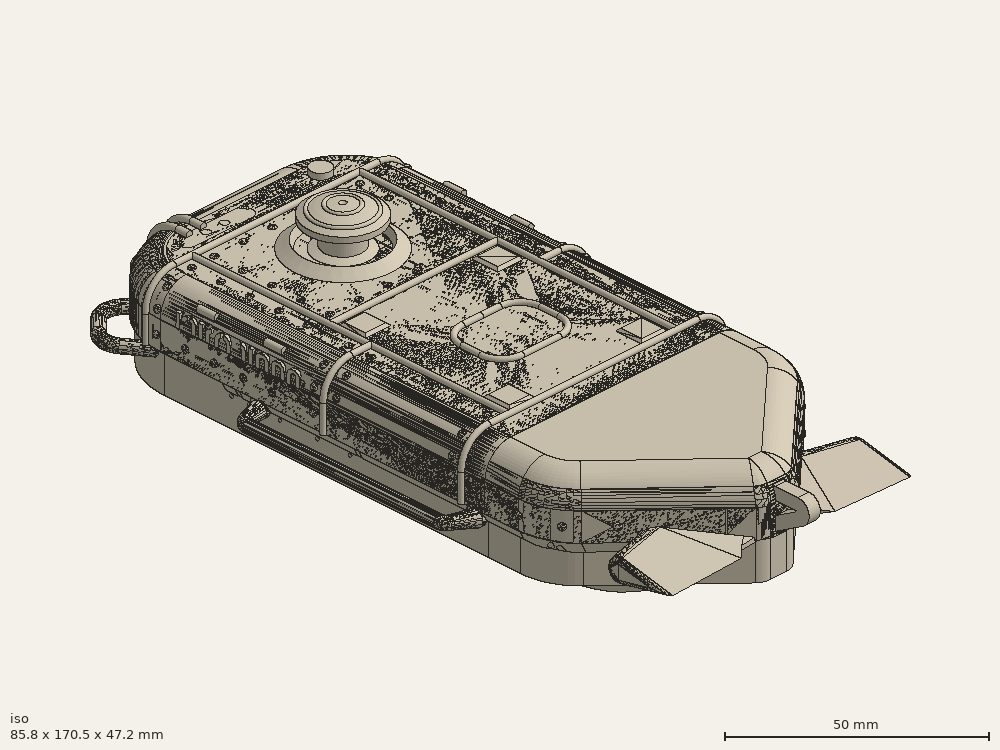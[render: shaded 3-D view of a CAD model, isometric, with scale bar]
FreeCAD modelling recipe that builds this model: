
FCSTD DOCUMENT  (FreeCAD 2022.709R26244 +5001 (Git))
Label: cq-80
License: All rights reserved
LicenseURL: http://en.wikipedia.org/wiki/All_rights_reserved
objects: Sketcher::SketchObject×173, PartDesign::Body×90, PartDesign::SubShapeBinder×79, PartDesign::Plane×57, PartDesign::Pad×45, Part::SubShapeBinder×44, PartDesign::ShapeBinder×41, PartDesign::FeatureBase×32, PartDesign::Pocket×29, PartDesign::Fillet×22, PartDesign::AdditivePipe×21, PartDesign::LinearPattern×16, PartDesign::Boolean×16, PartDesign::Mirrored×15, App::Part×14, PartDesign::MultiTransform×12, PartDesign::Line×12, Part::MultiFuse×11, PartDesign::Revolution×10, Part::Cut×8, +12 more types
note: 1204 computed .brp shape members not serialized (recipe doc carries the construction recipe); baked Part::Feature solids carry a one-line shape summary decoded from their .brp
EXTERNAL_REF file=cq-80-bottom.FCStd obj=Part

FEATURE [Sketcher::SketchObject] Sketch
  ArcFitTolerance = 0
  AttachmentSupport = -> [XY_Plane]
  FullyConstrained = true
  MapMode = 5
  Support = -> [XY_Plane]
  TreeRank = 6
  sketch-geometry (15):
    g0: LineSegment [constr] StartX=-35 StartY=53.5 StartZ=0 EndX=35 EndY=53.5 EndZ=0
    g1: LineSegment [constr] StartX=35 StartY=53.5 StartZ=0 EndX=35 EndY=-53.5 EndZ=0
    g2: LineSegment [constr] StartX=35 StartY=-53.5 StartZ=0 EndX=-35 EndY=-53.5 EndZ=0
    g3: LineSegment [constr] StartX=-35 StartY=-53.5 StartZ=0 EndX=-35 EndY=53.5 EndZ=0
    g4: LineSegment StartX=-35 StartY=-53.5 StartZ=0 EndX=-35 EndY=-69.5 EndZ=0
    g5: LineSegment [constr] StartX=-35 StartY=-69.5 StartZ=0 EndX=35 EndY=-69.5 EndZ=0
    g6: LineSegment StartX=35 StartY=-69.5 StartZ=0 EndX=35 EndY=-53.5 EndZ=0
    g7: LineSegment StartX=-35 StartY=-69.5 StartZ=0 EndX=-4.5 EndY=-97.9417 EndZ=0
    g8: LineSegment StartX=-4.5 StartY=-97.9417 StartZ=0 EndX=4.5 EndY=-97.9417 EndZ=0
    g9: LineSegment StartX=4.5 StartY=-97.9417 StartZ=0 EndX=35 EndY=-69.5 EndZ=0
    g10: LineSegment StartX=-15 StartY=53.5 StartZ=0 EndX=15 EndY=53.5 EndZ=0
    g11: LineSegment StartX=-35 StartY=33.5 StartZ=0 EndX=-35 EndY=-53.5 EndZ=0
    g12: LineSegment StartX=35 StartY=33.5 StartZ=0 EndX=35 EndY=-53.5 EndZ=0
    g13: ArcOfCircle CenterX=15 CenterY=33.5 CenterZ=0 NormalX=0 NormalY=0 NormalZ=1 AngleXU=0 Radius=20 StartAngle=1e-16 EndAngle=1.5708
    g14: ArcOfCircle CenterX=-15 CenterY=33.5 CenterZ=0 NormalX=0 NormalY=0 NormalZ=1 AngleXU=0 Radius=20 StartAngle=1.5708 EndAngle=3.14159
  constraints (39):
    c: Coincident(g0,g1)
    c: Coincident(g1,g2)
    c: Coincident(g2,g3)
    c: Coincident(g3,g0)
    c: Horizontal(g0)
    c: Horizontal(g2)
    c: Vertical(g1)
    c: Vertical(g3)
    c: DistanceX(g0,g0) = 70
    c: DistanceY(g3,g3) = 107
    c: Symmetric(g0,g2,g-1)
    c: Coincident(g2,g4)
    c: Vertical(g4)
    c: Coincident(g4,g5)
    c: Horizontal(g5)
    c: Coincident(g5,g6)
    c: Coincident(g6,g1)
    c: Vertical(g6)
    c: DistanceY(g4,g4) = 16
    c: Coincident(g4,g7)
    c: Coincident(g7,g8)
    c: Horizontal(g8)
    c: Coincident(g8,g9)
    c: Coincident(g9,g5)
    c: DistanceX(g8,g8) = 9
    c: Equal(g9,g7)
    c: Angle(g5,g9) = 0.750492
    c: Coincident(g11,g4)
    c: Coincident(g12,g6)
    c: Tangent(g14,g10) = 1.5708
    c: Tangent(g13,g10) = 1.5708
    c: Tangent(g12,g13) = 1.5708
    c: Tangent(g11,g14) = -1.5708
    c: Vertical(g12)
    c: Vertical(g11)
    c: Horizontal(g10)
    c: Radius(g14) = 20
    c: Radius(g13) = 20
    c: DistanceY(g-1,g10) = 53.5
FEATURE [PartDesign::Pad] Pad
  AddSubType = 0
  CheckUpToFaceLimits = true
  ClaimChildren = false
  Direction = (0,0,1)
  Fit = 0
  FitJoin = 0
  InnerFit = 0
  InnerFitJoin = 0
  InnerTaperAngle = 0
  InnerTaperAngleRev = 0
  Length = 14
  Length2 = 10
  NewSolid = false
  Profile = -> Sketch
  ReferenceAxis = -> Sketch [N_Axis]
  Suppress = false
  TreeRank = 6
  Type = 0
  _ProfileBasedVersion = 0
FEATURE [PartDesign::Fillet] Fillet001
  AddSubType = 0
  Base = -> Pad [Edge11,Edge14]
  BaseFeature = -> Pad
  NewSolid = false
  Radius = 4
  SupportTransform = false
  Suppress = false
  TreeRank = 6
FEATURE [PartDesign::Fillet] Fillet002
  AddSubType = 0
  Base = -> Fillet001 [Edge33,Edge3]
  BaseFeature = -> Fillet001
  NewSolid = false
  Radius = 16
  SupportTransform = false
  Suppress = false
  TreeRank = 6
FEATURE [PartDesign::Fillet] Fillet
  AddSubType = 0
  Base = -> Fillet002 [Face5]
  BaseFeature = -> Fillet002
  NewSolid = false
  Radius = 7
  SupportTransform = false
  Suppress = false
  TreeRank = 6
FEATURE [PartDesign::SubShapeBinder] Binder
  BindCopyOnChange = 0
  BindMode = 0
  ClaimChildren = false
  Context = -> Part [Part012.Body005.Binder.]
  FillStyle = 0
  Fuse = false
  MakeFace = true
  OffsetFill = false
  OffsetIntersection = false
  OffsetJoinType = 0
  OffsetOpenResult = false
  PartialLoad = false
  Relative = true
  Support = -> [Sketch]
  TreeRank = 6
  _Version = 2
FEATURE [PartDesign::SubShapeBinder] Binder004  label="Binder004(Fillet)..."
  BindCopyOnChange = 0
  BindMode = 0
  ClaimChildren = false
  Context = -> Part [Part012.Body006.Binder004.]
  FillStyle = 0
  Fuse = false
  MakeFace = true
  OffsetFill = false
  OffsetIntersection = false
  OffsetJoinType = 0
  OffsetOpenResult = false
  PartialLoad = false
  Relative = true
  Support = -> [Fillet[Edge67,Edge60]]
  TreeRank = 29
  _Version = 8
FEATURE [Sketcher::SketchObject] Sketch012
  ArcFitTolerance = 1e-06
  AttachmentSupport = -> [XY_Plane006]
  ExternalGeometry = -> [Binder004]
  FullyConstrained = true
  MapMode = 5
  Support = -> [XY_Plane006]
  TreeRank = 30
  sketch-geometry (2):
    g0: LineSegment StartX=-35 StartY=-53.5 StartZ=0 EndX=-35 EndY=-47.5 EndZ=0
    g1: LineSegment StartX=35 StartY=-53.5 StartZ=0 EndX=35 EndY=-47.5 EndZ=0
  constraints (6):
    c: Coincident(g0,g-3)
    c: Vertical(g0)
    c: DistanceY(g0,g0) = 6
    c: Coincident(g1,g-4)
    c: Vertical(g1)
    c: Equal(g1,g0)
FEATURE [PartDesign::Plane] DatumPlane001
  AttachmentSupport = -> [Sketch012]
  Length = 35
  MapMode = 7
  MinimumLength = 10
  MinimumWidth = 10
  Placement = pos=(-35,-53.5,0) rot=(1,0,0;1.5708rad)
  ResizeMode = 0
  Support = -> [Sketch012]
  TreeRank = 31
  Width = 10
FEATURE [PartDesign::SubShapeBinder] Binder005  label="Binder005(Sketch013)..."
  BindCopyOnChange = 0
  BindMode = 0
  ClaimChildren = false
  Context = -> Part [Part012.Body007.Binder005.]
  FillStyle = 0
  Fuse = false
  MakeFace = true
  OffsetFill = false
  OffsetIntersection = false
  OffsetJoinType = 0
  OffsetOpenResult = false
  PartialLoad = false
  Relative = true
  Support = -> [Body006[Sketch013.Edge5,Sketch013.Edge4,Sketch013.Edge3,Sketch013.Edge2,Sketch013.Edge1]]
  TreeRank = 47
  _Version = 8
FEATURE [Sketcher::SketchObject] Sketch015
  ArcFitTolerance = 1e-06
  AttachmentSupport = -> [XY_Plane007]
  ExternalGeometry = -> [Binder005]
  FullyConstrained = true
  MapMode = 5
  Support = -> [XY_Plane007]
  TreeRank = 48
  sketch-geometry (1):
    g0: LineSegment StartX=-35 StartY=-47.5 StartZ=0 EndX=-35 EndY=-10.5 EndZ=0
  constraints (3):
    c: Coincident(g0,g-3)
    c: Vertical(g0)
    c: DistanceY(g0,g0) = 37
FEATURE [PartDesign::Plane] DatumPlane002
  AttachmentSupport = -> [Sketch015]
  Length = 71.8
  MapMode = 7
  MinimumLength = 10
  MinimumWidth = 10
  Placement = pos=(-35,-10.5,0) rot=(1,0,0;1.5708rad)
  ResizeMode = 0
  Support = -> [Sketch015]
  TreeRank = 49
  Width = 14.9
FEATURE [Sketcher::SketchObject] Sketch016
  ArcFitTolerance = 1e-06
  AttachmentSupport = -> [DatumPlane002]
  ExternalGeometry = -> [Binder005]
  FullyConstrained = true
  MapMode = 5
  Placement = pos=(-35,-10.5,0) rot=(1,0,0;1.5708rad)
  Support = -> [DatumPlane002]
  TreeRank = 50
  sketch-geometry (8):
    g0: LineSegment StartX=0 StartY=0 StartZ=0 EndX=0 EndY=7 EndZ=0
    g1: LineSegment StartX=70 StartY=0 StartZ=0 EndX=70 EndY=7 EndZ=0
    g2: LineSegment [constr] StartX=63 StartY=14 StartZ=0 EndX=7 EndY=14 EndZ=0
    g3: ArcOfCircle CenterX=7 CenterY=7 CenterZ=0 NormalX=0 NormalY=0 NormalZ=1 AngleXU=0 Radius=7 StartAngle=1.5708 EndAngle=3.14159
    g4: ArcOfCircle CenterX=63 CenterY=7 CenterZ=0 NormalX=0 NormalY=0 NormalZ=1 AngleXU=0 Radius=7 StartAngle=1e-16 EndAngle=1.5708
    g5: LineSegment StartX=7 StartY=14 StartZ=0 EndX=12.5 EndY=14 EndZ=0
    g6: LineSegment StartX=57.5 StartY=14 StartZ=0 EndX=63 EndY=14 EndZ=0
    g7: LineSegment [constr] StartX=12.5 StartY=14 StartZ=0 EndX=57.5 EndY=14 EndZ=0
  constraints (21):
    c: Coincident(g0,g-3)
    c: Coincident(g0,g-4)
    c: Coincident(g1,g-7)
    c: Coincident(g1,g-7)
    c: Coincident(g2,g-6)
    c: Coincident(g2,g-5)
    c: Coincident(g3,g-4)
    c: Coincident(g3,g0)
    c: Coincident(g3,g2)
    c: Coincident(g4,g-6)
    c: Coincident(g4,g1)
    c: Coincident(g4,g2)
    c: Horizontal(g5)
    c: Horizontal(g6)
    c: Coincident(g5,g3)
    c: Coincident(g6,g4)
    c: Equal(g5,g6)
    c: Horizontal(g7)
    c: Coincident(g7,g5)
    c: Coincident(g7,g6)
    c: DistanceX(g7,g7) = 45
FEATURE [Sketcher::SketchObject] Sketch017
  ArcFitTolerance = 1e-06
  AttachmentSupport = -> [XY_Plane007]
  ExternalGeometry = -> [Sketch016]
  FullyConstrained = true
  MapMode = 5
  Support = -> [XY_Plane007]
  TreeRank = 51
  expr: Constraints[0] = Spreadsheet.groove_radius
  expr: Constraints[2] = Spreadsheet.groove_lift
  expr: Constraints[3] = Spreadsheet.groove_radius
  expr: Constraints[5] = Spreadsheet.groove_lift
  sketch-geometry (2):
    g0: Circle CenterX=-35.3 CenterY=-10.5 CenterZ=0 NormalX=0 NormalY=0 NormalZ=1 AngleXU=0 Radius=0.7
    g1: Circle CenterX=35.3 CenterY=-10.5 CenterZ=0 NormalX=0 NormalY=0 NormalZ=1 AngleXU=0 Radius=0.7
  constraints (6):
    c: Radius(g0) = 0.7
    c: Horizontal(g-3,g0)
    c: DistanceX(g0,g-3) = 0.3
    c: Radius(g1) = 0.7
    c: Horizontal(g1,g-4)
    c: DistanceX(g-4,g1) = 0.3
FEATURE [PartDesign::SubShapeBinder] Binder006  label="Binder006(Sketch017)"
  BindCopyOnChange = 0
  BindMode = 0
  ClaimChildren = false
  Context = -> Part [Part012.Body007.Binder006.]
  FillStyle = 0
  Fuse = false
  MakeFace = true
  OffsetFill = false
  OffsetIntersection = false
  OffsetJoinType = 0
  OffsetOpenResult = false
  PartialLoad = false
  Relative = true
  Support = -> [Sketch017[Edge1]]
  TreeRank = 53
  _Version = 8
FEATURE [PartDesign::AdditivePipe] Pipe002
  AddSubType = 0
  AuxilleryCurvelinear = true
  AuxillerySpineTangent = false
  Binormal = (0,0,0)
  ClaimChildren = false
  Fit = 0
  FitJoin = 0
  InnerFit = 0
  InnerFitJoin = 0
  Linearize = true
  Mode = 0
  NewSolid = false
  Profile = -> Binder006
  Spine = -> Sketch016 [Edge1,Edge2,Edge3]
  SpineTangent = false
  Suppress = false
  Transformation = 0
  Transition = 1
  TreeRank = 54
  _ProfileBasedVersion = 2
FEATURE [PartDesign::SubShapeBinder] Binder007  label="Binder007(Sketch017)"
  BindCopyOnChange = 0
  BindMode = 0
  ClaimChildren = false
  Context = -> Part [Part012.Body007.Binder007.]
  FillStyle = 0
  Fuse = false
  MakeFace = true
  OffsetFill = false
  OffsetIntersection = false
  OffsetJoinType = 0
  OffsetOpenResult = false
  PartialLoad = false
  Relative = true
  Support = -> [Sketch017[Edge2]]
  TreeRank = 56
  _Version = 8
FEATURE [PartDesign::AdditivePipe] Pipe003
  AddSubType = 0
  AuxilleryCurvelinear = true
  AuxillerySpineTangent = false
  BaseFeature = -> Pipe002
  Binormal = (0,0,0)
  ClaimChildren = false
  Fit = 0
  FitJoin = 0
  InnerFit = 0
  InnerFitJoin = 0
  Linearize = true
  Mode = 0
  NewSolid = false
  Profile = -> Binder007
  Spine = -> Sketch016 [Edge4,Edge5,Edge6]
  SpineTangent = false
  Suppress = false
  Transformation = 0
  Transition = 1
  TreeRank = 57
  _ProfileBasedVersion = 2
FEATURE [PartDesign::Body] Body007  label="middle side groove"
  AutoGroupSolids = false
  ClaimAllChildren = false
  ExportMode = 0
  Group = -> [Binder005,Sketch015,DatumPlane002,Sketch016,Sketch017,Pipe002,Binder006,Pipe003,Binder007]
  Origin = -> Origin007
  Tip = -> Pipe003
  TreeRank = 3234
  _ExportChildren = -> [Binder005,Sketch015,DatumPlane002,Sketch017,Pipe002,Pipe003]
  _GroupVersion = 1
FEATURE [PartDesign::SubShapeBinder] Binder008  label="Binder008(Sketch016)..."
  BindCopyOnChange = 0
  BindMode = 0
  ClaimChildren = false
  Context = -> Part [Part012.Body008.Binder008.]
  FillStyle = 0
  Fuse = false
  MakeFace = true
  OffsetFill = false
  OffsetIntersection = false
  OffsetJoinType = 0
  OffsetOpenResult = false
  PartialLoad = false
  Relative = true
  Support = -> [Body007[Sketch016.Edge3,Sketch016.Edge6]]
  TreeRank = 70
  _Version = 8
FEATURE [Sketcher::SketchObject] Sketch018
  ArcFitTolerance = 1e-06
  AttachmentSupport = -> [XY_Plane008]
  ExternalGeometry = -> [Binder008]
  FullyConstrained = true
  MapMode = 5
  Support = -> [XY_Plane008]
  TreeRank = 71
  sketch-geometry (1):
    g0: LineSegment StartX=-22.5 StartY=-10.5 StartZ=0 EndX=-22.5 EndY=0.5 EndZ=0
  constraints (3):
    c: Coincident(g0,g-3)
    c: Vertical(g0)
    c: DistanceY(g0,g0) = 11
FEATURE [PartDesign::Plane] DatumPlane003
  AttachmentSupport = -> [Sketch018]
  Length = 22.5
  MapMode = 7
  MinimumLength = 10
  MinimumWidth = 10
  Placement = pos=(-22.5,0.5,0) rot=(1,0,0;1.5708rad)
  ResizeMode = 0
  Support = -> [Sketch018]
  TreeRank = 72
  Width = 10
FEATURE [Sketcher::SketchObject] Sketch019
  ArcFitTolerance = 1e-06
  AttachmentSupport = -> [DatumPlane003]
  ExternalGeometry = -> [Binder008]
  FullyConstrained = true
  MapMode = 5
  Placement = pos=(-22.5,0.5,0) rot=(1,0,0;1.5708rad)
  Support = -> [DatumPlane003]
  TreeRank = 73
  sketch-geometry (1):
    g0: LineSegment StartX=0 StartY=14 StartZ=0 EndX=45 EndY=14 EndZ=0
  constraints (2):
    c: Coincident(g0,g-3)
    c: Coincident(g0,g-3)
FEATURE [PartDesign::Plane] DatumPlane004
  AttachmentSupport = -> [Sketch019]
  Length = 10
  MapMode = 7
  MinimumLength = 10
  MinimumWidth = 10
  Placement = pos=(-22.5,0.5,14) rot=(0.57735,-0.57735,-0.57735;2.0944rad)
  ResizeMode = 0
  Support = -> [Sketch019]
  TreeRank = 74
  Width = 10
FEATURE [Sketcher::SketchObject] Sketch020
  ArcFitTolerance = 1e-06
  AttachmentSupport = -> [DatumPlane004]
  FullyConstrained = true
  MapMode = 5
  Placement = pos=(-22.5,0.5,14) rot=(0.57735,-0.57735,-0.57735;2.0944rad)
  Support = -> [DatumPlane004]
  TreeRank = 75
  expr: Constraints[1] = Spreadsheet.groove_radius
  expr: Constraints[2] = Spreadsheet.groove_lift
  sketch-geometry (1):
    g0: Circle CenterX=0 CenterY=0.3 CenterZ=0 NormalX=0 NormalY=0 NormalZ=1 AngleXU=0 Radius=0.7
  constraints (3):
    c: Vertical(g0,g-1)
    c: Radius(g0) = 0.7
    c: DistanceY(g-1,g0) = 0.3
FEATURE [Spreadsheet::Sheet] Spreadsheet
  PythonMode = false
  ShowCells = 0
  TreeRank = 0
  cells = A1=groove_radius; B1(groove_radius)=0.7; A2=groove_lift; B2(groove_lift)=0.3; A3=bump_radius; B3(bump_radius)=0.8; A4=bump_sink; B4(bump_sink)=0.3; A5=middle_thickness; B5(middle_thickness)=10; A6=top_shell_width; B6(top_shell_width)=1; A7=bottom_shell_width; B7(bottom_shell_width)=1; A8=card_len; B8(card_len)=53.98; A9=card_thickness; B9(card_thickness)=1.2; C9=card nominal: 0.68-0.84; A10=thumbstick_width; B10(thumbstick_width)=9.68; A11=side_emboss_thickness; B11(side_emboss_thickness)=1; A12=side_bar_len; B12(side_bar_len)=58; A13=bottom_bump_polar_angle; B13(bottom_bump_polar_angle)=123.22; A14=bottom_groove_revolve_angle; B14(bottom_groove_revolve_angle)=133.24; A15=bottom_groove_len; B15(bottom_groove_len)=64
FEATURE [PartDesign::AdditivePipe] Pipe004
  AddSubType = 0
  AuxilleryCurvelinear = true
  AuxillerySpineTangent = false
  Binormal = (0,0,0)
  ClaimChildren = false
  Fit = 0
  FitJoin = 0
  InnerFit = 0
  InnerFitJoin = 0
  Linearize = true
  Mode = 0
  NewSolid = false
  Placement = pos=(-22.5,0.5,14) rot=(0.57735,-0.57735,-0.57735;2.0944rad)
  Profile = -> Sketch020
  Spine = -> Sketch019 [Edge1]
  SpineTangent = false
  Suppress = false
  Transformation = 0
  Transition = 1
  TreeRank = 77
  _ProfileBasedVersion = 2
FEATURE [PartDesign::Body] Body008  label="middle groove"
  AutoGroupSolids = false
  ClaimAllChildren = false
  ExportMode = 0
  Group = -> [Binder008,Sketch018,DatumPlane003,Sketch019,DatumPlane004,Sketch020,Pipe004]
  Origin = -> Origin008
  Tip = -> Pipe004
  TreeRank = 3238
  _ExportChildren = -> [Binder008,Sketch018,DatumPlane003,DatumPlane004,Pipe004]
  _GroupVersion = 1
FEATURE [PartDesign::SubShapeBinder] Binder009  label="Binder009(Sketch019)"
  BindCopyOnChange = 0
  BindMode = 0
  ClaimChildren = false
  Context = -> Part [Part012.Body009.Binder009.]
  FillStyle = 0
  Fuse = false
  MakeFace = true
  OffsetFill = false
  OffsetIntersection = false
  OffsetJoinType = 0
  OffsetOpenResult = false
  PartialLoad = false
  Relative = true
  Support = -> [Body008[Sketch019.]]
  TreeRank = 90
  _Version = 8
FEATURE [PartDesign::SubShapeBinder] Binder010  label="Binder010(Sketch013)"
  BindCopyOnChange = 0
  BindMode = 0
  ClaimChildren = false
  Context = -> Part [Part012.Body009.Binder010.]
  FillStyle = 0
  Fuse = false
  MakeFace = true
  OffsetFill = false
  OffsetIntersection = false
  OffsetJoinType = 0
  OffsetOpenResult = false
  PartialLoad = false
  Relative = true
  Support = -> [Body006[Sketch013.]]
  TreeRank = 91
  _Version = 8
FEATURE [PartDesign::SubShapeBinder] Binder011  label="Binder011(Sketch010)"
  BindCopyOnChange = 0
  BindMode = 0
  ClaimChildren = false
  Context = -> Part [Part012.Body009.Binder011.]
  FillStyle = 0
  Fuse = false
  MakeFace = true
  OffsetFill = false
  OffsetIntersection = false
  OffsetJoinType = 0
  OffsetOpenResult = false
  PartialLoad = false
  Relative = true
  Support = -> [Body005[Sketch010.]]
  TreeRank = 92
  _Version = 8
FEATURE [PartDesign::Plane] DatumPlane005
  AttachmentSupport = -> [Binder011,Binder009]
  Length = 10
  MapMode = 13
  MinimumLength = 10
  MinimumWidth = 10
  Placement = pos=(-9.12311,12.8333,14) rot=(0,0,1;0rad)
  ResizeMode = 0
  Support = -> [Binder011,Binder009]
  TreeRank = 93
  Width = 12.8333
FEATURE [Sketcher::SketchObject] Sketch021
  ArcFitTolerance = 1e-06
  AttachmentSupport = -> [DatumPlane005]
  ExternalGeometry = -> [Binder011,Binder010]
  FullyConstrained = true
  MapMode = 5
  Placement = pos=(-9.12311,12.8333,14) rot=(0,0,1;0rad)
  Support = -> [DatumPlane005]
  TreeRank = 94
  sketch-geometry (7):
    g0: LineSegment StartX=-13.3769 StartY=24.6667 StartZ=0 EndX=-13.3769 EndY=-60.3333 EndZ=0
    g1: LineSegment StartX=31.6231 StartY=24.6667 StartZ=0 EndX=31.6231 EndY=-60.3333 EndZ=0
    g2: LineSegment [constr] StartX=-13.3769 StartY=-40.3333 StartZ=0 EndX=31.6231 EndY=-40.3333 EndZ=0
    g3: LineSegment [constr] StartX=-18.8769 StartY=-60.3333 StartZ=0 EndX=9.12311 EndY=-60.3333 EndZ=0
    g4: LineSegment [constr] StartX=9.12311 StartY=-60.3333 StartZ=0 EndX=37.1231 EndY=-60.3333 EndZ=0
    g5: LineSegment [constr] StartX=-13.3769 StartY=-60.3333 StartZ=0 EndX=9.12311 EndY=-60.3333 EndZ=0
    g6: LineSegment [constr] StartX=9.12311 StartY=-60.3333 StartZ=0 EndX=31.6231 EndY=-60.3333 EndZ=0
  constraints (21):
    c: Vertical(g0)
    c: Vertical(g1)
    c: Equal(g0,g1)
    c: Horizontal(g0,g-3)
    c: PointOnObject(g2,g0)
    c: PointOnObject(g2,g1)
    c: Horizontal(g2)
    c: DistanceX(g2,g2) = 45
    c: DistanceY(g0,g2) = 20
    c: Horizontal(g1,g0)
    c: Horizontal(g0,g-4)
    c: Coincident(g3,g-4)
    c: PointOnObject(g3,g-4)
    c: Coincident(g4,g3)
    c: Coincident(g4,g-4)
    c: Equal(g3,g4)
    c: Coincident(g5,g0)
    c: Coincident(g5,g3)
    c: Coincident(g6,g3)
    c: Coincident(g6,g1)
    c: Equal(g5,g6)
FEATURE [PartDesign::Plane] DatumPlane006
  AttachmentSupport = -> [Sketch021]
  Length = 46.2
  MapMode = 7
  MinimumLength = 10
  MinimumWidth = 10
  Placement = pos=(-22.5,37.5,14) rot=(0,0.707107,0.707107;3.14159rad)
  ResizeMode = 0
  Support = -> [Sketch021]
  TreeRank = 95
  Width = 10
FEATURE [Sketcher::SketchObject] Sketch022
  ArcFitTolerance = 1e-06
  AttachmentSupport = -> [DatumPlane006]
  ExternalGeometry = -> [Sketch021]
  FullyConstrained = true
  MapMode = 5
  Placement = pos=(-22.5,37.5,14) rot=(0,0.707107,0.707107;3.14159rad)
  Support = -> [DatumPlane006]
  TreeRank = 96
  expr: Constraints[2] = Spreadsheet.groove_radius
  expr: Constraints[3] = Spreadsheet.groove_radius
  expr: Constraints[4] = Spreadsheet.groove_lift
  expr: Constraints[5] = Spreadsheet.groove_lift
  sketch-geometry (2):
    g0: Circle CenterX=0 CenterY=0.3 CenterZ=0 NormalX=0 NormalY=0 NormalZ=1 AngleXU=0 Radius=0.7
    g1: Circle CenterX=-45 CenterY=0.3 CenterZ=0 NormalX=0 NormalY=0 NormalZ=1 AngleXU=0 Radius=0.7
  constraints (6):
    c: Vertical(g-3,g0)
    c: Vertical(g-5,g1)
    c: Radius(g0) = 0.7
    c: Radius(g1) = 0.7
    c: DistanceY(g-3,g0) = 0.3
    c: DistanceY(g-5,g1) = 0.3
FEATURE [PartDesign::SubShapeBinder] Binder012  label="Binder012(Sketch022)"
  BindCopyOnChange = 0
  BindMode = 0
  ClaimChildren = false
  Context = -> Part [Part012.Body009.Binder012.]
  FillStyle = 0
  Fuse = false
  MakeFace = true
  OffsetFill = false
  OffsetIntersection = false
  OffsetJoinType = 0
  OffsetOpenResult = false
  PartialLoad = false
  Relative = true
  Support = -> [Sketch022[Edge1]]
  TreeRank = 98
  _Version = 8
FEATURE [PartDesign::AdditivePipe] Pipe005
  AddSubType = 0
  AuxilleryCurvelinear = true
  AuxillerySpineTangent = false
  Binormal = (0,0,0)
  ClaimChildren = false
  Fit = 0
  FitJoin = 0
  InnerFit = 0
  InnerFitJoin = 0
  Linearize = true
  Mode = 0
  NewSolid = false
  Profile = -> Binder012
  Spine = -> Sketch021 [Edge1]
  SpineTangent = false
  Suppress = false
  Transformation = 0
  Transition = 1
  TreeRank = 99
  _ProfileBasedVersion = 2
FEATURE [PartDesign::SubShapeBinder] Binder013  label="Binder013(Sketch022)"
  BindCopyOnChange = 0
  BindMode = 0
  ClaimChildren = false
  Context = -> Part [Part012.Body009.Binder013.]
  FillStyle = 0
  Fuse = false
  MakeFace = true
  OffsetFill = false
  OffsetIntersection = false
  OffsetJoinType = 0
  OffsetOpenResult = false
  PartialLoad = false
  Relative = true
  Support = -> [Sketch022[Edge2]]
  TreeRank = 101
  _Version = 8
FEATURE [PartDesign::Body] Body009  label="left groove"
  AutoGroupSolids = false
  ClaimAllChildren = false
  ExportMode = 0
  Group = -> [Binder009,Binder010,Binder011,DatumPlane005,Sketch021,DatumPlane006,Sketch022,Pipe005,Binder012,Binder013]
  Origin = -> Origin009
  Tip = -> Pipe005
  TreeRank = 3246
  _ExportChildren = -> [Binder009,Binder010,Binder011,DatumPlane005,DatumPlane006,Sketch022,Pipe005,Binder013]
  _GroupVersion = 1
FEATURE [PartDesign::Plane] DatumPlane007
  AttachmentSupport = -> [Sketch012]
  Length = 71.8
  MapMode = 7
  MinimumLength = 10
  MinimumWidth = 10
  Placement = pos=(-35,-47.5,0) rot=(1,0,0;1.5708rad)
  ResizeMode = 0
  Support = -> [Sketch012]
  TreeRank = 103
  Width = 14.9
FEATURE [Sketcher::SketchObject] Sketch013
  ArcFitTolerance = 1e-06
  AttachmentSupport = -> [DatumPlane007]
  ExternalGeometry = -> [Binder004,Sketch012]
  FullyConstrained = true
  MapMode = 5
  Placement = pos=(-35,-47.5,0) rot=(1,0,0;1.5708rad)
  Support = -> [DatumPlane007]
  TreeRank = 32
  sketch-geometry (5):
    g0: ArcOfCircle CenterX=7 CenterY=7 CenterZ=0 NormalX=0 NormalY=0 NormalZ=1 AngleXU=0 Radius=7 StartAngle=1.5708 EndAngle=3.14159
    g1: ArcOfCircle CenterX=63 CenterY=7 CenterZ=0 NormalX=0 NormalY=0 NormalZ=1 AngleXU=0 Radius=7 StartAngle=0 EndAngle=1.5708
    g2: LineSegment StartX=7 StartY=14 StartZ=0 EndX=63 EndY=14 EndZ=0
    g3: LineSegment StartX=70 StartY=7 StartZ=0 EndX=70 EndY=9e-16 EndZ=0
    g4: LineSegment StartX=0 StartY=7 StartZ=0 EndX=0 EndY=9e-16 EndZ=0
  constraints (12):
    c: Coincident(g0,g-3)
    c: Coincident(g0,g-3)
    c: Coincident(g0,g-3)
    c: Coincident(g1,g-4)
    c: Coincident(g1,g-4)
    c: Coincident(g1,g-4)
    c: Coincident(g2,g0)
    c: Coincident(g2,g1)
    c: Coincident(g3,g1)
    c: Coincident(g3,g-6)
    c: Coincident(g4,g0)
    c: Coincident(g4,g-5)
FEATURE [Sketcher::SketchObject] Sketch014
  ArcFitTolerance = 1e-06
  AttachmentSupport = -> [XY_Plane006]
  ExternalGeometry = -> [Sketch013]
  FullyConstrained = true
  MapMode = 5
  Support = -> [XY_Plane006]
  TreeRank = 33
  expr: Constraints[0] = Spreadsheet.groove_radius
  expr: Constraints[2] = Spreadsheet.groove_lift
  sketch-geometry (1):
    g0: Circle CenterX=-35.3 CenterY=-47.5 CenterZ=0 NormalX=0 NormalY=0 NormalZ=1 AngleXU=0 Radius=0.7
  constraints (3):
    c: Radius(g0) = 0.7
    c: Horizontal(g-3,g0)
    c: DistanceX(g0,g-3) = 0.3
FEATURE [PartDesign::AdditivePipe] Pipe001
  AddSubType = 0
  AuxilleryCurvelinear = true
  AuxillerySpineTangent = false
  Binormal = (0,0,0)
  ClaimChildren = false
  Fit = 0
  FitJoin = 0
  InnerFit = 0
  InnerFitJoin = 0
  Linearize = true
  Mode = 0
  NewSolid = false
  Profile = -> Sketch014
  Spine = -> Sketch013 [Edge5,Edge4,Edge3,Edge2,Edge1]
  SpineTangent = false
  Suppress = false
  Transformation = 0
  Transition = 1
  TreeRank = 34
  _ProfileBasedVersion = 2
FEATURE [PartDesign::Body] Body006  label="bottom groove"
  AutoGroupSolids = false
  ClaimAllChildren = false
  ExportMode = 0
  Group = -> [Binder004,Sketch012,DatumPlane001,Sketch013,Sketch014,Pipe001,DatumPlane007]
  Origin = -> Origin006
  Tip = -> Pipe001
  TreeRank = 3250
  _ExportChildren = -> [Binder004,Sketch012,DatumPlane001,Pipe001,DatumPlane007]
  _GroupVersion = 1
FEATURE [PartDesign::SubShapeBinder] Binder015  label="Binder015(Sketch019)"
  BindCopyOnChange = 0
  BindMode = 0
  ClaimChildren = false
  Context = -> Part [Part004.Body011.Binder015.]
  FillStyle = 0
  Fuse = false
  MakeFace = true
  OffsetFill = false
  OffsetIntersection = false
  OffsetJoinType = 0
  OffsetOpenResult = false
  PartialLoad = false
  Relative = true
  Support = -> [Body008[Sketch019.]]
  TreeRank = 129
  _Version = 8
FEATURE [PartDesign::SubShapeBinder] Binder016  label="Binder016(Sketch013)"
  BindCopyOnChange = 0
  BindMode = 0
  ClaimChildren = false
  Context = -> Part [Part004.Body011.Binder016.]
  FillStyle = 0
  Fuse = false
  MakeFace = true
  OffsetFill = false
  OffsetIntersection = false
  OffsetJoinType = 0
  OffsetOpenResult = false
  PartialLoad = false
  Relative = true
  Support = -> [Body006[Sketch013.]]
  TreeRank = 130
  _Version = 8
FEATURE [PartDesign::ShapeBinder] ShapeBinder
  Placement = pos=(-9.12311,12.8333,14) rot=(0,0,1;0rad)
  Support = -> [Sketch021]
  TraceSupport = false
  TreeRank = 209
FEATURE [PartDesign::Plane] DatumPlane008
  AttachmentSupport = -> [ShapeBinder,Binder015,Binder016]
  Length = 10
  MapMode = 45
  MinimumLength = 10
  MinimumWidth = 10
  Placement = pos=(1.921e-13,-12.869,14) rot=(0,0,1;0rad)
  ResizeMode = 0
  Support = -> [ShapeBinder,Binder015,Binder016]
  TreeRank = 133
  Width = 12.869
FEATURE [Sketcher::SketchObject] Sketch023
  ArcFitTolerance = 1e-06
  AttachmentSupport = -> [DatumPlane008]
  ExternalGeometry = -> [Binder016,ShapeBinder]
  FullyConstrained = true
  MapMode = 5
  Placement = pos=(1.921e-13,-12.869,14) rot=(0,0,1;0rad)
  Support = -> [DatumPlane008]
  TreeRank = 132
  sketch-geometry (4):
    g0: LineSegment StartX=-21.3 StartY=-26.431 StartZ=0 EndX=-14.3 EndY=-26.431 EndZ=0
    g1: LineSegment StartX=-14.3 StartY=-26.431 StartZ=0 EndX=-14.3 EndY=-33.431 EndZ=0
    g2: LineSegment StartX=-14.3 StartY=-33.431 StartZ=0 EndX=-21.3 EndY=-33.431 EndZ=0
    g3: LineSegment StartX=-21.3 StartY=-33.431 StartZ=0 EndX=-21.3 EndY=-26.431 EndZ=0
  constraints (12):
    c: Coincident(g0,g1)
    c: Coincident(g1,g2)
    c: Coincident(g2,g3)
    c: Coincident(g3,g0)
    c: Horizontal(g0)
    c: Horizontal(g2)
    c: Vertical(g1)
    c: Vertical(g3)
    c: DistanceX(g-4,g2) = 1.2
    c: DistanceY(g-4,g2) = 1.2
    c: DistanceY(g3,g3) = 7
    c: Equal(g3,g2)
FEATURE [Sketcher::SketchObject] Sketch025
  ArcFitTolerance = 1e-06
  AttachmentSupport = -> [DatumPlane008]
  ExternalGeometry = -> [Binder015,ShapeBinder]
  FullyConstrained = true
  MapMode = 5
  Placement = pos=(1.921e-13,-12.869,14) rot=(0,0,1;0rad)
  Support = -> [DatumPlane008]
  TreeRank = 135
  sketch-geometry (4):
    g0: LineSegment StartX=-22.5 StartY=13.369 StartZ=0 EndX=-4.334e-13 EndY=-10.631 EndZ=0
    g1: LineSegment StartX=-4.324e-13 StartY=-10.631 StartZ=0 EndX=22.5 EndY=-34.631 EndZ=0
    g2: LineSegment StartX=-4.324e-13 StartY=-10.631 StartZ=0 EndX=-4.324e-13 EndY=-20.631 EndZ=0
    g3: LineSegment StartX=-4.324e-13 StartY=-10.631 StartZ=0 EndX=-10 EndY=-10.631 EndZ=0
  constraints (11):
    c: Coincident(g0,g-3)
    c: Coincident(g0,g1)
    c: Coincident(g1,g-5)
    c: Parallel(g1,g0)
    c: Equal(g0,g1)
    c: Coincident(g2,g0)
    c: Vertical(g2)
    c: DistanceY(g2,g2) = 10
    c: Coincident(g3,g0)
    c: Horizontal(g3)
    c: DistanceX(g3,g3) = 10
FEATURE [PartDesign::Pad] Pad005
  AddSubType = 0
  AlongSketchNormal = false
  CheckUpToFaceLimits = true
  ClaimChildren = false
  Direction = (0,3e-16,1)
  Fit = 0
  FitJoin = 0
  InnerFit = 0
  InnerFitJoin = 0
  InnerTaperAngle = 0
  InnerTaperAngleRev = 0
  Length = 0.7
  Length2 = 100
  Linearize = true
  NewSolid = false
  Placement = pos=(1.921e-13,-12.869,14) rot=(0,0,1;0rad)
  Profile = -> Sketch023
  Suppress = false
  TreeRank = 136
  Type = 0
  _ProfileBasedVersion = 1
FEATURE [PartDesign::Plane] DatumPlane010
  AttachmentSupport = -> [Sketch025]
  Length = 70
  MapMode = 7
  MinimumLength = 10
  MinimumWidth = 10
  Placement = pos=(-1.6e-15,-23.5,14) rot=(0,0.707107,0.707107;3.14159rad)
  ResizeMode = 0
  Support = -> [Sketch025]
  TreeRank = 140
  Width = 14.6
FEATURE [PartDesign::SubShapeBinder] Binder017  label="Binder017(*Sketch019)..."
  BindCopyOnChange = 0
  BindMode = 0
  ClaimChildren = false
  Context = -> Part [Part012.Body012.Binder017.]
  FillStyle = 0
  Fuse = false
  MakeFace = true
  OffsetFill = false
  OffsetIntersection = false
  OffsetJoinType = 0
  OffsetOpenResult = false
  PartialLoad = false
  Relative = true
  Support = -> [Body009[Binder009.,Binder010.,Binder011.]]
  TreeRank = 154
  _Version = 8
FEATURE [PartDesign::Plane] DatumPlane011
  AttachmentSupport = -> [Binder017]
  Length = 10
  MapMode = 13
  MinimumLength = 10
  MinimumWidth = 10
  Placement = pos=(-9.12311,12.8333,14) rot=(0,0,1;0rad)
  ResizeMode = 0
  Support = -> [Binder017]
  TreeRank = 155
  Width = 12.8333
FEATURE [Part::SubShapeBinder] Import  label="Import(*Sketch019...)"
  BindCopyOnChange = 0
  BindMode = 0
  ClaimChildren = false
  Context = -> Part [Part012.Body012.Import.]
  FillStyle = 0
  Fuse = false
  MakeFace = false
  OffsetFill = false
  OffsetIntersection = false
  OffsetJoinType = 0
  OffsetOpenResult = false
  PartialLoad = false
  Relative = true
  Support = -> [Binder017]
  TreeRank = 157
  _Version = 8
FEATURE [Sketcher::SketchObject] Sketch026
  ArcFitTolerance = 1e-06
  AttachmentSupport = -> [DatumPlane011]
  ExternalGeometry = -> [Import]
  FullyConstrained = true
  MapMode = 5
  Placement = pos=(-9.12311,12.8333,14) rot=(0,0,1;0rad)
  Support = -> [DatumPlane011]
  TreeRank = 156
  sketch-geometry (1):
    g0: LineSegment StartX=31.6231 StartY=24.6667 StartZ=0 EndX=31.6231 EndY=-60.3333 EndZ=0
  constraints (4):
    c: Vertical(g0)
    c: PointOnObject(g-3,g0)
    c: Horizontal(g-4,g0)
    c: Horizontal(g-5,g0)
FEATURE [PartDesign::Plane] DatumPlane012
  AttachmentSupport = -> [Sketch026]
  Length = 10
  MapMode = 7
  MinimumLength = 10
  MinimumWidth = 10
  Placement = pos=(22.5,37.5,14) rot=(0,0.707107,0.707107;3.14159rad)
  ResizeMode = 0
  Support = -> [Sketch026]
  TreeRank = 158
  Width = 10
FEATURE [Sketcher::SketchObject] Sketch027
  ArcFitTolerance = 1e-06
  AttachmentSupport = -> [DatumPlane012]
  FullyConstrained = true
  MapMode = 5
  Placement = pos=(22.5,37.5,14) rot=(0,0.707107,0.707107;3.14159rad)
  Support = -> [DatumPlane012]
  TreeRank = 159
  expr: Constraints[1] = Spreadsheet.groove_radius
  expr: Constraints[2] = Spreadsheet.groove_lift
  sketch-geometry (1):
    g0: Circle CenterX=0 CenterY=0.3 CenterZ=0 NormalX=0 NormalY=0 NormalZ=1 AngleXU=0 Radius=0.7
  constraints (3):
    c: Vertical(g0,g-1)
    c: Radius(g0) = 0.7
    c: DistanceY(g-1,g0) = 0.3
FEATURE [PartDesign::AdditivePipe] Pipe007
  AddSubType = 0
  AuxilleryCurvelinear = true
  AuxillerySpineTangent = false
  Binormal = (0,0,0)
  ClaimChildren = false
  Fit = 0
  FitJoin = 0
  InnerFit = 0
  InnerFitJoin = 0
  Linearize = true
  Mode = 0
  NewSolid = false
  Placement = pos=(22.5,37.5,14) rot=(0,0.707107,0.707107;3.14159rad)
  Profile = -> Sketch027
  Spine = -> Sketch026 [Edge1]
  SpineTangent = false
  Suppress = false
  Transformation = 0
  Transition = 1
  TreeRank = 160
  _ProfileBasedVersion = 2
FEATURE [PartDesign::Body] Body012  label="right groove"
  AutoGroupSolids = false
  ClaimAllChildren = false
  ExportMode = 0
  Group = -> [Sketch026,Import,DatumPlane012,Sketch027,Pipe007,Binder017,DatumPlane011]
  Origin = -> Origin012
  Tip = -> Pipe007
  TreeRank = 3242
  _ExportChildren = -> [Import,DatumPlane012,Pipe007,Binder017,DatumPlane011]
  _GroupVersion = 1
FEATURE [PartDesign::SubShapeBinder] Binder018  label="Binder018(Sketch019)"
  BindCopyOnChange = 0
  BindMode = 0
  ClaimChildren = false
  Context = -> Part [Part006.Body.Binder018.]
  FillStyle = 0
  Fuse = false
  MakeFace = true
  OffsetFill = false
  OffsetIntersection = false
  OffsetJoinType = 0
  OffsetOpenResult = false
  PartialLoad = false
  Relative = true
  Support = -> [Body008[Sketch019.]]
  TreeRank = 186
  _Version = 8
FEATURE [PartDesign::ShapeBinder] ShapeBinder001
  Placement = pos=(-9.12311,12.8333,14) rot=(0,0,1;0rad)
  Support = -> [Sketch021]
  TraceSupport = false
  TreeRank = 187
FEATURE [PartDesign::Plane] DatumPlane014
  AttachmentSupport = -> [Fillet]
  Length = 10
  MapMode = 5
  MinimumLength = 10
  MinimumWidth = 10
  Placement = pos=(0,0,14) rot=(0,0,1;0rad)
  ResizeMode = 0
  Support = -> [Fillet]
  TreeRank = 189
  Width = 10
FEATURE [Sketcher::SketchObject] Sketch028
  ArcFitTolerance = 1e-06
  AttachmentSupport = -> [DatumPlane014]
  ExternalGeometry = -> [Binder018,ShapeBinder001]
  FullyConstrained = true
  MapMode = 5
  Placement = pos=(0,0,14) rot=(0,0,1;0rad)
  Support = -> [DatumPlane014]
  TreeRank = 165
  sketch-geometry (4):
    g0: LineSegment StartX=-21.2 StartY=-39.5 StartZ=0 EndX=-14.5 EndY=-39.5 EndZ=0
    g1: LineSegment StartX=-14.5 StartY=-39.5 StartZ=0 EndX=-14.5 EndY=-46.2 EndZ=0
    g2: LineSegment StartX=-14.5 StartY=-46.2 StartZ=0 EndX=-21.2 EndY=-46.2 EndZ=0
    g3: LineSegment StartX=-21.2 StartY=-46.2 StartZ=0 EndX=-21.2 EndY=-39.5 EndZ=0
  constraints (12):
    c: Coincident(g0,g1)
    c: Coincident(g1,g2)
    c: Coincident(g2,g3)
    c: Coincident(g3,g0)
    c: Horizontal(g0)
    c: Horizontal(g2)
    c: Vertical(g1)
    c: Vertical(g3)
    c: DistanceX(g-5,g2) = 1.3
    c: DistanceY(g-5,g2) = 1.3
    c: DistanceX(g2,g2) = 6.7
    c: DistanceY(g1,g1) = 6.7
FEATURE [Sketcher::SketchObject] Sketch029
  ArcFitTolerance = 1e-06
  AttachmentSupport = -> [DatumPlane014]
  ExternalGeometry = -> [Binder018,ShapeBinder001]
  FullyConstrained = true
  MapMode = 5
  Placement = pos=(0,0,14) rot=(0,0,1;0rad)
  Support = -> [DatumPlane014]
  TreeRank = 191
  sketch-geometry (4):
    g0: LineSegment StartX=-22.5 StartY=0.5 StartZ=0 EndX=0 EndY=-23.5 EndZ=0
    g1: LineSegment StartX=0 StartY=-23.5 StartZ=0 EndX=22.5 EndY=-47.5 EndZ=0
    g2: LineSegment StartX=0 StartY=-23.5 StartZ=0 EndX=0 EndY=-33.5 EndZ=0
    g3: LineSegment StartX=0 StartY=-23.5 StartZ=0 EndX=-10 EndY=-23.5 EndZ=0
  constraints (11):
    c: Coincident(g0,g-3)
    c: Coincident(g0,g1)
    c: Coincident(g1,g-4)
    c: Parallel(g1,g0)
    c: Equal(g0,g1)
    c: Coincident(g2,g0)
    c: Vertical(g2)
    c: Coincident(g3,g0)
    c: Horizontal(g3)
    c: DistanceY(g2,g2) = 10
    c: DistanceX(g3,g3) = 10
FEATURE [PartDesign::Plane] DatumPlane016
  AttachmentSupport = -> [Sketch029]
  Length = 70
  MapMode = 7
  MinimumLength = 10
  MinimumWidth = 10
  Placement = pos=(0,-23.5,14) rot=(0,0.707107,0.707107;3.14159rad)
  ResizeMode = 0
  Support = -> [Sketch029]
  TreeRank = 193
  Width = 14
FEATURE [PartDesign::Body] Body  label="top master"
  AutoGroupSolids = false
  ClaimAllChildren = false
  ExportMode = 0
  Group = -> [Sketch,Pad,Fillet001,Fillet002,Fillet,Binder018,ShapeBinder001,DatumPlane014,Sketch028,DatumPlane016,Sketch029]
  Origin = -> Origin
  Tip = -> Fillet
  TreeRank = 1
  _ExportChildren = -> [Pad,Fillet001,Fillet002,Fillet,Binder018,ShapeBinder001,DatumPlane014,Sketch028,DatumPlane016,Sketch029]
  _GroupVersion = 1
FEATURE [PartDesign::Mirrored] Mirrored002
  AddSubType = 0
  CopyShape = false
  MirrorPlane = -> Sketch023 [V_Axis]
  NewSolid = false
  ParallelTransform = true
  Placement = pos=(1.921e-13,-12.869,14) rot=(0,0,1;0rad)
  SubTransform = true
  Suppress = false
  TreeRank = 202
  _Version = 3
FEATURE [PartDesign::Mirrored] Mirrored003
  AddSubType = 0
  CopyShape = false
  MirrorPlane = -> DatumPlane010
  NewSolid = false
  ParallelTransform = true
  Placement = pos=(1.921e-13,-12.869,14) rot=(0,0,1;0rad)
  SubTransform = true
  Suppress = false
  TreeRank = 203
  _Version = 3
FEATURE [PartDesign::MultiTransform] MultiTransform001
  AddSubType = 0
  BaseFeature = -> Pad005
  CopyShape = false
  NewSolid = false
  OriginalSubs = -> [Pad005]
  Originals = -> [Pad005]
  ParallelTransform = true
  Placement = pos=(1.921e-13,-12.869,14) rot=(0,0,1;0rad)
  SubTransform = true
  Suppress = false
  Transformations = -> [Mirrored002,Mirrored003]
  TreeRank = 201
  _Version = 3
FEATURE [PartDesign::Draft] Draft
  AddSubType = 0
  Angle = 45
  Base = -> MultiTransform001 [Face13,Face16,Face15,Face14,Face20,Face19,Face22,Face21,Face7,Face10,Face9,Face8,Face4,Face3,Face2,Face1]
  BaseFeature = -> MultiTransform001
  NeutralPlane = -> MultiTransform001 [Face17]
  NewSolid = false
  Placement = pos=(1.921e-13,-12.869,14) rot=(0,0,1;0rad)
  SupportTransform = false
  Suppress = false
  TreeRank = 204
FEATURE [PartDesign::SubShapeBinder] Import001  label="Import001(Sketch022)"
  BindCopyOnChange = 0
  BindMode = 0
  ClaimChildren = false
  Context = -> Part [Part004.Body011.Import001.]
  FillStyle = 0
  Fuse = false
  MakeFace = false
  OffsetFill = false
  OffsetIntersection = false
  OffsetJoinType = 0
  OffsetOpenResult = false
  PartialLoad = false
  Relative = true
  Support = -> [Body009[Sketch022.]]
  TreeRank = 208
  _Version = 8
FEATURE [PartDesign::Body] Body011  label="square bumps"
  AutoGroupSolids = false
  ClaimAllChildren = false
  ExportMode = 0
  Group = -> [Binder015,Binder016,ShapeBinder,Sketch023,DatumPlane008,Sketch025,Pad005,DatumPlane010,MultiTransform001,Draft,Mirrored002,Mirrored003,Import001]
  Origin = -> Origin011
  Tip = -> Draft
  TreeRank = 3144
  _ExportChildren = -> [Binder015,Binder016,ShapeBinder,DatumPlane008,Sketch025,Pad005,DatumPlane010,MultiTransform001,Draft,Import001]
  _GroupVersion = 1
FEATURE [PartDesign::SubShapeBinder] Binder019  label="Binder019(*Sketch019)"
  BindCopyOnChange = 0
  BindMode = 0
  ClaimChildren = false
  Context = -> Part [Part012.Body013.Binder019.]
  FillStyle = 0
  Fuse = false
  MakeFace = true
  OffsetFill = false
  OffsetIntersection = false
  OffsetJoinType = 0
  OffsetOpenResult = false
  PartialLoad = false
  Relative = true
  Support = -> [Body011[Binder015.Edge1]]
  TreeRank = 223
  _Version = 8
FEATURE [Part::SubShapeBinder] Import002  label="Import002(*Sketch019)"
  BindCopyOnChange = 0
  BindMode = 0
  ClaimChildren = false
  Context = -> Part [Part012.Body013.Import002.]
  FillStyle = 0
  Fuse = false
  MakeFace = false
  OffsetFill = false
  OffsetIntersection = false
  OffsetJoinType = 0
  OffsetOpenResult = false
  PartialLoad = false
  Relative = true
  Support = -> [Body011[Binder015.]]
  TreeRank = 224
  _Version = 8
FEATURE [Sketcher::SketchObject] Sketch030
  ArcFitTolerance = 1e-06
  AttachmentSupport = -> [Fillet]
  ExternalGeometry = -> [Import002]
  FullyConstrained = true
  MapMode = 5
  Placement = pos=(0,0,14) rot=(0,0,1;0rad)
  Support = -> [Fillet]
  TreeRank = 222
  sketch-geometry (13):
    g0: LineSegment StartX=10.5 StartY=-23 StartZ=0 EndX=10.5 EndY=-28 EndZ=0
    g1: LineSegment StartX=5 StartY=-33.5 StartZ=0 EndX=-5 EndY=-33.5 EndZ=0
    g2: LineSegment StartX=-10.5 StartY=-28 StartZ=0 EndX=-10.5 EndY=-23 EndZ=0
    g3: ArcOfCircle CenterX=-5 CenterY=-23 CenterZ=0 NormalX=0 NormalY=0 NormalZ=1 AngleXU=0 Radius=5.5 StartAngle=1.5708 EndAngle=3.14159
    g4: GeomPoint [constr] X=-10.5 Y=-17.5 Z=0
    g5: ArcOfCircle CenterX=-5 CenterY=-28 CenterZ=0 NormalX=0 NormalY=0 NormalZ=1 AngleXU=0 Radius=5.5 StartAngle=3.14159 EndAngle=4.71239
    g6: GeomPoint [constr] X=-10.5 Y=-33.5 Z=0
    g7: ArcOfCircle CenterX=5 CenterY=-28 CenterZ=0 NormalX=0 NormalY=0 NormalZ=1 AngleXU=0 Radius=5.5 StartAngle=4.71239 EndAngle=6.28319
    g8: GeomPoint [constr] X=10.5 Y=-33.5 Z=0
    g9: ArcOfCircle CenterX=5 CenterY=-23 CenterZ=0 NormalX=0 NormalY=0 NormalZ=1 AngleXU=0 Radius=5.5 StartAngle=0 EndAngle=1.5708
    g10: GeomPoint [constr] X=10.5 Y=-17.5 Z=0
    g11: LineSegment StartX=-5 StartY=-17.5 StartZ=0 EndX=0 EndY=-17.5 EndZ=0
    g12: LineSegment StartX=0 StartY=-17.5 StartZ=0 EndX=5 EndY=-17.5 EndZ=0
  constraints (32):
    c: Vertical(g0)
    c: Vertical(g2)
    c: DistanceY(g4,g-3) = 18
    c: DistanceY(g6,g4) = 16
    c: DistanceX(g4,g10) = 21
    c: Symmetric(g8,g6,g-2)
    c: PointOnObject(g4,g2)
    c: Tangent(g2,g3) = 1.5708
    c: PointOnObject(g6,g2)
    c: PointOnObject(g6,g1)
    c: Tangent(g2,g5) = 1.5708
    c: Tangent(g1,g5) = 1.5708
    c: PointOnObject(g8,g1)
    c: PointOnObject(g8,g0)
    c: Tangent(g1,g7) = 1.5708
    c: Tangent(g0,g7) = 1.5708
    c: PointOnObject(g10,g0)
    c: Tangent(g0,g9) = 1.5708
    c: Radius(g3) = 5.5
    c: Radius(g5) = 5.5
    c: Radius(g7) = 5.5
    c: Radius(g9) = 5.5
    c: Coincident(g11,g3)
    c: PointOnObject(g11,g-2)
    c: Horizontal(g11)
    c: Coincident(g12,g11)
    c: Coincident(g12,g9)
    c: Horizontal(g12)
    c: Horizontal(g4,g11)
    c: Vertical(g9,g9)
    c: Vertical(g3,g3)
    c: Horizontal(g10,g11)
FEATURE [Sketcher::SketchObject] Sketch031
  ArcFitTolerance = 1e-06
  AttachmentSupport = -> [YZ_Plane013]
  ExternalGeometry = -> [Sketch030]
  FullyConstrained = true
  MapMode = 5
  Placement = pos=(0,0,0) rot=(0.57735,0.57735,0.57735;2.0944rad)
  Support = -> [YZ_Plane013]
  TreeRank = 225
  expr: Constraints[1] = Spreadsheet.groove_lift
  expr: Constraints[2] = Spreadsheet.groove_radius
  sketch-geometry (1):
    g0: Circle CenterX=-17.5 CenterY=14.3 CenterZ=0 NormalX=0 NormalY=0 NormalZ=1 AngleXU=0 Radius=0.7
  constraints (3):
    c: Vertical(g0,g-3)
    c: DistanceY(g-3,g0) = 0.3
    c: Radius(g0) = 0.7
FEATURE [PartDesign::AdditivePipe] Pipe008
  AddSubType = 0
  AuxilleryCurvelinear = true
  AuxillerySpineTangent = false
  Binormal = (0,0,0)
  ClaimChildren = false
  Fit = 0
  FitJoin = 0
  InnerFit = 0
  InnerFitJoin = 0
  Linearize = true
  Mode = 0
  NewSolid = false
  Placement = pos=(0,0,0) rot=(0.57735,0.57735,0.57735;2.0944rad)
  Profile = -> Sketch031
  Spine = -> Sketch030 [Edge8,Edge9,Edge1,Edge2,Edge3,Edge4,Edge5,Edge6,Edge7]
  SpineTangent = false
  Suppress = false
  Transformation = 0
  Transition = 1
  TreeRank = 226
  _ProfileBasedVersion = 2
FEATURE [PartDesign::Body] Body013  label="belly button"
  AutoGroupSolids = false
  ClaimAllChildren = false
  ExportMode = 0
  Group = -> [Sketch030,Binder019,Import002,Sketch031,Pipe008]
  Origin = -> Origin013
  Tip = -> Pipe008
  TreeRank = 3230
  _ExportChildren = -> [Binder019,Import002,Pipe008]
  _GroupVersion = 1
FEATURE [PartDesign::ShapeBinder] ShapeBinder002
  Support = -> [ShapeBinder]
  TraceSupport = false
  TreeRank = 227
FEATURE [PartDesign::ShapeBinder] ShapeBinder003
  Placement = pos=(-22.5,0.5,0) rot=(1,0,0;1.5708rad)
  Support = -> [Binder015]
  TraceSupport = false
  TreeRank = 228
FEATURE [Sketcher::SketchObject] Sketch033
  ArcFitTolerance = 1e-06
  AttachmentSupport = -> [XY_Plane010]
  ExternalGeometry = -> [ShapeBinder003]
  FullyConstrained = true
  MapMode = 5
  Support = -> [XY_Plane010]
  TreeRank = 233
  expr: Constraints[1] = 37 - 6
  expr: Constraints[6] = 45 - 6
  sketch-geometry (5):
    g0: LineSegment StartX=-19.5 StartY=3.5 StartZ=0 EndX=-19.5 EndY=34.5 EndZ=0
    g1: LineSegment StartX=-19.5 StartY=3.5 StartZ=0 EndX=19.5 EndY=3.5 EndZ=0
    g2: LineSegment StartX=19.5 StartY=3.5 StartZ=0 EndX=0 EndY=19 EndZ=0
    g3: LineSegment StartX=0 StartY=19 StartZ=0 EndX=-19.5 EndY=34.5 EndZ=0
    g4: LineSegment StartX=0 StartY=19 StartZ=0 EndX=-6.22244 EndY=11.1718 EndZ=0
  constraints (15):
    c: Vertical(g0)
    c: DistanceY(g0,g0) = 31
    c: DistanceX(g-3,g0) = 3
    c: DistanceY(g-3,g0) = 3
    c: Coincident(g1,g0)
    c: Horizontal(g1)
    c: DistanceX(g1,g1) = 39
    c: Coincident(g2,g1)
    c: Coincident(g3,g2)
    c: Coincident(g3,g0)
    c: Equal(g2,g3)
    c: Parallel(g2,g3)
    c: Coincident(g4,g2)
    c: Perpendicular(g3,g4)
    c: Distance(g4) = 10
FEATURE [PartDesign::Plane] DatumPlane017
  AttachmentSupport = -> [Sketch033]
  Length = 10
  MapMode = 7
  MinimumLength = 10
  MinimumWidth = 10
  Placement = pos=(-19.5,3.5,0) rot=(0.57735,-0.57735,-0.57735;2.0944rad)
  ResizeMode = 0
  Support = -> [Sketch033]
  TreeRank = 234
  Width = 10
FEATURE [Sketcher::SketchObject] Sketch035
  ArcFitTolerance = 1e-06
  AttachmentSupport = -> [DatumPlane017]
  ExternalGeometry = -> [ShapeBinder003]
  FullyConstrained = true
  MapMode = 5
  Placement = pos=(-19.5,3.5,0) rot=(0.57735,-0.57735,-0.57735;2.0944rad)
  Support = -> [DatumPlane017]
  TreeRank = 238
  sketch-geometry (8):
    g0: LineSegment StartX=0.9 StartY=14 StartZ=0 EndX=0.9 EndY=13.2 EndZ=0
    g1: LineSegment StartX=0.9 StartY=13.2 StartZ=0 EndX=0 EndY=13.2 EndZ=0
    g2: LineSegment StartX=0 StartY=13.2 StartZ=0 EndX=0 EndY=14.55 EndZ=0
    g3: ArcOfEllipse CenterX=0 CenterY=14 CenterZ=0 NormalX=0 NormalY=0 NormalZ=1 MajorRadius=0.9 MinorRadius=0.55 AngleXU=0 StartAngle=-9e-16 EndAngle=1.5708
    g4: LineSegment [constr] StartX=0.9 StartY=14 StartZ=0 EndX=-0.9 EndY=14 EndZ=0
    g5: LineSegment [constr] StartX=0 StartY=14.55 StartZ=0 EndX=0 EndY=13.45 EndZ=0
    g6: GeomPoint [constr] X=0.71239 Y=14 Z=0
    g7: GeomPoint [constr] X=-0.71239 Y=14 Z=0
  constraints (15):
    c: Coincident(g1,g0)
    c: Horizontal(g1)
    c: Vertical(g0)
    c: DistanceY(g0,g0) = 0.8
    c: Coincident(g2,g1)
    c: Vertical(g2)
    c: PointOnObject(g2,g-2)
    c: Horizontal(g-3,g0)
    c: InternalAlignment(g4-g7 -> g3) x4
    c: PointOnObject(g3,g2)
    c: Coincident(g3,g2)
    c: DistanceX(g1,g1) = 0.9
    c: DistanceY(g0,g2) = 0.55
    c: Tangent(g3,g0) = 1.5708
    c: Horizontal(g4)
FEATURE [PartDesign::Line] DatumLine
  AttacherType = Attacher::AttachEngineLine
  AttachmentSupport = -> [Sketch035]
  Length = 14
  MapMode = 29
  MinimumLength = 10
  Placement = pos=(-19.5,3.5,0) rot=(0,0,1;0rad)
  ResizeMode = 0
  Support = -> [Sketch035]
  TreeRank = 239
FEATURE [PartDesign::Revolution] Revolution
  AddSubType = 0
  Angle = 360
  Axis = (0,0,1)
  Base = (-19.5,3.5,0)
  ClaimChildren = false
  Fit = 0
  FitJoin = 0
  InnerFit = 0
  InnerFitJoin = 0
  Linearize = true
  NewSolid = false
  Placement = pos=(-19.5,3.5,0) rot=(0.57735,-0.57735,-0.57735;2.0944rad)
  Profile = -> Sketch035
  ReferenceAxis = -> Sketch035 [V_Axis]
  Reversed = true
  Suppress = false
  TreeRank = 240
  _ProfileBasedVersion = 1
FEATURE [Sketcher::SketchObject] Sketch036
  ArcFitTolerance = 1e-06
  AttachmentSupport = -> [XY_Plane010]
  FullyConstrained = false
  MapMode = 5
  Support = -> [XY_Plane010]
  TreeRank = 256
  sketch-geometry (4):
    g0: LineSegment StartX=-14.5158 StartY=27.916 StartZ=0 EndX=15.7271 EndY=27.916 EndZ=0
    g1: LineSegment StartX=15.7271 StartY=27.916 StartZ=0 EndX=15.7271 EndY=7.66619 EndZ=0
    g2: LineSegment StartX=15.7271 StartY=7.66619 StartZ=0 EndX=-14.5158 EndY=7.66619 EndZ=0
    g3: LineSegment StartX=-14.5158 StartY=7.66619 StartZ=0 EndX=-14.5158 EndY=27.916 EndZ=0
  constraints (8):
    c: Coincident(g0,g1)
    c: Coincident(g1,g2)
    c: Coincident(g2,g3)
    c: Coincident(g3,g0)
    c: Horizontal(g0)
    c: Horizontal(g2)
    c: Vertical(g1)
    c: Vertical(g3)
FEATURE [PartDesign::Body] Body010  label="bump master"
  AutoGroupSolids = false
  ClaimAllChildren = false
  ExportMode = 0
  Group = -> [ShapeBinder002,ShapeBinder003,Sketch033,DatumPlane017,Sketch035,DatumLine,Revolution,Sketch036]
  Origin = -> Origin010
  Tip = -> Revolution
  TreeRank = 277
  _ExportChildren = -> [ShapeBinder002,ShapeBinder003,Sketch033,DatumPlane017,DatumLine,Revolution,Sketch036]
  _GroupVersion = 1
FEATURE [PartDesign::ShapeBinder] ShapeBinder004
  Support = -> [Sketch036]
  TraceSupport = false
  TreeRank = 271
FEATURE [Part::SubShapeBinder] Import003  label="Import003(Sketch036)"
  BindCopyOnChange = 0
  BindMode = 0
  ClaimChildren = false
  Context = -> Body014 [Import003.]
  FillStyle = 0
  Fuse = false
  MakeFace = false
  OffsetFill = false
  OffsetIntersection = false
  OffsetJoinType = 0
  OffsetOpenResult = false
  PartialLoad = false
  Relative = true
  Support = -> [Body010[Sketch036.]]
  TreeRank = 273
  _Version = 8
FEATURE [Sketcher::SketchObject] Sketch037
  ArcFitTolerance = 1e-06
  AttachmentSupport = -> [XY_Plane015]
  ExternalGeometry = -> [Import003]
  FullyConstrained = true
  MapMode = 5
  Support = -> [XY_Plane015]
  TreeRank = 272
  sketch-geometry (4):
    g0: LineSegment StartX=15.7271 StartY=27.916 StartZ=0 EndX=-14.5158 EndY=27.916 EndZ=0
    g1: LineSegment StartX=-14.5158 StartY=27.916 StartZ=0 EndX=-14.5158 EndY=7.66619 EndZ=0
    g2: LineSegment StartX=-14.5158 StartY=7.66619 StartZ=0 EndX=15.7271 EndY=7.66619 EndZ=0
    g3: LineSegment StartX=15.7271 StartY=7.66619 StartZ=0 EndX=15.7271 EndY=27.916 EndZ=0
  constraints (10):
    c: Coincident(g0,g1)
    c: Coincident(g1,g2)
    c: Coincident(g2,g3)
    c: Coincident(g3,g0)
    c: Horizontal(g0)
    c: Horizontal(g2)
    c: Vertical(g1)
    c: Vertical(g3)
    c: Coincident(g0,g-4)
    c: Coincident(g1,g-5)
FEATURE [PartDesign::Pad] Pad006
  AddSubType = 0
  AlongSketchNormal = false
  CheckUpToFaceLimits = true
  ClaimChildren = false
  Direction = (0,0,1)
  Fit = 0
  FitJoin = 0
  InnerFit = 0
  InnerFitJoin = 0
  InnerTaperAngle = 0
  InnerTaperAngleRev = 0
  Length = 20
  Length2 = 100
  Linearize = true
  NewSolid = false
  Profile = -> Sketch037
  Suppress = false
  TreeRank = 274
  Type = 0
  _ProfileBasedVersion = 1
FEATURE [PartDesign::Body] Body014  label="top bump cutout"
  AutoGroupSolids = false
  ClaimAllChildren = false
  ExportMode = 0
  Group = -> [ShapeBinder004,Sketch037,Import003,Pad006]
  Origin = -> Origin015
  Tip = -> Pad006
  TreeRank = 3478
  _ExportChildren = -> [ShapeBinder004,Import003,Pad006]
  _GroupVersion = 1
FEATURE [PartDesign::FeatureBase] Clone
  BaseFeature = -> Body010
  NewSolid = false
  Suppress = false
  TreeRank = 288
FEATURE [PartDesign::FeatureBase] Clone001
  BaseFeature = -> Body010
  NewSolid = false
  Suppress = false
  TreeRank = 300
FEATURE [PartDesign::FeatureBase] Clone002
  BaseFeature = -> Body010
  NewSolid = false
  Suppress = false
  TreeRank = 312
FEATURE [PartDesign::Body] Body017
  AutoGroupSolids = false
  BaseFeature = -> Body010
  ClaimAllChildren = false
  ExportMode = 0
  Group = -> [Clone002]
  Origin = -> Origin018
  Placement = pos=(-6,-11,0) rot=(0,0,1;0rad)
  Tip = -> Clone002
  TreeRank = 314
  _ExportChildren = -> [Clone002]
  _GroupVersion = 1
FEATURE [PartDesign::LinearPattern] LinearPattern
  AddSubType = 0
  CopyShape = false
  Direction = -> X_Axis016
  Length = 39
  NewSolid = false
  Occurrences = 6
  ParallelTransform = true
  SubTransform = true
  Suppress = false
  TreeRank = 328
  _Version = 3
  expr: Length = 45 - 6
FEATURE [PartDesign::LinearPattern] LinearPattern001
  AddSubType = 0
  CopyShape = false
  Direction = -> Y_Axis016
  Length = 31
  NewSolid = false
  Occurrences = 5
  ParallelTransform = true
  SubTransform = true
  Suppress = false
  TreeRank = 329
  _Version = 3
  expr: Length = 37 - 6
FEATURE [PartDesign::MultiTransform] MultiTransform
  AddSubType = 0
  BaseFeature = -> Clone
  CopyShape = false
  NewSolid = false
  OriginalSubs = -> [Clone]
  Originals = -> [Clone]
  ParallelTransform = true
  SubTransform = true
  Suppress = false
  Transformations = -> [LinearPattern,LinearPattern001]
  TreeRank = 327
  _Version = 3
FEATURE [PartDesign::Body] Body015  label="top bump"
  AutoGroupSolids = false
  BaseFeature = -> Body010
  ClaimAllChildren = false
  ExportMode = 0
  Group = -> [Clone,MultiTransform,LinearPattern,LinearPattern001]
  Origin = -> Origin016
  Tip = -> MultiTransform
  TreeRank = 3477
  _ExportChildren = -> [Clone,MultiTransform]
  _GroupVersion = 1
FEATURE [PartDesign::ShapeBinder] ShapeBinder005
  Placement = pos=(-29,-10.5,0) rot=(1,0,0;1.5708rad)
  Support = -> [Sketch016]
  TraceSupport = true
  TreeRank = 331
FEATURE [PartDesign::Plane] DatumPlane018
  AttachmentSupport = -> [ShapeBinder005]
  Length = 22.5
  MapMode = 13
  MinimumLength = 10
  MinimumWidth = 10
  Placement = pos=(-22.5,-10.5,11.6667) rot=(1,0,0;1.5708rad)
  ResizeMode = 0
  Support = -> [ShapeBinder005]
  TreeRank = 332
  Width = 11.6667
FEATURE [Sketcher::SketchObject] Sketch038
  ArcFitTolerance = 1e-06
  AttachmentSupport = -> [DatumPlane018]
  ExternalGeometry = -> [ShapeBinder005]
  FullyConstrained = true
  MapMode = 5
  Placement = pos=(-22.5,-10.5,11.6667) rot=(1,0,0;1.5708rad)
  Support = -> [DatumPlane018]
  TreeRank = 333
  sketch-geometry (6):
    g0: LineSegment StartX=0.5 StartY=2.33333 StartZ=0 EndX=0.5 EndY=-4.66667 EndZ=0
    g1: LineSegment [constr] StartX=6 StartY=2.33333 StartZ=0 EndX=3 EndY=2.33333 EndZ=0
    g2: LineSegment [constr] StartX=-6.5 StartY=-11.6667 StartZ=0 EndX=-6.5 EndY=-8.66667 EndZ=0
    g3: LineSegment StartX=3 StartY=2.33333 StartZ=0 EndX=0.5 EndY=2.33333 EndZ=0
    g4: LineSegment StartX=-6.5 StartY=-8.66667 StartZ=0 EndX=-6.5 EndY=-4.66667 EndZ=0
    g5: ArcOfCircle CenterX=0.5 CenterY=-4.66667 CenterZ=0 NormalX=0 NormalY=0 NormalZ=1 AngleXU=0 Radius=7 StartAngle=1.5708 EndAngle=3.14159
  constraints (15):
    c: Coincident(g0,g-3)
    c: Coincident(g0,g-3)
    c: Coincident(g1,g-4)
    c: Horizontal(g1)
    c: DistanceX(g1,g1) = 3
    c: Coincident(g2,g-5)
    c: Vertical(g2)
    c: DistanceY(g2,g2) = 3
    c: Coincident(g3,g1)
    c: Coincident(g3,g0)
    c: Coincident(g4,g2)
    c: Coincident(g4,g-3)
    c: Coincident(g5,g0)
    c: Coincident(g5,g0)
    c: Coincident(g5,g4)
FEATURE [PartDesign::Line] DatumLine001
  AttacherType = Attacher::AttachEngineLine
  AttachmentSupport = -> [DatumPlane018,Sketch038]
  Length = 45.7964
  MapMode = 46
  MinimumLength = 10
  Placement = pos=(-22,-10.5,7) rot=(0,-0.707107,0.707107;3.14159rad)
  ResizeMode = 0
  Support = -> [DatumPlane018,Sketch038]
  TreeRank = 334
FEATURE [PartDesign::LinearPattern] LinearPattern002
  AddSubType = 0
  CopyShape = false
  Direction = -> Y_Axis017
  Length = 31
  NewSolid = false
  Occurrences = 5
  ParallelTransform = true
  SubTransform = true
  Suppress = false
  TreeRank = 430
  _Version = 3
  expr: Length = 37 - 6
FEATURE [PartDesign::MultiTransform] MultiTransform002
  AddSubType = 0
  BaseFeature = -> Clone001
  CopyShape = false
  NewSolid = false
  OriginalSubs = -> [Clone001]
  Originals = -> [Clone001]
  ParallelTransform = true
  SubTransform = true
  Suppress = false
  Transformations = -> [LinearPattern002]
  TreeRank = 335
  _Version = 3
FEATURE [PartDesign::Body] Body016
  AutoGroupSolids = false
  BaseFeature = -> Body010
  ClaimAllChildren = false
  ExportMode = 0
  Group = -> [Clone001,ShapeBinder005,DatumPlane018,Sketch038,DatumLine001,MultiTransform002,LinearPattern002]
  Origin = -> Origin017
  Placement = pos=(-6,0,0) rot=(0,0,1;0rad)
  Tip = -> MultiTransform002
  TreeRank = 339
  _ExportChildren = -> [Clone001,ShapeBinder005,DatumPlane018,Sketch038,DatumLine001,MultiTransform002]
  _GroupVersion = 1
FEATURE [PartDesign::ShapeBinder] ShapeBinder006
  Placement = pos=(-35,-10.5,0) rot=(1,0,0;1.5708rad)
  Support = -> [Sketch016]
  TraceSupport = false
  TreeRank = 393
FEATURE [Sketcher::SketchObject] Sketch039
  ArcFitTolerance = 1e-06
  AttachmentSupport = -> [XZ_Plane023]
  ExternalGeometry = -> [ShapeBinder006]
  FullyConstrained = true
  MapMode = 5
  Placement = pos=(0,0,0) rot=(1,0,0;1.5708rad)
  Support = -> [XZ_Plane023]
  TreeRank = 394
  sketch-geometry (4):
    g0: LineSegment StartX=-37 StartY=15 StartZ=0 EndX=-28 EndY=15 EndZ=0
    g1: LineSegment StartX=-28 StartY=15 StartZ=0 EndX=-28 EndY=7 EndZ=0
    g2: LineSegment StartX=-28 StartY=7 StartZ=0 EndX=-37 EndY=7 EndZ=0
    g3: LineSegment StartX=-37 StartY=7 StartZ=0 EndX=-37 EndY=15 EndZ=0
  constraints (11):
    c: Coincident(g0,g1)
    c: Coincident(g1,g2)
    c: Coincident(g2,g3)
    c: Coincident(g3,g0)
    c: Horizontal(g0)
    c: Horizontal(g2)
    c: Vertical(g1)
    c: Vertical(g3)
    c: Coincident(g1,g-4)
    c: DistanceY(g3,g3) = 8
    c: DistanceX(g0,g0) = 9
FEATURE [PartDesign::Pad] Pad007
  AddSubType = 0
  AlongSketchNormal = false
  CheckUpToFaceLimits = true
  ClaimChildren = false
  Direction = (0,-1,-2e-16)
  Fit = 0
  FitJoin = 0
  InnerFit = 0
  InnerFitJoin = 0
  InnerTaperAngle = 0
  InnerTaperAngleRev = 0
  Length = 30
  Length2 = 100
  Linearize = true
  NewSolid = false
  Placement = pos=(0,0,0) rot=(1,0,0;1.5708rad)
  Profile = -> Sketch039
  Reversed = true
  Suppress = false
  TreeRank = 395
  Type = 0
  _ProfileBasedVersion = 1
FEATURE [PartDesign::Body] Body022
  AutoGroupSolids = false
  ClaimAllChildren = false
  ExportMode = 0
  Group = -> [ShapeBinder006,Sketch039,Pad007]
  Origin = -> Origin023
  Placement = pos=(0,-0.26,0) rot=(0,0,1;0rad)
  Tip = -> Pad007
  TreeRank = 3484
  _ExportChildren = -> [ShapeBinder006,Pad007]
  _GroupVersion = 1
FEATURE [PartDesign::FeatureBase] Clone010
  BaseFeature = -> Body010
  NewSolid = false
  Suppress = false
  TreeRank = 470
FEATURE [PartDesign::LinearPattern] LinearPattern003
  AddSubType = 0
  BaseFeature = -> Clone010
  CopyShape = false
  Direction = -> Y_Axis027
  Length = 31
  NewSolid = false
  Occurrences = 5
  OriginalSubs = -> [Clone010]
  Originals = -> [Clone010]
  ParallelTransform = true
  Reversed = true
  SubTransform = true
  Suppress = false
  TreeRank = 474
  _Version = 3
  expr: Length = 37 - 6
FEATURE [PartDesign::Body] Body026
  AutoGroupSolids = false
  BaseFeature = -> Body010
  ClaimAllChildren = false
  ExportMode = 0
  Group = -> [Clone010,LinearPattern003]
  Origin = -> Origin027
  Placement = pos=(-6,-17,0) rot=(0,0,1;0rad)
  Tip = -> LinearPattern003
  TreeRank = 473
  _ExportChildren = -> [Clone010,LinearPattern003]
  _GroupVersion = 1
FEATURE [PartDesign::FeatureBase] Clone011
  BaseFeature = -> Body026
  NewSolid = false
  Placement = pos=(-6,-17,0) rot=(0,0,1;0rad)
  Suppress = false
  TreeRank = 484
FEATURE [PartDesign::Body] Body027
  AutoGroupSolids = false
  BaseFeature = -> Body026
  ClaimAllChildren = false
  ExportMode = 0
  Group = -> [Clone011]
  Origin = -> Origin028
  Placement = pos=(-20.95,0,28.8) rot=(0,-1,0;1.5708rad)
  Tip = -> Clone011
  TreeRank = 487
  _ExportChildren = -> [Clone011]
  _GroupVersion = 1
FEATURE [PartDesign::FeatureBase] Clone012
  BaseFeature = -> Body026
  NewSolid = false
  Placement = pos=(-6,-17,0) rot=(0,0,1;0rad)
  Suppress = false
  TreeRank = 497
FEATURE [PartDesign::Body] Body028
  AutoGroupSolids = false
  BaseFeature = -> Body026
  ClaimAllChildren = false
  ExportMode = 0
  Group = -> [Clone012]
  Origin = -> Origin029
  Placement = pos=(-3.18,0,15.72) rot=(0,-1,0;0.610865rad)
  Tip = -> Clone012
  TreeRank = 500
  _ExportChildren = -> [Clone012]
  _GroupVersion = 1
FEATURE [PartDesign::FeatureBase] Clone013
  BaseFeature = -> Body026
  NewSolid = false
  Placement = pos=(-6,-17,0) rot=(0,0,1;0rad)
  Suppress = false
  TreeRank = 510
FEATURE [PartDesign::Body] Body029
  AutoGroupSolids = false
  BaseFeature = -> Body026
  ClaimAllChildren = false
  ExportMode = 0
  Group = -> [Clone013]
  Origin = -> Origin030
  Placement = pos=(-14.58,0,29.79) rot=(0,-1,0;1.309rad)
  Tip = -> Clone013
  TreeRank = 513
  _ExportChildren = -> [Clone013]
  _GroupVersion = 1
FEATURE [Part::MultiFuse] Fusion006
  Shapes = -> [Body027,Body026]
  TreeRank = 514
FEATURE [Part::MultiFuse] Fusion007
  Shapes = -> [Fusion006,Body028]
  TreeRank = 515
FEATURE [Part::MultiFuse] Fusion008
  Shapes = -> [Fusion007,Body029]
  TreeRank = 516
FEATURE [PartDesign::ShapeBinder] ShapeBinder007
  Placement = pos=(0,0,0) rot=(1,0,0;1.5708rad)
  Support = -> [Sketch039]
  TraceSupport = false
  TreeRank = 541
FEATURE [Sketcher::SketchObject] Sketch040
  ArcFitTolerance = 1e-06
  AttachmentSupport = -> [XZ_Plane032]
  ExternalGeometry = -> [ShapeBinder007]
  FullyConstrained = true
  MapMode = 5
  Placement = pos=(0,0,0) rot=(1,0,0;1.5708rad)
  Support = -> [XZ_Plane032]
  TreeRank = 542
  sketch-geometry (4):
    g0: LineSegment StartX=-28 StartY=15 StartZ=0 EndX=-37 EndY=15 EndZ=0
    g1: LineSegment StartX=-37 StartY=15 StartZ=0 EndX=-37 EndY=7 EndZ=0
    g2: LineSegment StartX=-37 StartY=7 StartZ=0 EndX=-28 EndY=7 EndZ=0
    g3: LineSegment StartX=-28 StartY=7 StartZ=0 EndX=-28 EndY=15 EndZ=0
  constraints (10):
    c: Coincident(g0,g1)
    c: Coincident(g1,g2)
    c: Coincident(g2,g3)
    c: Coincident(g3,g0)
    c: Horizontal(g0)
    c: Horizontal(g2)
    c: Vertical(g1)
    c: Vertical(g3)
    c: Coincident(g0,g-3)
    c: Coincident(g1,g-4)
FEATURE [PartDesign::Pad] Pad008
  AddSubType = 0
  CheckUpToFaceLimits = true
  ClaimChildren = false
  Direction = (0,-1,-2e-16)
  Fit = 0
  FitJoin = 0
  InnerFit = 0
  InnerFitJoin = 0
  InnerTaperAngle = 0
  InnerTaperAngleRev = 0
  Length = 20
  Length2 = 100
  Linearize = true
  NewSolid = false
  Placement = pos=(0,0,0) rot=(1,0,0;1.5708rad)
  Profile = -> Sketch040
  Suppress = false
  TreeRank = 543
  Type = 0
  _ProfileBasedVersion = 1
FEATURE [PartDesign::Body] Body030
  AutoGroupSolids = false
  ClaimAllChildren = false
  ExportMode = 0
  Group = -> [ShapeBinder007,Sketch040,Pad008]
  Origin = -> Origin032
  Placement = pos=(0,-19,0) rot=(0,0,1;0rad)
  Tip = -> Pad008
  TreeRank = 540
  _ExportChildren = -> [ShapeBinder007,Pad008]
  _GroupVersion = 1
FEATURE [Part::Cut] Cut002  label="bump side 2"
  Base = -> Fusion008
  Tool = -> Body030
  TreeRank = 3474
FEATURE [Sketcher::SketchObject] Sketch041
  ArcFitTolerance = 1e-06
  AttachmentSupport = -> [XZ_Plane033]
  FullyConstrained = true
  MapMode = 5
  Placement = pos=(0,0,0) rot=(1,0,0;1.5708rad)
  Support = -> [XZ_Plane033]
  TreeRank = 569
  sketch-geometry (1):
    g0: Circle CenterX=0 CenterY=0 CenterZ=0 NormalX=0 NormalY=0 NormalZ=1 AngleXU=0 Radius=0.9
  constraints (2):
    c: Coincident(g0,g-1)
    c: Radius(g0) = 0.9
FEATURE [PartDesign::Pad] Pad009
  AddSubType = 0
  AlongSketchNormal = false
  CheckUpToFaceLimits = true
  ClaimChildren = false
  Direction = (0,-1,2e-16)
  Fit = 0
  FitJoin = 0
  InnerFit = 0
  InnerFitJoin = 0
  InnerTaperAngle = 0
  InnerTaperAngleRev = 0
  Length = 4.8
  Length2 = 100
  Linearize = true
  NewSolid = false
  Placement = pos=(0,0,0) rot=(1,0,0;1.5708rad)
  Profile = -> Sketch041
  Suppress = false
  TreeRank = 3216
  Type = 0
  _ProfileBasedVersion = 1
FEATURE [PartDesign::ShapeBinder] ShapeBinder008
  Support = -> [Fillet]
  TraceSupport = false
  TreeRank = 598
FEATURE [Sketcher::SketchObject] Sketch042
  ArcFitTolerance = 1e-06
  AttachmentSupport = -> [ShapeBinder008]
  ExternalGeometry = -> [ShapeBinder008]
  FullyConstrained = true
  MapMode = 5
  Placement = pos=(0,53.5,0) rot=(0,0.707107,0.707107;3.14159rad)
  Support = -> [ShapeBinder008]
  TreeRank = 599
  sketch-geometry (3):
    g0: ArcOfCircle CenterX=-12 CenterY=5.4 CenterZ=0 NormalX=0 NormalY=0 NormalZ=1 AngleXU=0 Radius=3 StartAngle=3.14159 EndAngle=4.71239
    g1: LineSegment StartX=-15 StartY=5.4 StartZ=0 EndX=-12 EndY=5.4 EndZ=0
    g2: LineSegment StartX=-12 StartY=5.4 StartZ=0 EndX=-12 EndY=2.4 EndZ=0
  constraints (9):
    c: Coincident(g1,g0)
    c: Coincident(g1,g0)
    c: Coincident(g2,g0)
    c: Coincident(g2,g0)
    c: Vertical(g2)
    c: Horizontal(g1)
    c: Radius(g0) = 3
    c: DistanceX(g-3,g0) = 20
    c: DistanceY(g-1,g0) = 5.4
FEATURE [PartDesign::Line] DatumLine002
  AttacherType = Attacher::AttachEngineLine
  AttachmentSupport = -> [Sketch042]
  Length = 10
  MapMode = 29
  MinimumLength = 10
  Placement = pos=(12,53.5,0) rot=(0,1,0;3.14159rad)
  ResizeMode = 0
  Support = -> [Sketch042]
  TreeRank = 600
FEATURE [PartDesign::Revolution] Revolution001
  AddSubType = 0
  Angle = 360
  Axis = (0,0,-1)
  Base = (12,53.5,0)
  ClaimChildren = false
  Fit = 0
  FitJoin = 0
  InnerFit = 0
  InnerFitJoin = 0
  Linearize = true
  NewSolid = false
  Profile = -> Sketch042
  ReferenceAxis = -> DatumLine002
  Reversed = true
  Suppress = false
  TreeRank = 601
  _ProfileBasedVersion = 1
FEATURE [PartDesign::Body] Body033  label="front light bottom"
  AutoGroupSolids = false
  ClaimAllChildren = false
  ExportMode = 0
  Group = -> [ShapeBinder008,Sketch042,DatumLine002,Revolution001]
  Origin = -> Origin035
  Tip = -> Revolution001
  TreeRank = 3282
  _ExportChildren = -> [ShapeBinder008,DatumLine002,Revolution001]
  _GroupVersion = 1
FEATURE [PartDesign::ShapeBinder] ShapeBinder009
  Placement = pos=(0,53.5,0) rot=(0,0.707107,0.707107;3.14159rad)
  Support = -> [Sketch042]
  TraceSupport = false
  TreeRank = 614
FEATURE [PartDesign::ShapeBinder] ShapeBinder010
  Support = -> [Fillet]
  TraceSupport = false
  TreeRank = 615
FEATURE [Sketcher::SketchObject] Sketch043
  ArcFitTolerance = 1e-06
  AttachmentSupport = -> [ShapeBinder010]
  ExternalGeometry = -> [ShapeBinder009]
  FullyConstrained = true
  MapMode = 5
  Placement = pos=(0,53.5,0) rot=(0,0.707107,0.707107;3.14159rad)
  Support = -> [ShapeBinder010]
  TreeRank = 616
  sketch-geometry (5):
    g0: ArcOfCircle CenterX=-12 CenterY=6.6 CenterZ=0 NormalX=0 NormalY=0 NormalZ=1 AngleXU=0 Radius=3 StartAngle=1.5708 EndAngle=3.14159
    g1: LineSegment StartX=-12 StartY=9.6 StartZ=0 EndX=-12 EndY=6.6 EndZ=0
    g2: LineSegment StartX=-12 StartY=6.6 StartZ=0 EndX=-12 EndY=5.4 EndZ=0
    g3: LineSegment StartX=-12 StartY=5.4 StartZ=0 EndX=-15 EndY=5.4 EndZ=0
    g4: LineSegment StartX=-15 StartY=5.4 StartZ=0 EndX=-15 EndY=6.6 EndZ=0
  constraints (13):
    c: Coincident(g1,g0)
    c: Coincident(g1,g0)
    c: Vertical(g1)
    c: Vertical(g0,g-5)
    c: Vertical(g0,g-6)
    c: DistanceY(g-5,g0) = 1.2
    c: Coincident(g2,g0)
    c: Coincident(g2,g-5)
    c: Coincident(g2,g3)
    c: Coincident(g3,g-6)
    c: Coincident(g3,g4)
    c: Coincident(g4,g0)
    c: Horizontal(g0,g0)
FEATURE [PartDesign::Line] DatumLine003
  AttacherType = Attacher::AttachEngineLine
  AttachmentSupport = -> [Sketch043]
  Length = 10
  MapMode = 29
  MinimumLength = 10
  Placement = pos=(12,53.5,0) rot=(0,1,0;3.14159rad)
  ResizeMode = 0
  Support = -> [Sketch043]
  TreeRank = 617
FEATURE [PartDesign::ShapeBinder] ShapeBinder011
  Support = -> [Revolution001]
  TraceSupport = false
  TreeRank = 632
FEATURE [PartDesign::ShapeBinder] ShapeBinder012
  Support = -> [Fillet]
  TraceSupport = false
  TreeRank = 633
FEATURE [Part::SubShapeBinder] Import005  label="Import005(Revolution001)"
  BindCopyOnChange = 0
  BindMode = 0
  ClaimChildren = false
  Context = -> Part [Part010.Body035.Import005.]
  FillStyle = 0
  Fuse = false
  MakeFace = false
  OffsetFill = false
  OffsetIntersection = false
  OffsetJoinType = 0
  OffsetOpenResult = false
  PartialLoad = false
  Relative = true
  Support = -> [Body033[Revolution001.]]
  TreeRank = 635
  _Version = 8
FEATURE [Sketcher::SketchObject] Sketch044
  ArcFitTolerance = 1e-06
  AttachmentSupport = -> [ShapeBinder012]
  ExternalGeometry = -> [Import005,ShapeBinder011]
  FullyConstrained = true
  MapMode = 5
  Placement = pos=(0,53.5,0) rot=(0,0.707107,0.707107;3.14159rad)
  Support = -> [ShapeBinder012]
  TreeRank = 634
  sketch-geometry (3):
    g0: Circle CenterX=-12 CenterY=6.9 CenterZ=0 NormalX=0 NormalY=0 NormalZ=1 AngleXU=0 Radius=1.5
    g1: LineSegment [constr] StartX=-12 StartY=6.9 StartZ=0 EndX=-15 EndY=5.4 EndZ=0
    g2: LineSegment [constr] StartX=-12 StartY=6.9 StartZ=0 EndX=-9 EndY=5.4 EndZ=0
  constraints (7):
    c: DistanceY(g-4,g0) = 1.5
    c: Coincident(g1,g0)
    c: Coincident(g1,g-4)
    c: Coincident(g2,g1)
    c: Coincident(g2,g-4)
    c: Equal(g1,g2)
    c: Radius(g0) = 1.5
FEATURE [PartDesign::SubShapeBinder] Import004  label="Import004(DatumLine002)"
  BindCopyOnChange = 0
  BindMode = 0
  ClaimChildren = false
  Context = -> Part [Part010.Body034.Import004.]
  FillStyle = 0
  Fuse = false
  MakeFace = false
  OffsetFill = false
  OffsetIntersection = false
  OffsetJoinType = 0
  OffsetOpenResult = false
  PartialLoad = false
  Relative = true
  Support = -> [Body033[DatumLine002.]]
  TreeRank = 636
  _Version = 8
FEATURE [PartDesign::Revolution] Revolution002
  AddSubType = 0
  Angle = 180
  Axis = (0,0,-1)
  Base = (12,53.5,0)
  ClaimChildren = false
  Fit = 0
  FitJoin = 0
  InnerFit = 0
  InnerFitJoin = 0
  Linearize = true
  NewSolid = false
  Profile = -> Sketch043
  ReferenceAxis = -> Import004
  Suppress = false
  TreeRank = 618
  _ProfileBasedVersion = 1
FEATURE [PartDesign::Body] Body034  label="front light top cutout"
  AutoGroupSolids = false
  ClaimAllChildren = false
  ExportMode = 0
  Group = -> [ShapeBinder009,ShapeBinder010,Sketch043,DatumLine003,Revolution002,Import004]
  Origin = -> Origin036
  Tip = -> Revolution002
  TreeRank = 3274
  _ExportChildren = -> [ShapeBinder009,ShapeBinder010,DatumLine003,Revolution002,Import004]
  _GroupVersion = 1
FEATURE [PartDesign::Pad] Pad010
  AddSubType = 0
  AlongSketchNormal = false
  CheckUpToFaceLimits = true
  ClaimChildren = false
  Direction = (0,1,-2e-16)
  Fit = 0
  FitJoin = 0
  InnerFit = 0
  InnerFitJoin = 0
  InnerTaperAngle = 0
  InnerTaperAngleRev = 0
  Length = 4.25
  Length2 = 100
  Linearize = true
  NewSolid = false
  Profile = -> Sketch044
  Reversed = true
  Suppress = false
  TreeRank = 637
  Type = 0
  _ProfileBasedVersion = 1
FEATURE [PartDesign::Body] Body035  label="front light hole"
  AutoGroupSolids = false
  ClaimAllChildren = false
  ExportMode = 0
  Group = -> [ShapeBinder011,ShapeBinder012,Sketch044,Import005,Pad010]
  Origin = -> Origin037
  Tip = -> Pad010
  TreeRank = 3270
  _ExportChildren = -> [ShapeBinder011,ShapeBinder012,Import005,Pad010]
  _GroupVersion = 1
FEATURE [PartDesign::ShapeBinder] ShapeBinder014
  Placement = pos=(0,53.5,0) rot=(0,0.707107,0.707107;3.14159rad)
  Support = -> [Sketch043]
  TraceSupport = false
  TreeRank = 740
FEATURE [Part::SubShapeBinder] Import007  label="Import007(Revolution002)"
  BindCopyOnChange = 0
  BindMode = 0
  ClaimChildren = false
  Context = -> Part [Body039.Import007.]
  FillStyle = 0
  Fuse = false
  MakeFace = false
  OffsetFill = false
  OffsetIntersection = false
  OffsetJoinType = 0
  OffsetOpenResult = false
  PartialLoad = false
  Relative = true
  Support = -> [Body034[Revolution002.]]
  TreeRank = 743
  _Version = 8
FEATURE [Sketcher::SketchObject] Sketch047
  ArcFitTolerance = 1e-06
  AttachmentSupport = -> [Import007]
  ExternalGeometry = -> [Import007]
  FullyConstrained = true
  MapMode = 5
  Placement = pos=(-6.6e-15,53.5,0) rot=(0,0.707107,0.707107;3.14159rad)
  Support = -> [Import007]
  TreeRank = 746
  sketch-geometry (9):
    g0: LineSegment StartX=-12 StartY=9.6 StartZ=0 EndX=-12 EndY=10.6 EndZ=0
    g1: ArcOfCircle CenterX=-12 CenterY=6.6 CenterZ=0 NormalX=0 NormalY=0 NormalZ=1 AngleXU=0 Radius=3 StartAngle=1.5708 EndAngle=3.14159
    g2: ArcOfCircle CenterX=-12 CenterY=6.6 CenterZ=0 NormalX=0 NormalY=0 NormalZ=1 AngleXU=0 Radius=4 StartAngle=1.5708 EndAngle=3.14159
    g3: LineSegment StartX=-16 StartY=6.6 StartZ=0 EndX=-16 EndY=5.4 EndZ=0
    g4: LineSegment StartX=-15 StartY=6.6 StartZ=0 EndX=-15 EndY=5.4 EndZ=0
    g5: LineSegment StartX=-16 StartY=5.4 StartZ=0 EndX=-16 EndY=3.4 EndZ=0
    g6: LineSegment StartX=-16 StartY=3.4 StartZ=0 EndX=-12 EndY=3.4 EndZ=0
    g7: LineSegment StartX=-12 StartY=3.4 StartZ=0 EndX=-12 EndY=5.4 EndZ=0
    g8: LineSegment StartX=-12 StartY=5.4 StartZ=0 EndX=-15 EndY=5.4 EndZ=0
  constraints (24):
    c: Coincident(g0,g-5)
    c: Vertical(g0)
    c: Coincident(g1,g-4)
    c: Coincident(g1,g0)
    c: Coincident(g2,g1)
    c: Coincident(g2,g0)
    c: Horizontal(g1,g2)
    c: Coincident(g3,g2)
    c: Vertical(g3)
    c: DistanceX(g3,g-3) = 1
    c: Coincident(g4,g1)
    c: Coincident(g5,g3)
    c: Vertical(g5)
    c: Coincident(g6,g5)
    c: Horizontal(g6)
    c: Coincident(g7,g6)
    c: Coincident(g7,g-6)
    c: Vertical(g7)
    c: DistanceY(g5,g5) = 2
    c: Equal(g7,g5)
    c: Coincident(g8,g7)
    c: Coincident(g8,g4)
    c: Coincident(g4,g-3)
    c: Horizontal(g2,g-7)
FEATURE [PartDesign::Line] DatumLine005
  AttacherType = Attacher::AttachEngineLine
  AttachmentSupport = -> [Sketch047]
  Length = 10
  MapMode = 29
  MinimumLength = 10
  Placement = pos=(12,53.5,0) rot=(0,0,1;0rad)
  ResizeMode = 0
  Support = -> [Sketch047]
  TreeRank = 745
FEATURE [PartDesign::Revolution] Revolution004
  AddSubType = 0
  Angle = 180
  Axis = (0,0,1)
  Base = (12,53.5,0)
  ClaimChildren = false
  Fit = 0
  FitJoin = 0
  InnerFit = 0
  InnerFitJoin = 0
  Linearize = true
  NewSolid = false
  Profile = -> Sketch047
  ReferenceAxis = -> DatumLine005
  Reversed = true
  Suppress = false
  TreeRank = 747
  _ProfileBasedVersion = 1
FEATURE [PartDesign::ShapeBinder] ShapeBinder015
  Placement = pos=(0,0,14) rot=(0,0,1;0rad)
  Support = -> [Fillet]
  TraceSupport = false
  TreeRank = 763
FEATURE [Sketcher::SketchObject] Sketch048
  ArcFitTolerance = 1e-06
  AttachmentSupport = -> [ShapeBinder015]
  ExternalGeometry = -> [ShapeBinder015]
  FullyConstrained = true
  MapMode = 5
  Placement = pos=(0,0,14) rot=(0,0,1;0rad)
  Support = -> [ShapeBinder015]
  TreeRank = 764
  sketch-geometry (1):
    g0: LineSegment StartX=17 StartY=46.5 StartZ=0 EndX=17 EndY=42.5 EndZ=0
  constraints (4):
    c: Vertical(g0)
    c: DistanceY(g0,g0) = 4
    c: DistanceX(g-3,g0) = 2
    c: Horizontal(g0,g-3)
FEATURE [PartDesign::Plane] DatumPlane019
  AttachmentSupport = -> [Sketch048]
  Length = 17
  MapMode = 7
  MinimumLength = 10
  MinimumWidth = 10
  Placement = pos=(17,42.5,14) rot=(0,0.707107,0.707107;3.14159rad)
  ResizeMode = 0
  Support = -> [Sketch048]
  TreeRank = 765
  Width = 14
FEATURE [Part::SubShapeBinder] Import009  label="Import009(Sketch049)"
  BindCopyOnChange = 0
  BindMode = 0
  ClaimChildren = false
  Context = -> Part [Part010.Body041.Import009.]
  FillStyle = 0
  Fuse = false
  MakeFace = false
  OffsetFill = false
  OffsetIntersection = false
  OffsetJoinType = 0
  OffsetOpenResult = false
  PartialLoad = false
  Relative = true
  Support = -> [Body040[Sketch049.]]
  TreeRank = 790
  _Version = 8
FEATURE [PartDesign::Plane] DatumPlane021
  AttachmentSupport = -> [Sketch048]
  Length = 17
  MapMode = 7
  MinimumLength = 10
  MinimumWidth = 10
  Placement = pos=(17,46.5,14) rot=(0,0.707107,0.707107;3.14159rad)
  ResizeMode = 0
  Support = -> [Sketch048]
  TreeRank = 791
  Width = 14
FEATURE [PartDesign::Plane] DatumPlane022
  AttachmentSupport = -> [Sketch048]
  Length = 10
  MapMode = 7
  MinimumLength = 10
  MinimumWidth = 10
  Placement = pos=(17,42.5,14) rot=(0,0.707107,0.707107;3.14159rad)
  ResizeMode = 0
  Support = -> [Sketch048]
  TreeRank = 792
  Width = 10
FEATURE [Sketcher::SketchObject] Sketch049
  ArcFitTolerance = 1e-06
  AttachmentSupport = -> [DatumPlane022]
  FullyConstrained = true
  MapMode = 5
  Placement = pos=(17,42.5,14) rot=(0,0.707107,0.707107;3.14159rad)
  Support = -> [DatumPlane022]
  TreeRank = 768
  expr: Constraints[17] = Spreadsheet.top_shell_width
  sketch-geometry (9):
    g0: LineSegment StartX=-5 StartY=-7 StartZ=0 EndX=-3 EndY=-7 EndZ=0
    g1: LineSegment StartX=-3 StartY=-7 StartZ=0 EndX=-3 EndY=-5 EndZ=0
    g2: LineSegment StartX=-3 StartY=-5 StartZ=0 EndX=-2.5 EndY=-5 EndZ=0
    g3: LineSegment StartX=-5 StartY=-1 StartZ=0 EndX=-5 EndY=-7 EndZ=0
    g4: LineSegment [constr] StartX=-5 StartY=-1 StartZ=0 EndX=-2.5 EndY=-1 EndZ=0
    g5: LineSegment StartX=-2.5 StartY=-1 StartZ=0 EndX=-2.5 EndY=-5 EndZ=0
    g6: LineSegment StartX=-5 StartY=-1 StartZ=0 EndX=-5 EndY=-0.5 EndZ=0
    g7: LineSegment StartX=-5 StartY=-0.5 StartZ=0 EndX=-2.5 EndY=-0.5 EndZ=0
    g8: LineSegment StartX=-2.5 StartY=-0.5 StartZ=0 EndX=-2.5 EndY=-1 EndZ=0
  constraints (26):
    c: Horizontal(g0)
    c: Coincident(g0,g1)
    c: Vertical(g1)
    c: Coincident(g1,g2)
    c: Horizontal(g2)
    c: Coincident(g3,g0)
    c: Vertical(g3)
    c: DistanceY(g1,g1) = 2
    c: Coincident(g4,g3)
    c: Horizontal(g4)
    c: Coincident(g5,g4)
    c: Coincident(g5,g2)
    c: Vertical(g5)
    c: DistanceX(g2,g2) = 0.5
    c: DistanceX(g0,g0) = 2
    c: DistanceX(g4,g-1) = 2.5
    c: DistanceY(g5,g5) = 4
    c: DistanceY(g4,g-1) = 1
    c: Coincident(g3,g6)
    c: Vertical(g6)
    c: Coincident(g6,g7)
    c: Horizontal(g7)
    c: Coincident(g7,g8)
    c: Coincident(g8,g5)
    c: Vertical(g8)
    c: DistanceY(g6,g6) = 0.5
FEATURE [Sketcher::SketchObject] Sketch050
  ArcFitTolerance = 1e-06
  AttachmentSupport = -> [DatumPlane022]
  FullyConstrained = true
  MapMode = 5
  Placement = pos=(17,42.5,14) rot=(0,0.707107,0.707107;3.14159rad)
  Support = -> [DatumPlane022]
  TreeRank = 769
  sketch-geometry (1):
    g0: LineSegment StartX=0 StartY=0 StartZ=0 EndX=0 EndY=-10 EndZ=0
  constraints (3):
    c: Coincident(g0,g-1)
    c: PointOnObject(g0,g-2)
    c: DistanceY(g0,g0) = 10
FEATURE [PartDesign::Line] DatumLine006
  AttacherType = Attacher::AttachEngineLine
  AttachmentSupport = -> [Sketch050]
  Length = 14
  MapMode = 29
  MinimumLength = 10
  Placement = pos=(17,42.5,14) rot=(0,1,0;3.14159rad)
  ResizeMode = 0
  Support = -> [Sketch050]
  TreeRank = 770
FEATURE [PartDesign::Revolution] Revolution005
  AddSubType = 0
  Angle = 360
  Axis = (0,2e-16,1)
  Base = (17,42.5,14)
  ClaimChildren = false
  Fit = 0
  FitJoin = 0
  InnerFit = 0
  InnerFitJoin = 0
  Linearize = true
  NewSolid = false
  Placement = pos=(17,42.5,14) rot=(0,0.707107,0.707107;3.14159rad)
  Profile = -> Sketch049
  ReferenceAxis = -> Sketch049 [V_Axis]
  Suppress = false
  TreeRank = 771
  _ProfileBasedVersion = 1
FEATURE [PartDesign::ShapeBinder] ShapeBinder016
  Placement = pos=(17,42.5,14) rot=(0,0.707107,0.707107;3.14159rad)
  Support = -> [Sketch049]
  TraceSupport = false
  TreeRank = 784
FEATURE [PartDesign::Plane] DatumPlane020
  AttachmentSupport = -> [ShapeBinder016]
  Length = 20.5
  MapMode = 13
  MinimumLength = 10
  MinimumWidth = 10
  Placement = pos=(20.5,42.5,11.3333) rot=(1,0,0;1.5708rad)
  ResizeMode = 0
  Support = -> [ShapeBinder016]
  TreeRank = 785
  Width = 11.3333
FEATURE [Sketcher::SketchObject] Sketch051
  ArcFitTolerance = 1e-06
  AttachmentSupport = -> [DatumPlane020]
  ExternalGeometry = -> [ShapeBinder016,Import009]
  FullyConstrained = true
  MapMode = 5
  Placement = pos=(20.5,42.5,11.3333) rot=(1,0,0;1.5708rad)
  Support = -> [DatumPlane020]
  TreeRank = 786
  sketch-geometry (4):
    g0: LineSegment StartX=-1 StartY=4.16667 StartZ=0 EndX=-3.5 EndY=4.16667 EndZ=0
    g1: LineSegment StartX=-3.5 StartY=4.16667 StartZ=0 EndX=-3.5 EndY=-4.33333 EndZ=0
    g2: LineSegment StartX=-3.5 StartY=-4.33333 StartZ=0 EndX=-1 EndY=-4.33333 EndZ=0
    g3: LineSegment StartX=-1 StartY=-4.33333 StartZ=0 EndX=-1 EndY=4.16667 EndZ=0
  constraints (12):
    c: Coincident(g0,g1)
    c: Coincident(g1,g2)
    c: Coincident(g2,g3)
    c: Coincident(g3,g0)
    c: Horizontal(g0)
    c: Horizontal(g2)
    c: Vertical(g1)
    c: Vertical(g3)
    c: Horizontal(g2,g-4)
    c: DistanceX(g0,g0) = 2.5
    c: Vertical(g-3,g0)
    c: DistanceY(g-5,g0) = 2.5
FEATURE [PartDesign::Line] DatumLine007
  AttacherType = Attacher::AttachEngineLine
  AttachmentSupport = -> [Sketch051]
  Length = 10
  MapMode = 29
  MinimumLength = 10
  Placement = pos=(17,42.5,11.3333) rot=(0,1,0;3.14159rad)
  ResizeMode = 0
  Support = -> [Sketch051]
  TreeRank = 787
FEATURE [PartDesign::Revolution] Revolution006
  AddSubType = 0
  Angle = 360
  Axis = (0,0,-1)
  Base = (17,42.5,11.3333)
  ClaimChildren = false
  Fit = 0
  FitJoin = 0
  InnerFit = 0
  InnerFitJoin = 0
  Linearize = true
  NewSolid = false
  Placement = pos=(20.5,42.5,11.3333) rot=(1,0,0;1.5708rad)
  Profile = -> Sketch051
  ReferenceAxis = -> DatumLine007
  Suppress = false
  TreeRank = 788
  _ProfileBasedVersion = 1
FEATURE [PartDesign::Body] Body041  label="top light cutout"
  AutoGroupSolids = false
  ClaimAllChildren = false
  ExportMode = 0
  Group = -> [ShapeBinder016,DatumPlane020,Sketch051,DatumLine007,Revolution006,Import009]
  Origin = -> Origin043
  Tip = -> Revolution006
  TreeRank = 3266
  _ExportChildren = -> [ShapeBinder016,DatumPlane020,DatumLine007,Revolution006,Import009]
  _GroupVersion = 1
FEATURE [PartDesign::FeatureBase] Clone015
  BaseFeature = -> Body
  NewSolid = false
  Suppress = false
  TreeRank = 802
FEATURE [Part::SubShapeBinder] Import010  label="Import010(Clone015)"
  BindCopyOnChange = 0
  BindMode = 0
  ClaimChildren = false
  Context = -> Part [Part010.Body040.Import010.]
  FillStyle = 0
  Fuse = false
  MakeFace = false
  OffsetFill = false
  OffsetIntersection = false
  OffsetJoinType = 0
  OffsetOpenResult = false
  PartialLoad = false
  Relative = true
  Support = -> [Body042[Clone015.]]
  TreeRank = 808
  _Version = 8
FEATURE [PartDesign::ShapeBinder] ShapeBinder017
  Support = -> [Sketch]
  TraceSupport = false
  TreeRank = 824
FEATURE [Sketcher::SketchObject] Sketch054
  ArcFitTolerance = 1e-06
  AttachmentSupport = -> [XY_Plane045]
  ExternalGeometry = -> [ShapeBinder017]
  FullyConstrained = true
  MapMode = 5
  Support = -> [XY_Plane045]
  TreeRank = 825
  expr: Constraints[24] = Spreadsheet.top_shell_width
  expr: Constraints[26] = Spreadsheet.top_shell_width
  expr: Constraints[28] = Spreadsheet.top_shell_width
  expr: Constraints[35] = Spreadsheet.top_shell_width
  sketch-geometry (13):
    g0: LineSegment StartX=34 StartY=33.5 StartZ=0 EndX=34 EndY=-53.5 EndZ=0
    g1: LineSegment StartX=34 StartY=-53.5 StartZ=0 EndX=34 EndY=-69.0652 EndZ=0
    g2: LineSegment StartX=34 StartY=-69.0652 StartZ=0 EndX=3.818 EndY=-97.2104 EndZ=0
    g3: LineSegment StartX=3.818 StartY=-97.2104 StartZ=0 EndX=-3.818 EndY=-97.2104 EndZ=0
    g4: LineSegment StartX=-3.818 StartY=-97.2104 StartZ=0 EndX=-34 EndY=-69.0652 EndZ=0
    g5: LineSegment StartX=-34 StartY=-69.0652 StartZ=0 EndX=-34 EndY=-53.5 EndZ=0
    g6: LineSegment StartX=-34 StartY=-53.5 StartZ=0 EndX=-34 EndY=33.5 EndZ=0
    g7: LineSegment [constr] StartX=3.818 StartY=-97.2104 StartZ=0 EndX=4.5 EndY=-97.9417 EndZ=0
    g8: LineSegment [constr] StartX=-3.818 StartY=-97.2104 StartZ=0 EndX=-4.5 EndY=-97.9417 EndZ=0
    g9: LineSegment [constr] StartX=35 StartY=-53.5 StartZ=0 EndX=34 EndY=-53.5 EndZ=0
    g10: LineSegment StartX=-15 StartY=52.5 StartZ=0 EndX=15 EndY=52.5 EndZ=0
    g11: ArcOfCircle CenterX=-15 CenterY=33.5 CenterZ=0 NormalX=0 NormalY=0 NormalZ=1 AngleXU=0 Radius=19 StartAngle=1.5708 EndAngle=3.14159
    g12: ArcOfCircle CenterX=15 CenterY=33.5 CenterZ=0 NormalX=0 NormalY=0 NormalZ=1 AngleXU=0 Radius=19 StartAngle=0 EndAngle=1.5708
  constraints (36):
    c: Vertical(g0)
    c: Coincident(g0,g1)
    c: Vertical(g1)
    c: Coincident(g2,g3)
    c: Horizontal(g3)
    c: Coincident(g3,g4)
    c: Coincident(g4,g5)
    c: Vertical(g5)
    c: Coincident(g5,g6)
    c: Vertical(g6)
    c: Parallel(g2,g-9)
    c: Parallel(g4,g-10)
    c: Coincident(g7,g2)
    c: Coincident(g7,g-9)
    c: Coincident(g8,g3)
    c: Coincident(g8,g-10)
    c: Perpendicular(g-9,g7)
    c: Equal(g7,g8)
    c: Horizontal(g-8,g0)
    c: Horizontal(g5,g-7)
    c: Horizontal(g6,g-7)
    c: Horizontal(g0,g-6)
    c: Coincident(g9,g-8)
    c: Coincident(g9,g0)
    c: DistanceX(g9,g9) = 1
    c: Coincident(g1,g2)
    c: DistanceX(g-11,g5) = 1
    c: Horizontal(g10)
    c: DistanceY(g10,g-5) = 1
    c: Coincident(g11,g-5)
    c: Coincident(g11,g10)
    c: Coincident(g11,g6)
    c: Coincident(g12,g-3)
    c: Coincident(g12,g10)
    c: Coincident(g12,g0)
    c: Distance(g7) = 1
FEATURE [PartDesign::Pad] Pad011
  AddSubType = 0
  AlongSketchNormal = false
  CheckUpToFaceLimits = true
  ClaimChildren = false
  Direction = (0,0,1)
  Fit = 0
  FitJoin = 0
  InnerFit = 0
  InnerFitJoin = 0
  InnerTaperAngle = 0
  InnerTaperAngleRev = 0
  Length = 13
  Length2 = 100
  Linearize = true
  NewSolid = false
  Profile = -> Sketch054
  Suppress = false
  TreeRank = 826
  Type = 0
  _ProfileBasedVersion = 1
FEATURE [PartDesign::Plane] DatumPlane023
  AttachmentSupport = -> [Pad011]
  Length = 70
  MapMode = 5
  MinimumLength = 10
  MinimumWidth = 10
  Placement = pos=(0,0,13) rot=(0,0,1;0rad)
  ResizeMode = 0
  Support = -> [Pad011]
  TreeRank = 842
  Width = 151.442
FEATURE [PartDesign::Fillet] Fillet004
  AddSubType = 0
  Base = -> Pad011 [Edge11,Edge8]
  BaseFeature = -> Pad011
  NewSolid = false
  Radius = 4
  SupportTransform = false
  Suppress = false
  TreeRank = 843
FEATURE [PartDesign::Fillet] Fillet005
  AddSubType = 0
  Base = -> Fillet004 [Edge33,Edge3]
  BaseFeature = -> Fillet004
  NewSolid = false
  Radius = 16
  SupportTransform = false
  Suppress = false
  TreeRank = 844
FEATURE [PartDesign::Fillet] Fillet006
  AddSubType = 0
  Base = -> Fillet005 [Edge32,Edge31,Edge29,Edge27,Edge23,Edge4,Edge19,Edge22,Edge24,Edge26,Edge28,Edge30]
  BaseFeature = -> Fillet005
  NewSolid = false
  Radius = 7
  SupportTransform = false
  Suppress = false
  TreeRank = 845
FEATURE [Sketcher::SketchObject] Sketch057
  ArcFitTolerance = 1e-06
  AttachmentSupport = -> [Fillet006]
  FullyConstrained = true
  MapMode = 5
  Placement = pos=(0,0,13) rot=(0,0,1;0rad)
  Support = -> [Fillet006]
  TreeRank = 846
  sketch-geometry (4):
    g0: LineSegment StartX=-40 StartY=65 StartZ=0 EndX=40 EndY=65 EndZ=0
    g1: LineSegment StartX=40 StartY=65 StartZ=0 EndX=40 EndY=-105 EndZ=0
    g2: LineSegment StartX=40 StartY=-105 StartZ=0 EndX=-40 EndY=-105 EndZ=0
    g3: LineSegment StartX=-40 StartY=-105 StartZ=0 EndX=-40 EndY=65 EndZ=0
  constraints (11):
    c: Coincident(g0,g1)
    c: Coincident(g1,g2)
    c: Coincident(g2,g3)
    c: Coincident(g3,g0)
    c: Horizontal(g2)
    c: Vertical(g1)
    c: Vertical(g3)
    c: DistanceX(g0,g0) = 80
    c: DistanceY(g1,g1) = 170
    c: Symmetric(g0,g0,g-2)
    c: DistanceY(g-1,g0) = 65
FEATURE [PartDesign::Pocket] Pocket001
  AddSubType = 1
  BaseFeature = -> Fillet006
  CheckUpToFaceLimits = true
  ClaimChildren = false
  Fit = 0
  FitJoin = 0
  InnerFit = 0
  InnerFitJoin = 0
  InnerTaperAngle = 0
  InnerTaperAngleRev = 0
  Length = 3
  Length2 = 100
  Linearize = true
  NewSolid = false
  Profile = -> Sketch057
  Suppress = false
  TreeRank = 847
  Type = 0
  _ProfileBasedVersion = 1
  _Version = 1
  expr: Length = 3
FEATURE [Sketcher::SketchObject] Sketch058
  ArcFitTolerance = 1e-06
  AttachmentSupport = -> [Pocket001]
  ExternalGeometry = -> [Sketch054]
  FullyConstrained = true
  MapMode = 5
  Placement = pos=(0,0,10) rot=(0,0,1;0rad)
  Support = -> [Pocket001]
  TreeRank = 848
  expr: Constraints[7] = Spreadsheet.top_shell_width
  sketch-geometry (4):
    g0: LineSegment StartX=-40 StartY=-52.5 StartZ=0 EndX=40 EndY=-52.5 EndZ=0
    g1: LineSegment StartX=40 StartY=-52.5 StartZ=0 EndX=40 EndY=-102.5 EndZ=0
    g2: LineSegment StartX=40 StartY=-102.5 StartZ=0 EndX=-40 EndY=-102.5 EndZ=0
    g3: LineSegment StartX=-40 StartY=-102.5 StartZ=0 EndX=-40 EndY=-52.5 EndZ=0
  constraints (11):
    c: Coincident(g0,g1)
    c: Coincident(g1,g2)
    c: Coincident(g2,g3)
    c: Coincident(g3,g0)
    c: Horizontal(g0)
    c: Vertical(g1)
    c: Vertical(g3)
    c: DistanceY(g-3,g0) = 1
    c: Symmetric(g1,g2,g-2)
    c: DistanceX(g2,g2) = 80
    c: DistanceY(g1,g1) = 50
FEATURE [PartDesign::Pad] Pad012
  AddSubType = 0
  AlongSketchNormal = false
  BaseFeature = -> Pocket001
  CheckUpToFaceLimits = true
  ClaimChildren = false
  Direction = (0,0,-1)
  Fit = 0
  FitJoin = 0
  InnerFit = 0
  InnerFitJoin = 0
  InnerTaperAngle = 0
  InnerTaperAngleRev = 0
  Length = 1
  Length2 = 100
  Linearize = true
  NewSolid = false
  Profile = -> Pocket001 [Face4]
  Suppress = false
  TreeRank = 869
  Type = 0
  _ProfileBasedVersion = 1
FEATURE [PartDesign::Body] Body043  label="top cut out 1"
  AutoGroupSolids = false
  ClaimAllChildren = false
  ExportMode = 0
  Group = -> [ShapeBinder017,Sketch054,Pad011,Fillet004,Fillet005,Fillet006,DatumPlane023,Sketch057,Pocket001,Sketch058,Pad012]
  Origin = -> Origin045
  Tip = -> Pad012
  TreeRank = 961
  _ExportChildren = -> [ShapeBinder017,Pad011,Fillet004,Fillet005,Fillet006,DatumPlane023,Pocket001,Sketch058,Pad012]
  _GroupVersion = 1
FEATURE [PartDesign::ShapeBinder] ShapeBinder018
  Placement = pos=(0,0,14) rot=(0,0,1;0rad)
  Support = -> [Fillet]
  TraceSupport = false
  TreeRank = 942
FEATURE [Sketcher::SketchObject] Sketch059
  ArcFitTolerance = 1e-06
  AttachmentSupport = -> [Clone015]
  ExternalGeometry = -> [Clone015]
  FullyConstrained = true
  MapMode = 5
  Placement = pos=(0,0,14) rot=(0,0,1;0rad)
  Support = -> [Clone015]
  TreeRank = 956
  sketch-geometry (4):
    g0: LineSegment StartX=-40 StartY=-53.5 StartZ=0 EndX=40 EndY=-53.5 EndZ=0
    g1: LineSegment StartX=40 StartY=-53.5 StartZ=0 EndX=40 EndY=-103.5 EndZ=0
    g2: LineSegment StartX=40 StartY=-103.5 StartZ=0 EndX=-40 EndY=-103.5 EndZ=0
    g3: LineSegment StartX=-40 StartY=-103.5 StartZ=0 EndX=-40 EndY=-53.5 EndZ=0
  constraints (11):
    c: Coincident(g0,g1)
    c: Coincident(g1,g2)
    c: Coincident(g2,g3)
    c: Coincident(g3,g0)
    c: Horizontal(g2)
    c: Vertical(g1)
    c: Vertical(g3)
    c: DistanceX(g2,g2) = 80
    c: DistanceY(g1,g1) = 50
    c: Symmetric(g0,g0,g-2)
    c: Horizontal(g0,g-3)
FEATURE [PartDesign::Pocket] Pocket
  AddSubType = 1
  BaseFeature = -> Clone015
  CheckUpToFaceLimits = true
  ClaimChildren = false
  Fit = 0
  FitJoin = 0
  InnerFit = 0
  InnerFitJoin = 0
  InnerTaperAngle = 0
  InnerTaperAngleRev = 0
  Length = 3
  Length2 = 100
  Linearize = true
  NewSolid = false
  Profile = -> Sketch059
  Suppress = false
  TreeRank = 957
  Type = 0
  _ProfileBasedVersion = 1
  _Version = 1
FEATURE [PartDesign::Body] Body042  label="top"
  AutoGroupSolids = false
  BaseFeature = -> Body
  ClaimAllChildren = false
  ExportMode = 0
  Group = -> [Clone015,Sketch059,Pocket]
  Origin = -> Origin044
  Tip = -> Pocket
  TreeRank = 960
  _ExportChildren = -> [Clone015,Pocket]
  _GroupVersion = 1
FEATURE [Part::Cut] Cut003
  Base = -> Body042
  Tool = -> Body043
  TreeRank = 962
FEATURE [PartDesign::FeatureBase] Clone016
  BaseFeature = -> Fillet006
  NewSolid = false
  Suppress = false
  TreeRank = 972
FEATURE [Sketcher::SketchObject] Sketch060
  ArcFitTolerance = 1e-06
  AttachmentSupport = -> [Clone016]
  ExternalGeometry = -> [Clone016]
  FullyConstrained = true
  MapMode = 5
  Placement = pos=(0,0,13) rot=(0,0,1;0rad)
  Support = -> [Clone016]
  TreeRank = 976
  sketch-geometry (4):
    g0: LineSegment StartX=-40 StartY=-6.5 StartZ=0 EndX=40 EndY=-6.5 EndZ=0
    g1: LineSegment StartX=40 StartY=-6.5 StartZ=0 EndX=40 EndY=-106.5 EndZ=0
    g2: LineSegment StartX=40 StartY=-106.5 StartZ=0 EndX=-40 EndY=-106.5 EndZ=0
    g3: LineSegment StartX=-40 StartY=-106.5 StartZ=0 EndX=-40 EndY=-6.5 EndZ=0
  constraints (11):
    c: Coincident(g0,g1)
    c: Coincident(g1,g2)
    c: Coincident(g2,g3)
    c: Coincident(g3,g0)
    c: Horizontal(g2)
    c: Vertical(g1)
    c: Vertical(g3)
    c: Symmetric(g0,g0,g-2)
    c: DistanceY(g0,g-3) = 59
    c: DistanceY(g1,g1) = 100
    c: DistanceX(g2,g2) = 80
FEATURE [PartDesign::Pocket] Pocket002
  AddSubType = 1
  BaseFeature = -> Clone016
  CheckUpToFaceLimits = true
  ClaimChildren = false
  Fit = 0
  FitJoin = 0
  InnerFit = 0
  InnerFitJoin = 0
  InnerTaperAngle = 0
  InnerTaperAngleRev = 0
  Length = 14
  Length2 = 100
  Linearize = true
  NewSolid = false
  Profile = -> Sketch060
  Suppress = false
  TreeRank = 977
  Type = 0
  _ProfileBasedVersion = 1
  _Version = 1
FEATURE [Sketcher::SketchObject] Sketch061
  ArcFitTolerance = 1e-06
  AttachmentSupport = -> [Pocket002]
  FullyConstrained = true
  MapMode = 5
  Placement = pos=(0,0,13) rot=(0,0,1;0rad)
  Support = -> [Pocket002]
  TreeRank = 978
  sketch-geometry (4):
    g0: LineSegment StartX=-40 StartY=60 StartZ=0 EndX=40 EndY=60 EndZ=0
    g1: LineSegment StartX=40 StartY=60 StartZ=0 EndX=40 EndY=-20 EndZ=0
    g2: LineSegment StartX=40 StartY=-20 StartZ=0 EndX=-40 EndY=-20 EndZ=0
    g3: LineSegment StartX=-40 StartY=-20 StartZ=0 EndX=-40 EndY=60 EndZ=0
  constraints (11):
    c: Coincident(g0,g1)
    c: Coincident(g1,g2)
    c: Coincident(g2,g3)
    c: Coincident(g3,g0)
    c: Horizontal(g2)
    c: Vertical(g1)
    c: Vertical(g3)
    c: Symmetric(g0,g0,g-2)
    c: DistanceX(g2,g2) = 80
    c: DistanceY(g1,g1) = 80
    c: DistanceY(g-1,g0) = 60
FEATURE [PartDesign::Body] Body044
  AutoGroupSolids = false
  BaseFeature = -> Fillet006
  ClaimAllChildren = false
  ExportMode = 0
  Group = -> [Clone016,Sketch060,Pocket002,Sketch061]
  Origin = -> Origin047
  Tip = -> Pocket002
  TreeRank = 975
  _ExportChildren = -> [Clone016,Pocket002,Sketch061]
  _GroupVersion = 1
FEATURE [Part::SubShapeBinder] Import011  label="Import011(Cut004)"
  BindCopyOnChange = 0
  BindMode = 0
  ClaimChildren = false
  Context = -> Part [Part006.Body045.Import011.]
  FillStyle = 0
  Fuse = false
  MakeFace = false
  OffsetFill = false
  OffsetIntersection = false
  OffsetJoinType = 0
  OffsetOpenResult = false
  PartialLoad = false
  Relative = true
  Support = -> [Cut004]
  TreeRank = 995
  _Version = 8
FEATURE [Sketcher::SketchObject] Sketch062
  ArcFitTolerance = 1e-06
  AttachmentSupport = -> [Import011]
  FullyConstrained = true
  MapMode = 5
  Placement = pos=(0,0,11) rot=(0,0,1;0rad)
  Support = -> [Import011]
  TreeRank = 996
FEATURE [Sketcher::SketchObject] Sketch063
  ArcFitTolerance = 1e-06
  AttachmentSupport = -> [Import011]
  FullyConstrained = false
  MapMode = 5
  Placement = pos=(0,0,11) rot=(0,0,1;0rad)
  Support = -> [Import011]
  TreeRank = 997
  sketch-geometry (8):
    g0: LineSegment StartX=-23.99 StartY=8.70684 StartZ=0 EndX=23.99 EndY=8.70684 EndZ=0
    g1: LineSegment StartX=26.99 StartY=5.70684 StartZ=0 EndX=26.99 EndY=-73.8932 EndZ=0
    g2: LineSegment StartX=23.99 StartY=-76.8932 StartZ=0 EndX=-23.99 EndY=-76.8932 EndZ=0
    g3: LineSegment StartX=-26.99 StartY=-73.8932 StartZ=0 EndX=-26.99 EndY=5.70684 EndZ=0
    g4: ArcOfCircle CenterX=23.99 CenterY=5.70684 CenterZ=0 NormalX=0 NormalY=0 NormalZ=1 AngleXU=0 Radius=3 StartAngle=0 EndAngle=1.5708
    g5: ArcOfCircle CenterX=-23.99 CenterY=5.70684 CenterZ=0 NormalX=0 NormalY=0 NormalZ=1 AngleXU=0 Radius=3 StartAngle=1.5708 EndAngle=3.14159
    g6: ArcOfCircle CenterX=-23.99 CenterY=-73.8932 CenterZ=0 NormalX=0 NormalY=0 NormalZ=1 AngleXU=0 Radius=3 StartAngle=3.14159 EndAngle=4.71239
    g7: ArcOfCircle CenterX=23.99 CenterY=-73.8932 CenterZ=0 NormalX=0 NormalY=0 NormalZ=1 AngleXU=0 Radius=3 StartAngle=4.71239 EndAngle=6.28319
  constraints (18):
    c: Horizontal(g2)
    c: Vertical(g1)
    c: Vertical(g3)
    c: Tangent(g0,g4) = 1.5708
    c: Tangent(g1,g4) = 1.5708
    c: Tangent(g0,g5) = 1.5708
    c: Tangent(g3,g5) = 1.5708
    c: Tangent(g3,g6) = 1.5708
    c: Tangent(g2,g6) = 1.5708
    c: Tangent(g2,g7) = 1.5708
    c: Tangent(g1,g7) = 1.5708
    c: Radius(g7) = 3
    c: Radius(g6) = 3
    c: Radius(g5) = 3
    c: Radius(g4) = 3
    c: DistanceX(g3,g1) = 53.98
    c: DistanceY(g2,g0) = 85.6
    c: Symmetric(g0,g0,g-2)
FEATURE [PartDesign::Body] Body045  label="card"
  AutoGroupSolids = false
  ClaimAllChildren = false
  ExportMode = 0
  Group = -> [Import011,Sketch062,Sketch063]
  Origin = -> Origin048
  TreeRank = 992
  _ExportChildren = -> [Import011,Sketch062,Sketch063]
  _GroupVersion = 1
FEATURE [Part::SubShapeBinder] Import012  label="Import012(Cut004)"
  BindCopyOnChange = 0
  BindMode = 0
  ClaimChildren = false
  Context = -> Part [Body046.Import012.]
  FillStyle = 0
  Fuse = false
  MakeFace = false
  OffsetFill = false
  OffsetIntersection = false
  OffsetJoinType = 0
  OffsetOpenResult = false
  PartialLoad = false
  Relative = true
  Support = -> [Cut004]
  TreeRank = 1015
  _Version = 8
FEATURE [PartDesign::ShapeBinder] ShapeBinder019
  Support = -> [Fillet]
  TraceSupport = false
  TreeRank = 1016
FEATURE [Sketcher::SketchObject] Sketch009
  ArcFitTolerance = 0
  AttachmentSupport = -> [XY_Plane005]
  ExternalGeometry = -> [ShapeBinder018,ShapeBinder019]
  FullyConstrained = true
  MapMode = 5
  Support = -> [XY_Plane005]
  TreeRank = 6
  sketch-geometry (7):
    g0: LineSegment [constr] StartX=-50 StartY=37.5 StartZ=0 EndX=50 EndY=37.5 EndZ=0
    g1: GeomPoint [constr] X=-27.3693 Y=37.5 Z=0
    g2: GeomPoint [constr] X=27.3693 Y=37.5 Z=0
    g3: LineSegment StartX=-27.3693 StartY=37.5 StartZ=0 EndX=-27.3693 EndY=47.5 EndZ=0
    g4: LineSegment StartX=27.3693 StartY=37.5 StartZ=0 EndX=27.3693 EndY=47.5 EndZ=0
    g5: LineSegment StartX=-34.5959 StartY=37.5 StartZ=0 EndX=-34.5959 EndY=47.5 EndZ=0
    g6: LineSegment StartX=34.5959 StartY=37.5 StartZ=0 EndX=34.5959 EndY=47.5 EndZ=0
  constraints (21):
    c: DistanceX(g0,g0) = 100
    c: DistanceY(g-1,g0) = 37.5
    c: Symmetric(g0,g0,g-2)
    c: PointOnObject(g1,g0)
    c: PointOnObject(g2,g0)
    c: Coincident(g3,g1)
    c: Vertical(g3)
    c: Coincident(g4,g2)
    c: Vertical(g4)
    c: DistanceY(g3,g3) = 10
    c: DistanceY(g4,g4) = 10
    c: PointOnObject(g4,g-3)
    c: PointOnObject(g3,g-4)
    c: Vertical(g5)
    c: PointOnObject(g5,g0)
    c: PointOnObject(g5,g-5)
    c: DistanceY(g5,g5) = 10
    c: Vertical(g6)
    c: PointOnObject(g6,g0)
    c: PointOnObject(g6,g-6)
    c: DistanceY(g6,g6) = 10
FEATURE [PartDesign::Plane] DatumPlane
  AttachmentSupport = -> [Sketch009]
  Length = 70.9918
  MapMode = 7
  MinimumLength = 10
  MinimumWidth = 10
  Placement = pos=(-27.3693,37.5,0) rot=(1,0,0;1.5708rad)
  ResizeMode = 0
  Support = -> [Sketch009]
  TreeRank = 6
  Width = 14.9
FEATURE [Sketcher::SketchObject] Sketch010
  ArcFitTolerance = 0
  AttachmentSupport = -> [DatumPlane]
  ExternalGeometry = -> [Sketch009,ShapeBinder018]
  FullyConstrained = true
  MapMode = 5
  Placement = pos=(-27.3693,37.5,0) rot=(1,0,0;1.5708rad)
  Support = -> [DatumPlane]
  TreeRank = 10
  sketch-geometry (5):
    g0: ArcOfCircle CenterX=0 CenterY=6.7734 CenterZ=0 NormalX=0 NormalY=0 NormalZ=1 AngleXU=0 Radius=7.2266 StartAngle=1.5708 EndAngle=3.14159
    g1: ArcOfCircle CenterX=54.7386 CenterY=6.7734 CenterZ=0 NormalX=0 NormalY=0 NormalZ=1 AngleXU=0 Radius=7.2266 StartAngle=-5.3e-15 EndAngle=1.5708
    g2: LineSegment StartX=2.84e-14 StartY=14 StartZ=0 EndX=54.7386 EndY=14 EndZ=0
    g3: LineSegment StartX=-7.2266 StartY=6.7734 StartZ=0 EndX=-7.2266 EndY=0 EndZ=0
    g4: LineSegment StartX=61.9652 StartY=6.7734 StartZ=0 EndX=61.9652 EndY=0 EndZ=0
  constraints (14):
    c: Vertical(g4)
    c: Tangent(g4,g1) = 1.5708
    c: Tangent(g3,g0) = -1.5708
    c: Horizontal(g4,g-4)
    c: Horizontal(g3,g4)
    c: Vertical(g1,g-4)
    c: Horizontal(g2)
    c: Tangent(g2,g1) = 1.5708
    c: Tangent(g0,g2) = 1.5708
    c: Vertical(g-6,g3)
    c: Vertical(g-7,g4)
    c: Vertical(g0,g3)
    c: Vertical(g0,g-3)
    c: Horizontal(g1,g-5)
FEATURE [Sketcher::SketchObject] Sketch011
  ArcFitTolerance = 1e-06
  AttachmentSupport = -> [XY_Plane005]
  ExternalGeometry = -> [Sketch010]
  FullyConstrained = true
  MapMode = 5
  Support = -> [XY_Plane005]
  TreeRank = 9
  expr: Constraints[1] = Spreadsheet.groove_radius
  expr: Constraints[2] = Spreadsheet.groove_lift
  sketch-geometry (1):
    g0: Circle CenterX=-34.8959 CenterY=37.5 CenterZ=0 NormalX=0 NormalY=0 NormalZ=1 AngleXU=0 Radius=0.7
  constraints (3):
    c: Horizontal(g-3,g0)
    c: Radius(g0) = 0.7
    c: DistanceX(g0,g-3) = 0.3
FEATURE [PartDesign::AdditivePipe] Pipe
  AddSubType = 0
  AuxilleryCurvelinear = true
  AuxillerySpineTangent = false
  Binormal = (0,0,0)
  ClaimChildren = false
  Fit = 0
  FitJoin = 0
  InnerFit = 0
  InnerFitJoin = 0
  Linearize = true
  Mode = 0
  NewSolid = false
  Profile = -> Sketch011
  Spine = -> Sketch010 [Edge5,Edge4,Edge3,Edge2,Edge1]
  SpineTangent = false
  Suppress = false
  Transformation = 0
  Transition = 1
  TreeRank = 11
  _ProfileBasedVersion = 2
FEATURE [PartDesign::Body] Body005  label="top groove"
  AutoGroupSolids = false
  ClaimAllChildren = false
  ExportMode = 0
  Group = -> [Sketch009,Binder,Sketch010,DatumPlane,Sketch011,Pipe,ShapeBinder018,ShapeBinder019]
  Origin = -> Origin005
  Tip = -> Pipe
  TreeRank = 3254
  _ExportChildren = -> [Sketch009,Binder,DatumPlane,Pipe,ShapeBinder018,ShapeBinder019]
  _GroupVersion = 1
FEATURE [Part::SubShapeBinder] Import013  label="Import013(Cut004)"
  BindCopyOnChange = 0
  BindMode = 0
  ClaimChildren = false
  Context = -> Body047 [Import013.]
  FillStyle = 0
  Fuse = false
  MakeFace = false
  OffsetFill = false
  OffsetIntersection = false
  OffsetJoinType = 0
  OffsetOpenResult = false
  PartialLoad = false
  Relative = true
  Support = -> [Cut004]
  TreeRank = 1031
  _Version = 8
FEATURE [Sketcher::SketchObject] Sketch065
  ArcFitTolerance = 1e-06
  AttachmentSupport = -> [Import013]
  ExternalGeometry = -> [Import013]
  FullyConstrained = true
  MapMode = 5
  Placement = pos=(0,-53.5,0) rot=(1,0,0;1.5708rad)
  Support = -> [Import013]
  TreeRank = 1032
  expr: Constraints[8] = Spreadsheet.card_thickness
  expr: Constraints[9] = Spreadsheet.card_len
  sketch-geometry (4):
    g0: LineSegment StartX=-26.99 StartY=12.2 StartZ=0 EndX=26.99 EndY=12.2 EndZ=0
    g1: LineSegment StartX=26.99 StartY=12.2 StartZ=0 EndX=26.99 EndY=11 EndZ=0
    g2: LineSegment StartX=26.99 StartY=11 StartZ=0 EndX=-26.99 EndY=11 EndZ=0
    g3: LineSegment StartX=-26.99 StartY=11 StartZ=0 EndX=-26.99 EndY=12.2 EndZ=0
  constraints (11):
    c: Coincident(g0,g1)
    c: Coincident(g1,g2)
    c: Coincident(g2,g3)
    c: Coincident(g3,g0)
    c: Horizontal(g2)
    c: Vertical(g1)
    c: Vertical(g3)
    c: Symmetric(g0,g0,g-2)
    c: DistanceY(g1,g1) = 1.2
    c: DistanceX(g2,g2) = 53.98
    c: Horizontal(g2,g-3)
FEATURE [PartDesign::Pad] Pad013
  AddSubType = 0
  AlongSketchNormal = false
  CheckUpToFaceLimits = true
  ClaimChildren = false
  Direction = (0,-1,2e-16)
  Fit = 0
  FitJoin = 0
  InnerFit = 0
  InnerFitJoin = 0
  InnerTaperAngle = 0
  InnerTaperAngleRev = 0
  Length = 60
  Length2 = 100
  Linearize = true
  NewSolid = false
  Profile = -> Sketch065
  Reversed = true
  Suppress = false
  TreeRank = 1034
  Type = 0
  _ProfileBasedVersion = 1
FEATURE [Part::SubShapeBinder] Import015  label="Import015(Cut005)"
  BindCopyOnChange = 0
  BindMode = 0
  ClaimChildren = false
  Context = -> Part002 [Body049.Import015.]
  FillStyle = 0
  Fuse = false
  MakeFace = false
  OffsetFill = false
  OffsetIntersection = false
  OffsetJoinType = 0
  OffsetOpenResult = false
  PartialLoad = false
  Relative = true
  Support = -> [Cut005]
  TreeRank = 1091
  _Version = 8
FEATURE [Part::SubShapeBinder] Import016  label="Import016(Sketch064)"
  BindCopyOnChange = 0
  BindMode = 0
  ClaimChildren = false
  Context = -> Part002 [Body049.Import016.]
  FillStyle = 0
  Fuse = false
  MakeFace = false
  OffsetFill = false
  OffsetIntersection = false
  OffsetJoinType = 0
  OffsetOpenResult = false
  PartialLoad = false
  Relative = true
  Support = -> [Body046[Sketch064.]]
  TreeRank = 1092
  _Version = 8
FEATURE [Part::SubShapeBinder] Import017  label="Import017(Sketch064)"
  BindCopyOnChange = 0
  BindMode = 0
  ClaimChildren = false
  Context = -> Part002 [Body048.Import017.]
  FillStyle = 0
  Fuse = false
  MakeFace = false
  OffsetFill = false
  OffsetIntersection = false
  OffsetJoinType = 0
  OffsetOpenResult = false
  PartialLoad = false
  Relative = true
  Support = -> [Body046[Sketch064.]]
  TreeRank = 1094
  _Version = 8
FEATURE [Part::SubShapeBinder] Import018  label="Import018(Draft001)"
  BindCopyOnChange = 0
  BindMode = 0
  ClaimChildren = false
  Context = -> Part002 [Body049.Import018.]
  FillStyle = 0
  Fuse = false
  MakeFace = false
  OffsetFill = false
  OffsetIntersection = false
  OffsetJoinType = 0
  OffsetOpenResult = false
  PartialLoad = false
  Relative = true
  Support = -> [Body048[Draft001.]]
  TreeRank = 1103
  _Version = 8
FEATURE [Sketcher::SketchObject] Sketch069
  ArcFitTolerance = 1e-06
  AttachmentSupport = -> [YZ_Plane052]
  ExternalGeometry = -> [Import015,Import018]
  FullyConstrained = true
  MapMode = 5
  Placement = pos=(0,0,0) rot=(0.57735,0.57735,0.57735;2.0944rad)
  Support = -> [YZ_Plane052]
  TreeRank = 1090
  expr: Constraints[9] = Spreadsheet.thumbstick_width / 2
  sketch-geometry (3):
    g0: LineSegment StartX=19.5 StartY=4.18436 StartZ=0 EndX=19.5 EndY=34.1844 EndZ=0
    g1: LineSegment StartX=19.5 StartY=4.18436 StartZ=0 EndX=7.77807 EndY=31.7995 EndZ=0
    g2: LineSegment [constr] StartX=14.9552 StartY=14.8911 StartZ=0 EndX=10.5 EndY=13 EndZ=0
  constraints (10):
    c: Vertical(g0)
    c: Angle(g0,g1) = 0.401426
    c: DistanceX(g0,g-3) = 34
    c: Coincident(g0,g1)
    c: DistanceY(g0,g0) = 30
    c: Distance(g1) = 30
    c: PointOnObject(g2,g1)
    c: Coincident(g2,g-4)
    c: Perpendicular(g1,g2)
    c: Distance(g2) = 4.84
FEATURE [PartDesign::Body] Body049  label="joystick origin"
  AutoGroupSolids = false
  ClaimAllChildren = false
  ExportMode = 0
  Group = -> [Sketch069,Import015,Import016,Import018]
  Origin = -> Origin052
  TreeRank = 1089
  _ExportChildren = -> [Sketch069,Import015,Import016,Import018]
  _GroupVersion = 1
FEATURE [Part::SubShapeBinder] Import019  label="Import019(Cut005)"
  BindCopyOnChange = 0
  BindMode = 0
  ClaimChildren = false
  Context = -> Part002 [Body048.Import019.]
  FillStyle = 0
  Fuse = false
  MakeFace = false
  OffsetFill = false
  OffsetIntersection = false
  OffsetJoinType = 0
  OffsetOpenResult = false
  PartialLoad = false
  Relative = true
  Support = -> [Cut005]
  TreeRank = 1106
  _Version = 8
FEATURE [Sketcher::SketchObject] Sketch073
  ArcFitTolerance = 1e-06
  AttachmentSupport = -> [Import019]
  FullyConstrained = true
  MapMode = 5
  Placement = pos=(0,0,11) rot=(0,0,1;0rad)
  Support = -> [Import019]
  TreeRank = 1107
FEATURE [Part::SubShapeBinder] Import020  label="Import020(Fillet)"
  BindCopyOnChange = 0
  BindMode = 0
  ClaimChildren = false
  Context = -> Part [Part011.Body051.Import020.]
  FillStyle = 0
  Fuse = false
  MakeFace = false
  OffsetFill = false
  OffsetIntersection = false
  OffsetJoinType = 0
  OffsetOpenResult = false
  PartialLoad = false
  Relative = true
  Support = -> [Body[Fillet.]]
  TreeRank = 1137
  _Version = 8
FEATURE [Sketcher::SketchObject] Sketch074
  ArcFitTolerance = 1e-06
  AttachmentSupport = -> [Import020]
  FullyConstrained = true
  MapMode = 5
  Placement = pos=(-35,0,0) rot=(0.57735,-0.57735,-0.57735;2.0944rad)
  Support = -> [Import020]
  TreeRank = 1138
  expr: Constraints[104] = Spreadsheet.side_emboss_thickness
  expr: Constraints[109] = Spreadsheet.side_emboss_thickness
  expr: Constraints[128] = Spreadsheet.side_emboss_thickness
  expr: Constraints[129] = Spreadsheet.side_emboss_thickness
  expr: Constraints[130] = Spreadsheet.side_emboss_thickness
  expr: Constraints[157] = Spreadsheet.side_emboss_thickness
  expr: Constraints[24] = Spreadsheet.side_emboss_thickness
  expr: Constraints[35] = Spreadsheet.side_emboss_thickness
  expr: Constraints[78] = Spreadsheet.side_emboss_thickness
  expr: Constraints[84] = Spreadsheet.side_emboss_thickness
  expr: Constraints[86] = Spreadsheet.side_emboss_thickness - 0.2
  sketch-geometry (56):
    g0: LineSegment [constr] StartX=-17.25 StartY=2.4 StartZ=0 EndX=17.25 EndY=2.4 EndZ=0
    g1: LineSegment [constr] StartX=17.25 StartY=2.4 StartZ=0 EndX=17.25 EndY=-2.4 EndZ=0
    g2: LineSegment [constr] StartX=17.25 StartY=-2.4 StartZ=0 EndX=-17.25 EndY=-2.4 EndZ=0
    g3: LineSegment [constr] StartX=-17.25 StartY=-2.4 StartZ=0 EndX=-17.25 EndY=2.4 EndZ=0
    g4: LineSegment StartX=-16.25 StartY=0.129822 StartZ=0 EndX=-16.25 EndY=2.4 EndZ=0
    g5: LineSegment StartX=-16.25 StartY=2.4 StartZ=0 EndX=-15.25 EndY=2.4 EndZ=0
    g6: LineSegment StartX=-15.25 StartY=2.4 StartZ=0 EndX=-15.25 EndY=0.129822 EndZ=0
    g7: ArcOfCircle CenterX=-17.85 CenterY=0.129822 CenterZ=0 NormalX=0 NormalY=0 NormalZ=1 AngleXU=0 Radius=1.6 StartAngle=5.09679 EndAngle=6.28319
    g8: ArcOfCircle CenterX=-17.85 CenterY=0.129822 CenterZ=0 NormalX=0 NormalY=0 NormalZ=1 AngleXU=0 Radius=2.6 StartAngle=4.94526 EndAngle=6.28319
    g9: LineSegment StartX=-17.25 StartY=-1.35342 StartZ=0 EndX=-17.25 EndY=-2.4 EndZ=0
    g10: ArcOfCircle CenterX=-13.25 CenterY=1 CenterZ=0 NormalX=0 NormalY=0 NormalZ=1 AngleXU=0 Radius=0.6 StartAngle=1.5708 EndAngle=3.14159
    g11: ArcOfCircle CenterX=-13.45 CenterY=1 CenterZ=0 NormalX=0 NormalY=0 NormalZ=1 AngleXU=0 Radius=1.4 StartAngle=1.5708 EndAngle=3.14159
    g12: ArcOfCircle CenterX=-12.45 CenterY=1.2 CenterZ=0 NormalX=0 NormalY=0 NormalZ=1 AngleXU=0 Radius=0.4 StartAngle=0 EndAngle=1.5708
    g13: ArcOfCircle CenterX=-12.25 CenterY=1.2 CenterZ=0 NormalX=0 NormalY=0 NormalZ=1 AngleXU=0 Radius=1.2 StartAngle=0 EndAngle=1.5708
    g14: ArcOfCircle CenterX=-13.05 CenterY=-0.463508 CenterZ=0 NormalX=0 NormalY=0 NormalZ=1 AngleXU=0 Radius=1 StartAngle=5.23599 EndAngle=6.28319
    g15: ArcOfCircle CenterX=-13.05 CenterY=-0.463508 CenterZ=0 NormalX=0 NormalY=0 NormalZ=1 AngleXU=0 Radius=2 StartAngle=4.96507 EndAngle=6.28319
    g16: LineSegment StartX=-12.05 StartY=1.2 StartZ=0 EndX=-12.05 EndY=-0.463508 EndZ=0
    g17: LineSegment StartX=-11.05 StartY=1.2 StartZ=0 EndX=-11.05 EndY=-0.463508 EndZ=0
    g18: LineSegment [constr] StartX=-12.45 StartY=1.6 StartZ=0 EndX=-13.25 EndY=1.6 EndZ=0
    g19: LineSegment [constr] StartX=-12.25 StartY=2.4 StartZ=0 EndX=-13.45 EndY=2.4 EndZ=0
    g20: LineSegment StartX=-13.85 StartY=1 StartZ=0 EndX=-14.85 EndY=1 EndZ=0
    g21: LineSegment StartX=-12.55 StartY=-1.32953 StartZ=0 EndX=-12.55 EndY=-2.4 EndZ=0
    g22: LineSegment StartX=-13.45 StartY=2.4 StartZ=0 EndX=-13.15 EndY=2.4 EndZ=0
    g23: LineSegment StartX=-13.15 StartY=2.4 StartZ=0 EndX=-13.15 EndY=1.6 EndZ=0
    g24: LineSegment StartX=-13.15 StartY=1.6 StartZ=0 EndX=-13.25 EndY=1.6 EndZ=0
    g25: LineSegment StartX=-12.55 StartY=1.6 StartZ=0 EndX=-12.45 EndY=1.6 EndZ=0
    g26: LineSegment StartX=-12.25 StartY=2.4 StartZ=0 EndX=-12.55 EndY=2.4 EndZ=0
    g27: LineSegment StartX=-12.55 StartY=2.4 StartZ=0 EndX=-12.55 EndY=1.6 EndZ=0
    g28: LineSegment StartX=-10.25 StartY=2.4 StartZ=0 EndX=-9.25 EndY=2.4 EndZ=0
    g29: LineSegment StartX=-9.25 StartY=2.4 StartZ=0 EndX=-9.25 EndY=-2.4 EndZ=0
    g30: LineSegment StartX=-9.25 StartY=-2.4 StartZ=0 EndX=-10.25 EndY=-2.4 EndZ=0
    g31: LineSegment StartX=-10.25 StartY=-2.4 StartZ=0 EndX=-10.25 EndY=2.4 EndZ=0
    g32: ArcOfCircle CenterX=-6.55 CenterY=0.510556 CenterZ=0 NormalX=0 NormalY=0 NormalZ=1 AngleXU=0 Radius=1.9 StartAngle=1.67625 EndAngle=3.14159
    g33: ArcOfCircle CenterX=-6.53492 CenterY=0.510556 CenterZ=0 NormalX=0 NormalY=0 NormalZ=1 AngleXU=0 Radius=0.915079 StartAngle=1.80806 EndAngle=3.14159
    g34: ArcOfCircle CenterX=-6.53492 CenterY=-0.510556 CenterZ=0 NormalX=0 NormalY=0 NormalZ=1 AngleXU=0 Radius=0.915079 StartAngle=3.14159 EndAngle=4.47513
    g35: ArcOfCircle CenterX=-6.55 CenterY=-0.510556 CenterZ=0 NormalX=0 NormalY=0 NormalZ=1 AngleXU=0 Radius=1.9 StartAngle=3.14159 EndAngle=4.60693
    g36: LineSegment StartX=-8.45 StartY=0.510556 StartZ=0 EndX=-8.45 EndY=-0.510556 EndZ=0
    g37: LineSegment StartX=-7.45 StartY=0.510556 StartZ=0 EndX=-7.45 EndY=-0.510556 EndZ=0
    g38: LineSegment StartX=-6.75 StartY=1.4 StartZ=0 EndX=-6.75 EndY=2.4 EndZ=0
    g39: LineSegment StartX=-6.75 StartY=-1.4 StartZ=0 EndX=-6.75 EndY=-2.4 EndZ=0
    g40: ArcOfCircle CenterX=-4.03492 CenterY=0.510556 CenterZ=0 NormalX=0 NormalY=0 NormalZ=1 AngleXU=0 Radius=0.915079 StartAngle=1.80806 EndAngle=3.14159
    g41: ArcOfCircle CenterX=-4.05 CenterY=0.510556 CenterZ=0 NormalX=0 NormalY=0 NormalZ=1 AngleXU=0 Radius=1.9 StartAngle=1.67625 EndAngle=3.14159
    g42: ArcOfCircle CenterX=-4.03492 CenterY=-0.510556 CenterZ=0 NormalX=0 NormalY=0 NormalZ=1 AngleXU=0 Radius=0.915079 StartAngle=3.14159 EndAngle=4.47513
    g43: ArcOfCircle CenterX=-4.05 CenterY=-0.510556 CenterZ=0 NormalX=0 NormalY=0 NormalZ=1 AngleXU=0 Radius=1.9 StartAngle=3.14159 EndAngle=4.60693
    g44: ArcOfCircle CenterX=-3.66508 CenterY=0.510556 CenterZ=0 NormalX=0 NormalY=0 NormalZ=1 AngleXU=0 Radius=0.915079 StartAngle=0 EndAngle=1.33354
    g45: ArcOfCircle CenterX=-3.65 CenterY=0.510556 CenterZ=0 NormalX=0 NormalY=0 NormalZ=1 AngleXU=0 Radius=1.9 StartAngle=0 EndAngle=1.46534
    g46: ArcOfCircle CenterX=-3.66508 CenterY=-0.510556 CenterZ=0 NormalX=0 NormalY=0 NormalZ=1 AngleXU=0 Radius=0.915079 StartAngle=4.94965 EndAngle=6.28319
    g47: ArcOfCircle CenterX=-3.65 CenterY=-0.510556 CenterZ=0 NormalX=0 NormalY=0 NormalZ=1 AngleXU=0 Radius=1.9 StartAngle=4.81785 EndAngle=6.28319
    g48: LineSegment StartX=-5.95 StartY=0.510556 StartZ=0 EndX=-5.95 EndY=-0.510556 EndZ=0
    g49: LineSegment StartX=-4.95 StartY=0.510556 StartZ=0 EndX=-4.95 EndY=-0.510556 EndZ=0
    g50: LineSegment StartX=-2.75 StartY=0.510556 StartZ=0 EndX=-2.75 EndY=-0.510556 EndZ=0
    g51: LineSegment StartX=-1.75 StartY=0.510556 StartZ=0 EndX=-1.75 EndY=-0.510556 EndZ=0
    g52: LineSegment StartX=-4.25 StartY=2.4 StartZ=0 EndX=-4.25 EndY=1.4 EndZ=0
    g53: LineSegment StartX=-4.25 StartY=-1.4 StartZ=0 EndX=-4.25 EndY=-2.4 EndZ=0
    g54: LineSegment StartX=-3.45 StartY=2.4 StartZ=0 EndX=-3.45 EndY=1.4 EndZ=0
    g55: LineSegment StartX=-3.45 StartY=-1.4 StartZ=0 EndX=-3.45 EndY=-2.4 EndZ=0
  constraints (163):
    c: Coincident(g0,g1)
    c: Coincident(g1,g2)
    c: Coincident(g2,g3)
    c: Coincident(g3,g0)
    c: Horizontal(g0)
    c: Horizontal(g2)
    c: Vertical(g1)
    c: Vertical(g3)
    c: Symmetric(g0,g2,g-1)
    c: DistanceX(g0,g0) = 34.5
    c: DistanceY(g3,g3) = 4.8
    c: Vertical(g4)
    c: Coincident(g4,g5)
    c: Horizontal(g5)
    c: Coincident(g5,g6)
    c: Vertical(g6)
    c: Coincident(g7,g4)
    c: Coincident(g8,g7)
    c: Coincident(g8,g6)
    c: Coincident(g9,g7)
    c: Coincident(g9,g8)
    c: Horizontal(g7,g4)
    c: Vertical(g7,g8)
    c: Horizontal(g6,g4)
    c: DistanceX(g5,g5) = 1
    c: Horizontal(g4,g0)
    c: Horizontal(g2,g8)
    c: Vertical(g8,g2)
    c: DistanceX(g0,g5) = 2
    c: Radius(g7) = 1.6
    c: Vertical(g16)
    c: Coincident(g20,g10)
    c: Coincident(g20,g11)
    c: Coincident(g21,g14)
    c: Coincident(g21,g15)
    c: DistanceX(g20,g20) = 1
    c: Vertical(g21)
    c: Tangent(g16,g14) = 1.5708
    c: Tangent(g17,g15) = 1.5708
    c: Tangent(g17,g13) = 1.5708
    c: Tangent(g16,g12) = 1.5708
    c: Tangent(g19,g13) = -1.5708
    c: Tangent(g19,g11) = -1.5708
    c: Horizontal(g20)
    c: Horizontal(g19)
    c: Vertical(g17)
    c: PointOnObject(g11,g0)
    c: DistanceX(g11,g13) = 3.8
    c: DistanceX(g5,g11) = 0.4
    c: PointOnObject(g15,g2)
    c: Tangent(g11,g22) = 1.5708
    c: Coincident(g22,g23)
    c: PointOnObject(g23,g18)
    c: Vertical(g23)
    c: Coincident(g23,g24)
    c: PointOnObject(g25,g18)
    c: Tangent(g13,g26) = -1.5708
    c: Coincident(g26,g27)
    c: Vertical(g27)
    c: Coincident(g25,g27)
    c: DistanceX(g22,g26) = 0.6
    c: DistanceY(g10,g11) = 1.4
    c: Radius(g13) = 1.2
    c: Radius(g15) = 2
    c: Vertical(g14,g25)
    c: Radius(g11) = 1.4
    c: Equal(g24,g25)
    c: Coincident(g28,g29)
    c: Coincident(g29,g30)
    c: Coincident(g30,g31)
    c: Coincident(g31,g28)
    c: Horizontal(g28)
    c: Horizontal(g30)
    c: Vertical(g29)
    c: Vertical(g31)
    c: PointOnObject(g28,g0)
    c: PointOnObject(g29,g2)
    c: DistanceX(g15,g30) = 0.8
    c: DistanceX(g30,g30) = 1
    c: Coincident(g18,g10)
    c: Tangent(g24,g10) = -1.5708
    c: Horizontal(g18)
    c: Tangent(g25,g12) = 1.5708
    c: Coincident(g12,g18)
    c: DistanceX(g12,g13) = 1
    c: Equal(g26,g22)
    c: DistanceY(g23,g23) = 0.8
    c: Horizontal(g10,g10)
    c: Coincident(g14,g15)
    c: Vertical(g36)
    c: Vertical(g37)
    c: Coincident(g38,g33)
    c: Coincident(g38,g32)
    c: Coincident(g39,g34)
    c: Coincident(g39,g35)
    c: Vertical(g39)
    c: DistanceX(g29,g35) = 0.8
    c: Horizontal(g34,g35)
    c: Horizontal(g33,g32)
    c: Vertical(g38)
    c: PointOnObject(g32,g0)
    c: PointOnObject(g35,g2)
    c: Tangent(g36,g35) = -1.5708
    c: Tangent(g36,g32) = -1.5708
    c: DistanceX(g32,g33) = 1
    c: Vertical(g33,g34)
    c: DistanceX(g32,g32) = 1.7
    c: Tangent(g37,g33) = -1.5708
    c: Tangent(g37,g34) = -1.5708
    c: DistanceY(g38,g38) = 1
    c: Equal(g38,g39)
    c: Radius(g32) = 1.9
    c: Radius(g35) = 1.9
    c: Tangent(g49,g42) = -1.5708
    c: Tangent(g49,g40) = -1.5708
    c: Tangent(g48,g41) = -1.5708
    c: Tangent(g48,g43) = -1.5708
    c: Tangent(g50,g46) = 1.5708
    c: Tangent(g51,g47) = 1.5708
    c: Tangent(g51,g45) = 1.5708
    c: Tangent(g50,g44) = 1.5708
    c: DistanceX(g34,g43) = 0.8
    c: Vertical(g48)
    c: Vertical(g49)
    c: Vertical(g50)
    c: Vertical(g51)
    c: PointOnObject(g43,g2)
    c: PointOnObject(g41,g0)
    c: DistanceX(g41,g40) = 1
    c: DistanceY(g40,g41) = 1
    c: DistanceY(g43,g42) = 1
    c: Radius(g41) = 1.9
    c: DistanceX(g41,g41) = 1.7
    c: Vertical(g43,g41)
    c: Vertical(g40,g41)
    c: Vertical(g42,g43)
    c: Vertical(g45,g47)
    c: PointOnObject(g47,g2)
    c: DistanceX(g45,g45) = 1.7
    c: PointOnObject(g45,g0)
    c: Radius(g45) = 1.9
    c: Radius(g47) = 1.9
    c: Radius(g43) = 1.9
    c: Coincident(g52,g40)
    c: Vertical(g52)
    c: Coincident(g53,g42)
    c: Vertical(g53)
    c: Coincident(g54,g45)
    c: Coincident(g54,g44)
    c: Coincident(g55,g46)
    c: Coincident(g55,g47)
    c: Vertical(g55)
    c: Vertical(g54)
    c: Equal(g55,g53)
    c: Equal(g54,g52)
    c: PointOnObject(g53,g2)
    c: DistanceX(g40,g44) = 0.8
    c: DistanceX(g44,g45) = 1
    c: PointOnObject(g52,g0)
    c: Horizontal(g40,g41)
    c: Horizontal(g43,g42)
    c: Horizontal(g44,g45)
    c: Horizontal(g46,g47)
FEATURE [Sketcher::SketchObject] Sketch075
  ArcFitTolerance = 1e-06
  AttachmentSupport = -> [Import020]
  ExternalGeometry = -> [Sketch074]
  FullyConstrained = true
  MapMode = 5
  Placement = pos=(-35,0,0) rot=(0.57735,-0.57735,-0.57735;2.0944rad)
  Support = -> [Import020]
  TreeRank = 1139
  expr: Constraints[26] = Spreadsheet.side_emboss_thickness
  expr: Constraints[27] = Spreadsheet.side_emboss_thickness
  expr: Constraints[38] = Spreadsheet.side_emboss_thickness - 0.2
  expr: Constraints[68] = Spreadsheet.side_emboss_thickness
  expr: Constraints[69] = Spreadsheet.side_emboss_thickness
  expr: Constraints[70] = Spreadsheet.side_emboss_thickness - 0.2
  expr: Constraints[71] = Spreadsheet.side_emboss_thickness - 0.2
  sketch-geometry (64):
    g0: ArcOfCircle CenterX=0.95 CenterY=1.1 CenterZ=0 NormalX=0 NormalY=0 NormalZ=1 AngleXU=0 Radius=0.3 StartAngle=5.405e-13 EndAngle=1.5708
    g1: ArcOfCircle CenterX=0.95 CenterY=1.1 CenterZ=0 NormalX=0 NormalY=0 NormalZ=1 AngleXU=0 Radius=1.3 StartAngle=0 EndAngle=1.5708
    g2: LineSegment StartX=0.95 StartY=2.4 StartZ=0 EndX=0.95 EndY=1.4 EndZ=0
    g3: LineSegment StartX=3.25 StartY=-0.7 StartZ=0 EndX=3.25 EndY=2.4 EndZ=0
    g4: LineSegment StartX=3.25 StartY=2.4 StartZ=0 EndX=4.25 EndY=2.4 EndZ=0
    g5: LineSegment StartX=4.25 StartY=2.4 StartZ=0 EndX=4.25 EndY=-0.4 EndZ=0
    g6: LineSegment [constr] StartX=-17.25 StartY=2.4 StartZ=0 EndX=17.25 EndY=2.4 EndZ=0
    g7: LineSegment [constr] StartX=17.25 StartY=2.4 StartZ=0 EndX=17.25 EndY=-2.4 EndZ=0
    g8: LineSegment [constr] StartX=17.25 StartY=-2.4 StartZ=0 EndX=-17.25 EndY=-2.4 EndZ=0
    g9: LineSegment [constr] StartX=-17.25 StartY=-2.4 StartZ=0 EndX=-17.25 EndY=2.4 EndZ=0
    g10: ArcOfCircle CenterX=2.35 CenterY=-1.5 CenterZ=0 NormalX=0 NormalY=0 NormalZ=1 AngleXU=0 Radius=0.1 StartAngle=3.14159 EndAngle=4.71239
    g11: ArcOfCircle CenterX=2.25 CenterY=-1.4 CenterZ=0 NormalX=0 NormalY=0 NormalZ=1 AngleXU=0 Radius=1 StartAngle=3.14159 EndAngle=4.71239
    g12: LineSegment StartX=2.25 StartY=1.1 StartZ=0 EndX=2.25 EndY=-1.5 EndZ=0
    g13: LineSegment StartX=1.25 StartY=-1.4 StartZ=0 EndX=1.25 EndY=1.1 EndZ=0
    g14: ArcOfCircle CenterX=2.25 CenterY=-0.4 CenterZ=0 NormalX=0 NormalY=0 NormalZ=1 AngleXU=0 Radius=2 StartAngle=4.71239 EndAngle=6.28319
    g15: ArcOfCircle CenterX=2.35 CenterY=-0.7 CenterZ=0 NormalX=0 NormalY=0 NormalZ=1 AngleXU=0 Radius=0.9 StartAngle=4.71239 EndAngle=6.28319
    g16: LineSegment StartX=8.45 StartY=1 StartZ=0 EndX=8.45 EndY=-1 EndZ=0
    g17: LineSegment StartX=7.45 StartY=1 StartZ=0 EndX=7.45 EndY=-1 EndZ=0
    g18: LineSegment StartX=6.05 StartY=1 StartZ=0 EndX=6.05 EndY=-1 EndZ=0
    g19: LineSegment StartX=5.05 StartY=1 StartZ=0 EndX=5.05 EndY=-1 EndZ=0
    g20: ArcOfCircle CenterX=7.05 CenterY=1 CenterZ=0 NormalX=0 NormalY=0 NormalZ=1 AngleXU=0 Radius=1.4 StartAngle=1e-16 EndAngle=1.5708
    g21: ArcOfCircle CenterX=6.85 CenterY=1 CenterZ=0 NormalX=0 NormalY=0 NormalZ=1 AngleXU=0 Radius=0.6 StartAngle=1e-16 EndAngle=1.5708
    g22: ArcOfCircle CenterX=6.65 CenterY=1 CenterZ=0 NormalX=0 NormalY=0 NormalZ=1 AngleXU=0 Radius=0.6 StartAngle=1.5708 EndAngle=3.14159
    g23: ArcOfCircle CenterX=6.45 CenterY=1 CenterZ=0 NormalX=0 NormalY=0 NormalZ=1 AngleXU=0 Radius=1.4 StartAngle=1.5708 EndAngle=3.14159
    g24: ArcOfCircle CenterX=6.85 CenterY=-1 CenterZ=0 NormalX=0 NormalY=0 NormalZ=1 AngleXU=0 Radius=0.6 StartAngle=4.71239 EndAngle=6.28319
    g25: ArcOfCircle CenterX=7.05 CenterY=-1 CenterZ=0 NormalX=0 NormalY=0 NormalZ=1 AngleXU=0 Radius=1.4 StartAngle=4.71239 EndAngle=6.28319
    g26: ArcOfCircle CenterX=6.65 CenterY=-1 CenterZ=0 NormalX=0 NormalY=0 NormalZ=1 AngleXU=0 Radius=0.6 StartAngle=3.14159 EndAngle=4.71239
    g27: ArcOfCircle CenterX=6.45 CenterY=-1 CenterZ=0 NormalX=0 NormalY=0 NormalZ=1 AngleXU=0 Radius=1.4 StartAngle=3.14159 EndAngle=4.71239
    g28: LineSegment StartX=7.05 StartY=-2.4 StartZ=0 EndX=6.45 EndY=-2.4 EndZ=0
    g29: LineSegment StartX=6.85 StartY=-1.6 StartZ=0 EndX=6.65 EndY=-1.6 EndZ=0
    g30: LineSegment StartX=6.85 StartY=1.6 StartZ=0 EndX=6.65 EndY=1.6 EndZ=0
    g31: LineSegment StartX=7.05 StartY=2.4 StartZ=0 EndX=6.45 EndY=2.4 EndZ=0
    g32: LineSegment StartX=12.65 StartY=1 StartZ=0 EndX=12.65 EndY=-1 EndZ=0
    g33: LineSegment StartX=11.65 StartY=1 StartZ=0 EndX=11.65 EndY=-1 EndZ=0
    g34: LineSegment StartX=10.25 StartY=1 StartZ=0 EndX=10.25 EndY=-1 EndZ=0
    g35: LineSegment StartX=9.25 StartY=1 StartZ=0 EndX=9.25 EndY=-1 EndZ=0
    g36: ArcOfCircle CenterX=11.25 CenterY=1 CenterZ=0 NormalX=0 NormalY=0 NormalZ=1 AngleXU=0 Radius=1.4 StartAngle=1e-16 EndAngle=1.5708
    g37: ArcOfCircle CenterX=11.05 CenterY=1 CenterZ=0 NormalX=0 NormalY=0 NormalZ=1 AngleXU=0 Radius=0.6 StartAngle=1e-16 EndAngle=1.5708
    g38: ArcOfCircle CenterX=10.85 CenterY=1 CenterZ=0 NormalX=0 NormalY=0 NormalZ=1 AngleXU=0 Radius=0.6 StartAngle=1.5708 EndAngle=3.14159
    g39: ArcOfCircle CenterX=10.65 CenterY=1 CenterZ=0 NormalX=0 NormalY=0 NormalZ=1 AngleXU=0 Radius=1.4 StartAngle=1.5708 EndAngle=3.14159
    g40: ArcOfCircle CenterX=11.05 CenterY=-1 CenterZ=0 NormalX=0 NormalY=0 NormalZ=1 AngleXU=0 Radius=0.6 StartAngle=4.71239 EndAngle=6.28319
    g41: ArcOfCircle CenterX=11.25 CenterY=-1 CenterZ=0 NormalX=0 NormalY=0 NormalZ=1 AngleXU=0 Radius=1.4 StartAngle=4.71239 EndAngle=6.28319
    g42: ArcOfCircle CenterX=10.85 CenterY=-1 CenterZ=0 NormalX=0 NormalY=0 NormalZ=1 AngleXU=0 Radius=0.6 StartAngle=3.14159 EndAngle=4.71239
    g43: ArcOfCircle CenterX=10.65 CenterY=-1 CenterZ=0 NormalX=0 NormalY=0 NormalZ=1 AngleXU=0 Radius=1.4 StartAngle=3.14159 EndAngle=4.71239
    g44: LineSegment StartX=11.25 StartY=-2.4 StartZ=0 EndX=10.65 EndY=-2.4 EndZ=0
    g45: LineSegment StartX=11.05 StartY=-1.6 StartZ=0 EndX=10.85 EndY=-1.6 EndZ=0
    g46: LineSegment StartX=11.05 StartY=1.6 StartZ=0 EndX=10.85 EndY=1.6 EndZ=0
    g47: LineSegment StartX=11.25 StartY=2.4 StartZ=0 EndX=10.65 EndY=2.4 EndZ=0
    g48: LineSegment StartX=16.85 StartY=1 StartZ=0 EndX=16.85 EndY=-1 EndZ=0
    g49: LineSegment StartX=15.85 StartY=1 StartZ=0 EndX=15.85 EndY=-1 EndZ=0
    g50: LineSegment StartX=14.45 StartY=1 StartZ=0 EndX=14.45 EndY=-1 EndZ=0
    g51: LineSegment StartX=13.45 StartY=1 StartZ=0 EndX=13.45 EndY=-1 EndZ=0
    g52: ArcOfCircle CenterX=15.45 CenterY=1 CenterZ=0 NormalX=0 NormalY=0 NormalZ=1 AngleXU=0 Radius=1.4 StartAngle=2e-16 EndAngle=1.5708
    g53: ArcOfCircle CenterX=15.25 CenterY=1 CenterZ=0 NormalX=0 NormalY=0 NormalZ=1 AngleXU=0 Radius=0.6 StartAngle=1e-16 EndAngle=1.5708
    g54: ArcOfCircle CenterX=15.05 CenterY=1 CenterZ=0 NormalX=0 NormalY=0 NormalZ=1 AngleXU=0 Radius=0.6 StartAngle=1.5708 EndAngle=3.14159
    g55: ArcOfCircle CenterX=14.85 CenterY=1 CenterZ=0 NormalX=0 NormalY=0 NormalZ=1 AngleXU=0 Radius=1.4 StartAngle=1.5708 EndAngle=3.14159
    g56: ArcOfCircle CenterX=15.25 CenterY=-1 CenterZ=0 NormalX=0 NormalY=0 NormalZ=1 AngleXU=0 Radius=0.6 StartAngle=4.71239 EndAngle=6.28319
    g57: ArcOfCircle CenterX=15.45 CenterY=-1 CenterZ=0 NormalX=0 NormalY=0 NormalZ=1 AngleXU=0 Radius=1.4 StartAngle=4.71239 EndAngle=6.28319
    g58: ArcOfCircle CenterX=15.05 CenterY=-1 CenterZ=0 NormalX=0 NormalY=0 NormalZ=1 AngleXU=0 Radius=0.6 StartAngle=3.14159 EndAngle=4.71239
    g59: ArcOfCircle CenterX=14.85 CenterY=-1 CenterZ=0 NormalX=0 NormalY=0 NormalZ=1 AngleXU=0 Radius=1.4 StartAngle=3.14159 EndAngle=4.71239
    g60: LineSegment StartX=15.45 StartY=-2.4 StartZ=0 EndX=14.85 EndY=-2.4 EndZ=0
    g61: LineSegment StartX=15.25 StartY=-1.6 StartZ=0 EndX=15.05 EndY=-1.6 EndZ=0
    g62: LineSegment StartX=15.25 StartY=1.6 StartZ=0 EndX=15.05 EndY=1.6 EndZ=0
    g63: LineSegment StartX=15.45 StartY=2.4 StartZ=0 EndX=14.85 EndY=2.4 EndZ=0
  constraints (164):
    c: Coincident(g2,g1)
    c: Coincident(g2,g0)
    c: Coincident(g3,g4)
    c: Coincident(g4,g5)
    c: Vertical(g3)
    c: Vertical(g5)
    c: Vertical(g2)
    c: Horizontal(g4)
    c: Coincident(g6,g7)
    c: Coincident(g7,g8)
    c: Coincident(g8,g9)
    c: Coincident(g9,g6)
    c: Horizontal(g6)
    c: Horizontal(g8)
    c: Vertical(g7)
    c: Vertical(g9)
    c: Symmetric(g6,g8,g-1)
    c: DistanceX(g8,g8) = 34.5
    c: DistanceY(g9,g9) = 4.8
    c: Vertical(g13)
    c: Vertical(g12)
    c: Tangent(g12,g1) = 1.5708
    c: Tangent(g12,g10) = -1.5708
    c: Tangent(g13,g11) = 1.5708
    c: Tangent(g13,g0) = -1.5708
    c: Radius(g11) = 1
    c: DistanceX(g0,g1) = 1
    c: DistanceY(g2,g2) = 1
    c: Equal(g2,g4)
    c: Tangent(g1,g6) = 1.5708
    c: Radius(g1) = 1.3
    c: PointOnObject(g3,g6)
    c: Tangent(g11,g8)
    c: Tangent(g14,g5) = 1.5708
    c: Radius(g10) = 0.1
    c: DistanceX(g1,g3) = 1
    c: Vertical(g0,g0)
    c: Tangent(g15,g3) = -1.5708
    c: DistanceY(g14,g10) = 0.8
    c: Tangent(g15,g10) = -1.5708
    c: Tangent(g11,g14) = -1.5708
    c: Vertical(g10,g10)
    c: Vertical(g11,g11)
    c: Vertical(g16)
    c: Vertical(g18)
    c: Vertical(g17)
    c: Vertical(g19)
    c: Tangent(g25,g16) = 1.5708
    c: Tangent(g28,g25) = 1.5708
    c: Tangent(g28,g27) = 1.5708
    c: Tangent(g27,g19) = -1.5708
    c: Tangent(g23,g19) = -1.5708
    c: Tangent(g31,g23) = -1.5708
    c: Tangent(g31,g20) = -1.5708
    c: Tangent(g20,g16) = 1.5708
    c: Tangent(g21,g17) = 1.5708
    c: Tangent(g30,g21) = -1.5708
    c: Tangent(g30,g22) = -1.5708
    c: Tangent(g22,g18) = -1.5708
    c: Tangent(g26,g18) = -1.5708
    c: Tangent(g29,g26) = 1.5708
    c: Tangent(g29,g24) = 1.5708
    c: Tangent(g24,g17) = 1.5708
    c: PointOnObject(g25,g8)
    c: PointOnObject(g20,g6)
    c: PointOnObject(g23,g6)
    c: PointOnObject(g27,g8)
    c: Horizontal(g30)
    c: DistanceX(g19,g18) = 1
    c: DistanceX(g17,g16) = 1
    c: DistanceY(g22,g23) = 0.8
    c: DistanceY(g27,g26) = 0.8
    c: Horizontal(g29)
    c: Radius(g27) = 1.4
    c: DistanceX(g5,g19) = 0.8
    c: Radius(g26) = 0.6
    c: DistanceX(g18,g17) = 1.4
    c: Vertical(g27,g23)
    c: Horizontal(g25,g27)
    c: Vertical(g25,g20)
    c: Horizontal(g24,g26)
    c: Vertical(g26,g22)
    c: Vertical(g21,g24)
    c: Vertical(g32)
    c: Vertical(g34)
    c: Vertical(g33)
    c: Vertical(g35)
    c: Tangent(g41,g32) = 1.5708
    c: Tangent(g44,g41) = 1.5708
    c: Tangent(g44,g43) = 1.5708
    c: Tangent(g43,g35) = -1.5708
    c: Tangent(g39,g35) = -1.5708
    c: Tangent(g47,g39) = -1.5708
    c: Tangent(g47,g36) = -1.5708
    c: Tangent(g36,g32) = 1.5708
    c: Tangent(g37,g33) = 1.5708
    c: Tangent(g46,g37) = -1.5708
    c: Tangent(g46,g38) = -1.5708
    c: Tangent(g38,g34) = -1.5708
    c: Tangent(g42,g34) = -1.5708
    c: Tangent(g45,g42) = 1.5708
    c: Tangent(g45,g40) = 1.5708
    c: Tangent(g40,g33) = 1.5708
    c: Horizontal(g46)
    c: DistanceX(g35,g34) = 1
    c: DistanceX(g33,g32) = 1
    c: DistanceY(g38,g39) = 0.8
    c: DistanceY(g43,g42) = 0.8
    c: Horizontal(g45)
    c: Equal(g27,g43) = 1.4
    c: Equal(g26,g42) = 0.6
    c: DistanceX(g34,g33) = 1.4
    c: Vertical(g43,g39)
    c: Horizontal(g41,g43)
    c: Vertical(g41,g36)
    c: Horizontal(g40,g42)
    c: Vertical(g42,g38)
    c: Vertical(g37,g40)
    c: PointOnObject(g39,g6)
    c: PointOnObject(g43,g8)
    c: PointOnObject(g36,g6)
    c: PointOnObject(g41,g8)
    c: DistanceX(g16,g35) = 0.8
    c: Vertical(g48)
    c: Vertical(g50)
    c: Vertical(g49)
    c: Vertical(g51)
    c: Tangent(g57,g48) = 1.5708
    c: Tangent(g60,g57) = 1.5708
    c: Tangent(g60,g59) = 1.5708
    c: Tangent(g59,g51) = -1.5708
    c: Tangent(g55,g51) = -1.5708
    c: Tangent(g63,g55) = -1.5708
    c: Tangent(g63,g52) = -1.5708
    c: Tangent(g52,g48) = 1.5708
    c: Tangent(g53,g49) = 1.5708
    c: Tangent(g62,g53) = -1.5708
    c: Tangent(g62,g54) = -1.5708
    c: Tangent(g54,g50) = -1.5708
    c: Tangent(g58,g50) = -1.5708
    c: Tangent(g61,g58) = 1.5708
    c: Tangent(g61,g56) = 1.5708
    c: Tangent(g56,g49) = 1.5708
    c: Horizontal(g62)
    c: DistanceX(g51,g50) = 1
    c: DistanceX(g49,g48) = 1
    c: DistanceY(g54,g55) = 0.8
    c: DistanceY(g59,g58) = 0.8
    c: Horizontal(g61)
    c: Equal(g27,g59) = 1.4
    c: Equal(g26,g58) = 0.6
    c: DistanceX(g50,g49) = 1.4
    c: Vertical(g59,g55)
    c: Horizontal(g57,g59)
    c: Vertical(g57,g52)
    c: Horizontal(g56,g58)
    c: Vertical(g58,g54)
    c: Vertical(g53,g56)
    c: PointOnObject(g55,g6)
    c: PointOnObject(g59,g8)
    c: PointOnObject(g57,g8)
    c: PointOnObject(g52,g6)
    c: DistanceX(g32,g51) = 0.8
    c: DistanceX(g-5,g1) = 2.7
FEATURE [Sketcher::SketchObject] Sketch076
  ArcFitTolerance = 1e-06
  AttachmentSupport = -> [Import020]
  FullyConstrained = true
  MapMode = 5
  Placement = pos=(-35,0,0) rot=(0.57735,-0.57735,-0.57735;2.0944rad)
  Support = -> [Import020]
  TreeRank = 1140
  sketch-geometry (4):
    g0: LineSegment StartX=-18.25 StartY=3.4 StartZ=0 EndX=18.25 EndY=3.4 EndZ=0
    g1: LineSegment StartX=18.25 StartY=3.4 StartZ=0 EndX=18.25 EndY=-3.4 EndZ=0
    g2: LineSegment StartX=18.25 StartY=-3.4 StartZ=0 EndX=-18.25 EndY=-3.4 EndZ=0
    g3: LineSegment StartX=-18.25 StartY=-3.4 StartZ=0 EndX=-18.25 EndY=3.4 EndZ=0
  constraints (11):
    c: Coincident(g0,g1)
    c: Coincident(g1,g2)
    c: Coincident(g2,g3)
    c: Coincident(g3,g0)
    c: Horizontal(g0)
    c: Horizontal(g2)
    c: Vertical(g1)
    c: Vertical(g3)
    c: Symmetric(g0,g2,g-1)
    c: DistanceX(g2,g2) = 36.5
    c: DistanceY(g3,g3) = 6.8
FEATURE [PartDesign::Pad] Pad017
  AddSubType = 0
  AlongSketchNormal = false
  CheckUpToFaceLimits = true
  ClaimChildren = false
  Direction = (-1,0,0)
  Fit = 0
  FitJoin = 0
  InnerFit = 0
  InnerFitJoin = 0
  InnerTaperAngle = 0
  InnerTaperAngleRev = 0
  Length = 3
  Length2 = 100
  Linearize = true
  NewSolid = false
  Profile = -> Sketch074
  Reversed = true
  Suppress = false
  TreeRank = 1171
  Type = 0
  _ProfileBasedVersion = 1
FEATURE [PartDesign::Pad] Pad018
  AddSubType = 0
  AlongSketchNormal = false
  BaseFeature = -> Pad017
  CheckUpToFaceLimits = true
  ClaimChildren = false
  Direction = (-1,0,0)
  Fit = 0
  FitJoin = 0
  InnerFit = 0
  InnerFitJoin = 0
  InnerTaperAngle = 0
  InnerTaperAngleRev = 0
  Length = 3
  Length2 = 100
  Linearize = true
  NewSolid = false
  Profile = -> Sketch075
  Reversed = true
  Suppress = false
  TreeRank = 1172
  Type = 0
  _ProfileBasedVersion = 1
FEATURE [PartDesign::FeatureBase] Clone019
  BaseFeature = -> Fillet006
  NewSolid = false
  Suppress = false
  TreeRank = 1199
FEATURE [PartDesign::Body] Body053  label="top inside master"
  AutoGroupSolids = false
  BaseFeature = -> Fillet006
  ClaimAllChildren = false
  ExportMode = 0
  Group = -> [Clone019]
  Origin = -> Origin056
  Tip = -> Clone019
  TreeRank = 1201
  _ExportChildren = -> [Clone019]
  _GroupVersion = 1
FEATURE [Part::SubShapeBinder] Import021  label="Import021(Fillet)"
  BindCopyOnChange = 0
  BindMode = 0
  ClaimChildren = false
  Context = -> Part [Part011.Body054.Import021.]
  FillStyle = 0
  Fuse = false
  MakeFace = false
  OffsetFill = false
  OffsetIntersection = false
  OffsetJoinType = 0
  OffsetOpenResult = false
  PartialLoad = false
  Relative = true
  Support = -> [Body[Fillet.]]
  TreeRank = 1216
  _Version = 8
FEATURE [Sketcher::SketchObject] Sketch077
  ArcFitTolerance = 1e-06
  AttachmentSupport = -> [Import021]
  ExternalGeometry = -> [Import021]
  FullyConstrained = true
  MapMode = 5
  Placement = pos=(0,0,14) rot=(0,0,1;0rad)
  Support = -> [Import021]
  TreeRank = 1217
  sketch-geometry (4):
    g0: ArcOfCircle CenterX=-19 CenterY=42.2 CenterZ=0 NormalX=0 NormalY=0 NormalZ=1 AngleXU=0 Radius=2.3 StartAngle=1.5708 EndAngle=4.71239
    g1: ArcOfCircle CenterX=-4 CenterY=42.2 CenterZ=0 NormalX=0 NormalY=0 NormalZ=1 AngleXU=0 Radius=2.3 StartAngle=4.71239 EndAngle=7.85398
    g2: LineSegment StartX=-19 StartY=39.9 StartZ=0 EndX=-4 EndY=39.9 EndZ=0
    g3: LineSegment StartX=-4 StartY=44.5 StartZ=0 EndX=-19 EndY=44.5 EndZ=0
  constraints (10):
    c: Tangent(g0,g2) = -1.5708
    c: Tangent(g2,g1) = -1.5708
    c: Tangent(g1,g3) = -1.5708
    c: Tangent(g3,g0) = -1.5708
    c: Equal(g0,g1)
    c: Horizontal(g1,g0)
    c: Radius(g0) = 2.3
    c: DistanceY(g0,g-3) = 9
    c: DistanceX(g0,g-3) = 4
    c: DistanceX(g3,g3) = 15
FEATURE [Part::Part2DObjectPython] ShapeString  # Draft 2D object (typed FeaturePython)
  FontFile = <userpath>/cq-80/Pretendo.ttf
  MakeFace = true
  Placement = pos=(-20,41,13) rot=(0,0,1;0rad)
  Size = 2.4
  String = niatendo
  Tracking = 0
  TreeRank = 1218
FEATURE [Part::Extrusion] Extrude  label="trademark text"
  Base = -> ShapeString
  Dir = (0,0,1)
  DirMode = 2
  FaceMakerClass = Part::FaceMakerBullseye
  InnerTaperAngle = 0
  InnerTaperAngleRev = 0
  LengthFwd = 0.6
  LengthRev = 0
  Linearize = true
  Solid = true
  Symmetric = false
  TreeRank = 3536
FEATURE [PartDesign::Pad] Pad019
  AddSubType = 0
  AlongSketchNormal = false
  CheckUpToFaceLimits = true
  ClaimChildren = false
  Direction = (0,0,1)
  Fit = 0
  FitJoin = 0
  InnerFit = 0
  InnerFitJoin = 0
  InnerTaperAngle = 0
  InnerTaperAngleRev = 0
  Length = 2
  Length2 = 100
  Linearize = true
  NewSolid = false
  Profile = -> Sketch077
  Reversed = true
  Suppress = false
  TreeRank = 1220
  Type = 0
  _ProfileBasedVersion = 1
FEATURE [PartDesign::ShapeBinder] ShapeBinder021
  Placement = pos=(0,0,14) rot=(0,0,1;0rad)
  Support = -> [Sketch077]
  TraceSupport = false
  TreeRank = 1233
FEATURE [Part::SubShapeBinder] Import022  label="Import022(Sketch077)"
  BindCopyOnChange = 0
  BindMode = 0
  ClaimChildren = false
  Context = -> Part [Part010.Body055.Import022.]
  FillStyle = 0
  Fuse = false
  MakeFace = false
  OffsetFill = false
  OffsetIntersection = false
  OffsetJoinType = 0
  OffsetOpenResult = false
  PartialLoad = false
  Relative = true
  Support = -> [Body054[Sketch077.]]
  TreeRank = 1235
  _Version = 8
FEATURE [PartDesign::Plane] DatumPlane025
  AttachmentSupport = -> [ShapeBinder021]
  Length = 23.6
  MapMode = 2
  MinimumLength = 10
  MinimumWidth = 10
  Placement = pos=(0,0,14) rot=(0,0,1;0rad)
  ResizeMode = 0
  Support = -> [ShapeBinder021]
  TreeRank = 1237
  Width = 46.5
FEATURE [Sketcher::SketchObject] Sketch078
  ArcFitTolerance = 1e-06
  AttachmentSupport = -> [DatumPlane025]
  ExternalGeometry = -> [Import022]
  FullyConstrained = true
  MapMode = 5
  Placement = pos=(0,0,14) rot=(0,0,1;0rad)
  Support = -> [DatumPlane025]
  TreeRank = 1236
  sketch-geometry (4):
    g0: ArcOfCircle CenterX=-19 CenterY=42.2 CenterZ=0 NormalX=0 NormalY=0 NormalZ=1 AngleXU=0 Radius=4.3 StartAngle=1.5708 EndAngle=4.71239
    g1: ArcOfCircle CenterX=-4 CenterY=42.2 CenterZ=0 NormalX=0 NormalY=0 NormalZ=1 AngleXU=0 Radius=4.3 StartAngle=4.71239 EndAngle=7.85398
    g2: LineSegment StartX=-19 StartY=46.5 StartZ=0 EndX=-4 EndY=46.5 EndZ=0
    g3: LineSegment StartX=-19 StartY=37.9 StartZ=0 EndX=-3.99998 EndY=37.9 EndZ=0
  constraints (9):
    c: Coincident(g0,g-3)
    c: Coincident(g1,g-4)
    c: DistanceY(g-3,g0) = 2
    c: Horizontal(g2)
    c: Coincident(g3,g1)
    c: Horizontal(g3)
    c: Tangent(g2,g1) = 1.5708
    c: Tangent(g2,g0) = 1.5708
    c: Tangent(g3,g0) = -1.5708
FEATURE [PartDesign::Pad] Pad020
  AddSubType = 0
  AlongSketchNormal = false
  CheckUpToFaceLimits = true
  ClaimChildren = false
  Direction = (0,0,1)
  Fit = 0
  FitJoin = 0
  InnerFit = 0
  InnerFitJoin = 0
  InnerTaperAngle = 0
  InnerTaperAngleRev = 0
  Length = 2
  Length2 = 100
  Linearize = true
  NewSolid = false
  Placement = pos=(0,0,14) rot=(0,0,1;0rad)
  Profile = -> Sketch078
  Reversed = true
  Suppress = false
  TreeRank = 1238
  Type = 0
  _ProfileBasedVersion = 1
FEATURE [PartDesign::Fillet] Fillet007
  AddSubType = 0
  Base = -> Pad020 [Face6]
  BaseFeature = -> Pad020
  NewSolid = false
  Placement = pos=(0,0,14) rot=(0,0,1;0rad)
  Radius = 1.99
  SupportTransform = false
  Suppress = false
  TreeRank = 1239
FEATURE [PartDesign::Body] Body055  label="trademark support"
  AutoGroupSolids = false
  ClaimAllChildren = false
  ExportMode = 0
  Group = -> [ShapeBinder021,Sketch078,Import022,DatumPlane025,Pad020,Fillet007]
  Origin = -> Origin058
  Placement = pos=(0,0,-1) rot=(0,0,1;0rad)
  Tip = -> Fillet007
  TreeRank = 3278
  _ExportChildren = -> [ShapeBinder021,Import022,DatumPlane025,Pad020,Fillet007]
  _GroupVersion = 1
FEATURE [PartDesign::ShapeBinder] ShapeBinder022
  Support = -> [Fillet,ShapeBinder019]
  TraceSupport = false
  TreeRank = 1252
FEATURE [Part::SubShapeBinder] Import023  label="Import023(Sketch077)"
  BindCopyOnChange = 0
  BindMode = 0
  ClaimChildren = false
  Context = -> Part [Part012.Body056.Import023.]
  FillStyle = 0
  Fuse = false
  MakeFace = false
  OffsetFill = false
  OffsetIntersection = false
  OffsetJoinType = 0
  OffsetOpenResult = false
  PartialLoad = false
  Relative = true
  Support = -> [Body054[Sketch077.]]
  TreeRank = 1254
  _Version = 8
FEATURE [Sketcher::SketchObject] Sketch079
  ArcFitTolerance = 1e-06
  AttachmentSupport = -> [Fillet]
  ExternalGeometry = -> [Import023,ShapeBinder022]
  FullyConstrained = true
  MapMode = 5
  Placement = pos=(0,0,14) rot=(0,0,1;0rad)
  Support = -> [Fillet]
  TreeRank = 1253
  sketch-geometry (6):
    g0: LineSegment [constr] StartX=-17.4 StartY=44.5 StartZ=0 EndX=-17.4 EndY=54.5 EndZ=0
    g1: LineSegment StartX=-17.4 StartY=46.2765 StartZ=0 EndX=-17.4 EndY=61.2765 EndZ=0
    g2: LineSegment StartX=-13.4 StartY=44.5 StartZ=0 EndX=-13.4 EndY=59.5 EndZ=0
    g3: LineSegment StartX=-17.4 StartY=61.2765 StartZ=0 EndX=-7.4 EndY=61.2765 EndZ=0
    g4: LineSegment StartX=-13.4 StartY=59.5 StartZ=0 EndX=-3.4 EndY=59.5 EndZ=0
    g5: LineSegment StartX=-17.4 StartY=53.3555 StartZ=0 EndX=-27.4 EndY=53.3555 EndZ=0
  constraints (22):
    c: PointOnObject(g0,g-3)
    c: Vertical(g0)
    c: DistanceY(g0,g0) = 10
    c: PointOnObject(g1,g0)
    c: PointOnObject(g1,g-4)
    c: DistanceX(g-3,g0) = 1.6
    c: Vertical(g1)
    c: PointOnObject(g2,g-3)
    c: Vertical(g2)
    c: DistanceY(g2,g2) = 15
    c: DistanceY(g1,g1) = 15
    c: DistanceX(g1,g2) = 4
    c: Coincident(g3,g1)
    c: Horizontal(g3)
    c: Coincident(g4,g2)
    c: Horizontal(g4)
    c: DistanceX(g3,g3) = 10
    c: DistanceX(g4,g4) = 10
    c: Horizontal(g5)
    c: PointOnObject(g5,g-5)
    c: PointOnObject(g5,g1)
    c: DistanceX(g5,g5) = 10
FEATURE [PartDesign::Plane] DatumPlane026
  AttachmentSupport = -> [Sketch079]
  Length = 61.2765
  MapMode = 7
  MinimumLength = 10
  MinimumWidth = 10
  Placement = pos=(-17.4,61.2765,14) rot=(0.57735,-0.57735,-0.57735;2.0944rad)
  ResizeMode = 0
  Support = -> [Sketch079]
  TreeRank = 1255
  Width = 14
FEATURE [Part::SubShapeBinder] Import024  label="Import024(ShapeBinder019)"
  BindCopyOnChange = 0
  BindMode = 0
  ClaimChildren = false
  Context = -> Part [Part012.Body056.Import024.]
  FillStyle = 0
  Fuse = false
  MakeFace = false
  OffsetFill = false
  OffsetIntersection = false
  OffsetJoinType = 0
  OffsetOpenResult = false
  PartialLoad = false
  Relative = true
  Support = -> [Body005[ShapeBinder019.]]
  TreeRank = 1257
  _Version = 8
FEATURE [Sketcher::SketchObject] Sketch080
  ArcFitTolerance = 1e-06
  AttachmentSupport = -> [DatumPlane026]
  ExternalGeometry = -> [Sketch079,Import024,ShapeBinder022]
  FullyConstrained = true
  MapMode = 5
  Placement = pos=(-17.4,61.2765,14) rot=(0.57735,-0.57735,-0.57735;2.0944rad)
  Support = -> [DatumPlane026]
  TreeRank = 1256
  sketch-geometry (3):
    g0: ArcOfCircle CenterX=14.9215 CenterY=-7 CenterZ=0 NormalX=0 NormalY=0 NormalZ=1 AngleXU=0 Radius=7.00044 StartAngle=1.55958 EndAngle=3.14159
    g1: LineSegment StartX=7.92106 StartY=-7 StartZ=0 EndX=7.92106 EndY=-14 EndZ=0
    g2: LineSegment StartX=15 StartY=0 StartZ=0 EndX=18 EndY=0 EndZ=0
  constraints (9):
    c: Coincident(g0,g-3)
    c: Vertical(g-4,g0)
    c: Vertical(g1)
    c: Horizontal(g1,g-5)
    c: Tangent(g1,g0) = -1.5708
    c: Horizontal(g-6,g0)
    c: Coincident(g2,g0)
    c: PointOnObject(g2,g-1)
    c: DistanceX(g2,g2) = 3
FEATURE [PartDesign::Plane] DatumPlane027
  AttachmentSupport = -> [Sketch079]
  Length = 26
  MapMode = 7
  MinimumLength = 10
  MinimumWidth = 10
  Placement = pos=(-13.4,59.5,14) rot=(0.57735,-0.57735,-0.57735;2.0944rad)
  ResizeMode = 0
  Support = -> [Sketch079]
  TreeRank = 1258
  Width = 15.1
FEATURE [Sketcher::SketchObject] Sketch081
  ArcFitTolerance = 1e-06
  AttachmentSupport = -> [DatumPlane027]
  ExternalGeometry = -> [ShapeBinder022,Import024]
  FullyConstrained = true
  MapMode = 5
  Placement = pos=(-13.4,59.5,14) rot=(0.57735,-0.57735,-0.57735;2.0944rad)
  Support = -> [DatumPlane027]
  TreeRank = 1259
  sketch-geometry (3):
    g0: ArcOfCircle CenterX=13 CenterY=-7 CenterZ=0 NormalX=0 NormalY=0 NormalZ=1 AngleXU=0 Radius=7 StartAngle=1.5708 EndAngle=3.14159
    g1: LineSegment StartX=6 StartY=-7 StartZ=0 EndX=6 EndY=-14 EndZ=0
    g2: LineSegment StartX=13 StartY=0 StartZ=0 EndX=16 EndY=0 EndZ=0
  constraints (7):
    c: Coincident(g1,g-4)
    c: Coincident(g1,g-5)
    c: Coincident(g-3,g0)
    c: Tangent(g0,g1) = -1.5708
    c: Coincident(g2,g0)
    c: Horizontal(g2)
    c: DistanceX(g2,g2) = 3
FEATURE [Sketcher::SketchObject] Sketch082
  ArcFitTolerance = 1e-06
  AttachmentSupport = -> [XY_Plane059]
  ExternalGeometry = -> [Sketch080,Sketch081]
  FullyConstrained = true
  MapMode = 5
  Support = -> [XY_Plane059]
  TreeRank = 1260
  expr: Constraints[4] = Spreadsheet.groove_lift
  expr: Constraints[5] = Spreadsheet.groove_lift
  sketch-geometry (2):
    g0: Circle CenterX=-17.4 CenterY=53.6555 CenterZ=0 NormalX=0 NormalY=0 NormalZ=1 AngleXU=0 Radius=0.9
    g1: Circle CenterX=-13.4 CenterY=53.8 CenterZ=0 NormalX=0 NormalY=0 NormalZ=1 AngleXU=0 Radius=0.9
  constraints (6):
    c: Vertical(g0,g-3)
    c: Vertical(g1,g-4)
    c: Radius(g0) = 0.9
    c: Radius(g1) = 0.9
    c: DistanceY(g-3,g0) = 0.3
    c: DistanceY(g-4,g1) = 0.3
FEATURE [PartDesign::SubShapeBinder] Binder020  label="Binder020(Sketch082)"
  BindCopyOnChange = 0
  BindMode = 0
  ClaimChildren = false
  Context = -> Part [Part012.Body056.Binder020.]
  FillStyle = 0
  Fuse = false
  MakeFace = true
  OffsetFill = false
  OffsetIntersection = false
  OffsetJoinType = 0
  OffsetOpenResult = false
  PartialLoad = false
  Relative = true
  Support = -> [Sketch082[Edge1]]
  TreeRank = 1262
  _Version = 8
FEATURE [PartDesign::AdditivePipe] Pipe009
  AddSubType = 0
  AuxilleryCurvelinear = true
  AuxillerySpineTangent = false
  Binormal = (0,0,0)
  ClaimChildren = false
  Fit = 0
  FitJoin = 0
  InnerFit = 0
  InnerFitJoin = 0
  Linearize = true
  Mode = 0
  NewSolid = false
  Profile = -> Binder020
  Spine = -> Sketch080 [Edge3,Edge2,Edge1]
  SpineTangent = false
  Suppress = false
  Transformation = 0
  Transition = 1
  TreeRank = 1263
  _ProfileBasedVersion = 2
FEATURE [PartDesign::SubShapeBinder] Binder021  label="Binder021(Sketch082)"
  BindCopyOnChange = 0
  BindMode = 0
  ClaimChildren = false
  Context = -> Part [Part012.Body056.Binder021.]
  FillStyle = 0
  Fuse = false
  MakeFace = true
  OffsetFill = false
  OffsetIntersection = false
  OffsetJoinType = 0
  OffsetOpenResult = false
  PartialLoad = false
  Relative = true
  Support = -> [Sketch082[Edge2]]
  TreeRank = 1265
  _Version = 8
FEATURE [PartDesign::AdditivePipe] Pipe010
  AddSubType = 0
  AuxilleryCurvelinear = true
  AuxillerySpineTangent = false
  BaseFeature = -> Pipe009
  Binormal = (0,0,0)
  ClaimChildren = false
  Fit = 0
  FitJoin = 0
  InnerFit = 0
  InnerFitJoin = 0
  Linearize = true
  Mode = 0
  NewSolid = false
  Profile = -> Binder021
  Spine = -> Sketch081 [Edge3,Edge2,Edge1]
  SpineTangent = false
  Suppress = false
  Transformation = 0
  Transition = 1
  TreeRank = 1266
  _ProfileBasedVersion = 2
FEATURE [PartDesign::Body] Body056  label="trademark groove"
  AutoGroupSolids = false
  ClaimAllChildren = false
  ExportMode = 0
  Group = -> [ShapeBinder022,Sketch079,Import023,DatumPlane026,Sketch080,Import024,DatumPlane027,Sketch081,Sketch082,Pipe009,Binder020,Pipe010,Binder021]
  Origin = -> Origin059
  Tip = -> Pipe010
  TreeRank = 3226
  _ExportChildren = -> [ShapeBinder022,Sketch079,Import023,DatumPlane026,Import024,DatumPlane027,Sketch082,Pipe009,Pipe010]
  _GroupVersion = 1
FEATURE [Part::SubShapeBinder] Import025  label="Import025(Cut005)"
  BindCopyOnChange = 0
  BindMode = 0
  ClaimChildren = false
  Context = -> Part [Part004.Body057.Import025.]
  FillStyle = 0
  Fuse = false
  MakeFace = false
  OffsetFill = false
  OffsetIntersection = false
  OffsetJoinType = 0
  OffsetOpenResult = false
  PartialLoad = false
  Relative = true
  Support = -> [Cut005]
  TreeRank = 1281
  _Version = 8
FEATURE [Sketcher::SketchObject] Sketch083
  ArcFitTolerance = 1e-06
  AttachmentSupport = -> [Import025]
  ExternalGeometry = -> [Import025]
  FullyConstrained = true
  MapMode = 5
  Placement = pos=(0,0,11) rot=(0,0,1;0rad)
  Support = -> [Import025]
  TreeRank = 1282
  sketch-geometry (18):
    g0: ArcOfCircle CenterX=0 CenterY=-62.9417 CenterZ=0 NormalX=0 NormalY=0 NormalZ=1 AngleXU=0 Radius=5.1 StartAngle=1.09956 EndAngle=2.04204
    g1: LineSegment StartX=-2.31535 StartY=-58.3976 StartZ=0 EndX=-14.0442 EndY=-64.3737 EndZ=0
    g2: LineSegment StartX=2.31535 StartY=-58.3976 StartZ=0 EndX=14.0442 EndY=-64.3737 EndZ=0
    g3: LineSegment StartX=-11.9558 StartY=-68.4723 StartZ=0 EndX=-0.226995 EndY=-62.4962 EndZ=0
    g4: LineSegment StartX=0.226995 StartY=-62.4962 StartZ=0 EndX=11.9558 EndY=-68.4723 EndZ=0
    g5: ArcOfCircle CenterX=-13 CenterY=-66.423 CenterZ=0 NormalX=0 NormalY=0 NormalZ=1 AngleXU=0 Radius=2.3 StartAngle=2.04204 EndAngle=5.18363
    g6: ArcOfCircle CenterX=13 CenterY=-66.423 CenterZ=0 NormalX=0 NormalY=0 NormalZ=1 AngleXU=0 Radius=2.3 StartAngle=4.24115 EndAngle=7.38274
    g7: ArcOfCircle CenterX=0 CenterY=-62.9417 CenterZ=0 NormalX=0 NormalY=0 NormalZ=1 AngleXU=0 Radius=0.5 StartAngle=1.09956 EndAngle=2.04204
    g8: LineSegment [constr] StartX=-11.9558 StartY=-68.4723 StartZ=0 EndX=0 EndY=-68.4723 EndZ=0
    g9: ArcOfCircle CenterX=0 CenterY=-71.9417 CenterZ=0 NormalX=0 NormalY=0 NormalZ=1 AngleXU=0 Radius=5.1 StartAngle=1.09956 EndAngle=2.04204
    g10: LineSegment StartX=-2.31535 StartY=-67.3976 StartZ=0 EndX=-14.0442 EndY=-73.3737 EndZ=0
    g11: LineSegment StartX=2.31535 StartY=-67.3976 StartZ=0 EndX=14.0442 EndY=-73.3737 EndZ=0
    g12: LineSegment StartX=-11.9558 StartY=-77.4723 StartZ=0 EndX=-0.226995 EndY=-71.4962 EndZ=0
    g13: LineSegment StartX=0.226995 StartY=-71.4962 StartZ=0 EndX=11.9558 EndY=-77.4723 EndZ=0
    g14: ArcOfCircle CenterX=-13 CenterY=-75.423 CenterZ=0 NormalX=0 NormalY=0 NormalZ=1 AngleXU=0 Radius=2.3 StartAngle=2.04204 EndAngle=5.18363
    g15: ArcOfCircle CenterX=13 CenterY=-75.423 CenterZ=0 NormalX=0 NormalY=0 NormalZ=1 AngleXU=0 Radius=2.3 StartAngle=4.24115 EndAngle=7.38274
    g16: ArcOfCircle CenterX=0 CenterY=-71.9417 CenterZ=0 NormalX=0 NormalY=0 NormalZ=1 AngleXU=0 Radius=0.5 StartAngle=1.09956 EndAngle=2.04204
    g17: LineSegment [constr] StartX=-11.9558 StartY=-77.4723 StartZ=0 EndX=0 EndY=-77.4723 EndZ=0
  constraints (44):
    c: PointOnObject(g0,g-2)
    c: Tangent(g5,g3) = -1.5708
    c: Tangent(g5,g1) = -1.5708
    c: Tangent(g1,g0) = -1.5708
    c: Tangent(g2,g0) = 1.5708
    c: Tangent(g6,g2) = 1.5708
    c: Tangent(g6,g4) = -1.5708
    c: Tangent(g7,g4) = 1.5708
    c: Tangent(g7,g3) = 1.5708
    c: Equal(g1,g2)
    c: Parallel(g3,g1)
    c: Parallel(g4,g2)
    c: Horizontal(g0,g0)
    c: Coincident(g7,g0)
    c: Distance(g3,g0) = 4.6
    c: DistanceX(g5,g0) = 13
    c: Radius(g7) = 0.5
    c: Coincident(g8,g3)
    c: PointOnObject(g8,g-2)
    c: Horizontal(g8)
    c: Angle(g8,g3) = 0.471239
    c: Tangent(g14,g12) = -1.5708
    c: Tangent(g14,g10) = -1.5708
    c: Tangent(g10,g9) = -1.5708
    c: Tangent(g11,g9) = 1.5708
    c: Tangent(g15,g11) = 1.5708
    c: Tangent(g15,g13) = -1.5708
    c: Tangent(g16,g13) = 1.5708
    c: Tangent(g16,g12) = 1.5708
    c: Equal(g10,g11)
    c: Parallel(g12,g10)
    c: Parallel(g13,g11)
    c: Horizontal(g9,g9)
    c: Coincident(g16,g9)
    c: Distance(g12,g9) = 4.6
    c: DistanceX(g14,g9) = 13
    c: Equal(g7,g16) = 0.5
    c: Coincident(g17,g12)
    c: Horizontal(g17)
    c: Angle(g17,g12) = 0.471239
    c: PointOnObject(g9,g-2)
    c: PointOnObject(g17,g-2)
    c: DistanceY(g14,g5) = 9
    c: DistanceY(g-3,g9) = 26
FEATURE [PartDesign::Pad] Pad021
  AddSubType = 0
  AlongSketchNormal = false
  CheckUpToFaceLimits = true
  ClaimChildren = false
  Direction = (0,0,1)
  Fit = 0
  FitJoin = 0
  InnerFit = 0
  InnerFitJoin = 0
  InnerTaperAngle = 0
  InnerTaperAngleRev = 0
  Length = 0.45
  Length2 = 100
  Linearize = true
  NewSolid = false
  Profile = -> Sketch083
  Suppress = false
  TreeRank = 1283
  Type = 0
  _ProfileBasedVersion = 1
FEATURE [PartDesign::Chamfer] Chamfer001
  AddSubType = 0
  Angle = 45
  Base = -> Pad021 [Face20,Face10]
  BaseFeature = -> Pad021
  ChamferType = 1
  FlipDirection = false
  NewSolid = false
  Size = 0.39
  Size2 = 0.5
  SupportTransform = false
  Suppress = false
  TreeRank = 1284
FEATURE [PartDesign::Body] Body057  label="arrows"
  AutoGroupSolids = false
  ClaimAllChildren = false
  ExportMode = 0
  Group = -> [Import025,Sketch083,Pad021,Chamfer001]
  Origin = -> Origin060
  Tip = -> Chamfer001
  TreeRank = 3148
  _ExportChildren = -> [Import025,Pad021,Chamfer001]
  _GroupVersion = 1
FEATURE [PartDesign::ShapeBinder] ShapeBinder023
  Support = -> [Sketch076]
  TraceSupport = false
  TreeRank = 1297
FEATURE [Part::SubShapeBinder] Import026  label="Import026(Sketch076)"
  BindCopyOnChange = 0
  BindMode = 0
  ClaimChildren = false
  Context = -> Part [Part011.Body058.Import026.]
  FillStyle = 0
  Fuse = false
  MakeFace = false
  OffsetFill = false
  OffsetIntersection = false
  OffsetJoinType = 0
  OffsetOpenResult = false
  PartialLoad = false
  Relative = true
  Support = -> [Body051[Sketch076.]]
  TreeRank = 1299
  _Version = 8
FEATURE [Sketcher::SketchObject] Sketch085
  ArcFitTolerance = 1e-06
  AttachmentSupport = -> [Revolution005]
  ExternalGeometry = -> [Revolution005]
  FullyConstrained = true
  MapMode = 5
  Placement = pos=(17,42.5,7) rot=(0,1,0;3.14159rad)
  Support = -> [Revolution005]
  TreeRank = 1328
  sketch-geometry (3):
    g0: ArcOfCircle CenterX=0 CenterY=0 CenterZ=0 NormalX=0 NormalY=0 NormalZ=1 AngleXU=0 Radius=6 StartAngle=5.75959 EndAngle=7.85398
    g1: LineSegment StartX=0 StartY=6 StartZ=0 EndX=0 EndY=0 EndZ=0
    g2: LineSegment StartX=0 StartY=0 StartZ=0 EndX=5.19615 EndY=-3 EndZ=0
  constraints (8):
    c: Coincident(g0,g-3)
    c: PointOnObject(g0,g-2)
    c: Coincident(g1,g0)
    c: Coincident(g1,g0)
    c: Coincident(g2,g0)
    c: Radius(g0) = 6
    c: Angle(g2,g1) = 2.0944
    c: Coincident(g2,g0)
FEATURE [PartDesign::Pocket] Pocket005
  AddSubType = 1
  BaseFeature = -> Revolution005
  CheckUpToFaceLimits = true
  ClaimChildren = false
  Fit = 0
  FitJoin = 0
  InnerFit = 0
  InnerFitJoin = 0
  InnerTaperAngle = 0
  InnerTaperAngleRev = 0
  Length = 3
  Length2 = 100
  Linearize = true
  NewSolid = false
  Placement = pos=(17,42.5,14) rot=(0,0.707107,0.707107;3.14159rad)
  Profile = -> Sketch085
  Suppress = false
  TreeRank = 1329
  Type = 0
  _ProfileBasedVersion = 1
  _Version = 1
FEATURE [PartDesign::Body] Body040  label="top light shell"
  AutoGroupSolids = false
  ClaimAllChildren = false
  ExportMode = 0
  Group = -> [ShapeBinder015,Sketch048,DatumPlane019,Sketch049,Sketch050,DatumLine006,Revolution005,DatumPlane021,DatumPlane022,Import010,Sketch085,Pocket005]
  Origin = -> Origin042
  Tip = -> Pocket005
  TreeRank = 3286
  _ExportChildren = -> [ShapeBinder015,Sketch048,DatumPlane019,Sketch050,DatumLine006,Revolution005,DatumPlane021,DatumPlane022,Import010,Pocket005]
  _GroupVersion = 1
FEATURE [Part::SubShapeBinder] Import027  label="Import027(Pad010)"
  BindCopyOnChange = 0
  BindMode = 0
  ClaimChildren = false
  Context = -> Part [Part010.Body060.Import027.]
  FillStyle = 0
  Fuse = false
  MakeFace = false
  OffsetFill = false
  OffsetIntersection = false
  OffsetJoinType = 0
  OffsetOpenResult = false
  PartialLoad = false
  Relative = true
  Support = -> [Body035[Pad010.]]
  TreeRank = 1344
  _Version = 8
FEATURE [Sketcher::SketchObject] Sketch086
  ArcFitTolerance = 1e-06
  AttachmentSupport = -> [Import027]
  ExternalGeometry = -> [Import027]
  FullyConstrained = true
  MapMode = 5
  Placement = pos=(0,49.25,0) rot=(1,0,0;1.5708rad)
  Support = -> [Import027]
  TreeRank = 1345
  sketch-geometry (1):
    g0: Circle CenterX=12 CenterY=6.9 CenterZ=0 NormalX=0 NormalY=0 NormalZ=1 AngleXU=0 Radius=3
  constraints (2):
    c: Radius(g0) = 3
    c: Coincident(g0,g-3)
FEATURE [PartDesign::Pad] Pad023
  AddSubType = 0
  AlongSketchNormal = false
  CheckUpToFaceLimits = true
  ClaimChildren = false
  Direction = (0,-1,2e-16)
  Fit = 0
  FitJoin = 0
  InnerFit = 0
  InnerFitJoin = 0
  InnerTaperAngle = 0
  InnerTaperAngleRev = 0
  Length = 2
  Length2 = 100
  Linearize = true
  NewSolid = false
  Profile = -> Sketch086
  Reversed = true
  Suppress = false
  TreeRank = 1346
  Type = 0
  _ProfileBasedVersion = 1
FEATURE [Sketcher::SketchObject] Sketch087
  ArcFitTolerance = 1e-06
  AttachmentSupport = -> [Pad023]
  FullyConstrained = true
  MapMode = 5
  Placement = pos=(0,49.25,0) rot=(1,0,0;1.5708rad)
  Support = -> [Pad023]
  TreeRank = 1361
FEATURE [PartDesign::Body] Body060  label="front light support"
  AutoGroupSolids = false
  ClaimAllChildren = false
  ExportMode = 0
  Group = -> [Import027,Sketch086,Pad023,Sketch087]
  Origin = -> Origin064
  Tip = -> Pad023
  TreeRank = 3292
  _ExportChildren = -> [Import027,Pad023,Sketch087]
  _GroupVersion = 1
FEATURE [PartDesign::ShapeBinder] ShapeBinder024
  TraceSupport = false
  TreeRank = 1420
FEATURE [Part::SubShapeBinder] Import029  label="Import029(Clone019)"
  BindCopyOnChange = 0
  BindMode = 0
  ClaimChildren = false
  Context = -> Body063 [Import029.]
  FillStyle = 0
  Fuse = false
  MakeFace = false
  OffsetFill = false
  OffsetIntersection = false
  OffsetJoinType = 0
  OffsetOpenResult = false
  PartialLoad = false
  Relative = true
  Support = -> [Body053[Clone019.]]
  TreeRank = 1480
  _Version = 8
FEATURE [Sketcher::SketchObject] Sketch089
  ArcFitTolerance = 1e-06
  AttachmentSupport = -> [Import029]
  ExternalGeometry = -> [Import029]
  FullyConstrained = true
  MapMode = 5
  Placement = pos=(0,0,0) rot=(1,0,0;3.14159rad)
  Support = -> [Import029]
  TreeRank = 1479
  sketch-geometry (4):
    g0: LineSegment StartX=33.9407 StartY=-35 StartZ=0 EndX=31.9407 EndY=-35 EndZ=0
    g1: LineSegment StartX=31.9407 StartY=-35 StartZ=0 EndX=31.9407 EndY=-40 EndZ=0
    g2: LineSegment StartX=31.9407 StartY=-40 StartZ=0 EndX=33.9407 EndY=-40 EndZ=0
    g3: LineSegment StartX=33.9407 StartY=-40 StartZ=0 EndX=33.9407 EndY=-35 EndZ=0
  constraints (12):
    c: Coincident(g0,g1)
    c: Coincident(g1,g2)
    c: Coincident(g2,g3)
    c: Coincident(g3,g0)
    c: Horizontal(g0)
    c: Horizontal(g2)
    c: Vertical(g1)
    c: Vertical(g3)
    c: DistanceY(g1,g1) = 5
    c: DistanceX(g0,g0) = 2
    c: PointOnObject(g0,g-3)
    c: DistanceY(g-3,g1) = 12.5
FEATURE [PartDesign::Plane] DatumPlane028
  AttachmentSupport = -> [Import029]
  Length = 68
  MapMode = 13
  MinimumLength = 10
  MinimumWidth = 10
  Placement = pos=(11.3333,33.5,10.6667) rot=(1,0,0;1.5708rad)
  ResizeMode = 0
  Support = -> [Import029]
  TreeRank = 1475
  Width = 13
FEATURE [Sketcher::SketchObject] Sketch090
  ArcFitTolerance = 1e-06
  AttachmentSupport = -> [DatumPlane028]
  ExternalGeometry = -> [Import029]
  FullyConstrained = true
  MapMode = 5
  Placement = pos=(11.3333,33.5,10.6667) rot=(1,0,0;1.5708rad)
  Support = -> [DatumPlane028]
  TreeRank = 1476
  sketch-geometry (5):
    g0: LineSegment StartX=15.6667 StartY=2.33333 StartZ=0 EndX=-38.3333 EndY=2.33333 EndZ=0
    g1: ArcOfCircle CenterX=15.6667 CenterY=-4.66667 CenterZ=0 NormalX=0 NormalY=0 NormalZ=1 AngleXU=0 Radius=7 StartAngle=0 EndAngle=1.5708
    g2: ArcOfCircle CenterX=-38.3333 CenterY=-4.66667 CenterZ=0 NormalX=0 NormalY=0 NormalZ=1 AngleXU=0 Radius=7 StartAngle=1.5708 EndAngle=3.14159
    g3: LineSegment StartX=-45.3333 StartY=-10.6667 StartZ=0 EndX=-45.3333 EndY=-4.66667 EndZ=0
    g4: LineSegment StartX=22.6667 StartY=-10.6667 StartZ=0 EndX=22.6667 EndY=-4.66667 EndZ=0
  constraints (12):
    c: Coincident(g0,g-3)
    c: Coincident(g0,g-4)
    c: Coincident(g1,g-3)
    c: Coincident(g1,g-6)
    c: Coincident(g1,g0)
    c: Coincident(g2,g-4)
    c: Coincident(g2,g0)
    c: Coincident(g2,g-5)
    c: Coincident(g3,g-5)
    c: Coincident(g3,g2)
    c: Coincident(g4,g-6)
    c: Coincident(g4,g1)
FEATURE [PartDesign::AdditivePipe] Pipe011
  AddSubType = 0
  AuxilleryCurvelinear = true
  AuxillerySpineTangent = false
  Binormal = (0,0,0)
  ClaimChildren = false
  Fit = 0
  FitJoin = 0
  InnerFit = 0
  InnerFitJoin = 0
  Linearize = true
  Mode = 0
  NewSolid = false
  Profile = -> Sketch089
  Spine = -> Sketch090 [Edge1,Edge2,Edge3,Edge4,Edge5]
  SpineTangent = false
  Suppress = false
  Transformation = 0
  Transition = 1
  TreeRank = 1481
  _ProfileBasedVersion = 2
FEATURE [PartDesign::Fillet] Fillet010
  AddSubType = 0
  Base = -> Pipe011 [Face5,Face9,Face13,Face17,Face22]
  BaseFeature = -> Pipe011
  NewSolid = false
  Radius = 1.99
  SupportTransform = false
  Suppress = false
  TreeRank = 1482
FEATURE [PartDesign::Body] Body063
  AutoGroupSolids = false
  ClaimAllChildren = false
  ExportMode = 0
  Group = -> [Import029,Sketch089,DatumPlane028,Sketch090,Pipe011,Fillet010]
  Origin = -> Origin068
  Tip = -> Fillet010
  TreeRank = 1462
  _ExportChildren = -> [Import029,DatumPlane028,Pipe011,Fillet010]
  _GroupVersion = 1
FEATURE [PartDesign::FeatureBase] Clone022
  BaseFeature = -> Body053
  NewSolid = false
  Suppress = false
  TreeRank = 1492
FEATURE [PartDesign::Body] Body064
  AutoGroupSolids = false
  BaseFeature = -> Body053
  ClaimAllChildren = false
  ExportMode = 0
  Group = -> [Clone022]
  Origin = -> Origin069
  Tip = -> Clone022
  TreeRank = 1494
  _ExportChildren = -> [Clone022]
  _GroupVersion = 1
FEATURE [Part::MultiCommon] Common002  label="top groove support"
  Shapes = -> [Body064,Body063]
  TreeRank = 3180
FEATURE [PartDesign::ShapeBinder] ShapeBinder025
  Support = -> [Clone019]
  TraceSupport = false
  TreeRank = 1508
FEATURE [Sketcher::SketchObject] Sketch091
  ArcFitTolerance = 1e-06
  AttachmentSupport = -> [XY_Plane070]
  ExternalGeometry = -> [ShapeBinder025]
  FullyConstrained = true
  MapMode = 5
  Support = -> [XY_Plane070]
  TreeRank = 1509
  sketch-geometry (4):
    g0: LineSegment StartX=34 StartY=-45 StartZ=0 EndX=32 EndY=-45 EndZ=0
    g1: LineSegment StartX=32 StartY=-45 StartZ=0 EndX=32 EndY=-50 EndZ=0
    g2: LineSegment StartX=32 StartY=-50 StartZ=0 EndX=34 EndY=-50 EndZ=0
    g3: LineSegment StartX=34 StartY=-50 StartZ=0 EndX=34 EndY=-45 EndZ=0
  constraints (12):
    c: Coincident(g0,g1)
    c: Coincident(g1,g2)
    c: Coincident(g2,g3)
    c: Coincident(g3,g0)
    c: Horizontal(g0)
    c: Horizontal(g2)
    c: Vertical(g1)
    c: Vertical(g3)
    c: PointOnObject(g0,g-3)
    c: DistanceY(g1,g1) = 5
    c: DistanceX(g0,g0) = 2
    c: DistanceY(g-3,g1) = 3.5
FEATURE [Sketcher::SketchObject] Sketch092
  ArcFitTolerance = 1e-06
  AttachmentSupport = -> [XZ_Plane070]
  ExternalGeometry = -> [ShapeBinder025]
  FullyConstrained = true
  MapMode = 5
  Placement = pos=(0,0,0) rot=(1,0,0;1.5708rad)
  Support = -> [XZ_Plane070]
  TreeRank = 1510
  sketch-geometry (5):
    g0: LineSegment StartX=34 StartY=0 StartZ=0 EndX=34 EndY=6 EndZ=0
    g1: LineSegment StartX=-34 StartY=6 StartZ=0 EndX=-34 EndY=0 EndZ=0
    g2: LineSegment StartX=-27 StartY=13 StartZ=0 EndX=27 EndY=13 EndZ=0
    g3: ArcOfCircle CenterX=27 CenterY=6 CenterZ=0 NormalX=0 NormalY=0 NormalZ=1 AngleXU=0 Radius=7 StartAngle=0 EndAngle=1.5708
    g4: ArcOfCircle CenterX=-27 CenterY=6 CenterZ=0 NormalX=0 NormalY=0 NormalZ=1 AngleXU=0 Radius=7 StartAngle=1.5708 EndAngle=3.14159
  constraints (13):
    c: Coincident(g0,g-4)
    c: Coincident(g0,g-4)
    c: Coincident(g1,g-5)
    c: PointOnObject(g1,g-1)
    c: Vertical(g1)
    c: Coincident(g2,g-5)
    c: Coincident(g2,g-3)
    c: Coincident(g3,g-3)
    c: Coincident(g3,g0)
    c: Coincident(g3,g2)
    c: Coincident(g4,g-5)
    c: Coincident(g4,g2)
    c: Coincident(g4,g1)
FEATURE [PartDesign::AdditivePipe] Pipe012
  AddSubType = 0
  AuxilleryCurvelinear = true
  AuxillerySpineTangent = false
  Binormal = (0,0,0)
  ClaimChildren = false
  Fit = 0
  FitJoin = 0
  InnerFit = 0
  InnerFitJoin = 0
  Linearize = true
  Mode = 0
  NewSolid = false
  Profile = -> Sketch091
  Spine = -> Sketch092 [Edge1,Edge2,Edge3,Edge4,Edge5]
  SpineTangent = false
  Suppress = false
  Transformation = 0
  Transition = 1
  TreeRank = 1511
  _ProfileBasedVersion = 2
FEATURE [PartDesign::Fillet] Fillet011
  AddSubType = 0
  Base = -> Pipe012 [Face3,Face7,Face11,Face15,Face20]
  BaseFeature = -> Pipe012
  NewSolid = false
  Radius = 1.99
  SupportTransform = false
  Suppress = false
  TreeRank = 1512
FEATURE [PartDesign::Body] Body065
  AutoGroupSolids = false
  ClaimAllChildren = false
  ExportMode = 0
  Group = -> [ShapeBinder025,Sketch091,Sketch092,Pipe012,Fillet011]
  Origin = -> Origin070
  Tip = -> Fillet011
  TreeRank = 1527
  _ExportChildren = -> [ShapeBinder025,Pipe012,Fillet011]
  _GroupVersion = 1
FEATURE [Part::SubShapeBinder] Import030  label="Import030(Clone019)"
  BindCopyOnChange = 0
  BindMode = 0
  ClaimChildren = false
  Context = -> Body069 [Import030.]
  FillStyle = 0
  Fuse = false
  MakeFace = false
  OffsetFill = false
  OffsetIntersection = false
  OffsetJoinType = 0
  OffsetOpenResult = false
  PartialLoad = false
  Relative = true
  Support = -> [Body053[Clone019.]]
  TreeRank = 1581
  _Version = 8
FEATURE [Sketcher::SketchObject] Sketch093
  ArcFitTolerance = 1e-06
  AttachmentSupport = -> [XY_Plane075]
  ExternalGeometry = -> [Import030]
  FullyConstrained = true
  MapMode = 5
  Support = -> [XY_Plane075]
  TreeRank = 1580
  sketch-geometry (4):
    g0: LineSegment StartX=34 StartY=3.1 StartZ=0 EndX=33 EndY=3.1 EndZ=0
    g1: LineSegment StartX=33 StartY=3.1 StartZ=0 EndX=33 EndY=-1.9 EndZ=0
    g2: LineSegment StartX=33 StartY=-1.9 StartZ=0 EndX=34 EndY=-1.9 EndZ=0
    g3: LineSegment StartX=34 StartY=-1.9 StartZ=0 EndX=34 EndY=3.1 EndZ=0
  constraints (12):
    c: Coincident(g0,g1)
    c: Coincident(g1,g2)
    c: Coincident(g2,g3)
    c: Coincident(g3,g0)
    c: Horizontal(g0)
    c: Horizontal(g2)
    c: Vertical(g1)
    c: Vertical(g3)
    c: PointOnObject(g0,g-3)
    c: DistanceY(g1,g1) = 5
    c: DistanceX(g0,g0) = 1
    c: DistanceY(g0,g-3) = 30.4
FEATURE [PartDesign::ShapeBinder] ShapeBinder026
  Support = -> [Clone019]
  TraceSupport = false
  TreeRank = 1582
FEATURE [Sketcher::SketchObject] Sketch094
  ArcFitTolerance = 1e-06
  AttachmentSupport = -> [XZ_Plane075]
  ExternalGeometry = -> [ShapeBinder026]
  FullyConstrained = true
  MapMode = 5
  Placement = pos=(0,0,0) rot=(1,0,0;1.5708rad)
  Support = -> [XZ_Plane075]
  TreeRank = 1583
  sketch-geometry (5):
    g0: LineSegment StartX=34 StartY=0 StartZ=0 EndX=34 EndY=6 EndZ=0
    g1: LineSegment StartX=27 StartY=13 StartZ=0 EndX=-27 EndY=13 EndZ=0
    g2: LineSegment StartX=-34 StartY=6 StartZ=0 EndX=-34 EndY=0 EndZ=0
    g3: ArcOfCircle CenterX=-27 CenterY=6 CenterZ=0 NormalX=0 NormalY=0 NormalZ=1 AngleXU=0 Radius=7 StartAngle=1.5708 EndAngle=3.14159
    g4: ArcOfCircle CenterX=27 CenterY=6 CenterZ=0 NormalX=0 NormalY=0 NormalZ=1 AngleXU=0 Radius=7 StartAngle=0 EndAngle=1.5708
  constraints (10):
    c: Coincident(g0,g-3)
    c: Coincident(g0,g-4)
    c: Coincident(g1,g-4)
    c: Coincident(g2,g-5)
    c: PointOnObject(g2,g-1)
    c: Tangent(g4,g1) = -1.5708
    c: Tangent(g3,g1) = -1.5708
    c: Tangent(g4,g0) = -1.5708
    c: Tangent(g3,g2) = -1.5708
    c: Vertical(g2)
FEATURE [PartDesign::AdditivePipe] Pipe013
  AddSubType = 0
  AuxilleryCurvelinear = true
  AuxillerySpineTangent = false
  Binormal = (0,0,0)
  ClaimChildren = false
  Fit = 0
  FitJoin = 0
  InnerFit = 0
  InnerFitJoin = 0
  Linearize = true
  Mode = 0
  NewSolid = false
  Profile = -> Sketch093
  Spine = -> Sketch094 [Edge1,Edge2,Edge3,Edge4,Edge5]
  SpineTangent = false
  Suppress = false
  Transformation = 0
  Transition = 1
  TreeRank = 1584
  _ProfileBasedVersion = 2
FEATURE [PartDesign::Fillet] Fillet012
  AddSubType = 0
  Base = -> Pipe013 [Face20,Face15,Face11,Face7,Face3]
  BaseFeature = -> Pipe013
  NewSolid = false
  Radius = 0.99
  SupportTransform = false
  Suppress = false
  TreeRank = 1585
FEATURE [PartDesign::ShapeBinder] ShapeBinder027
  TraceSupport = false
  TreeRank = 1620
FEATURE [PartDesign::ShapeBinder] ShapeBinder028
  TraceSupport = false
  TreeRank = 1621
FEATURE [Sketcher::SketchObject] Sketch095
  ArcFitTolerance = 1e-06
  AttachmentSupport = -> [XY_Plane076]
  ExternalGeometry = -> [ShapeBinder028,ShapeBinder027]
  FullyConstrained = true
  MapMode = 5
  Support = -> [XY_Plane076]
  TreeRank = 1622
  sketch-geometry (4):
    g0: LineSegment StartX=-32 StartY=31.26 StartZ=0 EndX=32 EndY=31.26 EndZ=0
    g1: LineSegment StartX=32 StartY=31.26 StartZ=0 EndX=32 EndY=-5.26 EndZ=0
    g2: LineSegment StartX=32 StartY=-5.26 StartZ=0 EndX=-32 EndY=-5.26 EndZ=0
    g3: LineSegment StartX=-32 StartY=-5.26 StartZ=0 EndX=-32 EndY=31.26 EndZ=0
  constraints (10):
    c: Coincident(g0,g1)
    c: Coincident(g1,g2)
    c: Coincident(g2,g3)
    c: Coincident(g3,g0)
    c: Horizontal(g0)
    c: Horizontal(g2)
    c: Vertical(g1)
    c: Vertical(g3)
    c: Coincident(g0,g-3)
    c: Coincident(g1,g-4)
FEATURE [PartDesign::Pad] Pad025
  AddSubType = 0
  AlongSketchNormal = false
  CheckUpToFaceLimits = true
  ClaimChildren = false
  Direction = (0,0,1)
  Fit = 0
  FitJoin = 0
  InnerFit = 0
  InnerFitJoin = 0
  InnerTaperAngle = 0
  InnerTaperAngleRev = 0
  Length = 20
  Length2 = 100
  Linearize = true
  NewSolid = false
  Profile = -> Sketch095
  Suppress = false
  TreeRank = 1623
  Type = 0
  _ProfileBasedVersion = 1
FEATURE [PartDesign::Body] Body070
  AutoGroupSolids = false
  ClaimAllChildren = false
  ExportMode = 0
  Group = -> [ShapeBinder027,ShapeBinder028,Sketch095,Pad025]
  Origin = -> Origin076
  Tip = -> Pad025
  TreeRank = 1619
  _ExportChildren = -> [ShapeBinder027,ShapeBinder028,Pad025]
  _GroupVersion = 1
FEATURE [Part::SubShapeBinder] Import031  label="Import031(Clone019)"
  BindCopyOnChange = 0
  BindMode = 0
  ClaimChildren = false
  Context = -> Part [Part005.Body071.Import031.]
  FillStyle = 0
  Fuse = false
  MakeFace = false
  OffsetFill = false
  OffsetIntersection = false
  OffsetJoinType = 0
  OffsetOpenResult = false
  PartialLoad = false
  Relative = true
  Support = -> [Body053[Clone019.]]
  TreeRank = 1745
  _Version = 8
FEATURE [Part::SubShapeBinder] Import032  label="Import032(top groove support)"
  BindCopyOnChange = 0
  BindMode = 0
  ClaimChildren = false
  Context = -> Part [Part005.Body071.Import032.]
  FillStyle = 0
  Fuse = false
  MakeFace = false
  OffsetFill = false
  OffsetIntersection = false
  OffsetJoinType = 0
  OffsetOpenResult = false
  PartialLoad = false
  Relative = true
  Support = -> [Common002]
  TreeRank = 1746
  _Version = 8
FEATURE [Part::SubShapeBinder] Import033  label="Import033(Common003)"
  BindCopyOnChange = 0
  BindMode = 0
  ClaimChildren = false
  Context = -> Part [Part005.Body071.Import033.]
  FillStyle = 0
  Fuse = false
  MakeFace = false
  OffsetFill = false
  OffsetIntersection = false
  OffsetJoinType = 0
  OffsetOpenResult = false
  PartialLoad = false
  Relative = true
  Support = -> [Common003]
  TreeRank = 1747
  _Version = 8
FEATURE [Sketcher::SketchObject] Sketch096
  ArcFitTolerance = 1e-06
  AttachmentSupport = -> [Import031]
  ExternalGeometry = -> [Import032,Import033]
  FullyConstrained = true
  MapMode = 5
  Placement = pos=(0,0,13) rot=(0,0,1;0rad)
  Support = -> [Import031]
  TreeRank = 3172
  sketch-geometry (4):
    g0: LineSegment StartX=-25 StartY=36.99 StartZ=0 EndX=-20 EndY=36.99 EndZ=0
    g1: LineSegment StartX=-20 StartY=36.99 StartZ=0 EndX=-20 EndY=2.11 EndZ=0
    g2: LineSegment StartX=-20 StartY=2.11 StartZ=0 EndX=-25 EndY=2.11 EndZ=0
    g3: LineSegment StartX=-25 StartY=2.11 StartZ=0 EndX=-25 EndY=36.99 EndZ=0
  constraints (12):
    c: Coincident(g0,g1)
    c: Coincident(g1,g2)
    c: Coincident(g2,g3)
    c: Coincident(g3,g0)
    c: Horizontal(g0)
    c: Horizontal(g2)
    c: Vertical(g1)
    c: Vertical(g3)
    c: Horizontal(g0,g-3)
    c: Horizontal(g1,g-4)
    c: DistanceX(g2,g1) = 5
    c: DistanceX(g-3,g0) = 2
FEATURE [PartDesign::Pad] Pad026
  AddSubType = 0
  AlongSketchNormal = false
  CheckUpToFaceLimits = true
  ClaimChildren = false
  Direction = (0,0,1)
  Fit = 0
  FitJoin = 0
  InnerFit = 0
  InnerFitJoin = 0
  InnerTaperAngle = 0
  InnerTaperAngleRev = 0
  Length = 1
  Length2 = 100
  Linearize = true
  NewSolid = false
  Profile = -> Sketch096
  Reversed = true
  Suppress = false
  TreeRank = 1748
  Type = 0
  _ProfileBasedVersion = 1
FEATURE [PartDesign::Fillet] Fillet013
  AddSubType = 0
  Base = -> Pad026 [Edge7,Edge12]
  BaseFeature = -> Pad026
  NewSolid = false
  Radius = 0.99
  SupportTransform = false
  Suppress = false
  TreeRank = 1749
FEATURE [Sketcher::SketchObject] Sketch103
  ArcFitTolerance = 1e-06
  AttachmentSupport = -> [XY_Plane080]
  FullyConstrained = true
  MapMode = 5
  Support = -> [XY_Plane080]
  TreeRank = 2378
  sketch-geometry (4):
    g0: LineSegment StartX=-34 StartY=11 StartZ=0 EndX=-14 EndY=11 EndZ=0
    g1: LineSegment StartX=-14 StartY=11 StartZ=0 EndX=-14 EndY=3 EndZ=0
    g2: LineSegment StartX=-14 StartY=3 StartZ=0 EndX=-34 EndY=3 EndZ=0
    g3: LineSegment StartX=-34 StartY=3 StartZ=0 EndX=-34 EndY=11 EndZ=0
  constraints (12):
    c: Coincident(g0,g1)
    c: Coincident(g1,g2)
    c: Coincident(g2,g3)
    c: Coincident(g3,g0)
    c: Horizontal(g0)
    c: Horizontal(g2)
    c: Vertical(g1)
    c: Vertical(g3)
    c: DistanceX(g2,g-1) = 34
    c: DistanceX(g2,g2) = 20
    c: DistanceY(g1,g1) = 8
    c: DistanceY(g-1,g1) = 3
FEATURE [PartDesign::Pad] Pad029
  AddSubType = 0
  AlongSketchNormal = false
  CheckUpToFaceLimits = true
  ClaimChildren = false
  Direction = (0,0,1)
  Fit = 0
  FitJoin = 0
  InnerFit = 0
  InnerFitJoin = 0
  InnerTaperAngle = 0
  InnerTaperAngleRev = 0
  Length = 14
  Length2 = 100
  Linearize = true
  NewSolid = false
  Profile = -> Sketch103
  Suppress = false
  TreeRank = 1941
  Type = 0
  _ProfileBasedVersion = 1
FEATURE [PartDesign::Pad] Pad030
  AddSubType = 0
  AlongSketchNormal = false
  BaseFeature = -> Pad029
  CheckUpToFaceLimits = true
  ClaimChildren = false
  Direction = (0,0,1)
  Fit = 0
  FitJoin = 0
  InnerFit = 0
  InnerFitJoin = 0
  InnerTaperAngle = 0
  InnerTaperAngleRev = 0
  Length = 6
  Length2 = 100
  Linearize = true
  NewSolid = false
  Profile = -> Sketch103
  Reversed = true
  Suppress = false
  TreeRank = 1942
  Type = 0
  _ProfileBasedVersion = 1
FEATURE [Sketcher::SketchObject] Sketch104
  ArcFitTolerance = 1e-06
  AttachmentSupport = -> [Pad030]
  ExternalGeometry = -> [Pad030]
  FullyConstrained = true
  MapMode = 5
  Placement = pos=(-34,0,0) rot=(0.57735,-0.57735,-0.57735;2.0944rad)
  Support = -> [Pad030]
  TreeRank = 2390
  sketch-geometry (1):
    g0: Circle CenterX=-8 CenterY=-2.1 CenterZ=0 NormalX=0 NormalY=0 NormalZ=1 AngleXU=0 Radius=2
  constraints (3):
    c: Diameter(g0) = 4
    c: DistanceY(g0,g-5) = 2.1
    c: DistanceX(g0,g-5) = 5
FEATURE [PartDesign::FeatureBase] Clone030
  BaseFeature = -> Body053
  NewSolid = false
  Suppress = false
  TreeRank = 1958
FEATURE [PartDesign::Pad] Pad031
  AddSubType = 0
  AlongSketchNormal = false
  BaseFeature = -> Clone030
  CheckUpToFaceLimits = true
  ClaimChildren = false
  Direction = (0,0,-1)
  Fit = 0
  FitJoin = 0
  InnerFit = 0
  InnerFitJoin = 0
  InnerTaperAngle = 0
  InnerTaperAngleRev = 0
  Length = 10
  Length2 = 100
  Linearize = true
  NewSolid = false
  Profile = -> Clone030 [Face4]
  Suppress = false
  TreeRank = 1961
  Type = 0
  _ProfileBasedVersion = 1
FEATURE [PartDesign::Body] Body078
  AutoGroupSolids = false
  BaseFeature = -> Body053
  ClaimAllChildren = false
  ExportMode = 0
  Group = -> [Clone030,Pad031]
  Origin = -> Origin092
  Tip = -> Pad031
  TreeRank = 3439
  _ExportChildren = -> [Clone030,Pad031]
  _GroupVersion = 1
FEATURE [Part::SubShapeBinder] Import035  label="Import035(main body)"
  BindCopyOnChange = 0
  BindMode = 0
  ClaimChildren = false
  Context = -> Part [Body079.Import035.]
  FillStyle = 0
  Fuse = false
  MakeFace = false
  OffsetFill = false
  OffsetIntersection = false
  OffsetJoinType = 0
  OffsetOpenResult = false
  PartialLoad = false
  Relative = true
  TreeRank = 1977
  _Version = 8
FEATURE [Sketcher::SketchObject] Sketch105
  ArcFitTolerance = 1e-06
  AttachmentSupport = -> [Import035]
  ExternalGeometry = -> [Import035]
  FullyConstrained = true
  MapMode = 5
  Placement = pos=(0,0,11) rot=(0,0,1;0rad)
  Support = -> [Import035]
  TreeRank = 1978
  sketch-geometry (4):
    g0: LineSegment StartX=33.7446 StartY=-43.5 StartZ=0 EndX=-33.7446 EndY=-43.5 EndZ=0
    g1: LineSegment StartX=-33.7446 StartY=-43.5 StartZ=0 EndX=-33.7446 EndY=-93.5 EndZ=0
    g2: LineSegment StartX=-33.7446 StartY=-93.5 StartZ=0 EndX=33.7446 EndY=-93.5 EndZ=0
    g3: LineSegment StartX=33.7446 StartY=-93.5 StartZ=0 EndX=33.7446 EndY=-43.5 EndZ=0
  constraints (12):
    c: Coincident(g1,g2)
    c: Coincident(g2,g3)
    c: Coincident(g3,g0)
    c: Horizontal(g0)
    c: Horizontal(g2)
    c: Vertical(g1)
    c: Vertical(g3)
    c: Vertical(g-4,g0)
    c: DistanceY(g3,g3) = 50
    c: Vertical(g0,g-3)
    c: DistanceY(g-3,g0) = 10
    c: Coincident(g1,g0)
FEATURE [PartDesign::Pad] Pad032
  AddSubType = 0
  AlongSketchNormal = false
  CheckUpToFaceLimits = true
  ClaimChildren = false
  Direction = (0,0,1)
  Fit = 0
  FitJoin = 0
  InnerFit = 0
  InnerFitJoin = 0
  InnerTaperAngle = 0
  InnerTaperAngleRev = 0
  Length = 10
  Length2 = 100
  Linearize = true
  NewSolid = false
  Profile = -> Sketch105
  Suppress = false
  TreeRank = 1979
  Type = 0
  _ProfileBasedVersion = 1
FEATURE [PartDesign::Pad] Pad033
  AddSubType = 0
  AlongSketchNormal = false
  BaseFeature = -> Pad032
  CheckUpToFaceLimits = true
  ClaimChildren = false
  Direction = (0,0,-1)
  Fit = 0
  FitJoin = 0
  InnerFit = 0
  InnerFitJoin = 0
  InnerTaperAngle = 0
  InnerTaperAngleRev = 0
  Length = 1
  Length2 = 100
  Linearize = true
  NewSolid = false
  Profile = -> Pad032 [Face5]
  Suppress = false
  TreeRank = 1981
  Type = 0
  _ProfileBasedVersion = 1
FEATURE [Part::SubShapeBinder] Import036  label="Import036(Pad030)"
  BindCopyOnChange = 0
  BindMode = 0
  ClaimChildren = false
  Context = -> Part [Part007.Body079.Import036.]
  FillStyle = 0
  Fuse = false
  MakeFace = false
  OffsetFill = false
  OffsetIntersection = false
  OffsetJoinType = 0
  OffsetOpenResult = false
  PartialLoad = false
  Relative = true
  Support = -> [Body073[Pad030.]]
  TreeRank = 1985
  _Version = 8
FEATURE [Sketcher::SketchObject] Sketch106
  ArcFitTolerance = 1e-06
  AttachmentSupport = -> [Import036]
  ExternalGeometry = -> [Import036]
  FullyConstrained = false
  MapMode = 5
  Placement = pos=(0,0,-6) rot=(1,0,0;3.14159rad)
  Support = -> [Import036]
  TreeRank = 1986
  sketch-geometry (4):
    g0: LineSegment StartX=-34 StartY=-3 StartZ=0 EndX=-26.4982 EndY=-3 EndZ=0
    g1: LineSegment StartX=-26.4982 StartY=-3 StartZ=0 EndX=-26.4982 EndY=-16.043 EndZ=0
    g2: LineSegment StartX=-26.4982 StartY=-16.043 StartZ=0 EndX=-34 EndY=-16.043 EndZ=0
    g3: LineSegment StartX=-34 StartY=-16.043 StartZ=0 EndX=-34 EndY=-3 EndZ=0
  constraints (9):
    c: Coincident(g0,g1)
    c: Coincident(g1,g2)
    c: Coincident(g2,g3)
    c: Coincident(g3,g0)
    c: Horizontal(g0)
    c: Horizontal(g2)
    c: Vertical(g1)
    c: Vertical(g3)
    c: Coincident(g0,g-4)
FEATURE [PartDesign::Body] Body079  label="screw support cutout"
  AutoGroupSolids = false
  ClaimAllChildren = false
  ExportMode = 0
  Group = -> [Import035,Sketch105,Pad032,Pad033,Import036,Sketch106]
  Origin = -> Origin093
  Tip = -> Pad033
  TreeRank = 3356
  _ExportChildren = -> [Import035,Pad032,Pad033,Import036,Sketch106]
  _GroupVersion = 1
FEATURE [Sketcher::SketchObject] Sketch107
  ArcFitTolerance = 1e-06
  AttachmentSupport = -> [Pad030]
  ExternalGeometry = -> [Pad030]
  FullyConstrained = true
  MapMode = 5
  Placement = pos=(0,0,-6) rot=(1,0,0;3.14159rad)
  Support = -> [Pad030]
  TreeRank = 1987
  sketch-geometry (4):
    g0: LineSegment StartX=-34 StartY=-3 StartZ=0 EndX=-27 EndY=-3 EndZ=0
    g1: LineSegment StartX=-27 StartY=-3 StartZ=0 EndX=-27 EndY=-11 EndZ=0
    g2: LineSegment StartX=-27 StartY=-11 StartZ=0 EndX=-34 EndY=-11 EndZ=0
    g3: LineSegment StartX=-34 StartY=-11 StartZ=0 EndX=-34 EndY=-3 EndZ=0
  constraints (11):
    c: Coincident(g0,g1)
    c: Coincident(g1,g2)
    c: Coincident(g2,g3)
    c: Coincident(g3,g0)
    c: Horizontal(g0)
    c: Horizontal(g2)
    c: Vertical(g1)
    c: Vertical(g3)
    c: Coincident(g0,g-4)
    c: Horizontal(g1,g-4)
    c: DistanceX(g0,g0) = 7
FEATURE [Sketcher::SketchObject] Sketch108
  ArcFitTolerance = 1e-06
  AttachmentSupport = -> [Pad030]
  ExternalGeometry = -> [Pad030]
  FullyConstrained = true
  MapMode = 5
  Placement = pos=(-14,0,0) rot=(0.57735,0.57735,0.57735;2.0944rad)
  Support = -> [Pad030]
  TreeRank = 2391
  sketch-geometry (1):
    g0: Circle CenterX=7 CenterY=-2 CenterZ=0 NormalX=0 NormalY=0 NormalZ=1 AngleXU=0 Radius=1.7
  constraints (3):
    c: Diameter(g0) = 3.4
    c: DistanceY(g0,g-4) = 2
    c: DistanceX(g-3,g0) = 4
FEATURE [Sketcher::SketchObject] Sketch109
  ArcFitTolerance = 1e-06
  AttachmentSupport = -> [Pad030]
  ExternalGeometry = -> [Pad030]
  FullyConstrained = true
  MapMode = 5
  Placement = pos=(-14,0,0) rot=(0.57735,0.57735,0.57735;2.0944rad)
  Support = -> [Pad030]
  TreeRank = 2380
  sketch-geometry (1):
    g0: Circle CenterX=7 CenterY=7 CenterZ=0 NormalX=0 NormalY=0 NormalZ=1 AngleXU=0 Radius=2
  constraints (3):
    c: DistanceX(g0,g-3) = 4
    c: DistanceY(g0,g-3) = 7
    c: Diameter(g0) = 4
FEATURE [Part::SubShapeBinder] Import037  label="Import037(DatumPlane)"
  BindCopyOnChange = 0
  BindMode = 0
  ClaimChildren = false
  Context = -> <external cq-80-bottom.FCStd>#Part [Body001.Import037.]
  FillStyle = 0
  Fuse = false
  MakeFace = false
  OffsetFill = false
  OffsetIntersection = false
  OffsetJoinType = 0
  OffsetOpenResult = false
  PartialLoad = false
  Relative = true
  Support = -> [DatumPlane029]
  TreeRank = 76
  _Version = 8
FEATURE [Part::SubShapeBinder] Import038  label="Import038(DatumPlane001)"
  BindCopyOnChange = 0
  BindMode = 0
  ClaimChildren = false
  Context = -> <external cq-80-bottom.FCStd>#Part [Body001.Import038.]
  FillStyle = 0
  Fuse = false
  MakeFace = false
  OffsetFill = false
  OffsetIntersection = false
  OffsetJoinType = 0
  OffsetOpenResult = false
  PartialLoad = false
  Relative = true
  Support = -> [DatumPlane030]
  TreeRank = 80
  _Version = 8
FEATURE [Part::SubShapeBinder] Import039  label="Import039(DatumPlane002)"
  BindCopyOnChange = 0
  BindMode = 0
  ClaimChildren = false
  Context = -> <external cq-80-bottom.FCStd>#Part [Body001.Import039.]
  FillStyle = 0
  Fuse = false
  MakeFace = false
  OffsetFill = false
  OffsetIntersection = false
  OffsetJoinType = 0
  OffsetOpenResult = false
  PartialLoad = false
  Relative = true
  Support = -> [DatumPlane031]
  TreeRank = 85
  _Version = 8
FEATURE [Part::SubShapeBinder] Import040  label="Import040(DatumPlane003)"
  BindCopyOnChange = 0
  BindMode = 0
  ClaimChildren = false
  Context = -> <external cq-80-bottom.FCStd>#Part [Body001.Import040.]
  FillStyle = 0
  Fuse = false
  MakeFace = false
  OffsetFill = false
  OffsetIntersection = false
  OffsetJoinType = 0
  OffsetOpenResult = false
  PartialLoad = false
  Relative = true
  Support = -> [Body080[DatumPlane032.]]
  TreeRank = 89
  _Version = 8
FEATURE [Sketcher::SketchObject] Sketch111
  ArcFitTolerance = 0
  AttachmentSupport = -> [XY_Plane088]
  FullyConstrained = true
  MapMode = 5
  Support = -> [XY_Plane088]
  TreeRank = 2826
  sketch-geometry (15):
    g0: LineSegment [constr] StartX=-35 StartY=53.5 StartZ=0 EndX=35 EndY=53.5 EndZ=0
    g1: LineSegment [constr] StartX=35 StartY=53.5 StartZ=0 EndX=35 EndY=-53.5 EndZ=0
    g2: LineSegment [constr] StartX=35 StartY=-53.5 StartZ=0 EndX=-35 EndY=-53.5 EndZ=0
    g3: LineSegment [constr] StartX=-35 StartY=-53.5 StartZ=0 EndX=-35 EndY=53.5 EndZ=0
    g4: LineSegment StartX=-35 StartY=-53.5 StartZ=0 EndX=-35 EndY=-69.5 EndZ=0
    g5: LineSegment [constr] StartX=-35 StartY=-69.5 StartZ=0 EndX=35 EndY=-69.5 EndZ=0
    g6: LineSegment StartX=35 StartY=-69.5 StartZ=0 EndX=35 EndY=-53.5 EndZ=0
    g7: LineSegment StartX=-35 StartY=-69.5 StartZ=0 EndX=-4.5 EndY=-97.9417 EndZ=0
    g8: LineSegment StartX=-4.5 StartY=-97.9417 StartZ=0 EndX=4.5 EndY=-97.9417 EndZ=0
    g9: LineSegment StartX=4.5 StartY=-97.9417 StartZ=0 EndX=35 EndY=-69.5 EndZ=0
    g10: LineSegment StartX=-15 StartY=53.5 StartZ=0 EndX=15 EndY=53.5 EndZ=0
    g11: LineSegment StartX=-35 StartY=33.5 StartZ=0 EndX=-35 EndY=-53.5 EndZ=0
    g12: LineSegment StartX=35 StartY=33.5 StartZ=0 EndX=35 EndY=-53.5 EndZ=0
    g13: ArcOfCircle CenterX=15 CenterY=33.5 CenterZ=0 NormalX=0 NormalY=0 NormalZ=1 AngleXU=0 Radius=20 StartAngle=1e-16 EndAngle=1.5708
    g14: ArcOfCircle CenterX=-15 CenterY=33.5 CenterZ=0 NormalX=0 NormalY=0 NormalZ=1 AngleXU=0 Radius=20 StartAngle=1.5708 EndAngle=3.14159
  constraints (39):
    c: Coincident(g0,g1)
    c: Coincident(g1,g2)
    c: Coincident(g2,g3)
    c: Coincident(g3,g0)
    c: Horizontal(g0)
    c: Horizontal(g2)
    c: Vertical(g1)
    c: Vertical(g3)
    c: DistanceX(g0,g0) = 70
    c: DistanceY(g3,g3) = 107
    c: Symmetric(g0,g2,g-1)
    c: Coincident(g2,g4)
    c: Vertical(g4)
    c: Coincident(g4,g5)
    c: Horizontal(g5)
    c: Coincident(g5,g6)
    c: Coincident(g6,g1)
    c: Vertical(g6)
    c: DistanceY(g4,g4) = 16
    c: Coincident(g4,g7)
    c: Coincident(g7,g8)
    c: Horizontal(g8)
    c: Coincident(g8,g9)
    c: Coincident(g9,g5)
    c: DistanceX(g8,g8) = 9
    c: Equal(g9,g7)
    c: Angle(g5,g9) = 0.750492
    c: Coincident(g11,g4)
    c: Coincident(g12,g6)
    c: Tangent(g14,g10) = 1.5708
    c: Tangent(g13,g10) = 1.5708
    c: Tangent(g12,g13) = 1.5708
    c: Tangent(g11,g14) = -1.5708
    c: Vertical(g12)
    c: Vertical(g11)
    c: Horizontal(g10)
    c: Radius(g14) = 20
    c: Radius(g13) = 20
    c: DistanceY(g-1,g10) = 53.5
FEATURE [Sketcher::SketchObject] Sketch001
  ArcFitTolerance = 1e-06
  AttachmentSupport = -> [Sketch111]
  ExternalGeometry = -> [Sketch111]
  FullyConstrained = true
  MapMode = 5
  Support = -> [Sketch111]
  TreeRank = 2827
  sketch-geometry (15):
    g0: LineSegment StartX=0 StartY=0 StartZ=0 EndX=0 EndY=17 EndZ=0
    g1: ArcOfCircle CenterX=-19 CenterY=-62.543 CenterZ=0 NormalX=0 NormalY=0 NormalZ=1 AngleXU=0 Radius=16 StartAngle=3.14159 EndAngle=3.9619
    g2: ArcOfCircle CenterX=19 CenterY=-62.543 CenterZ=0 NormalX=0 NormalY=0 NormalZ=1 AngleXU=0 Radius=16 StartAngle=5.46288 EndAngle=6.28319
    g3: ArcOfCircle CenterX=-4.10609 CenterY=-96.9417 CenterZ=0 NormalX=0 NormalY=0 NormalZ=1 AngleXU=0 Radius=1 StartAngle=3.9619 EndAngle=4.71239
    g4: ArcOfCircle CenterX=4.10609 CenterY=-96.9417 CenterZ=0 NormalX=0 NormalY=0 NormalZ=1 AngleXU=0 Radius=1 StartAngle=4.71239 EndAngle=5.46288
    g5: LineSegment StartX=4.10609 StartY=-97.9417 StartZ=0 EndX=-4.10609 EndY=-97.9417 EndZ=0
    g6: LineSegment StartX=-4.78809 StartY=-97.6731 StartZ=0 EndX=-29.912 EndY=-74.2447 EndZ=0
    g7: LineSegment StartX=4.78809 StartY=-97.6731 StartZ=0 EndX=29.912 EndY=-74.2447 EndZ=0
    g8: LineSegment StartX=35 StartY=-53.5 StartZ=0 EndX=35 EndY=-62.543 EndZ=0
    g9: LineSegment StartX=-35 StartY=-62.543 StartZ=0 EndX=-35 EndY=-53.5 EndZ=0
    g10: LineSegment StartX=-35 StartY=17 StartZ=0 EndX=-35 EndY=-53.5 EndZ=0
    g11: LineSegment StartX=0 StartY=0 StartZ=0 EndX=0 EndY=-69.5 EndZ=0
    g12: LineSegment StartX=0 StartY=0 StartZ=0 EndX=0 EndY=-97.9417 EndZ=0
    g13: LineSegment StartX=0 StartY=17 StartZ=0 EndX=0 EndY=24.6 EndZ=0
    g14: LineSegment StartX=0 StartY=24.6 StartZ=0 EndX=0 EndY=44.6 EndZ=0
  constraints (40):
    c: Coincident(g0,g-1)
    c: PointOnObject(g0,g-2)
    c: Tangent(g1,g-5) = -1.5708
    c: Tangent(g1,g-4) = -1.5708
    c: Tangent(g2,g-8) = -1.5708
    c: Tangent(g2,g-6) = -1.5708
    c: Radius(g1) = 16
    c: Radius(g2) = 16
    c: Radius(g3) = 1
    c: Tangent(g3,g-5) = -1.5708
    c: Tangent(g3,g-7) = -1.5708
    c: Tangent(g4,g-7) = -1.5708
    c: Tangent(g4,g-6) = -1.5708
    c: Radius(g4) = 1
    c: Coincident(g5,g4)
    c: Coincident(g5,g3)
    c: Coincident(g6,g3)
    c: Coincident(g6,g1)
    c: Coincident(g7,g4)
    c: Coincident(g7,g2)
    c: Coincident(g8,g-9)
    c: Coincident(g8,g2)
    c: Coincident(g9,g1)
    c: Coincident(g9,g-4)
    c: PointOnObject(g10,g-3)
    c: Coincident(g10,g9)
    c: Horizontal(g0,g10)
    c: DistanceY(g0,g10) = 17
    c: Coincident(g11,g0)
    c: PointOnObject(g11,g-2)
    c: Coincident(g12,g0)
    c: PointOnObject(g12,g5)
    c: Vertical(g12)
    c: Horizontal(g11,g-5)
    c: Coincident(g13,g0)
    c: PointOnObject(g13,g-2)
    c: DistanceY(g13,g13) = 7.6
    c: Coincident(g14,g13)
    c: PointOnObject(g14,g-2)
    c: DistanceY(g14,g14) = 20
FEATURE [PartDesign::Plane] DatumPlane029
  AttachmentSupport = -> [Sketch001]
  Length = 10
  MapMode = 7
  MinimumLength = 10
  MinimumWidth = 10
  Placement = pos=(0,17,0) rot=(1,0,0;1.5708rad)
  ResizeMode = 0
  Support = -> [Sketch001]
  TreeRank = 22
  Width = 10
FEATURE [PartDesign::Plane] DatumPlane030
  AttachmentSupport = -> [Sketch001]
  Length = 10
  MapMode = 7
  MinimumLength = 10
  MinimumWidth = 10
  Placement = pos=(0,-69.5,0) rot=(0,0.707107,0.707107;3.14159rad)
  ResizeMode = 0
  Support = -> [Sketch001]
  TreeRank = 24
  Width = 10
FEATURE [PartDesign::Plane] DatumPlane031
  AttachmentSupport = -> [Sketch001]
  Length = 10
  MapMode = 7
  MinimumLength = 10
  MinimumWidth = 10
  Placement = pos=(0,-97.9417,0) rot=(0,0.707107,0.707107;3.14159rad)
  ResizeMode = 0
  Support = -> [Sketch001]
  TreeRank = 26
  Width = 10
FEATURE [PartDesign::Plane] DatumPlane032
  AttachmentSupport = -> [Sketch001]
  Length = 10
  MapMode = 7
  MinimumLength = 10
  MinimumWidth = 10
  Placement = pos=(0,24.6,0) rot=(1,0,0;1.5708rad)
  ResizeMode = 0
  Support = -> [Sketch001]
  TreeRank = 53
  Width = 10
FEATURE [PartDesign::Plane] DatumPlane033
  AttachmentSupport = -> [Sketch001]
  Length = 10
  MapMode = 7
  MinimumLength = 10
  MinimumWidth = 10
  Placement = pos=(0,44.6,0) rot=(1,0,0;1.5708rad)
  ResizeMode = 0
  Support = -> [Sketch001]
  TreeRank = 55
  Width = 10
FEATURE [Sketcher::SketchObject] Sketch002
  ArcFitTolerance = 1e-06
  AttachmentSupport = -> [DatumPlane029]
  ExternalGeometry = -> [Sketch001]
  FullyConstrained = true
  MapMode = 5
  Placement = pos=(0,17,0) rot=(1,0,0;1.5708rad)
  Support = -> [DatumPlane029]
  TreeRank = 48
  sketch-geometry (3):
    g0: ArcOfCircle CenterX=-9e-16 CenterY=15.1304 CenterZ=0 NormalX=0 NormalY=0 NormalZ=1 AngleXU=0 Radius=38.1304 StartAngle=3.54963 EndAngle=5.87515
    g1: GeomPoint [constr] X=0 Y=-23 Z=0
    g2: LineSegment StartX=-35 StartY=0 StartZ=0 EndX=35 EndY=0 EndZ=0
  constraints (7):
    c: Coincident(g-3,g0)
    c: Coincident(g0,g-5)
    c: PointOnObject(g1,g0)
    c: PointOnObject(g1,g-2)
    c: DistanceY(g1,g-1) = 23
    c: Coincident(g2,g0)
    c: Coincident(g2,g0)
FEATURE [Sketcher::SketchObject] Sketch003
  ArcFitTolerance = 1e-06
  AttachmentSupport = -> [DatumPlane030]
  ExternalGeometry = -> [Sketch001]
  FullyConstrained = true
  MapMode = 5
  Placement = pos=(0,-69.5,0) rot=(0,0.707107,0.707107;3.14159rad)
  Support = -> [DatumPlane030]
  TreeRank = 47
  sketch-geometry (3):
    g0: ArcOfCircle CenterX=-1.7e-15 CenterY=15.1304 CenterZ=0 NormalX=0 NormalY=0 NormalZ=1 AngleXU=0 Radius=38.1304 StartAngle=3.54963 EndAngle=5.87515
    g1: GeomPoint [constr] X=0 Y=-23 Z=0
    g2: LineSegment StartX=-35 StartY=2e-15 StartZ=0 EndX=35 EndY=2e-15 EndZ=0
  constraints (7):
    c: Coincident(g0,g-3)
    c: Coincident(g0,g-4)
    c: PointOnObject(g1,g0)
    c: PointOnObject(g1,g-2)
    c: DistanceY(g1,g-1) = 23
    c: Coincident(g2,g0)
    c: Coincident(g2,g0)
FEATURE [PartDesign::AdditiveLoft] Loft  label="Loft body"
  AddSubType = 0
  ClaimChildren = false
  Closed = false
  Fit = 0
  FitJoin = 0
  InnerFit = 0
  InnerFitJoin = 0
  Linearize = true
  NewSolid = false
  Placement = pos=(0,17,0) rot=(1,0,0;1.5708rad)
  Profile = -> Sketch002
  Ruled = false
  Sections = -> [Sketch003]
  SplitProfile = false
  Suppress = false
  TreeRank = 2828
  _ProfileBasedVersion = 1
FEATURE [Sketcher::SketchObject] Sketch004
  ArcFitTolerance = 1e-06
  AttachmentSupport = -> [DatumPlane031]
  ExternalGeometry = -> [Sketch001,Sketch003]
  FullyConstrained = true
  MapMode = 5
  Placement = pos=(0,-97.9417,0) rot=(0,0.707107,0.707107;3.14159rad)
  Support = -> [DatumPlane031]
  TreeRank = 43
  sketch-geometry (2):
    g0: ArcOfCircle CenterX=-2.17e-14 CenterY=15.1304 CenterZ=0 NormalX=0 NormalY=0 NormalZ=1 AngleXU=0 Radius=15.6777 StartAngle=4.44739 EndAngle=4.97739
    g1: LineSegment StartX=-4.10609 StartY=0 StartZ=0 EndX=4.10609 EndY=1.8e-15 EndZ=0
  constraints (5):
    c: Coincident(g0,g-3)
    c: Coincident(g-3,g0)
    c: Horizontal(g0,g-4)
    c: Coincident(g1,g0)
    c: Coincident(g1,g0)
FEATURE [PartDesign::AdditiveLoft] Loft001  label="Loft001 tail"
  AddSubType = 0
  BaseFeature = -> Loft
  ClaimChildren = false
  Closed = false
  Fit = 0
  FitJoin = 0
  InnerFit = 0
  InnerFitJoin = 0
  Linearize = true
  NewSolid = false
  Placement = pos=(0,17,0) rot=(1,0,0;1.5708rad)
  Profile = -> Sketch003
  Ruled = false
  Sections = -> [Sketch004]
  SplitProfile = false
  Suppress = false
  TreeRank = 2829
  _ProfileBasedVersion = 1
FEATURE [PartDesign::ShapeBinder] ShapeBinder031
  Placement = pos=(0,-97.9417,0) rot=(0,0.707107,0.707107;3.14159rad)
  Support = -> [Sketch004]
  TraceSupport = false
  TreeRank = 82
FEATURE [Sketcher::SketchObject] Sketch005
  ArcFitTolerance = 1e-06
  AttachmentSupport = -> [DatumPlane032]
  FullyConstrained = true
  MapMode = 5
  Placement = pos=(0,24.6,0) rot=(1,0,0;1.5708rad)
  Support = -> [DatumPlane032]
  TreeRank = 58
  sketch-geometry (2):
    g0: ArcOfCircle CenterX=0 CenterY=0 CenterZ=0 NormalX=0 NormalY=0 NormalZ=1 AngleXU=0 Radius=20 StartAngle=3.14159 EndAngle=6.28319
    g1: LineSegment StartX=20 StartY=0 StartZ=0 EndX=-20 EndY=0 EndZ=0
  constraints (6):
    c: PointOnObject(g0,g-1)
    c: PointOnObject(g0,g-1)
    c: Coincident(g1,g0)
    c: Coincident(g1,g0)
    c: Coincident(g0,g-1)
    c: Radius(g0) = 20
FEATURE [PartDesign::AdditiveLoft] Loft002  label="Loft002 neck"
  AddSubType = 0
  BaseFeature = -> Loft001
  ClaimChildren = false
  Closed = false
  Fit = 0
  FitJoin = 0
  InnerFit = 0
  InnerFitJoin = 0
  Linearize = true
  NewSolid = false
  Placement = pos=(0,17,0) rot=(1,0,0;1.5708rad)
  Profile = -> Sketch002
  Ruled = false
  Sections = -> [Sketch005]
  SplitProfile = false
  Suppress = false
  TreeRank = 2831
  _ProfileBasedVersion = 1
FEATURE [Sketcher::SketchObject] Sketch006
  ArcFitTolerance = 1e-06
  AttachmentSupport = -> [DatumPlane032]
  ExternalGeometry = -> [Sketch005]
  FullyConstrained = true
  MapMode = 5
  Placement = pos=(0,24.6,0) rot=(1,0,0;1.5708rad)
  Support = -> [DatumPlane032]
  TreeRank = 56
  sketch-geometry (3):
    g0: ArcOfCircle CenterX=0 CenterY=0 CenterZ=0 NormalX=0 NormalY=0 NormalZ=1 AngleXU=0 Radius=20 StartAngle=3.14159 EndAngle=4.71239
    g1: LineSegment StartX=0 StartY=0 StartZ=0 EndX=-20 EndY=2.4e-15 EndZ=0
    g2: LineSegment StartX=0 StartY=0 StartZ=0 EndX=0 EndY=-20 EndZ=0
  constraints (7):
    c: Coincident(g0,g-3)
    c: Coincident(g0,g-3)
    c: PointOnObject(g0,g-2)
    c: Coincident(g1,g0)
    c: Coincident(g1,g0)
    c: Coincident(g2,g0)
    c: Coincident(g2,g0)
FEATURE [PartDesign::Line] DatumLine008
  AttacherType = Attacher::AttachEngineLine
  AttachmentSupport = -> [Sketch006]
  Length = 10
  MapMode = 29
  MinimumLength = 10
  Placement = pos=(0,24.6,0) rot=(0,1,0;3.14159rad)
  ResizeMode = 0
  Support = -> [Sketch006]
  TreeRank = 2830
FEATURE [PartDesign::Revolution] Revolution007  label="Revolution007 head"
  AddSubType = 0
  Angle = 180
  Axis = (0,-2e-16,-1)
  Base = (0,24.6,0)
  BaseFeature = -> Loft002
  ClaimChildren = false
  Fit = 0
  FitJoin = 0
  InnerFit = 0
  InnerFitJoin = 0
  Linearize = true
  NewSolid = false
  Placement = pos=(0,17,0) rot=(1,0,0;1.5708rad)
  Profile = -> Sketch006
  ReferenceAxis = -> DatumLine008
  Suppress = false
  TreeRank = 2832
  _ProfileBasedVersion = 1
FEATURE [PartDesign::FeatureBase] Clone032
  BaseFeature = -> Revolution007
  NewSolid = false
  Placement = pos=(0,17,0) rot=(1,0,0;1.5708rad)
  Suppress = false
  TreeRank = 127
FEATURE [PartDesign::ShapeBinder] ShapeBinder030
  Placement = pos=(0,17,0) rot=(1,0,0;1.5708rad)
  Support = -> [Revolution007]
  TraceSupport = false
  TreeRank = 73
FEATURE [Sketcher::SketchObject] Sketch007
  ArcFitTolerance = 1e-06
  AttachmentSupport = -> [Import037]
  ExternalGeometry = -> [ShapeBinder030]
  FullyConstrained = true
  MapMode = 5
  Placement = pos=(0,17,-3.8e-15) rot=(1,0,0;1.5708rad)
  Support = -> [Import037]
  TreeRank = 77
  sketch-geometry (2):
    g0: ArcOfCircle CenterX=-9e-16 CenterY=15.1304 CenterZ=0 NormalX=0 NormalY=0 NormalZ=1 AngleXU=0 Radius=37.2146 StartAngle=3.56029 EndAngle=5.86449
    g1: LineSegment StartX=-34 StartY=0 StartZ=0 EndX=34 EndY=0 EndZ=0
  constraints (6):
    c: Coincident(g0,g-3)
    c: PointOnObject(g0,g-1)
    c: PointOnObject(g0,g-1)
    c: DistanceX(g-3,g0) = 1
    c: Coincident(g1,g0)
    c: Coincident(g1,g0)
FEATURE [Sketcher::SketchObject] Sketch008
  ArcFitTolerance = 1e-06
  AttachmentSupport = -> [Import038]
  ExternalGeometry = -> [Sketch007]
  FullyConstrained = true
  MapMode = 5
  Placement = pos=(-6e-15,-69.5,1.54e-14) rot=(0,0.707107,0.707107;3.14159rad)
  Support = -> [Import038]
  TreeRank = 81
  sketch-geometry (2):
    g0: ArcOfCircle CenterX=9e-16 CenterY=15.1304 CenterZ=0 NormalX=0 NormalY=0 NormalZ=1 AngleXU=0 Radius=37.2146 StartAngle=3.56029 EndAngle=5.86449
    g1: LineSegment StartX=-34 StartY=7.1e-15 StartZ=0 EndX=34 EndY=7.1e-15 EndZ=0
  constraints (5):
    c: Coincident(g0,g-3)
    c: Coincident(g0,g-3)
    c: Horizontal(g0,g-3)
    c: Coincident(g1,g0)
    c: Coincident(g1,g0)
FEATURE [Sketcher::SketchObject] Sketch112
  ArcFitTolerance = 1e-06
  AttachmentSupport = -> [Import039]
  ExternalGeometry = -> [Sketch007,ShapeBinder031]
  FullyConstrained = true
  MapMode = 5
  Placement = pos=(-8.5e-15,-97.9417,2.17e-14) rot=(0,0.707107,0.707107;3.14159rad)
  Support = -> [Import039]
  TreeRank = 86
  sketch-geometry (2):
    g0: ArcOfCircle CenterX=-2.17e-14 CenterY=15.1304 CenterZ=0 NormalX=0 NormalY=0 NormalZ=1 AngleXU=0 Radius=15.446 StartAngle=4.50991 EndAngle=4.91486
    g1: LineSegment StartX=-3.10609 StartY=0 StartZ=0 EndX=3.10609 EndY=0 EndZ=0
  constraints (6):
    c: Coincident(g0,g-4)
    c: PointOnObject(g0,g-1)
    c: PointOnObject(g0,g-1)
    c: DistanceX(g-4,g0) = 1
    c: Coincident(g1,g0)
    c: Coincident(g1,g0)
FEATURE [PartDesign::Body] Body001  label="old sketches"
  AutoGroupSolids = false
  ClaimAllChildren = false
  ExportMode = 0
  Group = -> [ShapeBinder030,Import037,Sketch007,Import038,Sketch008,ShapeBinder031,Import039,Sketch112,Import040]
  Origin = -> Origin002
  TreeRank = 2068
  _ExportChildren = -> [ShapeBinder030,Import037,Sketch007,Import038,Sketch008,ShapeBinder031,Import039,Sketch112,Import040]
  _GroupVersion = 1
FEATURE [Sketcher::SketchObject] Sketch114
  ArcFitTolerance = 1e-06
  AttachmentSupport = -> [DatumPlane032]
  ExternalGeometry = -> [Sketch005]
  FullyConstrained = true
  MapMode = 5
  Placement = pos=(0,24.6,0) rot=(1,0,0;1.5708rad)
  Support = -> [DatumPlane032]
  TreeRank = 93
  expr: Constraints[3] = Spreadsheet.bottom_shell_width
  sketch-geometry (3):
    g0: ArcOfCircle CenterX=0 CenterY=0 CenterZ=0 NormalX=0 NormalY=0 NormalZ=1 AngleXU=0 Radius=19 StartAngle=3.14159 EndAngle=4.71239
    g1: LineSegment StartX=-19 StartY=2.3e-15 StartZ=0 EndX=0 EndY=0 EndZ=0
    g2: LineSegment StartX=0 StartY=0 StartZ=0 EndX=0 EndY=-19 EndZ=0
  constraints (8):
    c: Coincident(g0,g-3)
    c: PointOnObject(g0,g-1)
    c: PointOnObject(g0,g-2)
    c: DistanceX(g-3,g0) = 1
    c: Coincident(g1,g0)
    c: Coincident(g1,g0)
    c: Coincident(g2,g0)
    c: Coincident(g2,g0)
FEATURE [PartDesign::Groove] Groove  label="Groove head cutout"
  AddSubType = 1
  Angle = 360
  Axis = (0,-2e-16,-1)
  Base = (0,24.6,0)
  BaseFeature = -> Revolution007
  ClaimChildren = false
  Fit = 0
  FitJoin = 0
  InnerFit = 0
  InnerFitJoin = 0
  Linearize = true
  NewSolid = false
  Placement = pos=(0,17,0) rot=(1,0,0;1.5708rad)
  Profile = -> Sketch114
  ReferenceAxis = -> DatumLine008
  Reversed = true
  Suppress = false
  TreeRank = 2833
  _ProfileBasedVersion = 1
FEATURE [Sketcher::SketchObject] Sketch119
  ArcFitTolerance = 1e-06
  AttachmentSupport = -> [XY_Plane088]
  ExternalGeometry = -> [Sketch111]
  FullyConstrained = true
  MapMode = 5
  Support = -> [XY_Plane088]
  TreeRank = 2836
  expr: Constraints[2] = Spreadsheet.bottom_shell_width + 1
  sketch-geometry (1):
    g0: LineSegment StartX=0 StartY=0 StartZ=0 EndX=0 EndY=-95.9417 EndZ=0
  constraints (3):
    c: Coincident(g0,g-1)
    c: PointOnObject(g0,g-2)
    c: DistanceY(g-3,g0) = 2
FEATURE [PartDesign::Plane] DatumPlane034
  AttachmentSupport = -> [Sketch119]
  Length = 10
  MapMode = 7
  MinimumLength = 10
  MinimumWidth = 10
  Placement = pos=(0,-95.9417,0) rot=(0,0.707107,0.707107;3.14159rad)
  ResizeMode = 0
  Support = -> [Sketch119]
  TreeRank = 102
  Width = 10
FEATURE [Sketcher::SketchObject] Sketch118
  ArcFitTolerance = 1e-06
  AttachmentSupport = -> [DatumPlane034]
  ExternalGeometry = -> [Sketch004]
  FullyConstrained = true
  MapMode = 5
  Placement = pos=(0,-95.9417,0) rot=(0,0.707107,0.707107;3.14159rad)
  Support = -> [DatumPlane034]
  TreeRank = 100
  expr: Constraints[3] = Spreadsheet.bottom_shell_width
  sketch-geometry (2):
    g0: ArcOfCircle CenterX=-2.17e-14 CenterY=15.1304 CenterZ=0 NormalX=0 NormalY=0 NormalZ=1 AngleXU=0 Radius=15.446 StartAngle=4.50991 EndAngle=4.91486
    g1: LineSegment StartX=3.10609 StartY=0 StartZ=0 EndX=-3.10609 EndY=0 EndZ=0
  constraints (6):
    c: Coincident(g0,g-3)
    c: PointOnObject(g0,g-1)
    c: PointOnObject(g0,g-1)
    c: DistanceX(g0,g-3) = 1
    c: Coincident(g1,g0)
    c: Coincident(g1,g0)
FEATURE [Sketcher::SketchObject] Sketch120  label="inner plane sketch"
  ArcFitTolerance = 1e-06
  AttachmentSupport = -> [XY_Plane088]
  ExternalGeometry = -> [Sketch005,Sketch002,Sketch111]
  FullyConstrained = true
  MapMode = 5
  Support = -> [XY_Plane088]
  TreeRank = 2841
  expr: Constraints[34] = Spreadsheet.bottom_shell_width
  expr: Constraints[35] = Spreadsheet.bottom_shell_width
  sketch-geometry (14):
    g0: LineSegment StartX=0 StartY=0 StartZ=0 EndX=0 EndY=23.708 EndZ=0
    g1: LineSegment StartX=0 StartY=0 StartZ=0 EndX=0 EndY=16.3856 EndZ=0
    g2: LineSegment StartX=0 StartY=0 StartZ=0 EndX=0 EndY=-69.0652 EndZ=0
    g3: LineSegment [constr] StartX=-34 StartY=-60 StartZ=0 EndX=-34 EndY=-69.0652 EndZ=0
    g4: LineSegment [constr] StartX=-34 StartY=-69.0652 StartZ=0 EndX=-22.2738 EndY=-80 EndZ=0
    g5: LineSegment [constr] StartX=-22.2738 StartY=-80 StartZ=0 EndX=-22.9558 EndY=-80.7314 EndZ=0
    g6: LineSegment [constr] StartX=-34 StartY=-60 StartZ=0 EndX=-35 EndY=-60 EndZ=0
    g7: LineSegment [constr] StartX=-20 StartY=24.6 StartZ=0 EndX=-35 EndY=17 EndZ=0
    g8: LineSegment [constr] StartX=-35 StartY=17 StartZ=0 EndX=-35 EndY=-53.5 EndZ=0
    g9: LineSegment [constr] StartX=-17.7874 StartY=24.6 StartZ=0 EndX=-34 EndY=16.3856 EndZ=0
    g10: LineSegment [constr] StartX=-34 StartY=16.3856 StartZ=0 EndX=-34 EndY=0 EndZ=0
    g11: LineSegment [constr] StartX=-20 StartY=24.6 StartZ=0 EndX=-19.548 EndY=23.708 EndZ=0
    g12: LineSegment [constr] StartX=-34 StartY=0 StartZ=0 EndX=-35 EndY=0 EndZ=0
    g13: LineSegment StartX=0 StartY=23.708 StartZ=0 EndX=-19.548 EndY=23.708 EndZ=0
  constraints (41):
    c: Coincident(g0,g-1)
    c: PointOnObject(g0,g-2)
    c: Coincident(g1,g0)
    c: Vertical(g1)
    c: Coincident(g2,g0)
    c: PointOnObject(g2,g-2)
    c: Coincident(g4,g3)
    c: DistanceY(g3,g0) = 60
    c: DistanceY(g4,g3) = 20
    c: Parallel(g4,g-6)
    c: Parallel(g3,g-7)
    c: Coincident(g5,g4)
    c: PointOnObject(g5,g-6)
    c: Coincident(g6,g3)
    c: PointOnObject(g6,g-7)
    c: Perpendicular(g-7,g6)
    c: Perpendicular(g-6,g5)
    c: Distance(g5) = 1
    c: DistanceX(g6,g6) = 1
    c: Horizontal(g3,g2)
    c: Coincident(g7,g-3)
    c: Coincident(g7,g-4)
    c: Coincident(g8,g-4)
    c: Coincident(g8,g-7)
    c: Coincident(g10,g9)
    c: Vertical(g10)
    c: Horizontal(g9,g-3)
    c: Horizontal(g10,g0)
    c: Parallel(g9,g7)
    c: Coincident(g11,g-3)
    c: PointOnObject(g11,g9)
    c: Coincident(g12,g10)
    c: PointOnObject(g12,g8)
    c: Horizontal(g12)
    c: DistanceX(g12,g12) = 1
    c: Distance(g11) = 1
    c: Perpendicular(g9,g11)
    c: Horizontal(g1,g9)
    c: Horizontal(g0,g11)
    c: Coincident(g13,g0)
    c: Coincident(g13,g11)
FEATURE [PartDesign::Plane] DatumPlane035
  AttachmentSupport = -> [Sketch120]
  Length = 10
  MapMode = 7
  MinimumLength = 10
  MinimumWidth = 10
  Placement = pos=(0,23.708,0) rot=(1,0,0;1.5708rad)
  ResizeMode = 0
  Support = -> [Sketch120]
  TreeRank = 2073
  Width = 10
FEATURE [Sketcher::SketchObject] Sketch115
  ArcFitTolerance = 1e-06
  AttachmentSupport = -> [DatumPlane035]
  ExternalGeometry = -> [Sketch005,Sketch120]
  FullyConstrained = true
  MapMode = 5
  Placement = pos=(0,23.708,0) rot=(1,0,0;1.5708rad)
  Support = -> [DatumPlane035]
  TreeRank = 95
  sketch-geometry (2):
    g0: ArcOfCircle CenterX=0 CenterY=2e-16 CenterZ=0 NormalX=0 NormalY=0 NormalZ=1 AngleXU=0 Radius=19.548 StartAngle=3.14159 EndAngle=6.28319
    g1: LineSegment StartX=-19.548 StartY=0 StartZ=0 EndX=19.548 EndY=0 EndZ=0
  constraints (6):
    c: Coincident(g0,g-3)
    c: PointOnObject(g0,g-1)
    c: PointOnObject(g0,g-1)
    c: Coincident(g1,g0)
    c: Coincident(g1,g0)
    c: Vertical(g0,g-4)
FEATURE [PartDesign::Plane] DatumPlane036
  AttachmentSupport = -> [Sketch120]
  Length = 10
  MapMode = 7
  MinimumLength = 10
  MinimumWidth = 10
  Placement = pos=(0,16.3856,0) rot=(1,0,0;1.5708rad)
  ResizeMode = 0
  Support = -> [Sketch120]
  TreeRank = 2074
  Width = 10
FEATURE [Sketcher::SketchObject] Sketch116
  ArcFitTolerance = 1e-06
  AttachmentSupport = -> [DatumPlane036]
  ExternalGeometry = -> [Sketch002]
  FullyConstrained = true
  MapMode = 5
  Placement = pos=(0,16.3856,0) rot=(1,0,0;1.5708rad)
  Support = -> [DatumPlane036]
  TreeRank = 96
  expr: Constraints[3] = Spreadsheet.bottom_shell_width
  sketch-geometry (2):
    g0: ArcOfCircle CenterX=-9e-16 CenterY=15.1304 CenterZ=0 NormalX=0 NormalY=0 NormalZ=1 AngleXU=0 Radius=37.2146 StartAngle=3.56029 EndAngle=5.86449
    g1: LineSegment StartX=-34 StartY=0 StartZ=0 EndX=34 EndY=0 EndZ=0
  constraints (6):
    c: Coincident(g0,g-3)
    c: PointOnObject(g0,g-1)
    c: PointOnObject(g0,g-1)
    c: DistanceX(g-3,g0) = 1
    c: Coincident(g1,g0)
    c: Coincident(g1,g0)
FEATURE [PartDesign::SubtractiveLoft] Loft003  label="Loft003 neck cutout"
  AddSubType = 1
  BaseFeature = -> Groove
  ClaimChildren = false
  Closed = false
  Fit = 0
  FitJoin = 0
  InnerFit = 0
  InnerFitJoin = 0
  Linearize = true
  NewSolid = false
  Placement = pos=(0,17,0) rot=(1,0,0;1.5708rad)
  Profile = -> Sketch115
  Ruled = false
  Sections = -> [Sketch116]
  SplitProfile = false
  Suppress = false
  TreeRank = 2834
  _ProfileBasedVersion = 1
FEATURE [PartDesign::Plane] DatumPlane037
  AttachmentSupport = -> [Sketch120]
  Length = 10
  MapMode = 7
  MinimumLength = 10
  MinimumWidth = 10
  Placement = pos=(0,-69.0652,0) rot=(0,0.707107,0.707107;3.14159rad)
  ResizeMode = 0
  Support = -> [Sketch120]
  TreeRank = 2075
  Width = 10
FEATURE [Sketcher::SketchObject] Sketch117
  ArcFitTolerance = 1e-06
  AttachmentSupport = -> [DatumPlane037]
  ExternalGeometry = -> [Sketch003]
  FullyConstrained = true
  MapMode = 5
  Placement = pos=(0,-69.0652,0) rot=(0,0.707107,0.707107;3.14159rad)
  Support = -> [DatumPlane037]
  TreeRank = 98
  expr: Constraints[3] = Spreadsheet.bottom_shell_width
  sketch-geometry (2):
    g0: ArcOfCircle CenterX=-1.7e-15 CenterY=15.1304 CenterZ=0 NormalX=0 NormalY=0 NormalZ=1 AngleXU=0 Radius=37.2146 StartAngle=3.56029 EndAngle=5.86449
    g1: LineSegment StartX=34 StartY=4.636e-13 StartZ=0 EndX=-34 EndY=0 EndZ=0
  constraints (6):
    c: Coincident(g0,g-3)
    c: PointOnObject(g0,g-1)
    c: PointOnObject(g0,g-1)
    c: DistanceX(g0,g-3) = 1
    c: Coincident(g1,g0)
    c: Coincident(g1,g0)
FEATURE [PartDesign::SubtractiveLoft] Loft004  label="Loft004 body cutout"
  AddSubType = 1
  BaseFeature = -> Loft003
  ClaimChildren = false
  Closed = false
  Fit = 0
  FitJoin = 0
  InnerFit = 0
  InnerFitJoin = 0
  Linearize = true
  NewSolid = false
  Placement = pos=(0,17,0) rot=(1,0,0;1.5708rad)
  Profile = -> Sketch116
  Ruled = false
  Sections = -> [Sketch117]
  SplitProfile = false
  Suppress = false
  TreeRank = 2835
  _ProfileBasedVersion = 1
FEATURE [PartDesign::SubtractiveLoft] Loft005  label="Loft005 tail cutout"
  AddSubType = 1
  BaseFeature = -> Loft004
  ClaimChildren = false
  Closed = false
  Fit = 0
  FitJoin = 0
  InnerFit = 0
  InnerFitJoin = 0
  Linearize = true
  NewSolid = false
  Placement = pos=(0,17,0) rot=(1,0,0;1.5708rad)
  Profile = -> Sketch117
  Ruled = false
  Sections = -> [Sketch118]
  SplitProfile = false
  Suppress = false
  TreeRank = 2837
  _ProfileBasedVersion = 1
FEATURE [PartDesign::Fillet] Fillet014  label="Fillet014 tail inside "
  AddSubType = 0
  Base = -> Loft005 [Edge32]
  BaseFeature = -> Loft005
  NewSolid = false
  Placement = pos=(0,17,0) rot=(1,0,0;1.5708rad)
  Radius = 16
  SupportTransform = false
  Suppress = false
  TreeRank = 2838
FEATURE [PartDesign::Fillet] Fillet015  label="Fillet015 tail outside"
  AddSubType = 0
  Base = -> Fillet014 [Edge30]
  BaseFeature = -> Fillet014
  NewSolid = false
  Placement = pos=(0,17,0) rot=(1,0,0;1.5708rad)
  Radius = 16
  SupportTransform = false
  Suppress = false
  TreeRank = 2839
FEATURE [PartDesign::Chamfer] Chamfer003
  AddSubType = 0
  Angle = 45
  Base = -> Fillet015 [Edge46]
  BaseFeature = -> Fillet015
  ChamferType = 0
  FlipDirection = false
  NewSolid = false
  Placement = pos=(0,17,0) rot=(1,0,0;1.5708rad)
  Size = 0.3
  Size2 = 1
  SupportTransform = false
  Suppress = false
  TreeRank = 2840
FEATURE [Sketcher::SketchObject] Sketch123
  ArcFitTolerance = 1e-06
  AttachmentSupport = -> [XY_Plane089]
  FullyConstrained = true
  MapMode = 5
  Support = -> [XY_Plane089]
  TreeRank = 2097
  sketch-geometry (1):
    g0: LineSegment StartX=0 StartY=-97.94 StartZ=0 EndX=-32.8 EndY=-97.94 EndZ=0
  constraints (4):
    c: PointOnObject(g0,g-2)
    c: Horizontal(g0)
    c: DistanceX(g0,g0) = 32.8
    c: DistanceY(g0,g-1) = 97.94
FEATURE [PartDesign::Plane] DatumPlane038
  AttachmentSupport = -> [Sketch123]
  Length = 151.442
  MapMode = 7
  MinimumLength = 10
  MinimumWidth = 10
  Placement = pos=(-32.8,-97.94,0) rot=(0.57735,0.57735,0.57735;2.0944rad)
  ResizeMode = 0
  Support = -> [Sketch123]
  TreeRank = 2098
  Width = 10
FEATURE [Sketcher::SketchObject] Sketch121
  ArcFitTolerance = 1e-06
  AttachmentSupport = -> [DatumPlane038]
  ExternalGeometry = -> [Sketch123]
  FullyConstrained = true
  MapMode = 5
  Placement = pos=(-32.8,-97.94,0) rot=(0.57735,0.57735,0.57735;2.0944rad)
  Support = -> [DatumPlane038]
  TreeRank = 2094
  sketch-geometry (4):
    g0: ArcOfCircle CenterX=11.0449 CenterY=4.22e-14 CenterZ=0 NormalX=0 NormalY=0 NormalZ=1 AngleXU=0 Radius=2.7551 StartAngle=-1.51e-14 EndAngle=1.77113
    g1: LineSegment StartX=10.4966 StartY=2.7 StartZ=0 EndX=-2.8 EndY=2.274e-13 EndZ=0
    g2: ArcOfCircle CenterX=11.0449 CenterY=4.22e-14 CenterZ=0 NormalX=0 NormalY=0 NormalZ=1 AngleXU=0 Radius=2.7551 StartAngle=4.51205 EndAngle=6.28319
    g3: LineSegment StartX=10.4966 StartY=-2.7 StartZ=0 EndX=-2.8 EndY=2.274e-13 EndZ=0
  constraints (11):
    c: PointOnObject(g0,g-1)
    c: PointOnObject(g0,g-1)
    c: PointOnObject(g1,g-1)
    c: Tangent(g1,g0) = -1.5708
    c: DistanceX(g1,g0) = 16.6
    c: DistanceY(g0,g0) = 2.7
    c: Tangent(g3,g2) = 1.5708
    c: Coincident(g2,g0)
    c: Coincident(g3,g1)
    c: Coincident(g2,g0)
    c: DistanceX(g1,g-3) = 2.8
FEATURE [Sketcher::SketchObject] Sketch122
  ArcFitTolerance = 1e-06
  AttachmentSupport = -> [Sketch121]
  FullyConstrained = true
  MapMode = 5
  Placement = pos=(-32.8,-97.94,0) rot=(0.57735,0.57735,0.57735;2.0944rad)
  Support = -> [Sketch121]
  TreeRank = 2096
FEATURE [Sketcher::SketchObject] Sketch124
  ArcFitTolerance = 1e-06
  AttachmentSupport = -> [YZ_Plane089]
  ExternalGeometry = -> [Sketch123,Sketch121]
  FullyConstrained = true
  MapMode = 5
  Placement = pos=(0,0,0) rot=(0.57735,0.57735,0.57735;2.0944rad)
  Support = -> [YZ_Plane089]
  TreeRank = 2099
  sketch-geometry (4):
    g0: ArcOfCircle CenterX=-79.8237 CenterY=0 CenterZ=0 NormalX=0 NormalY=0 NormalZ=1 AngleXU=0 Radius=3.8837 StartAngle=0 EndAngle=1.77113
    g1: LineSegment StartX=-80.5965 StartY=3.80602 StartZ=0 EndX=-99.34 EndY=0 EndZ=0
    g2: LineSegment StartX=-99.34 StartY=0 StartZ=0 EndX=-80.5965 EndY=-3.80602 EndZ=0
    g3: ArcOfCircle CenterX=-79.8237 CenterY=0 CenterZ=0 NormalX=0 NormalY=0 NormalZ=1 AngleXU=0 Radius=3.8837 StartAngle=4.51205 EndAngle=6.28319
  constraints (12):
    c: PointOnObject(g0,g-1)
    c: PointOnObject(g0,g-1)
    c: PointOnObject(g1,g-1)
    c: Coincident(g2,g1)
    c: Coincident(g3,g0)
    c: Coincident(g3,g2)
    c: Coincident(g3,g0)
    c: DistanceX(g-3,g0) = 22
    c: Tangent(g1,g0) = -1.5708
    c: Vertical(g2,g0)
    c: DistanceX(g1,g-3) = 1.4
    c: Parallel(g1,g-4)
FEATURE [PartDesign::AdditiveLoft] Loft006
  AddSubType = 0
  ClaimChildren = false
  Closed = false
  Fit = 0
  FitJoin = 0
  InnerFit = 0
  InnerFitJoin = 0
  Linearize = true
  NewSolid = false
  Placement = pos=(-32.8,-97.94,0) rot=(0.57735,0.57735,0.57735;2.0944rad)
  Profile = -> Sketch121
  Ruled = false
  Sections = -> [Sketch124]
  SplitProfile = false
  Suppress = false
  TreeRank = 2100
  _ProfileBasedVersion = 1
FEATURE [Sketcher::SketchObject] Sketch125
  ArcFitTolerance = 1e-06
  AttachmentSupport = -> [XY_Plane089]
  ExternalGeometry = -> [Loft006]
  FullyConstrained = true
  MapMode = 5
  Support = -> [XY_Plane089]
  TreeRank = 2101
  sketch-geometry (4):
    g0: LineSegment StartX=0 StartY=-95.9735 StartZ=0 EndX=-9.8 EndY=-97.1735 EndZ=0
    g1: LineSegment StartX=-9.8 StartY=-97.1735 StartZ=0 EndX=-12.5 EndY=-99.8735 EndZ=0
    g2: LineSegment StartX=-12.5 StartY=-99.8735 StartZ=0 EndX=0 EndY=-99.8735 EndZ=0
    g3: LineSegment StartX=0 StartY=-99.8735 StartZ=0 EndX=0 EndY=-95.9735 EndZ=0
  constraints (12):
    c: PointOnObject(g0,g-2)
    c: Coincident(g1,g0)
    c: PointOnObject(g1,g-3)
    c: Coincident(g2,g1)
    c: PointOnObject(g2,g-2)
    c: Horizontal(g2)
    c: Coincident(g3,g2)
    c: Coincident(g3,g0)
    c: DistanceX(g2,g2) = 12.5
    c: DistanceY(g2,g0) = 3.9
    c: DistanceX(g1,g0) = 2.7
    c: DistanceY(g1,g0) = 2.7
FEATURE [Sketcher::SketchObject] Sketch126
  ArcFitTolerance = 1e-06
  AttachmentSupport = -> [XY_Plane092]
  FullyConstrained = true
  MapMode = 5
  Support = -> [XY_Plane092]
  TreeRank = 2154
  sketch-geometry (7):
    g0: LineSegment StartX=-10.9282 StartY=-94 StartZ=0 EndX=-4 EndY=-90 EndZ=0
    g1: LineSegment StartX=4 StartY=-90 StartZ=0 EndX=10.9282 EndY=-94 EndZ=0
    g2: LineSegment StartX=-10.9282 StartY=-94 StartZ=0 EndX=-10.9282 EndY=-99 EndZ=0
    g3: LineSegment StartX=-10.9282 StartY=-99 StartZ=0 EndX=10.9282 EndY=-99 EndZ=0
    g4: LineSegment StartX=10.9282 StartY=-99 StartZ=0 EndX=10.9282 EndY=-94 EndZ=0
    g5: LineSegment StartX=4 StartY=-90 StartZ=0 EndX=0 EndY=-90 EndZ=0
    g6: LineSegment StartX=0 StartY=-90 StartZ=0 EndX=-4 EndY=-90 EndZ=0
  constraints (20):
    c: DistanceY(g0,g0) = 4
    c: Coincident(g2,g0)
    c: Coincident(g3,g2)
    c: Horizontal(g3)
    c: Coincident(g4,g3)
    c: Coincident(g4,g1)
    c: Vertical(g4)
    c: Coincident(g5,g1)
    c: PointOnObject(g5,g-2)
    c: Horizontal(g5)
    c: Coincident(g6,g5)
    c: Coincident(g6,g0)
    c: Horizontal(g6)
    c: Equal(g5,g6)
    c: DistanceX(g5,g5) = 4
    c: Angle(g-2,g0) = 2.0944
    c: DistanceY(g0,g-1) = 90
    c: Vertical(g2)
    c: Symmetric(g0,g1,g-2)
    c: DistanceY(g2,g2) = 5
FEATURE [PartDesign::Pad] Pad034
  AddSubType = 0
  AlongSketchNormal = false
  CheckUpToFaceLimits = true
  ClaimChildren = false
  Direction = (0,0,1)
  Fit = 0
  FitJoin = 0
  InnerFit = 0
  InnerFitJoin = 0
  InnerTaperAngle = 0
  InnerTaperAngleRev = 0
  Length = 14
  Length2 = 100
  Linearize = true
  NewSolid = false
  Profile = -> Sketch126
  Suppress = false
  TreeRank = 2156
  Type = 0
  _ProfileBasedVersion = 1
FEATURE [PartDesign::Mirrored] Mirrored
  AddSubType = 0
  BaseFeature = -> Loft006
  CopyShape = false
  MirrorPlane = -> YZ_Plane089
  NewSolid = false
  OriginalSubs = -> [Loft006]
  Originals = -> [Loft006]
  ParallelTransform = true
  Placement = pos=(-32.8,-97.94,0) rot=(0.57735,0.57735,0.57735;2.0944rad)
  SubTransform = true
  Suppress = false
  TreeRank = 2164
  _Version = 3
FEATURE [PartDesign::Pocket] Pocket010
  AddSubType = 1
  BaseFeature = -> Mirrored
  CheckUpToFaceLimits = true
  ClaimChildren = false
  Fit = 0
  FitJoin = 0
  InnerFit = 0
  InnerFitJoin = 0
  InnerTaperAngle = 0
  InnerTaperAngleRev = 0
  Length = 5
  Length2 = 100
  Linearize = true
  Midplane = true
  NewSolid = false
  Placement = pos=(-32.8,-97.94,0) rot=(0.57735,0.57735,0.57735;2.0944rad)
  Profile = -> Sketch125
  Suppress = false
  TreeRank = 2165
  Type = 0
  _ProfileBasedVersion = 1
  _Version = 1
FEATURE [PartDesign::Mirrored] Mirrored004
  AddSubType = 0
  BaseFeature = -> Pocket010
  CopyShape = false
  MirrorPlane = -> YZ_Plane089
  NewSolid = false
  OriginalSubs = -> [Pocket010]
  Originals = -> [Pocket010]
  ParallelTransform = true
  Placement = pos=(-32.8,-97.94,0) rot=(0.57735,0.57735,0.57735;2.0944rad)
  SubTransform = true
  Suppress = false
  TreeRank = 2166
  _Version = 3
FEATURE [PartDesign::Fillet] Fillet016
  AddSubType = 0
  Base = -> Mirrored004 [Face1,Face12]
  BaseFeature = -> Mirrored004
  NewSolid = false
  Placement = pos=(-32.8,-97.94,0) rot=(0.57735,0.57735,0.57735;2.0944rad)
  Radius = 1
  SupportTransform = false
  Suppress = false
  TreeRank = 2167
FEATURE [Sketcher::SketchObject] Sketch127
  ArcFitTolerance = 1e-06
  AttachmentSupport = -> [YZ_Plane094]
  FullyConstrained = true
  MapMode = 5
  Placement = pos=(0,0,0) rot=(0.57735,0.57735,0.57735;2.0944rad)
  Support = -> [YZ_Plane094]
  TreeRank = 2193
  sketch-geometry (12):
    g0: LineSegment StartX=-97.94 StartY=0.6 StartZ=0 EndX=-105.406 EndY=4.78273 EndZ=0
    g1: LineSegment StartX=-103.94 StartY=10.4 StartZ=0 EndX=-97.94 EndY=10.4 EndZ=0
    g2: LineSegment StartX=-97.94 StartY=7.4 StartZ=0 EndX=-103.94 EndY=7.4 EndZ=0
    g3: LineSegment StartX=-103.94 StartY=7.4 StartZ=0 EndX=-97.1569 EndY=3.6 EndZ=0
    g4: LineSegment StartX=-97.1569 StartY=3.6 StartZ=0 EndX=-90 EndY=3.6 EndZ=0
    g5: LineSegment StartX=-97.94 StartY=0.6 StartZ=0 EndX=-90 EndY=0.6 EndZ=0
    g6: LineSegment StartX=-90 StartY=0.6 StartZ=0 EndX=-90 EndY=3.6 EndZ=0
    g7: LineSegment StartX=-97.94 StartY=7.4 StartZ=0 EndX=-90 EndY=7.4 EndZ=0
    g8: LineSegment StartX=-90 StartY=7.4 StartZ=0 EndX=-90 EndY=10.4 EndZ=0
    g9: LineSegment StartX=-90 StartY=10.4 StartZ=0 EndX=-97.94 EndY=10.4 EndZ=0
    g10: ArcOfCircle CenterX=-103.94 CenterY=7.4 CenterZ=0 NormalX=0 NormalY=0 NormalZ=1 AngleXU=0 Radius=3 StartAngle=1.5708 EndAngle=4.20173
    g11: LineSegment [constr] StartX=-97.1569 StartY=3.6 StartZ=0 EndX=-98.6232 EndY=0.982725 EndZ=0
  constraints (35):
    c: Horizontal(g2)
    c: Coincident(g4,g3)
    c: Horizontal(g4)
    c: Coincident(g5,g0)
    c: Coincident(g6,g5)
    c: Coincident(g6,g4)
    c: Coincident(g7,g2)
    c: Horizontal(g7)
    c: Coincident(g8,g7)
    c: Coincident(g9,g8)
    c: Coincident(g9,g1)
    c: Coincident(g3,g2)
    c: Horizontal(g9)
    c: Horizontal(g1)
    c: Horizontal(g5)
    c: Vertical(g6)
    c: Vertical(g8)
    c: Tangent(g0,g10) = 1.5708
    c: Tangent(g10,g1) = 1.5708
    c: DistanceY(g8,g8) = 3
    c: Parallel(g3,g0)
    c: DistanceY(g6,g6) = 3
    c: PointOnObject(g11,g0)
    c: Perpendicular(g3,g11)
    c: Distance(g11) = 3
    c: Vertical(g2,g1)
    c: Radius(g10) = 3
    c: Equal(g7,g5)
    c: Coincident(g11,g3)
    c: DistanceX(g8,g-1) = 90
    c: Vertical(g7,g4)
    c: DistanceX(g0,g5) = 7.94
    c: DistanceY(g5,g8) = 9.8
    c: DistanceY(g-1,g5) = 0.6
    c: DistanceX(g1,g1) = 6
FEATURE [PartDesign::Pad] Pad035
  AddSubType = 0
  AlongSketchNormal = false
  CheckUpToFaceLimits = true
  ClaimChildren = false
  Direction = (1,-2e-16,3e-16)
  Fit = 0
  FitJoin = 0
  InnerFit = 0
  InnerFitJoin = 0
  InnerTaperAngle = 0
  InnerTaperAngleRev = 0
  Length = 3
  Length2 = 100
  Linearize = true
  Midplane = true
  NewSolid = false
  Placement = pos=(0,0,0) rot=(0.57735,0.57735,0.57735;2.0944rad)
  Profile = -> Sketch127
  Suppress = false
  TreeRank = 2195
  Type = 0
  _ProfileBasedVersion = 1
FEATURE [Part::SubShapeBinder] Import046  label="Import046(Sketch)"
  BindCopyOnChange = 0
  BindMode = 0
  ClaimChildren = false
  Context = -> Part [Part009.Body088.Import046.]
  FillStyle = 0
  Fuse = false
  MakeFace = false
  OffsetFill = false
  OffsetIntersection = false
  OffsetJoinType = 0
  OffsetOpenResult = false
  PartialLoad = false
  Relative = true
  Support = -> [Body[Sketch.]]
  TreeRank = 2223
  _Version = 8
FEATURE [Sketcher::SketchObject] Sketch128
  ArcFitTolerance = 1e-06
  AttachmentSupport = -> [XY_Plane096]
  ExternalGeometry = -> [Import046]
  FullyConstrained = true
  MapMode = 5
  Support = -> [XY_Plane096]
  TreeRank = 2222
  sketch-geometry (2):
    g0: Circle CenterX=2.9 CenterY=-83.4417 CenterZ=0 NormalX=0 NormalY=0 NormalZ=1 AngleXU=0 Radius=3
    g1: Circle CenterX=-2.9 CenterY=-83.4417 CenterZ=0 NormalX=0 NormalY=0 NormalZ=1 AngleXU=0 Radius=3
  constraints (5):
    c: Symmetric(g0,g1,g-2)
    c: DistanceX(g-1,g0) = 2.9
    c: Radius(g0) = 3
    c: Radius(g1) = 3
    c: DistanceY(g-3,g0) = 14.5
FEATURE [PartDesign::Pad] Pad036
  AddSubType = 0
  AlongSketchNormal = false
  CheckUpToFaceLimits = true
  ClaimChildren = false
  Direction = (0,0,1)
  Fit = 0
  FitJoin = 0
  InnerFit = 0
  InnerFitJoin = 0
  InnerTaperAngle = 0
  InnerTaperAngleRev = 0
  Length = 10
  Length2 = 100
  Linearize = true
  Midplane = true
  NewSolid = false
  Profile = -> Sketch128
  Reversed = true
  Suppress = false
  TreeRank = 2224
  Type = 0
  _ProfileBasedVersion = 1
FEATURE [PartDesign::Body] Body088  label="tail stud"
  AutoGroupSolids = false
  ClaimAllChildren = false
  ExportMode = 0
  Group = -> [Sketch128,Import046,Pad036]
  Origin = -> Origin104
  Tip = -> Pad036
  TreeRank = 2221
  _ExportChildren = -> [Import046,Pad036]
  _GroupVersion = 1
FEATURE [PartDesign::FeatureBase] Clone037
  BaseFeature = -> Body042
  NewSolid = false
  Suppress = false
  TreeRank = 2294
FEATURE [PartDesign::Body] Body089  label="top with pocket"
  AutoGroupSolids = false
  BaseFeature = -> Body042
  ClaimAllChildren = false
  ExportMode = 0
  Group = -> [Clone037]
  Origin = -> Origin108
  Tip = -> Clone037
  TreeRank = 2296
  _ExportChildren = -> [Clone037]
  _GroupVersion = 1
FEATURE [Sketcher::SketchObject] Sketch129
  ArcFitTolerance = 1e-06
  AttachmentSupport = -> [Pad030]
  ExternalGeometry = -> [Pad030]
  FullyConstrained = true
  MapMode = 5
  Placement = pos=(0,0,-6) rot=(1,0,0;3.14159rad)
  Support = -> [Pad030]
  TreeRank = 2379
  sketch-geometry (4):
    g0: LineSegment StartX=-34 StartY=-3 StartZ=0 EndX=-18 EndY=-3 EndZ=0
    g1: LineSegment StartX=-18 StartY=-3 StartZ=0 EndX=-18 EndY=-11 EndZ=0
    g2: LineSegment StartX=-18 StartY=-11 StartZ=0 EndX=-34 EndY=-11 EndZ=0
    g3: LineSegment StartX=-34 StartY=-11 StartZ=0 EndX=-34 EndY=-3 EndZ=0
  constraints (11):
    c: Coincident(g0,g1)
    c: Coincident(g1,g2)
    c: Coincident(g2,g3)
    c: Coincident(g3,g0)
    c: Horizontal(g0)
    c: Horizontal(g2)
    c: Vertical(g1)
    c: Vertical(g3)
    c: Coincident(g0,g-3)
    c: PointOnObject(g1,g-4)
    c: DistanceX(g0,g-3) = 4
FEATURE [PartDesign::Pocket] Pocket011
  AddSubType = 1
  BaseFeature = -> Pad030
  CheckUpToFaceLimits = true
  ClaimChildren = false
  Fit = 0
  FitJoin = 0
  InnerFit = 0
  InnerFitJoin = 0
  InnerTaperAngle = 0
  InnerTaperAngleRev = 0
  Length = 6
  Length2 = 100
  Linearize = true
  NewSolid = false
  Profile = -> Sketch129
  Suppress = false
  TreeRank = 2389
  Type = 0
  _ProfileBasedVersion = 1
  _Version = 1
FEATURE [PartDesign::Mirrored] Mirrored005
  AddSubType = 0
  CopyShape = false
  MirrorPlane = -> YZ_Plane080
  NewSolid = false
  ParallelTransform = true
  SubTransform = true
  Suppress = false
  TreeRank = 2397
  _Version = 3
FEATURE [PartDesign::LinearPattern] LinearPattern004
  AddSubType = 0
  CopyShape = false
  Direction = -> Y_Axis080
  Length = 58
  NewSolid = false
  Occurrences = 2
  ParallelTransform = true
  Reversed = true
  SubTransform = true
  Suppress = false
  TreeRank = 2398
  _Version = 3
  expr: Length = Spreadsheet.side_bar_len
FEATURE [Sketcher::SketchObject] Sketch130
  ArcFitTolerance = 1e-06
  AttachmentSupport = -> [YZ_Plane088]
  ExternalGeometry = -> [Chamfer003,Sketch005]
  FullyConstrained = true
  MapMode = 5
  Placement = pos=(0,0,0) rot=(0.57735,0.57735,0.57735;2.0944rad)
  Support = -> [YZ_Plane088]
  TreeRank = 2842
  sketch-geometry (7):
    g0: ArcOfCircle [constr] CenterX=24.6 CenterY=-8.187e-13 CenterZ=0 NormalX=0 NormalY=0 NormalZ=1 AngleXU=0 Radius=20 StartAngle=4.71239 EndAngle=6.28319
    g1: LineSegment [constr] StartX=44.591 StartY=-0.6 StartZ=0 EndX=41.8016 EndY=-10.2031 EndZ=0
    g2: LineSegment StartX=45.1169 StartY=-5.95942 StartZ=0 EndX=54.72 EndY=-8.74877 EndZ=0
    g3: LineSegment [constr] StartX=43.1963 StartY=-5.40155 StartZ=0 EndX=45.1169 EndY=-5.95942 EndZ=0
    g4: LineSegment [constr] StartX=41.7009 StartY=-10.3711 StartZ=0 EndX=37.0795 EndY=-15.6289 EndZ=0
    g5: LineSegment StartX=39.3902 StartY=-13 StartZ=0 EndX=40.1413 EndY=-13.6602 EndZ=0
    g6: LineSegment StartX=24.6 StartY=-8.187e-13 StartZ=0 EndX=37.8038 EndY=15.022 EndZ=0
  constraints (23):
    c: Coincident(g0,g-4)
    c: Coincident(g0,g-3)
    c: PointOnObject(g0,g-1)
    c: PointOnObject(g1,g0)
    c: PointOnObject(g1,g0)
    c: DistanceY(g1,g0) = 0.6
    c: Distance(g1) = 10
    c: Perpendicular(g1,g2)
    c: Distance(g2) = 10
    c: Coincident(g3,g2)
    c: Parallel(g3,g2)
    c: Distance(g3) = 2
    c: PointOnObject(g4,g0)
    c: PointOnObject(g4,g0)
    c: Perpendicular(g4,g5)
    c: Symmetric(g4,g4,g5)
    c: DistanceY(g5,g0) = 13
    c: Distance(g5) = 1
    c: Distance(g4) = 7
    c: Symmetric(g1,g1,g3)
    c: Coincident(g6,g-4)
    c: Parallel(g4,g6)
    c: Distance(g6) = 20
FEATURE [PartDesign::Plane] DatumPlane039
  AttachmentSupport = -> [Sketch130]
  Length = 10
  MapMode = 7
  MinimumLength = 10
  MinimumWidth = 10
  Placement = pos=(1.13e-14,45.1169,-5.95942) rot=(1,0,0;1.28811rad)
  ResizeMode = 0
  Support = -> [Sketch130]
  TreeRank = 2408
  Width = 10
FEATURE [Sketcher::SketchObject] Sketch131
  ArcFitTolerance = 1e-06
  AttachmentSupport = -> [DatumPlane039]
  FullyConstrained = true
  MapMode = 5
  Placement = pos=(1.13e-14,45.1169,-5.95942) rot=(1,0,0;1.28811rad)
  Support = -> [DatumPlane039]
  TreeRank = 2409
  sketch-geometry (2):
    g0: Circle CenterX=0 CenterY=0 CenterZ=0 NormalX=0 NormalY=0 NormalZ=1 AngleXU=0 Radius=5
    g1: Circle CenterX=0 CenterY=0 CenterZ=0 NormalX=0 NormalY=0 NormalZ=1 AngleXU=0 Radius=4
  constraints (4):
    c: Coincident(g0,g-1)
    c: Coincident(g1,g0)
    c: Radius(g0) = 5
    c: Radius(g1) = 4
FEATURE [PartDesign::SubShapeBinder] Binder022  label="Binder022(Sketch131)"
  BindCopyOnChange = 0
  BindMode = 0
  ClaimChildren = false
  Context = -> Part008 [Body080.Binder022.]
  FillStyle = 0
  Fuse = false
  MakeFace = true
  OffsetFill = false
  OffsetIntersection = false
  OffsetJoinType = 0
  OffsetOpenResult = false
  PartialLoad = false
  Relative = true
  Support = -> [Sketch131[Edge1]]
  TreeRank = 2411
  _Version = 8
FEATURE [PartDesign::Pad] Pad037  label="Pad037 headlight"
  AddSubType = 0
  AlongSketchNormal = false
  BaseFeature = -> Chamfer003
  CheckUpToFaceLimits = true
  ClaimChildren = false
  Direction = (-1e-16,0.96031,-0.278935)
  Fit = 0
  FitJoin = 0
  InnerFit = 0
  InnerFitJoin = 0
  InnerTaperAngle = 0
  InnerTaperAngleRev = 0
  Length = 7
  Length2 = 100
  Linearize = true
  NewSolid = false
  Placement = pos=(0,17,0) rot=(1,0,0;1.5708rad)
  Profile = -> Binder022
  Reversed = true
  Suppress = false
  TreeRank = 2843
  Type = 0
  _ProfileBasedVersion = 1
FEATURE [Sketcher::SketchObject] Sketch132
  ArcFitTolerance = 1e-06
  AttachmentSupport = -> [Pad037]
  ExternalGeometry = -> [Pad037]
  FullyConstrained = true
  MapMode = 5
  Placement = pos=(-1.4e-15,37.8035,-6.04264) rot=(1,0,0;1.28811rad)
  Support = -> [Pad037]
  TreeRank = 2844
  sketch-geometry (2):
    g0: Circle CenterX=0 CenterY=2.1199 CenterZ=0 NormalX=0 NormalY=0 NormalZ=1 AngleXU=0 Radius=4.5
    g1: Circle CenterX=0 CenterY=2.1199 CenterZ=0 NormalX=0 NormalY=0 NormalZ=1 AngleXU=0 Radius=5.5
  constraints (4):
    c: Coincident(g0,g-3)
    c: Diameter(g0) = 9
    c: Coincident(g1,g0)
    c: Diameter(g1) = 11
FEATURE [PartDesign::Plane] DatumPlane040
  AttachmentSupport = -> [Sketch130]
  Length = 10
  MapMode = 7
  MinimumLength = 10
  MinimumWidth = 10
  Placement = pos=(1.19e-14,40.1413,-13.6602) rot=(1,0,0;0.849728rad)
  ResizeMode = 0
  Support = -> [Sketch130]
  TreeRank = 2423
  Width = 16.2406
FEATURE [PartDesign::SubShapeBinder] Binder026  label="Binder026(Sketch133)"
  BindCopyOnChange = 0
  BindMode = 0
  ClaimChildren = false
  Context = -> Part008 [Body080.Binder026.]
  FillStyle = 0
  Fuse = false
  MakeFace = true
  OffsetFill = false
  OffsetIntersection = false
  OffsetJoinType = 0
  OffsetOpenResult = false
  PartialLoad = false
  Relative = true
  Support = -> [Sketch133[Edge2]]
  TreeRank = 2426
  _Version = 8
FEATURE [PartDesign::SubShapeBinder] Binder027  label="Binder027(Sketch133)"
  BindCopyOnChange = 0
  BindMode = 0
  ClaimChildren = false
  Context = -> Part008 [Body080.Binder027.]
  FillStyle = 0
  Fuse = false
  MakeFace = true
  OffsetFill = false
  OffsetIntersection = false
  OffsetJoinType = 0
  OffsetOpenResult = false
  PartialLoad = false
  Relative = true
  Support = -> [Sketch133[Edge1]]
  TreeRank = 2429
  _Version = 8
FEATURE [PartDesign::Line] DatumLine009
  AttacherType = Attacher::AttachEngineLine
  AttachmentSupport = -> [Sketch130]
  Length = 10
  MapMode = 29
  MinimumLength = 10
  Placement = pos=(5.8e-15,13.8781,-12.1983) rot=(0,0.352774,0.935708;3.14159rad)
  ResizeMode = 0
  Support = -> [Sketch130]
  TreeRank = 2848
FEATURE [PartDesign::Plane] DatumPlane041
  AttachmentSupport = -> [Sketch130]
  Length = 10
  MapMode = 7
  MinimumLength = 10
  MinimumWidth = 10
  Placement = pos=(5.5e-15,24.6,-8.225e-13) rot=(1,0,0;2.42052rad)
  ResizeMode = 0
  Support = -> [Sketch130]
  TreeRank = 2433
  Width = 18.4771
FEATURE [Sketcher::SketchObject] Sketch134
  ArcFitTolerance = 1e-06
  AttachmentSupport = -> [DatumPlane041]
  FullyConstrained = true
  MapMode = 5
  Placement = pos=(5.5e-15,24.6,-8.242e-13) rot=(1,0,0;2.42052rad)
  Support = -> [DatumPlane041]
  TreeRank = 2434
  sketch-geometry (2):
    g0: LineSegment [constr] StartX=0 StartY=0 StartZ=0 EndX=0 EndY=-30 EndZ=0
    g1: LineSegment StartX=0 StartY=0 StartZ=0 EndX=7.18242 EndY=-19.7335 EndZ=0
  constraints (6):
    c: Coincident(g0,g-1)
    c: Vertical(g0)
    c: Coincident(g1,g0)
    c: DistanceY(g0,g0) = 30
    c: Angle(g0,g1) = 0.349066
    c: Distance(g1) = 21
FEATURE [PartDesign::Plane] DatumPlane042
  AttachmentSupport = -> [Sketch134]
  Length = 10.7276
  MapMode = 7
  MinimumLength = 10
  MinimumWidth = 10
  Placement = pos=(7.18242,39.4219,-13.0278) rot=(0.884731,-0.203069,-0.41954;1.00121rad)
  ResizeMode = 0
  Support = -> [Sketch134]
  TreeRank = 2435
  Width = 13.7337
FEATURE [Sketcher::SketchObject] Sketch133
  ArcFitTolerance = 1e-06
  AttachmentSupport = -> [DatumPlane042]
  FullyConstrained = true
  MapMode = 5
  Placement = pos=(7.18242,39.4219,-13.0278) rot=(0.884731,-0.203069,-0.41954;1.00121rad)
  Support = -> [DatumPlane042]
  TreeRank = 2424
  sketch-geometry (2):
    g0: Circle CenterX=0 CenterY=0 CenterZ=0 NormalX=0 NormalY=0 NormalZ=1 AngleXU=0 Radius=2.5
    g1: Circle CenterX=0 CenterY=0 CenterZ=0 NormalX=0 NormalY=0 NormalZ=1 AngleXU=0 Radius=3.5
  constraints (4):
    c: Coincident(g0,g-1)
    c: Coincident(g1,g0)
    c: Diameter(g0) = 5
    c: Diameter(g1) = 7
FEATURE [PartDesign::SubShapeBinder] Binder028  label="Binder028(Sketch131)"
  BindCopyOnChange = 0
  BindMode = 0
  ClaimChildren = false
  Context = -> Part008 [Body080.Binder028.]
  FillStyle = 0
  Fuse = false
  MakeFace = true
  OffsetFill = false
  OffsetIntersection = false
  OffsetJoinType = 0
  OffsetOpenResult = false
  PartialLoad = false
  Relative = true
  Support = -> [Sketch131[Edge2]]
  TreeRank = 2437
  _Version = 8
FEATURE [PartDesign::Pocket] Pocket017  label="Pocket017 headlight hole"
  AddSubType = 1
  BaseFeature = -> Pad037
  CheckUpToFaceLimits = true
  ClaimChildren = false
  Fit = 0
  FitJoin = 0
  InnerFit = 0
  InnerFitJoin = 0
  InnerTaperAngle = 0
  InnerTaperAngleRev = 0
  Length = 7
  Length2 = 100
  Linearize = true
  NewSolid = false
  Placement = pos=(0,17,0) rot=(1,0,0;1.5708rad)
  Profile = -> Binder028
  Suppress = false
  TreeRank = 2845
  Type = 0
  _ProfileBasedVersion = 1
  _Version = 1
FEATURE [PartDesign::Pad] Pad039  label="Pad039 sidelight"
  AddSubType = 0
  AlongSketchNormal = false
  BaseFeature = -> Pocket017
  CheckUpToFaceLimits = true
  ClaimChildren = false
  Direction = (0.34202,0.705804,-0.620374)
  Fit = 0
  FitJoin = 0
  InnerFit = 0
  InnerFitJoin = 0
  InnerTaperAngle = 0
  InnerTaperAngleRev = 0
  Length = 4.25
  Length2 = 100
  Linearize = true
  NewSolid = false
  Placement = pos=(0,17,0) rot=(1,0,0;1.5708rad)
  Profile = -> Binder026
  Reversed = true
  Suppress = false
  TreeRank = 2846
  Type = 0
  _ProfileBasedVersion = 1
FEATURE [PartDesign::Pocket] Pocket016  label="Pocket016 sidelight hole"
  AddSubType = 1
  BaseFeature = -> Pad039
  CheckUpToFaceLimits = true
  ClaimChildren = false
  Fit = 0
  FitJoin = 0
  InnerFit = 0
  InnerFitJoin = 0
  InnerTaperAngle = 0
  InnerTaperAngleRev = 0
  Length = 5.25
  Length2 = 100
  Linearize = true
  NewSolid = false
  Placement = pos=(0,17,0) rot=(1,0,0;1.5708rad)
  Profile = -> Binder027
  Suppress = false
  TreeRank = 2847
  Type = 0
  _ProfileBasedVersion = 1
  _Version = 1
FEATURE [PartDesign::PolarPattern] PolarPattern
  AddSubType = 0
  Angle = 40
  Axis = -> DatumLine009
  BaseFeature = -> Pocket016
  CopyShape = false
  NewSolid = false
  Occurrences = 2
  OriginalSubs = -> [Pocket016,Pad039]
  Originals = -> [Pocket016,Pad039]
  ParallelTransform = true
  Placement = pos=(0,17,0) rot=(1,0,0;1.5708rad)
  SubTransform = true
  Suppress = false
  TreeRank = 2849
  _Version = 3
FEATURE [PartDesign::ShapeBinder] ShapeBinder032
  Support = -> [Sketch103]
  TraceSupport = false
  TreeRank = 2487
FEATURE [Sketcher::SketchObject] Sketch138
  ArcFitTolerance = 1e-06
  AttachmentSupport = -> [XY_Plane103]
  ExternalGeometry = -> [ShapeBinder032]
  FullyConstrained = true
  MapMode = 5
  Support = -> [XY_Plane103]
  TreeRank = 2650
  sketch-geometry (4):
    g0: LineSegment StartX=-11 StartY=11 StartZ=0 EndX=-34 EndY=11 EndZ=0
    g1: LineSegment StartX=-34 StartY=11 StartZ=0 EndX=-34 EndY=3 EndZ=0
    g2: LineSegment StartX=-34 StartY=3 StartZ=0 EndX=-11 EndY=3 EndZ=0
    g3: LineSegment StartX=-11 StartY=3 StartZ=0 EndX=-11 EndY=11 EndZ=0
  constraints (11):
    c: Coincident(g0,g1)
    c: Coincident(g1,g2)
    c: Coincident(g2,g3)
    c: Horizontal(g0)
    c: Horizontal(g2)
    c: Vertical(g1)
    c: Vertical(g3)
    c: Coincident(g3,g0)
    c: Coincident(g0,g-4)
    c: Horizontal(g2,g-3)
    c: DistanceX(g-4,g2) = 3
FEATURE [PartDesign::Pad] Pad040
  AddSubType = 0
  AlongSketchNormal = false
  CheckUpToFaceLimits = true
  ClaimChildren = false
  Direction = (0,0,1)
  Fit = 0
  FitJoin = 0
  InnerFit = 0
  InnerFitJoin = 0
  InnerTaperAngle = 0
  InnerTaperAngleRev = 0
  Length = 23
  Length2 = 100
  Linearize = true
  NewSolid = false
  Profile = -> Sketch138
  Reversed = true
  Suppress = false
  TreeRank = 2489
  Type = 0
  _ProfileBasedVersion = 1
FEATURE [Sketcher::SketchObject] Sketch140
  ArcFitTolerance = 1e-06
  AttachmentSupport = -> [Pad040]
  ExternalGeometry = -> [ShapeBinder032]
  FullyConstrained = true
  MapMode = 5
  Support = -> [Pad040]
  TreeRank = 2651
  sketch-geometry (4):
    g0: LineSegment StartX=-18 StartY=11 StartZ=0 EndX=-14 EndY=11 EndZ=0
    g1: LineSegment StartX=-14 StartY=11 StartZ=0 EndX=-14 EndY=3 EndZ=0
    g2: LineSegment StartX=-14 StartY=3 StartZ=0 EndX=-18 EndY=3 EndZ=0
    g3: LineSegment StartX=-18 StartY=3 StartZ=0 EndX=-18 EndY=11 EndZ=0
  constraints (11):
    c: Coincident(g0,g1)
    c: Coincident(g1,g2)
    c: Coincident(g2,g3)
    c: Coincident(g3,g0)
    c: Horizontal(g0)
    c: Horizontal(g2)
    c: Vertical(g1)
    c: Vertical(g3)
    c: Coincident(g0,g-4)
    c: DistanceX(g2,g2) = 4
    c: Horizontal(g2,g-3)
FEATURE [PartDesign::Pocket] Pocket018
  AddSubType = 1
  BaseFeature = -> Pad040
  CheckUpToFaceLimits = true
  ClaimChildren = false
  Fit = 0
  FitJoin = 0
  InnerFit = 0
  InnerFitJoin = 0
  InnerTaperAngle = 0
  InnerTaperAngleRev = 0
  Length = 6
  Length2 = 100
  Linearize = true
  NewSolid = false
  Profile = -> Sketch140
  Suppress = false
  TreeRank = 2492
  Type = 0
  _ProfileBasedVersion = 1
  _Version = 1
FEATURE [PartDesign::Mirrored] Mirrored006
  AddSubType = 0
  CopyShape = false
  MirrorPlane = -> YZ_Plane103
  NewSolid = false
  ParallelTransform = true
  SubTransform = true
  Suppress = false
  TreeRank = 2654
  _Version = 3
FEATURE [PartDesign::LinearPattern] LinearPattern005
  AddSubType = 0
  CopyShape = false
  Direction = -> Y_Axis103
  Length = 58
  NewSolid = false
  Occurrences = 2
  ParallelTransform = true
  Reversed = true
  SubTransform = true
  Suppress = false
  TreeRank = 2655
  _Version = 3
  expr: Length = Spreadsheet.side_bar_len
FEATURE [PartDesign::Plane] DatumPlane043
  AttachmentSupport = -> [Sketch002]
  Length = 17
  MapMode = 7
  MinimumLength = 10
  MinimumWidth = 10
  Placement = pos=(-35,17,0) rot=(0.57735,-0.57735,-0.57735;2.0944rad)
  ResizeMode = 0
  Support = -> [Sketch002]
  TreeRank = 2501
  Width = 10
FEATURE [Sketcher::SketchObject] Sketch143
  ArcFitTolerance = 1e-06
  AttachmentSupport = -> [DatumPlane043]
  FullyConstrained = true
  MapMode = 5
  Placement = pos=(-35,17,0) rot=(0.57735,-0.57735,-0.57735;2.0944rad)
  Support = -> [DatumPlane043]
  TreeRank = 2502
  sketch-geometry (1):
    g0: LineSegment StartX=0 StartY=0 StartZ=0 EndX=4 EndY=0 EndZ=0
  constraints (3):
    c: Coincident(g0,g-1)
    c: PointOnObject(g0,g-1)
    c: DistanceX(g0,g0) = 4
FEATURE [PartDesign::Plane] DatumPlane044
  AttachmentSupport = -> [Sketch143]
  Length = 35
  MapMode = 7
  MinimumLength = 10
  MinimumWidth = 10
  Placement = pos=(-35,13,0) rot=(0,0.707107,0.707107;3.14159rad)
  ResizeMode = 0
  Support = -> [Sketch143]
  TreeRank = 2503
  Width = 10
FEATURE [Sketcher::SketchObject] Sketch144
  ArcFitTolerance = 1e-06
  AttachmentSupport = -> [DatumPlane044]
  ExternalGeometry = -> [Sketch002]
  FullyConstrained = true
  MapMode = 5
  Placement = pos=(-35,13,0) rot=(0,0.707107,0.707107;3.14159rad)
  Support = -> [DatumPlane044]
  TreeRank = 2850
  sketch-geometry (1):
    g0: ArcOfCircle CenterX=-35 CenterY=15.1304 CenterZ=0 NormalX=0 NormalY=0 NormalZ=1 AngleXU=0 Radius=38.1304 StartAngle=3.54963 EndAngle=5.87515
  constraints (3):
    c: Coincident(g0,g-3)
    c: Coincident(g0,g-3)
    c: Coincident(g0,g-3)
FEATURE [PartDesign::Plane] DatumPlane045
  AttachmentSupport = -> [Sketch144,Sketch143]
  Length = 13
  MapMode = 7
  MinimumLength = 10
  MinimumWidth = 10
  Placement = pos=(-35,13,1.78e-14) rot=(0.699659,0.699659,0.144757;2.85408rad)
  ResizeMode = 0
  Support = -> [Sketch144,Sketch143]
  TreeRank = 2505
  Width = 32.1266
FEATURE [Sketcher::SketchObject] Sketch145
  ArcFitTolerance = 1e-06
  AttachmentSupport = -> [DatumPlane045]
  FullyConstrained = true
  MapMode = 5
  Placement = pos=(-35,13,1.95e-14) rot=(0.699659,0.699659,0.144757;2.85408rad)
  Support = -> [DatumPlane045]
  TreeRank = 2508
  expr: Constraints[1] = Spreadsheet.groove_lift
  expr: Constraints[2] = Spreadsheet.groove_radius
  sketch-geometry (1):
    g0: Circle CenterX=0 CenterY=-0.3 CenterZ=0 NormalX=0 NormalY=0 NormalZ=1 AngleXU=0 Radius=0.7
  constraints (3):
    c: PointOnObject(g0,g-2)
    c: DistanceY(g0,g-1) = 0.3
    c: Radius(g0) = 0.7
FEATURE [Sketcher::SketchObject] Sketch146
  ArcFitTolerance = 1e-06
  AttachmentSupport = -> [DatumPlane045]
  FullyConstrained = true
  MapMode = 5
  Placement = pos=(-35,13,1.95e-14) rot=(0.699659,0.699659,0.144757;2.85408rad)
  Support = -> [DatumPlane045]
  TreeRank = 2507
  expr: Constraints[10] = Spreadsheet.bottom_shell_width
  sketch-geometry (4):
    g0: LineSegment StartX=2.5 StartY=1 StartZ=0 EndX=-2.5 EndY=1 EndZ=0
    g1: LineSegment StartX=-2.5 StartY=1 StartZ=0 EndX=-2.5 EndY=3 EndZ=0
    g2: LineSegment StartX=-2.5 StartY=3 StartZ=0 EndX=2.5 EndY=3 EndZ=0
    g3: LineSegment StartX=2.5 StartY=3 StartZ=0 EndX=2.5 EndY=1 EndZ=0
  constraints (11):
    c: Coincident(g0,g1)
    c: Coincident(g1,g2)
    c: Coincident(g2,g3)
    c: Coincident(g3,g0)
    c: Horizontal(g2)
    c: Vertical(g1)
    c: Vertical(g3)
    c: DistanceX(g2,g2) = 5
    c: DistanceY(g1,g1) = 2
    c: Symmetric(g0,g0,g-2)
    c: DistanceY(g-1,g0) = 1
FEATURE [Sketcher::SketchObject] Sketch147
  ArcFitTolerance = 1e-06
  AttachmentSupport = -> [XZ_Plane088]
  ExternalGeometry = -> [Sketch144]
  FullyConstrained = true
  MapMode = 5
  Placement = pos=(0,0,0) rot=(1,0,0;1.5708rad)
  Support = -> [XZ_Plane088]
  TreeRank = 2851
  sketch-geometry (6):
    g0: LineSegment StartX=0 StartY=15.1304 StartZ=0 EndX=0 EndY=25.1304 EndZ=0
    g1: LineSegment StartX=0 StartY=15.1304 StartZ=0 EndX=-35 EndY=0 EndZ=0
    g2: LineSegment StartX=0 StartY=15.1304 StartZ=0 EndX=35 EndY=0 EndZ=0
    g3: LineSegment StartX=0 StartY=15.1304 StartZ=0 EndX=-33.5443 EndY=-3 EndZ=0
    g4: LineSegment StartX=0 StartY=15.1304 StartZ=0 EndX=33.5443 EndY=-3 EndZ=0
    g5: LineSegment StartX=-33.5443 StartY=-3 StartZ=0 EndX=-38.2991 EndY=5.79724 EndZ=0
  constraints (16):
    c: Coincident(g0,g-3)
    c: PointOnObject(g0,g-2)
    c: DistanceY(g0,g0) = 10
    c: Coincident(g1,g0)
    c: Coincident(g1,g-3)
    c: Coincident(g2,g0)
    c: Coincident(g2,g-3)
    c: Coincident(g3,g0)
    c: PointOnObject(g3,g-3)
    c: DistanceY(g3,g-1) = 3
    c: Coincident(g4,g0)
    c: PointOnObject(g4,g-3)
    c: Horizontal(g4,g3)
    c: Coincident(g5,g3)
    c: Distance(g5) = 10
    c: Perpendicular(g3,g5)
FEATURE [Sketcher::SketchObject] Sketch148
  ArcFitTolerance = 1e-06
  AttachmentSupport = -> [YZ_Plane088]
  ExternalGeometry = -> [Sketch147]
  FullyConstrained = true
  MapMode = 5
  Placement = pos=(0,0,0) rot=(0.57735,0.57735,0.57735;2.0944rad)
  Support = -> [YZ_Plane088]
  TreeRank = 2852
  sketch-geometry (1):
    g0: LineSegment StartX=-6.8e-15 StartY=15.1304 StartZ=0 EndX=-50 EndY=15.1304 EndZ=0
  constraints (3):
    c: Coincident(g0,g-3)
    c: Horizontal(g0)
    c: DistanceX(g0,g0) = 50
FEATURE [PartDesign::Line] DatumLine010
  AttacherType = Attacher::AttachEngineLine
  AttachmentSupport = -> [Sketch148]
  Length = 10
  MapMode = 29
  MinimumLength = 10
  Placement = pos=(-3.4e-15,3.2e-15,15.1304) rot=(1,0,0;1.5708rad)
  ResizeMode = 0
  Support = -> [Sketch148]
  TreeRank = 2853
FEATURE [PartDesign::Groove] Groove001  label="groove"
  AddSubType = 1
  Angle = 360
  Axis = (-2e-16,-1,2e-16)
  Base = (-3.4e-15,3.2e-15,15.1304)
  BaseFeature = -> PolarPattern
  ClaimChildren = false
  Fit = 0
  FitJoin = 0
  InnerFit = 0
  InnerFitJoin = 0
  Linearize = true
  NewSolid = false
  Placement = pos=(0,17,0) rot=(1,0,0;1.5708rad)
  Profile = -> Sketch145
  ReferenceAxis = -> DatumLine010
  Suppress = false
  TreeRank = 2854
  _ProfileBasedVersion = 1
FEATURE [PartDesign::Revolution] Revolution008  label="groove support001"
  AddSubType = 0
  Angle = 133.24
  Axis = (-2e-16,-1,2e-16)
  Base = (-3.4e-15,3.2e-15,15.1304)
  BaseFeature = -> Groove001
  ClaimChildren = false
  Fit = 0
  FitJoin = 0
  InnerFit = 0
  InnerFitJoin = 0
  Linearize = true
  NewSolid = false
  Placement = pos=(0,17,0) rot=(1,0,0;1.5708rad)
  Profile = -> Sketch146
  ReferenceAxis = -> DatumLine010
  Suppress = false
  TreeRank = 2855
  _ProfileBasedVersion = 1
  expr: Angle = Spreadsheet.bottom_groove_revolve_angle
FEATURE [PartDesign::Fillet] Fillet017
  AddSubType = 0
  Base = -> Revolution008 [Face40]
  BaseFeature = -> Revolution008
  NewSolid = false
  Placement = pos=(0,17,0) rot=(1,0,0;1.5708rad)
  Radius = 1.9
  SupportTransform = false
  Suppress = false
  TreeRank = 2856
FEATURE [PartDesign::LinearPattern] LinearPattern006  label="copy grooves"
  AddSubType = 0
  BaseFeature = -> Fillet017
  CopyShape = false
  Direction = -> Y_Axis088
  Length = 64
  NewSolid = false
  Occurrences = 3
  OriginalSubs = -> [Revolution008,Groove001,Fillet017]
  Originals = -> [Revolution008,Groove001,Fillet017]
  ParallelTransform = true
  Placement = pos=(0,17,0) rot=(1,0,0;1.5708rad)
  Reversed = true
  SubTransform = true
  Suppress = false
  TreeRank = 2857
  _Version = 3
  expr: Length = Spreadsheet.bottom_groove_len
FEATURE [PartDesign::Plane] DatumPlane046
  AttachmentSupport = -> [Sketch147]
  Length = 10
  MapMode = 7
  MinimumLength = 10
  MinimumWidth = 10
  Placement = pos=(-33.5443,7e-16,-3) rot=(0.69606,0.69606,0.176071;2.79302rad)
  ResizeMode = 0
  Support = -> [Sketch147]
  TreeRank = 2522
  Width = 38.1304
FEATURE [Sketcher::SketchObject] Sketch149
  ArcFitTolerance = 1e-06
  AttachmentSupport = -> [DatumPlane046]
  ExternalGeometry = -> [Sketch144]
  FullyConstrained = true
  MapMode = 5
  Placement = pos=(-33.5443,7e-16,-3) rot=(0.69606,0.69606,0.176071;2.79302rad)
  Support = -> [DatumPlane046]
  TreeRank = 2517
  sketch-geometry (8):
    g0: LineSegment StartX=15.4 StartY=0.8 StartZ=0 EndX=16.2 EndY=0.8 EndZ=0
    g1: LineSegment StartX=16.2 StartY=0.8 StartZ=0 EndX=16.2 EndY=2.84e-14 EndZ=0
    g2: LineSegment StartX=15.4 StartY=-0.5 StartZ=0 EndX=15.4 EndY=0.8 EndZ=0
    g3: ArcOfEllipse CenterX=15.4 CenterY=2.84e-14 CenterZ=0 NormalX=0 NormalY=0 NormalZ=1 MajorRadius=0.8 MinorRadius=0.5 AngleXU=-3.442e-13 StartAngle=4.71239 EndAngle=6.28319
    g4: LineSegment [constr] StartX=16.2 StartY=-2.745e-13 StartZ=0 EndX=14.6 EndY=3.313e-13 EndZ=0
    g5: LineSegment [constr] StartX=15.4 StartY=0.5 StartZ=0 EndX=15.4 EndY=-0.5 EndZ=0
    g6: GeomPoint [constr] X=16.0245 Y=-1.865e-13 Z=0
    g7: GeomPoint [constr] X=14.7755 Y=2.433e-13 Z=0
  constraints (15):
    c: Horizontal(g0)
    c: Coincident(g1,g0)
    c: Vertical(g1)
    c: Coincident(g2,g0)
    c: Vertical(g2)
    c: InternalAlignment(g4-g7 -> g3) x4
    c: PointOnObject(g3,g2)
    c: Horizontal(g1,g3)
    c: DistanceX(g3,g4) = 0.8
    c: DistanceY(g5,g3) = 0.5
    c: Coincident(g2,g3)
    c: Tangent(g3,g1) = 1.5708
    c: DistanceY(g1,g0) = 0.8
    c: DistanceX(g-3,g0) = 2.4
    c: Horizontal(g3,g-3)
FEATURE [PartDesign::Line] DatumLine011
  AttacherType = Attacher::AttachEngineLine
  AttachmentSupport = -> [Sketch149]
  Length = 30.9361
  MapMode = 29
  MinimumLength = 10
  Placement = pos=(-33.5443,15.4,-3) rot=(0.455817,0.455817,0.764501;1.83616rad)
  ResizeMode = 0
  Support = -> [Sketch149]
  TreeRank = 2858
FEATURE [PartDesign::Revolution] Revolution009  label="bump"
  AddSubType = 0
  Angle = 360
  Axis = (0.879724,0,0.475485)
  Base = (-33.5443,15.4,-3)
  BaseFeature = -> LinearPattern006
  ClaimChildren = false
  Fit = 0
  FitJoin = 0
  InnerFit = 0
  InnerFitJoin = 0
  Linearize = true
  NewSolid = false
  Placement = pos=(0,17,0) rot=(1,0,0;1.5708rad)
  Profile = -> Sketch149
  ReferenceAxis = -> DatumLine011
  Reversed = true
  Suppress = false
  TreeRank = 2859
  _ProfileBasedVersion = 1
FEATURE [PartDesign::LinearPattern] LinearPattern010
  AddSubType = 0
  CopyShape = false
  Direction = -> Y_Axis088
  Length = 23
  NewSolid = false
  Occurrences = 2
  ParallelTransform = true
  Placement = pos=(0,17,0) rot=(1,0,0;1.5708rad)
  Reversed = true
  SubTransform = true
  Suppress = false
  TreeRank = 2564
  _Version = 3
FEATURE [PartDesign::PolarPattern] PolarPattern004
  AddSubType = 0
  Angle = 123.22
  Axis = -> DatumLine010
  CopyShape = false
  NewSolid = false
  Occurrences = 2
  ParallelTransform = true
  Placement = pos=(0,17,0) rot=(1,0,0;1.5708rad)
  SubTransform = true
  Suppress = false
  TreeRank = 2565
  _Version = 3
  expr: Angle = Spreadsheet.bottom_bump_polar_angle
FEATURE [PartDesign::LinearPattern] LinearPattern009
  AddSubType = 0
  CopyShape = false
  Direction = -> Y_Axis088
  Length = 13
  NewSolid = false
  Occurrences = 2
  ParallelTransform = true
  Placement = pos=(0,17,0) rot=(1,0,0;1.5708rad)
  Reversed = true
  SubTransform = true
  Suppress = false
  TreeRank = 2566
  _Version = 3
FEATURE [PartDesign::PolarPattern] PolarPattern003
  AddSubType = 0
  Angle = 123.22
  Axis = -> DatumLine010
  CopyShape = false
  NewSolid = false
  Occurrences = 2
  ParallelTransform = true
  Placement = pos=(0,17,0) rot=(1,0,0;1.5708rad)
  SubTransform = true
  Suppress = false
  TreeRank = 2567
  _Version = 3
  expr: Angle = Spreadsheet.bottom_bump_polar_angle
FEATURE [PartDesign::MultiTransform] MultiTransform006
  AddSubType = 0
  BaseFeature = -> Revolution009
  CopyShape = false
  NewSolid = false
  OriginalSubs = -> [Revolution009]
  Originals = -> [Revolution009]
  ParallelTransform = true
  Placement = pos=(0,17,0) rot=(1,0,0;1.5708rad)
  SubTransform = true
  Suppress = false
  Transformations = -> [LinearPattern010,PolarPattern004]
  TreeRank = 2860
  _Version = 3
FEATURE [PartDesign::MultiTransform] MultiTransform005
  AddSubType = 0
  BaseFeature = -> MultiTransform006
  CopyShape = false
  NewSolid = false
  OriginalSubs = -> [Revolution009]
  Originals = -> [Revolution009]
  ParallelTransform = true
  Placement = pos=(0,17,0) rot=(1,0,0;1.5708rad)
  SubTransform = true
  Suppress = false
  Transformations = -> [LinearPattern009,PolarPattern003]
  TreeRank = 2861
  _Version = 3
FEATURE [PartDesign::LinearPattern] LinearPattern011
  AddSubType = 0
  CopyShape = false
  Direction = -> Y_Axis088
  Length = 4.8
  NewSolid = false
  Occurrences = 2
  ParallelTransform = true
  Placement = pos=(0,17,0) rot=(1,0,0;1.5708rad)
  Reversed = true
  SubTransform = true
  Suppress = false
  TreeRank = 2571
  _Version = 3
FEATURE [PartDesign::PolarPattern] PolarPattern005
  AddSubType = 0
  Angle = 123.22
  Axis = -> DatumLine010
  CopyShape = false
  NewSolid = false
  Occurrences = 10
  ParallelTransform = true
  Placement = pos=(0,17,0) rot=(1,0,0;1.5708rad)
  SubTransform = true
  Suppress = false
  TreeRank = 2572
  _Version = 3
  expr: Angle = Spreadsheet.bottom_bump_polar_angle
FEATURE [PartDesign::MultiTransform] MultiTransform007
  AddSubType = 0
  BaseFeature = -> MultiTransform005
  CopyShape = false
  NewSolid = false
  OriginalSubs = -> [Revolution009]
  Originals = -> [Revolution009]
  ParallelTransform = true
  Placement = pos=(0,17,0) rot=(1,0,0;1.5708rad)
  SubTransform = true
  Suppress = false
  Transformations = -> [LinearPattern011,PolarPattern005]
  TreeRank = 2862
  _Version = 3
FEATURE [PartDesign::LinearPattern] LinearPattern012
  AddSubType = 0
  CopyShape = false
  Direction = -> Y_Axis088
  Length = 31.8
  NewSolid = false
  Occurrences = 2
  ParallelTransform = true
  Placement = pos=(0,17,0) rot=(1,0,0;1.5708rad)
  Reversed = true
  SubTransform = true
  Suppress = false
  TreeRank = 2574
  _Version = 3
FEATURE [PartDesign::PolarPattern] PolarPattern006
  AddSubType = 0
  Angle = 123.22
  Axis = -> DatumLine010
  CopyShape = false
  NewSolid = false
  Occurrences = 10
  ParallelTransform = true
  Placement = pos=(0,17,0) rot=(1,0,0;1.5708rad)
  SubTransform = true
  Suppress = false
  TreeRank = 2575
  _Version = 3
  expr: Angle = Spreadsheet.bottom_bump_polar_angle
FEATURE [PartDesign::MultiTransform] MultiTransform008
  AddSubType = 0
  BaseFeature = -> MultiTransform007
  CopyShape = false
  NewSolid = false
  OriginalSubs = -> [Revolution009]
  Originals = -> [Revolution009]
  ParallelTransform = true
  Placement = pos=(0,17,0) rot=(1,0,0;1.5708rad)
  SubTransform = true
  Suppress = false
  Transformations = -> [LinearPattern012,PolarPattern006]
  TreeRank = 2863
  _Version = 3
FEATURE [Sketcher::SketchObject] Sketch150
  ArcFitTolerance = 1e-06
  AttachmentSupport = -> [XY_Plane088]
  FullyConstrained = true
  MapMode = 5
  Support = -> [XY_Plane088]
  TreeRank = 2576
  sketch-geometry (4):
    g0: LineSegment StartX=-40 StartY=30 StartZ=0 EndX=40 EndY=30 EndZ=0
    g1: LineSegment StartX=40 StartY=30 StartZ=0 EndX=40 EndY=-70 EndZ=0
    g2: LineSegment StartX=40 StartY=-70 StartZ=0 EndX=-40 EndY=-70 EndZ=0
    g3: LineSegment StartX=-40 StartY=-70 StartZ=0 EndX=-40 EndY=30 EndZ=0
  constraints (11):
    c: Coincident(g0,g1)
    c: Coincident(g1,g2)
    c: Coincident(g2,g3)
    c: Coincident(g3,g0)
    c: Horizontal(g2)
    c: Vertical(g1)
    c: Vertical(g3)
    c: Symmetric(g0,g0,g-2)
    c: DistanceY(g-1,g0) = 30
    c: DistanceX(g2,g2) = 80
    c: DistanceY(g1,g1) = 100
FEATURE [PartDesign::Pocket] Pocket021
  AddSubType = 1
  BaseFeature = -> MultiTransform008
  CheckUpToFaceLimits = true
  ClaimChildren = false
  Fit = 0
  FitJoin = 0
  InnerFit = 0
  InnerFitJoin = 0
  InnerTaperAngle = 0
  InnerTaperAngleRev = 0
  Length = 5
  Length2 = 100
  Linearize = true
  NewSolid = false
  Placement = pos=(0,17,0) rot=(1,0,0;1.5708rad)
  Profile = -> Sketch150
  Reversed = true
  Suppress = false
  TreeRank = 2864
  Type = 0
  _ProfileBasedVersion = 1
  _Version = 1
FEATURE [Sketcher::SketchObject] Sketch151
  ArcFitTolerance = 1e-06
  AttachmentSupport = -> [XY_Plane104]
  ExternalGeometry = -> [Pocket021]
  FullyConstrained = true
  MapMode = 5
  Support = -> [XY_Plane104]
  TreeRank = 2679
  sketch-geometry (29):
    g0: ArcOfCircle CenterX=0 CenterY=24.6 CenterZ=0 NormalX=0 NormalY=0 NormalZ=1 AngleXU=0 Radius=18 StartAngle=1.91986 EndAngle=3.14159
    g1: LineSegment StartX=-18 StartY=23.235 StartZ=0 EndX=-33 EndY=15.635 EndZ=0
    g2: LineSegment [constr] StartX=-19.279 StartY=23.708 StartZ=0 EndX=-18.8271 EndY=22.8159 EndZ=0
    g3: ArcOfCircle CenterX=0 CenterY=24.6 CenterZ=0 NormalX=0 NormalY=0 NormalZ=1 AngleXU=0 Radius=19 StartAngle=1.91986 EndAngle=3.14159
    g4: LineSegment StartX=-18 StartY=24.6 StartZ=0 EndX=-18 EndY=23.235 EndZ=0
    g5: LineSegment StartX=-19.548 StartY=23.708 StartZ=0 EndX=-34 EndY=16.3856 EndZ=0
    g6: LineSegment StartX=-19.548 StartY=23.708 StartZ=0 EndX=-19 EndY=24.6 EndZ=0
    g7: LineSegment StartX=-6.15636 StartY=41.5145 StartZ=0 EndX=-6.49838 EndY=42.4542 EndZ=0
    g8: LineSegment [constr] StartX=-6.15636 StartY=41.5145 StartZ=0 EndX=0 EndY=24.6 EndZ=0
    g9: LineSegment [constr] StartX=0 StartY=24.6 StartZ=0 EndX=-18 EndY=24.6 EndZ=0
    g10: LineSegment StartX=-33 StartY=15.635 StartZ=0 EndX=-33 EndY=14.635 EndZ=0
    g11: LineSegment StartX=-33 StartY=14.635 StartZ=0 EndX=-34 EndY=14.635 EndZ=0
    g12: LineSegment StartX=-34 StartY=14.635 StartZ=0 EndX=-34 EndY=16.3856 EndZ=0
    g13: LineSegment StartX=-34 StartY=-24 StartZ=0 EndX=-33 EndY=-24 EndZ=0
    g14: LineSegment StartX=-33 StartY=-24 StartZ=0 EndX=-33 EndY=-46 EndZ=0
    g15: LineSegment StartX=-33 StartY=-46 StartZ=0 EndX=-34 EndY=-46 EndZ=0
    g16: LineSegment StartX=-34 StartY=-46 StartZ=0 EndX=-34 EndY=-24 EndZ=0
    g17: LineSegment StartX=-34 StartY=2 StartZ=0 EndX=-33 EndY=2 EndZ=0
    g18: LineSegment StartX=-33 StartY=2 StartZ=0 EndX=-33 EndY=-14 EndZ=0
    g19: LineSegment StartX=-33 StartY=-14 StartZ=0 EndX=-34 EndY=-14 EndZ=0
    g20: LineSegment StartX=-34 StartY=-14 StartZ=0 EndX=-34 EndY=2 EndZ=0
    g21: LineSegment StartX=-34 StartY=-55.6587 StartZ=0 EndX=-33 EndY=-55.6587 EndZ=0
    g22: LineSegment StartX=-33 StartY=-55.6587 StartZ=0 EndX=-33 EndY=-61.3218 EndZ=0
    g23: LineSegment StartX=-27.5016 StartY=-73.3931 StartZ=0 EndX=-21.059 EndY=-78.9979 EndZ=0
    g24: LineSegment StartX=-21.059 StartY=-78.9979 StartZ=0 EndX=-21.7153 EndY=-79.7524 EndZ=0
    g25: LineSegment StartX=-21.7153 StartY=-79.7524 StartZ=0 EndX=-28.5055 EndY=-73.8452 EndZ=0
    g26: ArcOfCircle CenterX=-18.0024 CenterY=-61.7722 CenterZ=0 NormalX=0 NormalY=0 NormalZ=1 AngleXU=0 Radius=16.0023 StartAngle=3.16575 EndAngle=3.99642
    g27: ArcOfCircle CenterX=-17 CenterY=-61.3218 CenterZ=0 NormalX=0 NormalY=0 NormalZ=1 AngleXU=0 Radius=16 StartAngle=3.14159 EndAngle=3.99642
    g28: LineSegment StartX=-34 StartY=-55.6587 StartZ=0 EndX=-34 EndY=-62.1587 EndZ=0
  constraints (79):
    c: Coincident(g0,g-17)
    c: Horizontal(g0,g-7)
    c: DistanceX(g-7,g0) = 1
    c: Parallel(g-5,g1)
    c: DistanceX(g-9,g1) = 1
    c: Coincident(g2,g-6)
    c: PointOnObject(g2,g1)
    c: Perpendicular(g1,g2)
    c: Distance(g2) = 1
    c: Coincident(g3,g0)
    c: Coincident(g3,g-7)
    c: Coincident(g4,g0)
    c: Coincident(g4,g1)
    c: Vertical(g4)
    c: Coincident(g5,g-5)
    c: Coincident(g6,g-5)
    c: Coincident(g7,g0)
    c: Coincident(g7,g3)
    c: Perpendicular(g0,g7)
    c: Coincident(g8,g0)
    c: Coincident(g8,g0)
    c: Coincident(g9,g0)
    c: Coincident(g9,g0)
    c: Angle(g8,g9) = 1.22173
    c: Coincident(g6,g3)
    c: Coincident(g10,g1)
    c: Coincident(g11,g10)
    c: PointOnObject(g11,g-9)
    c: Horizontal(g11)
    c: Coincident(g12,g11)
    c: Coincident(g12,g5)
    c: Vertical(g10)
    c: DistanceY(g10,g10) = 1
    c: Coincident(g-9,g5)
    c: Coincident(g13,g14)
    c: Coincident(g14,g15)
    c: Coincident(g15,g16)
    c: Coincident(g16,g13)
    c: Horizontal(g13)
    c: Horizontal(g15)
    c: Vertical(g14)
    c: Vertical(g16)
    c: PointOnObject(g13,g-9)
    c: Coincident(g17,g18)
    c: Coincident(g18,g19)
    c: Coincident(g19,g20)
    c: Coincident(g20,g17)
    c: Horizontal(g17)
    c: Horizontal(g19)
    c: Vertical(g18)
    c: Vertical(g20)
    c: PointOnObject(g17,g-9)
    c: DistanceY(g-1,g17) = 2
    c: DistanceY(g18,g18) = 16
    c: DistanceY(g13,g18) = 10
    c: DistanceY(g14,g14) = 22
    c: DistanceX(g15,g15) = 1
    c: DistanceX(g19,g19) = 1
    c: PointOnObject(g21,g-9)
    c: Horizontal(g21)
    c: Coincident(g22,g21)
    c: Vertical(g22)
    c: Coincident(g24,g23)
    c: PointOnObject(g24,g-18)
    c: Coincident(g25,g24)
    c: Coincident(g25,g-18)
    c: Coincident(g26,g-9)
    c: Tangent(g26,g25) = 1.5708
    c: DistanceX(g21,g21) = 1
    c: Perpendicular(g23,g24)
    c: Perpendicular(g25,g24)
    c: Distance(g24) = 1
    c: Tangent(g27,g22) = -1.5708
    c: Tangent(g27,g23) = -1.5708
    c: Radius(g27) = 16
    c: Distance(g25) = 9
    c: DistanceY(g26,g21) = 6.5
    c: Coincident(g28,g21)
    c: Coincident(g28,g26)
FEATURE [PartDesign::SubShapeBinder] Import047  label="Import047(Sketch151)"
  BindCopyOnChange = 0
  BindMode = 0
  ClaimChildren = false
  Context = -> Part008 [Body093.Import047.]
  FillStyle = 0
  Fuse = false
  MakeFace = false
  OffsetFill = false
  OffsetIntersection = false
  OffsetJoinType = 0
  OffsetOpenResult = false
  PartialLoad = false
  Relative = true
  Support = -> [Sketch151]
  TreeRank = 2728
  _Version = 8
FEATURE [PartDesign::Pad] Pad041
  AddSubType = 0
  AlongSketchNormal = false
  CheckUpToFaceLimits = true
  ClaimChildren = false
  Direction = (0,0,1)
  Fit = 0
  FitJoin = 0
  InnerFit = 0
  InnerFitJoin = 0
  InnerTaperAngle = 0
  InnerTaperAngleRev = 0
  Length = 1.5
  Length2 = 10
  Linearize = true
  NewSolid = false
  Profile = -> Import047
  Suppress = false
  TreeRank = 2729
  Type = 4
  _ProfileBasedVersion = 1
FEATURE [PartDesign::Mirrored] Mirrored007
  AddSubType = 0
  BaseFeature = -> Pad041
  CopyShape = false
  MirrorPlane = -> YZ_Plane104
  NewSolid = false
  OriginalSubs = -> [Pad041]
  Originals = -> [Pad041]
  ParallelTransform = true
  SubTransform = true
  Suppress = false
  TreeRank = 2730
  _Version = 3
FEATURE [PartDesign::ShapeBinder] ShapeBinder033
  Support = -> [Pocket021]
  TraceSupport = false
  TreeRank = 2768
FEATURE [PartDesign::ShapeBinder] ShapeBinder034
  Support = -> [Sketch111]
  TraceSupport = false
  TreeRank = 2769
FEATURE [Part::SubShapeBinder] Import048  label="Import048(Sketch151)"
  BindCopyOnChange = 0
  BindMode = 0
  ClaimChildren = false
  Context = -> Part [Body095.Import048.]
  FillStyle = 0
  Fuse = false
  MakeFace = false
  OffsetFill = false
  OffsetIntersection = false
  OffsetJoinType = 0
  OffsetOpenResult = false
  PartialLoad = false
  Relative = true
  Support = -> [Part008[Body080.Sketch151.]]
  TreeRank = 2771
  _Version = 8
FEATURE [Sketcher::SketchObject] Sketch152
  ArcFitTolerance = 1e-06
  AttachmentSupport = -> [XY_Plane106]
  ExternalGeometry = -> [ShapeBinder034,ShapeBinder033,Import048]
  FullyConstrained = true
  MapMode = 5
  Support = -> [XY_Plane106]
  TreeRank = 2770
  sketch-geometry (10):
    g0: ArcOfCircle CenterX=0 CenterY=24.6 CenterZ=0 NormalX=0 NormalY=0 NormalZ=1 AngleXU=0 Radius=19 StartAngle=2e-16 EndAngle=3.14159
    g1: LineSegment StartX=-19 StartY=24.6 StartZ=0 EndX=-19.548 EndY=23.708 EndZ=0
    g2: LineSegment StartX=-19.548 StartY=23.708 StartZ=0 EndX=-34.5 EndY=16.1323 EndZ=0
    g3: LineSegment StartX=19 StartY=24.6 StartZ=0 EndX=19.548 EndY=23.708 EndZ=0
    g4: LineSegment StartX=19.548 StartY=23.708 StartZ=0 EndX=34.5 EndY=16.1323 EndZ=0
    g5: LineSegment StartX=-15 StartY=53 StartZ=0 EndX=15.0001 EndY=53 EndZ=0
    g6: LineSegment StartX=34.5 StartY=33.5 StartZ=0 EndX=34.5 EndY=16.1323 EndZ=0
    g7: LineSegment StartX=-34.5 StartY=33.5 StartZ=0 EndX=-34.5 EndY=16.1323 EndZ=0
    g8: ArcOfCircle CenterX=-15 CenterY=33.5 CenterZ=0 NormalX=0 NormalY=0 NormalZ=1 AngleXU=0 Radius=19.5 StartAngle=1.5708 EndAngle=3.14159
    g9: ArcOfCircle CenterX=15 CenterY=33.5 CenterZ=0 NormalX=0 NormalY=0 NormalZ=1 AngleXU=0 Radius=19.5 StartAngle=3e-16 EndAngle=1.57079
  constraints (24):
    c: Horizontal(g4,g2)
    c: Coincident(g0,g-17)
    c: Coincident(g0,g-16)
    c: Horizontal(g0,g0)
    c: Coincident(g1,g0)
    c: Coincident(g1,g-15)
    c: Coincident(g2,g1)
    c: PointOnObject(g-13,g2)
    c: Coincident(g3,g0)
    c: Coincident(g4,g3)
    c: Symmetric(g3,g1,g-2)
    c: Coincident(g8,g-3)
    c: Coincident(g9,g-12)
    c: Coincident(g9,g5)
    c: Horizontal(g5)
    c: Vertical(g6)
    c: Vertical(g7)
    c: Coincident(g2,g7)
    c: Coincident(g4,g6)
    c: Tangent(g8,g7) = -1.5708
    c: Tangent(g9,g6) = 1.5708
    c: Radius(g8) = 19.5
    c: Radius(g9) = 19.5
    c: Tangent(g8,g5) = 1.5708
FEATURE [PartDesign::Pad] Pad043
  AddSubType = 0
  AlongSketchNormal = false
  CheckUpToFaceLimits = true
  ClaimChildren = false
  Direction = (0,0,1)
  Fit = 0
  FitJoin = 0
  InnerFit = 0
  InnerFitJoin = 0
  InnerTaperAngle = 0
  InnerTaperAngleRev = 0
  Length = 1
  Length2 = 100
  Linearize = true
  NewSolid = false
  Profile = -> Sketch152
  Suppress = false
  TreeRank = 2772
  Type = 0
  _ProfileBasedVersion = 1
FEATURE [PartDesign::Body] Body095  label="chin plate"
  AutoGroupSolids = false
  ClaimAllChildren = false
  ExportMode = 0
  Group = -> [ShapeBinder033,ShapeBinder034,Sketch152,Import048,Pad043]
  Origin = -> Origin114
  Tip = -> Pad043
  TreeRank = 3200
  _ExportChildren = -> [ShapeBinder033,ShapeBinder034,Import048,Pad043]
  _GroupVersion = 1
FEATURE [PartDesign::ShapeBinder] ShapeBinder035
  Placement = pos=(-34,0,0) rot=(0.57735,-0.57735,-0.57735;2.0944rad)
  Support = -> [Sketch104]
  TraceSupport = false
  TreeRank = 2867
FEATURE [Sketcher::SketchObject] Sketch153
  ArcFitTolerance = 1e-06
  AttachmentSupport = -> [DatumPlane043]
  ExternalGeometry = -> [ShapeBinder035]
  FullyConstrained = true
  MapMode = 5
  Placement = pos=(-35,17,0) rot=(0.57735,-0.57735,-0.57735;2.0944rad)
  Support = -> [DatumPlane043]
  TreeRank = 2868
  sketch-geometry (5):
    g0: LineSegment StartX=10 StartY=-0.253381 StartZ=0 EndX=10 EndY=0 EndZ=0
    g1: LineSegment StartX=10 StartY=0 StartZ=0 EndX=8 EndY=0 EndZ=0
    g2: LineSegment StartX=8 StartY=0 StartZ=0 EndX=8 EndY=-0.253381 EndZ=0
    g3: ArcOfCircle CenterX=9 CenterY=-2.1 CenterZ=0 NormalX=0 NormalY=0 NormalZ=1 AngleXU=0 Radius=2.1 StartAngle=2.06711 EndAngle=7.35766
    g4: LineSegment [constr] StartX=8 StartY=-0.253381 StartZ=0 EndX=10 EndY=-0.253381 EndZ=0
  constraints (14):
    c: Coincident(g0,g1)
    c: Coincident(g1,g2)
    c: Horizontal(g1)
    c: Vertical(g0)
    c: Vertical(g2)
    c: DistanceX(g1,g1) = 2
    c: PointOnObject(g0,g-1)
    c: Coincident(g3,g-3)
    c: Coincident(g3,g2)
    c: Coincident(g3,g0)
    c: Radius(g3) = 2.1
    c: Coincident(g4,g2)
    c: Coincident(g4,g0)
    c: Horizontal(g4)
FEATURE [PartDesign::Pocket] Pocket022
  AddSubType = 1
  BaseFeature = -> Pocket021
  CheckUpToFaceLimits = true
  ClaimChildren = false
  Fit = 0
  FitJoin = 0
  InnerFit = 0
  InnerFitJoin = 0
  InnerTaperAngle = 0
  InnerTaperAngleRev = 0
  Length = 10
  Length2 = 100
  Linearize = true
  NewSolid = false
  Placement = pos=(0,17,0) rot=(1,0,0;1.5708rad)
  Profile = -> Sketch153
  Suppress = false
  TreeRank = 2869
  Type = 0
  _ProfileBasedVersion = 1
  _Version = 1
FEATURE [Sketcher::SketchObject] Sketch154
  ArcFitTolerance = 1e-06
  AttachmentSupport = -> [XY_Plane108]
  FullyConstrained = true
  MapMode = 5
  Support = -> [XY_Plane108]
  TreeRank = 2885
  sketch-geometry (10):
    g0: LineSegment StartX=-25 StartY=7 StartZ=0 EndX=-35 EndY=7 EndZ=0
    g1: LineSegment StartX=-35 StartY=7 StartZ=0 EndX=-40 EndY=5.47135 EndZ=0
    g2: LineSegment StartX=-41.4153 StartY=3.55874 StartZ=0 EndX=-41.4153 EndY=-47.5587 EndZ=0
    g3: LineSegment StartX=-40 StartY=-49.4713 StartZ=0 EndX=-35 EndY=-51 EndZ=0
    g4: LineSegment StartX=-35 StartY=-51 StartZ=0 EndX=-25 EndY=-51 EndZ=0
    g5: LineSegment [constr] StartX=-40 StartY=5.47135 StartZ=0 EndX=-35 EndY=5.47135 EndZ=0
    g6: ArcOfCircle CenterX=-39.4153 CenterY=3.55874 CenterZ=0 NormalX=0 NormalY=0 NormalZ=1 AngleXU=0 Radius=2 StartAngle=1.8675 EndAngle=3.14159
    g7: ArcOfCircle CenterX=-39.4153 CenterY=-47.5587 CenterZ=0 NormalX=0 NormalY=0 NormalZ=1 AngleXU=0 Radius=2 StartAngle=3.14159 EndAngle=4.41568
    g8: GeomPoint [constr] X=-35 Y=7 Z=0
    g9: LineSegment [constr] StartX=-40 StartY=-49.4713 StartZ=0 EndX=-35 EndY=-49.4713 EndZ=0
  constraints (28):
    c: Horizontal(g0)
    c: Coincident(g1,g0)
    c: Vertical(g2)
    c: Coincident(g4,g3)
    c: Horizontal(g4)
    c: Coincident(g5,g1)
    c: Horizontal(g5)
    c: Tangent(g7,g2) = -1.5708
    c: Tangent(g7,g3) = -1.5708
    c: Tangent(g6,g1) = -1.5708
    c: Tangent(g6,g2) = -1.5708
    c: Radius(g6) = 2
    c: Radius(g7) = 2
    c: PointOnObject(g8,g0)
    c: DistanceX(g8,g0) = 10
    c: Vertical(g8,g0)
    c: DistanceX(g5,g5) = 5
    c: Angle(g5,g1) = 0.296706
    c: DistanceY(g3,g0) = 58
    c: Vertical(g0,g3)
    c: DistanceX(g4,g4) = 10
    c: Coincident(g9,g3)
    c: Horizontal(g9)
    c: Angle(g3,g9) = 0.296706
    c: Vertical(g5,g0)
    c: Vertical(g3,g9)
    c: DistanceY(g-1,g0) = 7
    c: DistanceX(g5,g-1) = 35
FEATURE [PartDesign::Plane] DatumPlane047
  AttachmentSupport = -> [Sketch154]
  Length = 51
  MapMode = 7
  MinimumLength = 10
  MinimumWidth = 10
  Placement = pos=(-25,-51,0) rot=(0.57735,-0.57735,-0.57735;2.0944rad)
  ResizeMode = 0
  Support = -> [Sketch154]
  TreeRank = 2888
  Width = 10
FEATURE [Sketcher::SketchObject] Sketch155
  ArcFitTolerance = 1e-06
  AttachmentSupport = -> [DatumPlane047]
  FullyConstrained = true
  MapMode = 5
  Placement = pos=(-25,-51,0) rot=(0.57735,-0.57735,-0.57735;2.0944rad)
  Support = -> [DatumPlane047]
  TreeRank = 2889
  sketch-geometry (1):
    g0: Circle CenterX=0 CenterY=0 CenterZ=0 NormalX=0 NormalY=0 NormalZ=1 AngleXU=0 Radius=1.5
  constraints (2):
    c: Coincident(g0,g-1)
    c: Radius(g0) = 1.5
FEATURE [Sketcher::SketchObject] Sketch156
  ArcFitTolerance = 1e-06
  AttachmentSupport = -> [DatumPlane047]
  FullyConstrained = true
  MapMode = 5
  Placement = pos=(-25,-51,0) rot=(0.57735,-0.57735,-0.57735;2.0944rad)
  Support = -> [DatumPlane047]
  TreeRank = 2891
  sketch-geometry (1):
    g0: Circle CenterX=0 CenterY=-2 CenterZ=0 NormalX=0 NormalY=0 NormalZ=1 AngleXU=0 Radius=2
  constraints (3):
    c: Radius(g0) = 2
    c: Tangent(g0,g-1)
    c: Vertical(g0,g-1)
FEATURE [PartDesign::AdditivePipe] Pipe015
  AddSubType = 0
  AuxilleryCurvelinear = true
  AuxillerySpineTangent = false
  Binormal = (0,0,0)
  ClaimChildren = false
  Fit = 0
  FitJoin = 0
  InnerFit = 0
  InnerFitJoin = 0
  Linearize = true
  Mode = 0
  NewSolid = false
  Placement = pos=(-25,-51,0) rot=(0.57735,-0.57735,-0.57735;2.0944rad)
  Profile = -> Sketch156
  Spine = -> Sketch154 [Edge7]
  SpineTangent = false
  Suppress = false
  Transformation = 0
  Transition = 1
  TreeRank = 2892
  _ProfileBasedVersion = 2
FEATURE [PartDesign::Plane] DatumPlane048
  AttachmentSupport = -> [Sketch154]
  Length = 59.0046
  MapMode = 7
  MinimumLength = 10
  MinimumWidth = 10
  Placement = pos=(-40,-49.4713,0) rot=(-0.463605,0.626526,0.626526;4.00981rad)
  ResizeMode = 0
  Support = -> [Sketch154]
  TreeRank = 2893
  Width = 10
FEATURE [Sketcher::SketchObject] Sketch157
  ArcFitTolerance = 1e-06
  AttachmentSupport = -> [DatumPlane048]
  FullyConstrained = true
  MapMode = 5
  Placement = pos=(-40,-49.4713,0) rot=(-0.463605,0.626526,0.626526;4.00981rad)
  Support = -> [DatumPlane048]
  TreeRank = 2900
  sketch-geometry (1):
    g0: Circle CenterX=0 CenterY=-1.5 CenterZ=0 NormalX=0 NormalY=0 NormalZ=1 AngleXU=0 Radius=1.5
  constraints (3):
    c: Radius(g0) = 1.5
    c: Vertical(g0,g-1)
    c: Tangent(g0,g-1)
FEATURE [PartDesign::Plane] DatumPlane049
  AttachmentSupport = -> [Sketch154]
  Length = 16.9271
  MapMode = 7
  MinimumLength = 10
  MinimumWidth = 10
  Placement = pos=(-40,5.47135,0) rot=(0.463605,0.626526,0.626526;2.27337rad)
  ResizeMode = 0
  Support = -> [Sketch154]
  TreeRank = 2895
  Width = 10
FEATURE [Sketcher::SketchObject] Sketch158
  ArcFitTolerance = 1e-06
  AttachmentSupport = -> [DatumPlane049]
  FullyConstrained = true
  MapMode = 5
  Placement = pos=(-40,5.47135,0) rot=(0.463605,0.626526,0.626526;2.27337rad)
  Support = -> [DatumPlane049]
  TreeRank = 2896
  sketch-geometry (1):
    g0: Circle CenterX=0 CenterY=-1.5 CenterZ=0 NormalX=0 NormalY=0 NormalZ=1 AngleXU=0 Radius=1.5
  constraints (3):
    c: Radius(g0) = 1.5
    c: Vertical(g0,g-1)
    c: Tangent(g-1,g0)
FEATURE [Sketcher::SketchObject] Sketch159
  ArcFitTolerance = 1e-06
  AttachmentSupport = -> [Pipe015]
  FullyConstrained = true
  MapMode = 5
  Placement = pos=(-35,-51,0) rot=(0.57735,-0.57735,0.57735;4.18879rad)
  Support = -> [Pipe015]
  TreeRank = 2897
  sketch-geometry (1):
    g0: Circle CenterX=0 CenterY=2 CenterZ=0 NormalX=0 NormalY=0 NormalZ=1 AngleXU=0 Radius=2
  constraints (3):
    c: Radius(g0) = 2
    c: Vertical(g0,g-1)
    c: Tangent(g0,g-1)
FEATURE [PartDesign::Plane] DatumPlane050
  AttachmentSupport = -> [Sketch154]
  Length = 62
  MapMode = 7
  MinimumLength = 10
  MinimumWidth = 10
  Placement = pos=(-35,7,0) rot=(0.57735,0.57735,0.57735;2.0944rad)
  ResizeMode = 0
  Support = -> [Sketch154]
  TreeRank = 2898
  Width = 10
FEATURE [Sketcher::SketchObject] Sketch160
  ArcFitTolerance = 1e-06
  AttachmentSupport = -> [DatumPlane050]
  FullyConstrained = true
  MapMode = 5
  Placement = pos=(-35,7,0) rot=(0.57735,0.57735,0.57735;2.0944rad)
  Support = -> [DatumPlane050]
  TreeRank = 2902
  sketch-geometry (1):
    g0: Circle CenterX=0 CenterY=-2 CenterZ=0 NormalX=0 NormalY=0 NormalZ=1 AngleXU=0 Radius=2
  constraints (3):
    c: Radius(g0) = 2
    c: Vertical(g0,g-1)
    c: Tangent(g0,g-1)
FEATURE [PartDesign::AdditiveLoft] Loft007
  AddSubType = 0
  BaseFeature = -> Pipe015
  ClaimChildren = false
  Closed = false
  Fit = 0
  FitJoin = 0
  InnerFit = 0
  InnerFitJoin = 0
  Linearize = true
  NewSolid = false
  Placement = pos=(-25,-51,0) rot=(0.57735,-0.57735,-0.57735;2.0944rad)
  Profile = -> Sketch159
  Ruled = false
  Sections = -> [Sketch157]
  SplitProfile = false
  Suppress = false
  TreeRank = 2901
  _ProfileBasedVersion = 1
FEATURE [PartDesign::AdditivePipe] Pipe016
  AddSubType = 0
  AuxilleryCurvelinear = true
  AuxillerySpineTangent = false
  BaseFeature = -> Loft007
  Binormal = (0,0,0)
  ClaimChildren = false
  Fit = 0
  FitJoin = 0
  InnerFit = 0
  InnerFitJoin = 0
  Linearize = true
  Mode = 0
  NewSolid = false
  Placement = pos=(-25,-51,0) rot=(0.57735,-0.57735,-0.57735;2.0944rad)
  Profile = -> Sketch157
  Spine = -> Sketch154 [Edge5,Edge4,Edge3]
  SpineTangent = false
  Suppress = false
  Transformation = 0
  Transition = 1
  TreeRank = 2903
  _ProfileBasedVersion = 2
FEATURE [PartDesign::AdditiveLoft] Loft008
  AddSubType = 0
  BaseFeature = -> Pipe016
  ClaimChildren = false
  Closed = false
  Fit = 0
  FitJoin = 0
  InnerFit = 0
  InnerFitJoin = 0
  Linearize = true
  NewSolid = false
  Placement = pos=(-25,-51,0) rot=(0.57735,-0.57735,-0.57735;2.0944rad)
  Profile = -> Sketch158
  Ruled = false
  Sections = -> [Sketch160]
  SplitProfile = false
  Suppress = false
  TreeRank = 2904
  _ProfileBasedVersion = 1
FEATURE [PartDesign::AdditivePipe] Pipe017
  AddSubType = 0
  AuxilleryCurvelinear = true
  AuxillerySpineTangent = false
  BaseFeature = -> Loft008
  Binormal = (0,0,0)
  ClaimChildren = false
  Fit = 0
  FitJoin = 0
  InnerFit = 0
  InnerFitJoin = 0
  Linearize = true
  Mode = 0
  NewSolid = false
  Placement = pos=(-25,-51,0) rot=(0.57735,-0.57735,-0.57735;2.0944rad)
  Profile = -> Sketch160
  Spine = -> Sketch154 [Edge1]
  SpineTangent = false
  Suppress = false
  Transformation = 0
  Transition = 1
  TreeRank = 2905
  _ProfileBasedVersion = 2
FEATURE [PartDesign::Mirrored] Mirrored009
  AddSubType = 0
  BaseFeature = -> Pipe017
  CopyShape = false
  MirrorPlane = -> YZ_Plane108
  NewSolid = false
  OriginalSubs = -> [Pipe017,Loft008,Pipe016,Loft007,Pipe015]
  Originals = -> [Pipe017,Loft008,Pipe016,Loft007,Pipe015]
  ParallelTransform = true
  Placement = pos=(-25,-51,0) rot=(0.57735,-0.57735,-0.57735;2.0944rad)
  SubTransform = true
  Suppress = false
  TreeRank = 2906
  _Version = 3
FEATURE [PartDesign::Body] Body097  label="side bars"
  AutoGroupSolids = false
  ClaimAllChildren = false
  ExportMode = 0
  Group = -> [Sketch154,DatumPlane047,Sketch155,Sketch156,Pipe015,DatumPlane048,Sketch157,DatumPlane049,Sketch158,Sketch159,DatumPlane050,Sketch160,Loft007,Pipe016,Loft008,Pipe017,Mirrored009]
  Origin = -> Origin116
  Tip = -> Mirrored009
  TreeRank = 2884
  _ExportChildren = -> [DatumPlane047,Sketch155,Pipe015,DatumPlane048,DatumPlane049,DatumPlane050,Loft007,Pipe016,Loft008,Pipe017,Mirrored009]
  _GroupVersion = 1
FEATURE [Sketcher::SketchObject] Sketch161
  ArcFitTolerance = 1e-06
  AttachmentSupport = -> [XY_Plane]
  FullyConstrained = true
  MapMode = 5
  Support = -> [XY_Plane]
  TreeRank = 2936
FEATURE [Part::SubShapeBinder] Import051  label="Import051(Sketch005)"
  BindCopyOnChange = 0
  BindMode = 0
  ClaimChildren = false
  Context = -> Part008 [Body098.Import051.]
  FillStyle = 0
  Fuse = false
  MakeFace = false
  OffsetFill = false
  OffsetIntersection = false
  OffsetJoinType = 0
  OffsetOpenResult = false
  PartialLoad = false
  Relative = true
  Support = -> [Body080[Sketch005.]]
  TreeRank = 2938
  _Version = 8
FEATURE [Part::SubShapeBinder] Import052  label="Import052(MultiTransform009)"
  BindCopyOnChange = 0
  BindMode = 0
  ClaimChildren = false
  Context = -> Part008 [Body098.Import052.]
  FillStyle = 0
  Fuse = false
  MakeFace = false
  OffsetFill = false
  OffsetIntersection = false
  OffsetJoinType = 0
  OffsetOpenResult = false
  PartialLoad = false
  Relative = true
  Support = -> [Body080[MultiTransform009.]]
  TreeRank = 2939
  _Version = 8
FEATURE [Part::SubShapeBinder] Import053  label="Import053(Sketch111)"
  BindCopyOnChange = 0
  BindMode = 0
  ClaimChildren = false
  Context = -> Part008 [Body098.Import053.]
  FillStyle = 0
  Fuse = false
  MakeFace = false
  OffsetFill = false
  OffsetIntersection = false
  OffsetJoinType = 0
  OffsetOpenResult = false
  PartialLoad = false
  Relative = true
  Support = -> [Body080[Sketch111.]]
  TreeRank = 2940
  _Version = 8
FEATURE [Sketcher::SketchObject] Sketch162  label="front bar path"
  ArcFitTolerance = 1e-06
  AttachmentSupport = -> [XY_Plane109]
  ExternalGeometry = -> [Import051,Import052,Import053]
  FullyConstrained = true
  MapMode = 5
  Support = -> [XY_Plane109]
  TreeRank = 2937
  sketch-geometry (13):
    g0: LineSegment StartX=0 StartY=62.1 StartZ=0 EndX=-11 EndY=62.1 EndZ=0
    g1: ArcOfCircle CenterX=-11 CenterY=59.1 CenterZ=0 NormalX=0 NormalY=0 NormalZ=1 AngleXU=0 Radius=3 StartAngle=1.5708 EndAngle=3.03756
    g2: LineSegment StartX=-33 StartY=52.1 StartZ=0 EndX=-36.5355 EndY=48.5645 EndZ=0
    g3: ArcOfCircle CenterX=-33 CenterY=45.0289 CenterZ=0 NormalX=0 NormalY=0 NormalZ=1 AngleXU=0 Radius=5 StartAngle=2.35619 EndAngle=3.75246
    g4: ArcOfCircle CenterX=-29.4645 CenterY=48.5645 CenterZ=0 NormalX=0 NormalY=0 NormalZ=1 AngleXU=0 Radius=5 StartAngle=0.959931 EndAngle=2.35619
    g5: LineSegment [constr] StartX=-25.61 StartY=25.7576 StartZ=0 EndX=-25.61 EndY=21.7576 EndZ=0
    g6: LineSegment StartX=-20.1593 StartY=48.1528 StartZ=0 EndX=-15.1593 EndY=48.1528 EndZ=0
    g7: LineSegment StartX=-20.1593 StartY=48.1528 StartZ=0 EndX=-24.255 EndY=51.0206 EndZ=0
    g8: LineSegment StartX=-24.255 StartY=51.0206 StartZ=0 EndX=-26.5966 EndY=52.6602 EndZ=0
    g9: LineSegment StartX=-37.0958 StartY=42.1611 StartZ=0 EndX=-29.625 EndY=31.4917 EndZ=0
    g10: LineSegment StartX=-29.625 StartY=31.4917 StartZ=0 EndX=-25.61 EndY=25.7576 EndZ=0
    g11: LineSegment StartX=-13.9838 StartY=59.4115 StartZ=0 EndX=-14.8578 EndY=51.0405 EndZ=0
    g12: LineSegment StartX=-14.8578 StartY=51.0405 StartZ=0 EndX=-16 EndY=40.1 EndZ=0
  constraints (38):
    c: PointOnObject(g0,g-2)
    c: Horizontal(g0)
    c: Tangent(g1,g11) = -1.5708
    c: DistanceY(g-3,g0) = 37.5
    c: DistanceX(g0,g0) = 11
    c: DistanceX(g-3,g12) = 4
    c: Radius(g1) = 3
    c: Tangent(g1,g0) = -1.5708
    c: Tangent(g4,g8) = -1.5708
    c: Tangent(g3,g2) = -1.5708
    c: Tangent(g3,g9) = -1.5708
    c: Radius(g4) = 5
    c: Radius(g3) = 5
    c: DistanceY(g12,g0) = 22
    c: Distance(g2) = 5
    c: Tangent(g4,g2) = -1.5708
    c: Coincident(g5,g10)
    c: PointOnObject(g5,g-4)
    c: Vertical(g5)
    c: Angle(g-1,g2) = 0.785398
    c: Coincident(g6,g7)
    c: Distance(g6) = 5
    c: DistanceY(g5,g5) = 4
    c: Horizontal(g6)
    c: DistanceY(g2,g0) = 10
    c: DistanceX(g2,g0) = 22
    c: Coincident(g7,g8)
    c: Coincident(g9,g10)
    c: Coincident(g11,g12)
    c: PointOnObject(g6,g12)
    c: Parallel(g7,g8)
    c: Parallel(g10,g9)
    c: Parallel(g12,g11)
    c: Distance(g7) = 5
    c: Distance(g10) = 7
    c: Distance(g12) = 11
    c: Angle(g-2,g9) = 0.610865
    c: Angle(g8,g-1) = 0.610865
FEATURE [Sketcher::SketchObject] Sketch163
  ArcFitTolerance = 1e-06
  AttachmentSupport = -> [XY_Plane109]
  ExternalGeometry = -> [Sketch162]
  FullyConstrained = true
  MapMode = 5
  Support = -> [XY_Plane109]
  TreeRank = 2941
  sketch-geometry (2):
    g0: LineSegment StartX=-17.4184 StartY=31.4934 StartZ=0 EndX=-25.61 EndY=25.7576 EndZ=0
    g1: LineSegment StartX=-16 StartY=40.1 StartZ=0 EndX=-6.05406 EndY=39.0616 EndZ=0
  constraints (6):
    c: Distance(g0) = 10
    c: Distance(g1) = 10
    c: Coincident(g0,g-3)
    c: Coincident(g-4,g1)
    c: Perpendicular(g-3,g0)
    c: Perpendicular(g-4,g1)
FEATURE [PartDesign::Plane] DatumPlane052
  AttachmentSupport = -> [Sketch163]
  Length = 46.1446
  MapMode = 7
  MinimumLength = 10
  MinimumWidth = 10
  Placement = pos=(-16,40.1,0) rot=(-0.537332,0.596353,0.596353;4.12772rad)
  ResizeMode = 0
  Support = -> [Sketch163]
  TreeRank = 2944
  Width = 10
FEATURE [Sketcher::SketchObject] Sketch165
  ArcFitTolerance = 1e-06
  AttachmentSupport = -> [DatumPlane052]
  FullyConstrained = true
  MapMode = 5
  Placement = pos=(-16,40.1,0) rot=(-0.537332,0.596353,0.596353;4.12772rad)
  Support = -> [DatumPlane052]
  TreeRank = 2945
  sketch-geometry (1):
    g0: ArcOfCircle CenterX=0 CenterY=3 CenterZ=0 NormalX=0 NormalY=0 NormalZ=1 AngleXU=0 Radius=3 StartAngle=4.71239 EndAngle=6.28319
  constraints (4):
    c: PointOnObject(g0,g-2)
    c: Coincident(g0,g-1)
    c: Radius(g0) = 3
    c: Horizontal(g0,g0)
FEATURE [Sketcher::SketchObject] Sketch166  label="circle w support"
  ArcFitTolerance = 1e-06
  AttachmentSupport = -> [YZ_Plane109]
  ExternalGeometry = -> [Sketch162]
  FullyConstrained = true
  MapMode = 5
  Placement = pos=(0,0,0) rot=(0.57735,0.57735,0.57735;2.0944rad)
  Support = -> [YZ_Plane109]
  TreeRank = 2946
  sketch-geometry (6):
    g0: LineSegment StartX=60.6 StartY=-1.50002 StartZ=0 EndX=60.6 EndY=0 EndZ=0
    g1: LineSegment StartX=60.6 StartY=0 StartZ=0 EndX=62.1 EndY=1.88e-14 EndZ=0
    g2: LineSegment StartX=62.1 StartY=1.88e-14 StartZ=0 EndX=63.6 EndY=0 EndZ=0
    g3: LineSegment StartX=63.6 StartY=0 StartZ=0 EndX=63.6 EndY=-1.50002 EndZ=0
    g4: ArcOfCircle CenterX=62.1 CenterY=-1.5 CenterZ=0 NormalX=0 NormalY=0 NormalZ=1 AngleXU=0 Radius=1.5 StartAngle=3.1416 EndAngle=6.28317
    g5: Circle [constr] CenterX=62.1 CenterY=-1.5 CenterZ=0 NormalX=0 NormalY=0 NormalZ=1 AngleXU=0 Radius=1.5
  constraints (17):
    c: PointOnObject(g0,g-1)
    c: Vertical(g0)
    c: Coincident(g1,g0)
    c: Coincident(g1,g-3)
    c: Coincident(g2,g1)
    c: PointOnObject(g2,g-1)
    c: Coincident(g3,g2)
    c: Coincident(g4,g0)
    c: Coincident(g4,g3)
    c: Vertical(g3)
    c: Equal(g2,g1)
    c: Horizontal(g3,g0)
    c: Radius(g4) = 1.5
    c: Coincident(g5,g4)
    c: PointOnObject(g1,g5)
    c: PointOnObject(g3,g5)
    c: DistanceX(g2,g2) = 1.5
FEATURE [Sketcher::SketchObject] Sketch167  label="circle wo support"
  ArcFitTolerance = 1e-06
  AttachmentSupport = -> [YZ_Plane109]
  ExternalGeometry = -> [Sketch162]
  FullyConstrained = true
  MapMode = 5
  Placement = pos=(0,0,0) rot=(0.57735,0.57735,0.57735;2.0944rad)
  Support = -> [YZ_Plane109]
  TreeRank = 2947
  sketch-geometry (1):
    g0: Circle CenterX=62.1 CenterY=-1.5 CenterZ=0 NormalX=0 NormalY=0 NormalZ=1 AngleXU=0 Radius=1.5
  constraints (3):
    c: PointOnObject(g-3,g0)
    c: Vertical(g0,g-3)
    c: Radius(g0) = 1.5
FEATURE [PartDesign::AdditivePipe] Pipe018
  AddSubType = 0
  AuxilleryCurvelinear = true
  AuxillerySpineTangent = false
  Binormal = (0,0,0)
  ClaimChildren = false
  Fit = 0
  FitJoin = 0
  InnerFit = 0
  InnerFitJoin = 0
  Linearize = true
  Mode = 0
  NewSolid = false
  Placement = pos=(0,0,0) rot=(0.57735,0.57735,0.57735;2.0944rad)
  Profile = -> Sketch167
  Spine = -> Sketch162 [Edge1,Edge2,Edge3,Edge4]
  SpineTangent = false
  Suppress = false
  Transformation = 0
  Transition = 1
  TreeRank = 2948
  _ProfileBasedVersion = 2
FEATURE [PartDesign::Plane] DatumPlane053
  AttachmentSupport = -> [Sketch162]
  Length = 82.4855
  MapMode = 7
  MinimumLength = 10
  MinimumWidth = 10
  Placement = pos=(-16,40.1,0) rot=(0.036788,0.706628,0.706628;3.06805rad)
  ResizeMode = 0
  Support = -> [Sketch162]
  TreeRank = 2949
  Width = 10
FEATURE [Sketcher::SketchObject] Sketch168
  ArcFitTolerance = 1e-06
  AttachmentSupport = -> [DatumPlane053]
  FullyConstrained = true
  MapMode = 5
  Placement = pos=(-16,40.1,0) rot=(0.036788,0.706628,0.706628;3.06805rad)
  Support = -> [DatumPlane053]
  TreeRank = 2950
  sketch-geometry (5):
    g0: ArcOfCircle CenterX=0 CenterY=-1.5 CenterZ=0 NormalX=0 NormalY=0 NormalZ=1 AngleXU=0 Radius=1.5 StartAngle=3.14159 EndAngle=6.28319
    g1: LineSegment StartX=-1.5 StartY=-1.5 StartZ=0 EndX=-1.5 EndY=0 EndZ=0
    g2: LineSegment StartX=-1.5 StartY=0 StartZ=0 EndX=0 EndY=0 EndZ=0
    g3: LineSegment StartX=0 StartY=0 StartZ=0 EndX=1.5 EndY=0 EndZ=0
    g4: LineSegment StartX=1.5 StartY=0 StartZ=0 EndX=1.5 EndY=-1.5 EndZ=0
  constraints (15):
    c: PointOnObject(g0,g-2)
    c: Coincident(g1,g0)
    c: PointOnObject(g1,g-1)
    c: Vertical(g1)
    c: Coincident(g2,g1)
    c: Coincident(g2,g-1)
    c: Coincident(g3,g2)
    c: PointOnObject(g3,g-1)
    c: Coincident(g4,g3)
    c: Coincident(g4,g0)
    c: Vertical(g4)
    c: Radius(g0) = 1.5
    c: Horizontal(g0,g0)
    c: Horizontal(g0,g0)
    c: DistanceY(g1,g1) = 1.5
FEATURE [PartDesign::AdditivePipe] Pipe019
  AddSubType = 0
  AuxilleryCurvelinear = true
  AuxillerySpineTangent = false
  BaseFeature = -> Pipe018
  Binormal = (0,0,0)
  ClaimChildren = false
  Fit = 0
  FitJoin = 0
  InnerFit = 0
  InnerFitJoin = 0
  Linearize = true
  Mode = 0
  NewSolid = false
  Placement = pos=(0,0,0) rot=(0.57735,0.57735,0.57735;2.0944rad)
  Profile = -> Sketch168
  Spine = -> Sketch162 [Edge4]
  SpineTangent = false
  Suppress = false
  Transformation = 0
  Transition = 1
  TreeRank = 2951
  _ProfileBasedVersion = 2
FEATURE [PartDesign::Fillet] Fillet018
  AddSubType = 0
  Base = -> Pipe019 [Face9]
  BaseFeature = -> Pipe019
  NewSolid = false
  Placement = pos=(0,0,0) rot=(0.57735,0.57735,0.57735;2.0944rad)
  Radius = 1.4
  SupportTransform = false
  Suppress = false
  TreeRank = 2952
FEATURE [PartDesign::Plane] DatumPlane054
  AttachmentSupport = -> [Sketch162]
  Length = 86.5559
  MapMode = 7
  MinimumLength = 10
  MinimumWidth = 10
  Placement = pos=(-25.61,25.7576,0) rot=(-0.217607,0.690162,0.690162;3.57013rad)
  ResizeMode = 0
  Support = -> [Sketch162]
  TreeRank = 2953
  Width = 10
FEATURE [Sketcher::SketchObject] Sketch169
  ArcFitTolerance = 1e-06
  AttachmentSupport = -> [DatumPlane054]
  FullyConstrained = true
  MapMode = 5
  Placement = pos=(-25.61,25.7576,0) rot=(-0.217607,0.690162,0.690162;3.57013rad)
  Support = -> [DatumPlane054]
  TreeRank = 2954
  sketch-geometry (1):
    g0: Circle CenterX=0 CenterY=-1.5 CenterZ=0 NormalX=0 NormalY=0 NormalZ=1 AngleXU=0 Radius=1.5
  constraints (3):
    c: PointOnObject(g0,g-2)
    c: PointOnObject(g-1,g0)
    c: Radius(g0) = 1.5
FEATURE [PartDesign::AdditivePipe] Pipe020
  AddSubType = 0
  AuxilleryCurvelinear = true
  AuxillerySpineTangent = false
  BaseFeature = -> Fillet018
  Binormal = (0,0,0)
  ClaimChildren = false
  Fit = 0
  FitJoin = 0
  InnerFit = 0
  InnerFitJoin = 0
  Linearize = true
  Mode = 0
  NewSolid = false
  Placement = pos=(0,0,0) rot=(0.57735,0.57735,0.57735;2.0944rad)
  Profile = -> Sketch169
  Spine = -> Sketch162 [Edge12,Edge11,Edge10,Edge9,Edge8,Edge7,Edge6,Edge5]
  SpineTangent = false
  Suppress = false
  Transformation = 0
  Transition = 2
  TreeRank = 2955
  _ProfileBasedVersion = 2
FEATURE [Sketcher::SketchObject] Sketch170
  ArcFitTolerance = 1e-06
  AttachmentSupport = -> [DatumPlane054]
  ExternalGeometry = -> [Pipe020]
  FullyConstrained = true
  MapMode = 5
  Placement = pos=(-25.61,25.7576,0) rot=(-0.217607,0.690162,0.690162;3.57013rad)
  Support = -> [DatumPlane054]
  TreeRank = 2956
  sketch-geometry (4):
    g0: LineSegment StartX=-1.5 StartY=0 StartZ=0 EndX=1.5 EndY=0 EndZ=0
    g1: LineSegment StartX=1.5 StartY=0 StartZ=0 EndX=1.5 EndY=-1.5 EndZ=0
    g2: LineSegment StartX=1.5 StartY=-1.5 StartZ=0 EndX=-1.5 EndY=-1.5 EndZ=0
    g3: LineSegment StartX=-1.5 StartY=-1.5 StartZ=0 EndX=-1.5 EndY=0 EndZ=0
  constraints (12):
    c: Coincident(g0,g1)
    c: Coincident(g1,g2)
    c: Coincident(g2,g3)
    c: Coincident(g3,g0)
    c: Horizontal(g0)
    c: Horizontal(g2)
    c: Vertical(g1)
    c: Vertical(g3)
    c: PointOnObject(g0,g-1)
    c: PointOnObject(g1,g-3)
    c: PointOnObject(g2,g-3)
    c: Horizontal(g-3,g2)
FEATURE [PartDesign::AdditivePipe] Pipe021
  AddSubType = 0
  AuxilleryCurvelinear = true
  AuxillerySpineTangent = false
  BaseFeature = -> Pipe020
  Binormal = (0,0,0)
  ClaimChildren = false
  Fit = 0
  FitJoin = 0
  InnerFit = 0
  InnerFitJoin = 0
  Linearize = true
  Mode = 0
  NewSolid = false
  Placement = pos=(0,0,0) rot=(0.57735,0.57735,0.57735;2.0944rad)
  Profile = -> Sketch170
  Spine = -> Sketch162 [Edge12]
  SpineTangent = false
  Suppress = false
  Transformation = 0
  Transition = 1
  TreeRank = 2957
  _ProfileBasedVersion = 2
FEATURE [PartDesign::Plane] DatumPlane055
  AttachmentSupport = -> [Sketch162]
  Length = 38.1526
  MapMode = 7
  MinimumLength = 10
  MinimumWidth = 10
  Placement = pos=(-15.1593,48.1528,0) rot=(0.57735,-0.57735,-0.57735;2.0944rad)
  ResizeMode = 0
  Support = -> [Sketch162]
  TreeRank = 2958
  Width = 10
FEATURE [Sketcher::SketchObject] Sketch171
  ArcFitTolerance = 1e-06
  AttachmentSupport = -> [DatumPlane055]
  FullyConstrained = true
  MapMode = 5
  Placement = pos=(-15.1593,48.1528,0) rot=(0.57735,-0.57735,-0.57735;2.0944rad)
  Support = -> [DatumPlane055]
  TreeRank = 2959
  sketch-geometry (5):
    g0: LineSegment StartX=0 StartY=0 StartZ=0 EndX=1.5 EndY=0 EndZ=0
    g1: LineSegment StartX=1.5 StartY=0 StartZ=0 EndX=1.5 EndY=-1.5 EndZ=0
    g2: LineSegment StartX=1.5 StartY=-1.5 StartZ=0 EndX=-1.5 EndY=-1.5 EndZ=0
    g3: LineSegment StartX=-1.5 StartY=-1.5 StartZ=0 EndX=-1.5 EndY=0 EndZ=0
    g4: LineSegment StartX=-1.5 StartY=0 StartZ=0 EndX=0 EndY=0 EndZ=0
  constraints (14):
    c: Coincident(g0,g-1)
    c: PointOnObject(g0,g-1)
    c: Coincident(g1,g0)
    c: Coincident(g2,g1)
    c: Horizontal(g2)
    c: Coincident(g3,g2)
    c: PointOnObject(g3,g-1)
    c: Coincident(g4,g3)
    c: Coincident(g4,g0)
    c: Vertical(g1)
    c: Vertical(g3)
    c: Equal(g0,g4)
    c: DistanceX(g2,g2) = 3
    c: DistanceY(g1,g1) = 1.5
FEATURE [PartDesign::AdditivePipe] Pipe022
  AddSubType = 0
  AuxilleryCurvelinear = true
  AuxillerySpineTangent = false
  BaseFeature = -> Pipe021
  Binormal = (0,0,0)
  ClaimChildren = false
  Fit = 0
  FitJoin = 0
  InnerFit = 0
  InnerFitJoin = 0
  Linearize = true
  Mode = 0
  NewSolid = false
  Placement = pos=(0,0,0) rot=(0.57735,0.57735,0.57735;2.0944rad)
  Profile = -> Sketch171
  Spine = -> Sketch162 [Edge5,Edge6]
  SpineTangent = false
  Suppress = false
  Transformation = 0
  Transition = 2
  TreeRank = 2960
  _ProfileBasedVersion = 2
FEATURE [PartDesign::Fillet] Fillet019
  AddSubType = 0
  Base = -> Pipe022 [Edge107,Edge96,Edge105]
  BaseFeature = -> Pipe022
  NewSolid = false
  Placement = pos=(0,0,0) rot=(0.57735,0.57735,0.57735;2.0944rad)
  Radius = 1.4
  SupportTransform = false
  Suppress = false
  TreeRank = 2961
FEATURE [PartDesign::Mirrored] Mirrored010
  AddSubType = 0
  BaseFeature = -> Fillet019
  CopyShape = false
  MirrorPlane = -> YZ_Plane109
  NewSolid = false
  OriginalSubs = -> [Fillet019,Pipe022,Pipe021,Pipe020,Pipe019,Fillet018,Pipe018]
  Originals = -> [Fillet019,Pipe022,Pipe021,Pipe020,Pipe019,Fillet018,Pipe018]
  ParallelTransform = true
  Placement = pos=(0,0,0) rot=(0.57735,0.57735,0.57735;2.0944rad)
  SubTransform = true
  Suppress = false
  TreeRank = 2962
  _Version = 3
FEATURE [PartDesign::Body] Body098  label="front bars"
  AutoGroupSolids = false
  ClaimAllChildren = false
  ExportMode = 0
  Group = -> [Sketch162,Import051,Import052,Import053,Sketch163,DatumPlane052,Sketch165,Sketch166,Sketch167,Pipe018,DatumPlane053,Sketch168,Pipe019,Fillet018,DatumPlane054,Sketch169,Pipe020,Sketch170,Pipe021,DatumPlane055,Sketch171,Pipe022,Fillet019,Mirrored010]
  Origin = -> Origin117
  Tip = -> Mirrored010
  TreeRank = 2918
  _ExportChildren = -> [Import051,Import052,Import053,Sketch163,DatumPlane052,Sketch165,Sketch166,Pipe018,DatumPlane053,Pipe019,Fillet018,DatumPlane054,Pipe020,Pipe021,DatumPlane055,Pipe022,Fillet019,Mirrored010]
  _GroupVersion = 1
FEATURE [PartDesign::ShapeBinder] ShapeBinder036
  Placement = pos=(0,0,0) rot=(0.57735,0.57735,0.57735;2.0944rad)
  Support = -> [Sketch069]
  TraceSupport = false
  TreeRank = 2977
FEATURE [Sketcher::SketchObject] Sketch174
  ArcFitTolerance = 1e-06
  AttachmentSupport = -> [YZ_Plane110]
  ExternalGeometry = -> [ShapeBinder036]
  FullyConstrained = true
  MapMode = 5
  Placement = pos=(0,0,0) rot=(0.57735,0.57735,0.57735;2.0944rad)
  Support = -> [YZ_Plane110]
  TreeRank = 2982
  sketch-geometry (1):
    g0: LineSegment StartX=19.5 StartY=0 StartZ=0 EndX=19.5 EndY=-5 EndZ=0
  constraints (4):
    c: PointOnObject(g0,g-1)
    c: Vertical(g0)
    c: DistanceY(g0,g0) = 5
    c: Vertical(g-3,g0)
FEATURE [PartDesign::Plane] DatumPlane056
  AttachmentSupport = -> [Sketch174]
  Length = 28
  MapMode = 7
  MinimumLength = 10
  MinimumWidth = 10
  Placement = pos=(5.4e-15,19.5,-5) rot=(0,0,1;0rad)
  ResizeMode = 0
  Support = -> [Sketch174]
  TreeRank = 2983
  Width = 105
FEATURE [Sketcher::SketchObject] Sketch172
  ArcFitTolerance = 1e-06
  AttachmentSupport = -> [DatumPlane056]
  ExternalGeometry = -> [ShapeBinder036]
  FullyConstrained = true
  MapMode = 5
  Placement = pos=(5.4e-15,19.5,-5) rot=(0,0,1;0rad)
  Support = -> [DatumPlane056]
  TreeRank = 2976
  sketch-geometry (4):
    g0: LineSegment StartX=-14 StartY=12 StartZ=0 EndX=14 EndY=12 EndZ=0
    g1: LineSegment StartX=14 StartY=12 StartZ=0 EndX=14 EndY=-93 EndZ=0
    g2: LineSegment StartX=14 StartY=-93 StartZ=0 EndX=-14 EndY=-93 EndZ=0
    g3: LineSegment StartX=-14 StartY=-93 StartZ=0 EndX=-14 EndY=12 EndZ=0
  constraints (11):
    c: Coincident(g0,g1)
    c: Coincident(g1,g2)
    c: Coincident(g2,g3)
    c: Coincident(g3,g0)
    c: Horizontal(g2)
    c: Vertical(g1)
    c: Vertical(g3)
    c: DistanceY(g1,g1) = 105
    c: DistanceX(g2,g2) = 28
    c: Symmetric(g0,g0,g-2)
    c: DistanceY(g-3,g0) = 12
FEATURE [PartDesign::Pad] Pad044
  AddSubType = 0
  AlongSketchNormal = false
  CheckUpToFaceLimits = true
  ClaimChildren = false
  Direction = (-2e-16,2e-16,1)
  Fit = 0
  FitJoin = 0
  InnerFit = 0
  InnerFitJoin = 0
  InnerTaperAngle = 0
  InnerTaperAngleRev = 0
  Length = 1.6
  Length2 = 100
  Linearize = true
  NewSolid = false
  Placement = pos=(5.4e-15,19.5,-5) rot=(0,0,1;0rad)
  Profile = -> Sketch172
  Suppress = false
  TreeRank = 2978
  Type = 0
  _ProfileBasedVersion = 1
FEATURE [Sketcher::SketchObject] Sketch173
  ArcFitTolerance = 1e-06
  AttachmentSupport = -> [XY_Plane110]
  ExternalGeometry = -> [Pad044]
  FullyConstrained = true
  MapMode = 5
  Support = -> [XY_Plane110]
  TreeRank = 2979
  sketch-geometry (2):
    g0: Circle CenterX=10 CenterY=-13.5 CenterZ=0 NormalX=0 NormalY=0 NormalZ=1 AngleXU=0 Radius=1
    g1: Circle CenterX=-6 CenterY=3.5 CenterZ=0 NormalX=0 NormalY=0 NormalZ=1 AngleXU=0 Radius=1
  constraints (6):
    c: DistanceY(g0,g-3) = 45
    c: DistanceX(g-1,g0) = 10
    c: Radius(g0) = 1
    c: Radius(g1) = 1
    c: DistanceY(g1,g-3) = 28
    c: DistanceX(g1,g-1) = 6
FEATURE [PartDesign::Pocket] Pocket023
  AddSubType = 1
  BaseFeature = -> Pad044
  CheckUpToFaceLimits = true
  ClaimChildren = false
  Fit = 0
  FitJoin = 0
  InnerFit = 0
  InnerFitJoin = 0
  InnerTaperAngle = 0
  InnerTaperAngleRev = 0
  Length = 5
  Length2 = 100
  Linearize = true
  NewSolid = false
  Placement = pos=(5.4e-15,19.5,-5) rot=(0,0,1;0rad)
  Profile = -> Sketch173
  Suppress = false
  TreeRank = 2980
  Type = 0
  _ProfileBasedVersion = 1
  _Version = 1
FEATURE [PartDesign::Fillet] Fillet020
  AddSubType = 0
  Base = -> Pocket023 [Edge2,Edge1,Edge8,Edge5]
  BaseFeature = -> Pocket023
  NewSolid = false
  Placement = pos=(5.4e-15,19.5,-5) rot=(0,0,1;0rad)
  Radius = 2
  SupportTransform = false
  Suppress = false
  TreeRank = 2981
FEATURE [PartDesign::Body] Body099  label="pcb"
  AutoGroupSolids = false
  ClaimAllChildren = false
  ExportMode = 0
  Group = -> [Sketch172,ShapeBinder036,Pad044,Sketch173,Pocket023,Fillet020,Sketch174,DatumPlane056]
  Origin = -> Origin118
  Tip = -> Fillet020
  TreeRank = 2974
  _ExportChildren = -> [ShapeBinder036,Pad044,Pocket023,Fillet020,Sketch174,DatumPlane056]
  _GroupVersion = 1
FEATURE [PartDesign::Chamfer] Chamfer007
  AddSubType = 0
  Angle = 45
  Base = -> Pocket011 [Edge13]
  BaseFeature = -> Pocket011
  ChamferType = 0
  FlipDirection = false
  NewSolid = false
  Size = 2
  Size2 = 1
  SupportTransform = false
  Suppress = false
  TreeRank = 2986
FEATURE [PartDesign::Pocket] Pocket012
  AddSubType = 1
  BaseFeature = -> Chamfer007
  CheckUpToFaceLimits = true
  ClaimChildren = false
  Fit = 0
  FitJoin = 0
  InnerFit = 0
  InnerFitJoin = 0
  InnerTaperAngle = 0
  InnerTaperAngleRev = 0
  Length = 5
  Length2 = 100
  Linearize = true
  NewSolid = false
  Profile = -> Sketch108
  Suppress = false
  TreeRank = 2392
  Type = 0
  _ProfileBasedVersion = 1
  _Version = 1
FEATURE [Sketcher::SketchObject] Sketch177
  ArcFitTolerance = 1e-06
  AttachmentSupport = -> [XY_Plane103]
  ExternalGeometry = -> [ShapeBinder032]
  FullyConstrained = true
  MapMode = 5
  Support = -> [XY_Plane103]
  TreeRank = 2993
  sketch-geometry (4):
    g0: LineSegment StartX=-14 StartY=11 StartZ=0 EndX=-11 EndY=11 EndZ=0
    g1: LineSegment StartX=-11 StartY=11 StartZ=0 EndX=-11 EndY=3 EndZ=0
    g2: LineSegment StartX=-11 StartY=3 StartZ=0 EndX=-14 EndY=3 EndZ=0
    g3: LineSegment StartX=-14 StartY=3 StartZ=0 EndX=-14 EndY=11 EndZ=0
  constraints (11):
    c: Coincident(g0,g1)
    c: Coincident(g1,g2)
    c: Coincident(g2,g3)
    c: Coincident(g3,g0)
    c: Horizontal(g0)
    c: Horizontal(g2)
    c: Vertical(g1)
    c: Vertical(g3)
    c: Coincident(g0,g-4)
    c: DistanceX(g2,g2) = 3
    c: Horizontal(g1,g-4)
FEATURE [PartDesign::Pocket] Pocket026
  AddSubType = 1
  BaseFeature = -> Pocket018
  CheckUpToFaceLimits = true
  ClaimChildren = false
  Fit = 0
  FitJoin = 0
  InnerFit = 0
  InnerFitJoin = 0
  InnerTaperAngle = 0
  InnerTaperAngleRev = 0
  Length = 5
  Length2 = 100
  Linearize = true
  NewSolid = false
  Profile = -> Sketch177
  Suppress = false
  TreeRank = 2994
  Type = 0
  _ProfileBasedVersion = 1
  _Version = 1
FEATURE [PartDesign::Chamfer] Chamfer006
  AddSubType = 0
  Angle = 45
  Base = -> Pocket026 [Edge15,Edge17]
  BaseFeature = -> Pocket026
  ChamferType = 0
  FlipDirection = false
  NewSolid = false
  Size = 2
  Size2 = 1
  SupportTransform = false
  Suppress = false
  TreeRank = 2493
FEATURE [Sketcher::SketchObject] Sketch141
  ArcFitTolerance = 1e-06
  AttachmentSupport = -> [Chamfer006]
  ExternalGeometry = -> [ShapeBinder032]
  FullyConstrained = true
  MapMode = 5
  Placement = pos=(-34,0,0) rot=(0.57735,-0.57735,-0.57735;2.0944rad)
  Support = -> [Chamfer006]
  TreeRank = 2652
  sketch-geometry (1):
    g0: Circle CenterX=-8 CenterY=-2 CenterZ=0 NormalX=0 NormalY=0 NormalZ=1 AngleXU=0 Radius=1
  constraints (3):
    c: DistanceY(g0,g-1) = 2
    c: Diameter(g0) = 2
    c: DistanceX(g0,g-3) = 5
FEATURE [PartDesign::Pocket] Pocket019
  AddSubType = 1
  BaseFeature = -> Chamfer006
  CheckUpToFaceLimits = true
  ClaimChildren = false
  Fit = 0
  FitJoin = 0
  InnerFit = 0
  InnerFitJoin = 0
  InnerTaperAngle = 0
  InnerTaperAngleRev = 0
  Length = 20
  Length2 = 100
  Linearize = true
  NewSolid = false
  Profile = -> Sketch141
  Suppress = false
  TreeRank = 2495
  Type = 0
  _ProfileBasedVersion = 1
  _Version = 1
FEATURE [Sketcher::SketchObject] Sketch142
  ArcFitTolerance = 1e-06
  AttachmentSupport = -> [Pocket019]
  ExternalGeometry = -> [ShapeBinder032]
  FullyConstrained = true
  MapMode = 5
  Placement = pos=(-34,0,0) rot=(0.57735,-0.57735,-0.57735;2.0944rad)
  Support = -> [Pocket019]
  TreeRank = 2653
  sketch-geometry (1):
    g0: Circle CenterX=-8 CenterY=-2 CenterZ=0 NormalX=0 NormalY=0 NormalZ=1 AngleXU=0 Radius=2
  constraints (3):
    c: DistanceY(g0,g-1) = 2
    c: DistanceX(g0,g-3) = 5
    c: Diameter(g0) = 4
FEATURE [PartDesign::Pocket] Pocket020
  AddSubType = 1
  BaseFeature = -> Pocket019
  CheckUpToFaceLimits = true
  ClaimChildren = false
  Fit = 0
  FitJoin = 0
  InnerFit = 0
  InnerFitJoin = 0
  InnerTaperAngle = 0
  InnerTaperAngleRev = 0
  Length = 12
  Length2 = 100
  Linearize = true
  NewSolid = false
  Profile = -> Sketch142
  Suppress = false
  TreeRank = 2497
  Type = 0
  _ProfileBasedVersion = 1
  _Version = 1
FEATURE [Sketcher::SketchObject] Sketch175
  ArcFitTolerance = 1e-06
  AttachmentSupport = -> [Pocket020]
  ExternalGeometry = -> [Pocket020]
  FullyConstrained = true
  MapMode = 5
  Placement = pos=(0,3,0) rot=(1,0,0;1.5708rad)
  Support = -> [Pocket020]
  TreeRank = 2984
  sketch-geometry (3):
    g0: Circle CenterX=-24 CenterY=-8.4 CenterZ=0 NormalX=0 NormalY=0 NormalZ=1 AngleXU=0 Radius=3.8
    g1: Circle CenterX=-15.7151 CenterY=-14 CenterZ=0 NormalX=0 NormalY=0 NormalZ=1 AngleXU=0 Radius=2
    g2: LineSegment [constr] StartX=-24 StartY=-8.4 StartZ=0 EndX=-15.7151 EndY=-14 EndZ=0
  constraints (8):
    c: DistanceX(g0,g-1) = 24
    c: DistanceY(g0,g-1) = 8.4
    c: Radius(g0) = 3.8
    c: Radius(g1) = 2
    c: Coincident(g2,g0)
    c: Coincident(g2,g1)
    c: Distance(g2) = 10
    c: DistanceY(g1,g-1) = 14
FEATURE [PartDesign::Pocket] Pocket024
  AddSubType = 1
  BaseFeature = -> Pocket020
  CheckUpToFaceLimits = true
  ClaimChildren = false
  Fit = 0
  FitJoin = 0
  InnerFit = 0
  InnerFitJoin = 0
  InnerTaperAngle = 0
  InnerTaperAngleRev = 0
  Length = 10
  Length2 = 100
  Linearize = true
  NewSolid = false
  Profile = -> Sketch175
  Suppress = false
  TreeRank = 2985
  Type = 0
  _ProfileBasedVersion = 1
  _Version = 1
FEATURE [PartDesign::Fillet] Fillet023
  AddSubType = 0
  Base = -> Pocket024 [Edge42,Edge40,Edge12,Edge11]
  BaseFeature = -> Pocket024
  NewSolid = false
  Radius = 1.4
  SupportTransform = false
  Suppress = false
  TreeRank = 2992
FEATURE [PartDesign::MultiTransform] MultiTransform004
  AddSubType = 0
  BaseFeature = -> Fillet023
  CopyShape = false
  NewSolid = false
  OriginalSubs = -> [Pocket020,Pocket019,Chamfer006,Pocket018,Pad040,Pocket024,Fillet023,Pocket026]
  Originals = -> [Pocket020,Pocket019,Chamfer006,Pocket018,Pad040,Pocket024,Fillet023,Pocket026]
  ParallelTransform = true
  SubTransform = true
  Suppress = false
  Transformations = -> [Mirrored006,LinearPattern005]
  TreeRank = 2498
  _Version = 3
FEATURE [PartDesign::ShapeBinder] ShapeBinder038
  Placement = pos=(0,0,-5) rot=(0,0,1;0rad)
  Support = -> [Fillet020]
  TraceSupport = false
  TreeRank = 3008
FEATURE [PartDesign::Plane] DatumPlane057
  AttachmentSupport = -> [ShapeBinder038]
  Length = 10
  MapMode = 11
  MinimumLength = 10
  MinimumWidth = 10
  Placement = pos=(-6,3.5,-5) rot=(0,0,1;1.5708rad)
  ResizeMode = 0
  Support = -> [ShapeBinder038]
  TreeRank = 3009
  Width = 10
FEATURE [Part::SubShapeBinder] Import054  label="Import054(MultiTransform004)"
  BindCopyOnChange = 0
  BindMode = 0
  ClaimChildren = false
  Context = -> Part008 [Body100.Import054.]
  FillStyle = 0
  Fuse = false
  MakeFace = false
  OffsetFill = false
  OffsetIntersection = false
  OffsetJoinType = 0
  OffsetOpenResult = false
  PartialLoad = false
  Relative = true
  Support = -> [Body092[MultiTransform004.]]
  TreeRank = 3011
  _Version = 8
FEATURE [Sketcher::SketchObject] Sketch178
  ArcFitTolerance = 1e-06
  AttachmentSupport = -> [DatumPlane057]
  ExternalGeometry = -> [Import054]
  FullyConstrained = false
  MapMode = 5
  Placement = pos=(-6,3.5,-5) rot=(0,0,1;1.5708rad)
  Support = -> [DatumPlane057]
  TreeRank = 3010
  sketch-geometry (5):
    g0: Circle [constr] CenterX=0 CenterY=0 CenterZ=0 NormalX=0 NormalY=0 NormalZ=1 AngleXU=0 Radius=3.5
    g1: LineSegment StartX=-0.5 StartY=5 StartZ=0 EndX=-0.5 EndY=3.4641 EndZ=0
    g2: LineSegment StartX=3.5 StartY=5 StartZ=0 EndX=3.5 EndY=0 EndZ=0
    g3: ArcOfCircle CenterX=0 CenterY=3e-16 CenterZ=0 NormalX=0 NormalY=0 NormalZ=1 AngleXU=0 Radius=3.5 StartAngle=1.71414 EndAngle=6.28319
    g4: LineSegment StartX=-0.5 StartY=5 StartZ=0 EndX=3.5 EndY=5 EndZ=0
  constraints (12):
    c: Coincident(g0,g-1)
    c: Diameter(g0) = 7
    c: Coincident(g1,g-3)
    c: Vertical(g1)
    c: PointOnObject(g2,g-3)
    c: Tangent(g2,g0) = 1.5708
    c: Vertical(g2)
    c: PointOnObject(g1,g0)
    c: Coincident(g3,g1)
    c: Horizontal(g3,g2)
    c: Coincident(g4,g1)
    c: Coincident(g4,g2)
FEATURE [PartDesign::Pad] Pad045
  AddSubType = 0
  AlongSketchNormal = false
  CheckUpToFaceLimits = true
  ClaimChildren = false
  Direction = (-2e-16,2e-16,1)
  Fit = 0
  FitJoin = 0
  InnerFit = 0
  InnerFitJoin = 0
  InnerTaperAngle = 0
  InnerTaperAngleRev = 0
  Length = 20
  Length2 = 100
  Linearize = true
  NewSolid = false
  Placement = pos=(-6,3.5,-5) rot=(0,0,1;1.5708rad)
  Profile = -> Sketch178
  Reversed = true
  Suppress = false
  TreeRank = 3012
  Type = 0
  _ProfileBasedVersion = 1
FEATURE [Sketcher::SketchObject] Sketch179
  ArcFitTolerance = 1e-06
  AttachmentSupport = -> [DatumPlane057]
  FullyConstrained = true
  MapMode = 5
  Placement = pos=(-6,3.5,-5) rot=(0,0,1;1.5708rad)
  Support = -> [DatumPlane057]
  TreeRank = 3013
  sketch-geometry (1):
    g0: Circle CenterX=0 CenterY=0 CenterZ=0 NormalX=0 NormalY=0 NormalZ=1 AngleXU=0 Radius=1.7
  constraints (2):
    c: Coincident(g0,g-1)
    c: Diameter(g0) = 3.4
FEATURE [PartDesign::Pocket] Pocket027
  AddSubType = 1
  BaseFeature = -> Pad045
  CheckUpToFaceLimits = true
  ClaimChildren = false
  Fit = 0
  FitJoin = 0
  InnerFit = 0
  InnerFitJoin = 0
  InnerTaperAngle = 0
  InnerTaperAngleRev = 0
  Length = 4
  Length2 = 100
  Linearize = true
  NewSolid = false
  Placement = pos=(-6,3.5,-5) rot=(0,0,1;1.5708rad)
  Profile = -> Sketch179
  Suppress = false
  TreeRank = 3014
  Type = 0
  _ProfileBasedVersion = 1
  _Version = 1
FEATURE [Sketcher::SketchObject] Sketch181
  ArcFitTolerance = 1e-06
  AttachmentSupport = -> [YZ_Plane113]
  FullyConstrained = true
  MapMode = 5
  Placement = pos=(0,0,0) rot=(0.57735,0.57735,0.57735;2.0944rad)
  Support = -> [YZ_Plane113]
  TreeRank = 3040
  sketch-geometry (1):
    g0: LineSegment StartX=0 StartY=0 StartZ=0 EndX=0 EndY=-23 EndZ=0
  constraints (3):
    c: Coincident(g0,g-1)
    c: PointOnObject(g0,g-2)
    c: DistanceY(g0,g0) = 23
FEATURE [PartDesign::Plane] DatumPlane058
  AttachmentSupport = -> [Sketch181]
  Length = 13
  MapMode = 7
  MinimumLength = 10
  MinimumWidth = 10
  Placement = pos=(5.1e-15,-5.1e-15,-23) rot=(0,0,1;0rad)
  ResizeMode = 0
  Support = -> [Sketch181]
  TreeRank = 3041
  Width = 24
FEATURE [Sketcher::SketchObject] Sketch182
  ArcFitTolerance = 1e-06
  AttachmentSupport = -> [DatumPlane058]
  FullyConstrained = true
  MapMode = 5
  Placement = pos=(5.1e-15,-5.1e-15,-23) rot=(0,0,1;0rad)
  Support = -> [DatumPlane058]
  TreeRank = 3042
  sketch-geometry (13):
    g0: LineSegment StartX=-7.25 StartY=-20 StartZ=0 EndX=7.25 EndY=-20 EndZ=0
    g1: LineSegment StartX=7.25 StartY=-20 StartZ=0 EndX=7.25 EndY=-27.25 EndZ=0
    g2: LineSegment StartX=-7.25 StartY=-27.25 StartZ=0 EndX=-7.25 EndY=-20 EndZ=0
    g3: LineSegment StartX=7.25 StartY=-27.25 StartZ=0 EndX=-7.25 EndY=-27.25 EndZ=0
    g4: LineSegment StartX=0 StartY=-18 StartZ=0 EndX=11.5 EndY=-18 EndZ=0
    g5: LineSegment StartX=15 StartY=-21.5 StartZ=0 EndX=15 EndY=-27.5 EndZ=0
    g6: LineSegment StartX=-8.46891 StartY=-29.25 StartZ=0 EndX=8.46891 EndY=-29.25 EndZ=0
    g7: ArcOfCircle CenterX=11.5 CenterY=-27.5 CenterZ=0 NormalX=0 NormalY=0 NormalZ=1 AngleXU=0 Radius=3.5 StartAngle=3.66519 EndAngle=6.28319
    g8: ArcOfCircle CenterX=11.5 CenterY=-21.5 CenterZ=0 NormalX=0 NormalY=0 NormalZ=1 AngleXU=0 Radius=3.5 StartAngle=6e-16 EndAngle=1.5708
    g9: LineSegment StartX=0 StartY=-18 StartZ=0 EndX=-11.5 EndY=-18 EndZ=0
    g10: LineSegment StartX=-15 StartY=-21.5 StartZ=0 EndX=-15 EndY=-27.5 EndZ=0
    g11: ArcOfCircle CenterX=-11.5 CenterY=-21.5 CenterZ=0 NormalX=0 NormalY=0 NormalZ=1 AngleXU=0 Radius=3.5 StartAngle=1.5708 EndAngle=3.14159
    g12: ArcOfCircle CenterX=-11.5 CenterY=-27.5 CenterZ=0 NormalX=0 NormalY=0 NormalZ=1 AngleXU=0 Radius=3.5 StartAngle=3.14159 EndAngle=5.75959
  constraints (36):
    c: DistanceY(g0,g-1) = 20
    c: Symmetric(g0,g0,g-2)
    c: DistanceX(g0,g0) = 14.5
    c: Coincident(g1,g0)
    c: Coincident(g2,g0)
    c: Vertical(g2)
    c: Vertical(g1)
    c: DistanceY(g1,g1) = 7.25
    c: Coincident(g3,g1)
    c: Coincident(g3,g2)
    c: Horizontal(g3)
    c: Horizontal(g4)
    c: Vertical(g5)
    c: Horizontal(g6)
    c: Coincident(g7,g6)
    c: Tangent(g8,g5) = 1.5708
    c: Tangent(g8,g4) = 1.5708
    c: Tangent(g7,g5) = 1.5708
    c: DistanceY(g0,g4) = 2
    c: PointOnObject(g4,g-2)
    c: DistanceX(g4,g7) = 11.5
    c: Diameter(g7) = 7
    c: DistanceY(g7,g4) = 9.5
    c: DistanceY(g6,g1) = 2
    c: Diameter(g8) = 7
    c: Coincident(g9,g4)
    c: Horizontal(g9)
    c: Vertical(g10)
    c: Coincident(g12,g6)
    c: Diameter(g12) = 7
    c: Diameter(g11) = 7
    c: Tangent(g11,g10) = -1.5708
    c: Tangent(g11,g9) = -1.5708
    c: Tangent(g12,g10) = -1.5708
    c: Equal(g10,g5)
    c: Equal(g9,g4)
FEATURE [Sketcher::SketchObject] Sketch183
  ArcFitTolerance = 1e-06
  AttachmentSupport = -> [DatumPlane058]
  ExternalGeometry = -> [Sketch182]
  FullyConstrained = true
  MapMode = 5
  Placement = pos=(5.1e-15,-5.1e-15,-23) rot=(0,0,1;0rad)
  Support = -> [DatumPlane058]
  TreeRank = 3043
  sketch-geometry (5):
    g0: LineSegment StartX=-9.25 StartY=-18 StartZ=0 EndX=-9.25 EndY=-29.25 EndZ=0
    g1: LineSegment StartX=-9.25 StartY=-29.25 StartZ=0 EndX=9.25 EndY=-29.25 EndZ=0
    g2: LineSegment [constr] StartX=9.25 StartY=-29.25 StartZ=0 EndX=9.25 EndY=-18 EndZ=0
    g3: LineSegment StartX=9.25 StartY=-18 StartZ=0 EndX=0 EndY=-18 EndZ=0
    g4: LineSegment StartX=0 StartY=-18 StartZ=0 EndX=-9.25 EndY=-18 EndZ=0
  constraints (15):
    c: Coincident(g0,g1)
    c: Coincident(g1,g2)
    c: Horizontal(g1)
    c: Vertical(g0)
    c: Vertical(g2)
    c: DistanceX(g-4,g2) = 2
    c: DistanceY(g-4,g2) = 2
    c: DistanceY(g1,g-4) = 2
    c: Coincident(g3,g2)
    c: Horizontal(g3)
    c: Coincident(g4,g3)
    c: Coincident(g4,g0)
    c: Horizontal(g4)
    c: Equal(g4,g3)
    c: PointOnObject(g3,g-2)
FEATURE [PartDesign::ShapeBinder] ShapeBinder039
  Placement = pos=(0,0,-5) rot=(0,0,1;0rad)
  Support = -> [Fillet020]
  TraceSupport = false
  TreeRank = 3048
FEATURE [PartDesign::Plane] DatumPlane059
  AttachmentSupport = -> [ShapeBinder039]
  Length = 10
  MapMode = 11
  MinimumLength = 10
  MinimumWidth = 10
  Placement = pos=(10,-13.5,-5) rot=(0,0,1;1.5708rad)
  ResizeMode = 0
  Support = -> [ShapeBinder039]
  TreeRank = 3049
  Width = 10
FEATURE [Sketcher::SketchObject] Sketch185
  ArcFitTolerance = 1e-06
  AttachmentSupport = -> [DatumPlane059]
  FullyConstrained = true
  MapMode = 5
  Placement = pos=(10,-13.5,-5) rot=(0,0,1;1.5708rad)
  Support = -> [DatumPlane059]
  TreeRank = 3050
  sketch-geometry (1):
    g0: Circle CenterX=0 CenterY=0 CenterZ=0 NormalX=0 NormalY=0 NormalZ=1 AngleXU=0 Radius=3.5
  constraints (2):
    c: Diameter(g0) = 7
    c: Coincident(g0,g-1)
FEATURE [Sketcher::SketchObject] Sketch186
  ArcFitTolerance = 1e-06
  AttachmentSupport = -> [DatumPlane059]
  FullyConstrained = true
  MapMode = 5
  Placement = pos=(10,-13.5,-5) rot=(0,0,1;1.5708rad)
  Support = -> [DatumPlane059]
  TreeRank = 3051
  sketch-geometry (1):
    g0: Circle CenterX=0 CenterY=0 CenterZ=0 NormalX=0 NormalY=0 NormalZ=1 AngleXU=0 Radius=1.7
  constraints (2):
    c: Coincident(g0,g-1)
    c: Diameter(g0) = 3.4
FEATURE [PartDesign::Pad] Pad047
  AddSubType = 0
  AlongSketchNormal = false
  CheckUpToFaceLimits = true
  ClaimChildren = false
  Direction = (-2e-16,2e-16,1)
  Fit = 0
  FitJoin = 0
  InnerFit = 0
  InnerFitJoin = 0
  InnerTaperAngle = 0
  InnerTaperAngleRev = 0
  Length = 23
  Length2 = 100
  Linearize = true
  NewSolid = false
  Placement = pos=(10,-13.5,-5) rot=(0,0,1;1.5708rad)
  Profile = -> Sketch185
  Reversed = true
  Suppress = false
  TreeRank = 3053
  Type = 0
  _ProfileBasedVersion = 1
FEATURE [PartDesign::ShapeBinder] ShapeBinder040
  Support = -> [Body]
  TraceSupport = false
  TreeRank = 3057
FEATURE [Sketcher::SketchObject] Sketch188
  ArcFitTolerance = 1e-06
  AttachmentSupport = -> [XY_Plane088]
  ExternalGeometry = -> [ShapeBinder040]
  FullyConstrained = true
  MapMode = 5
  Support = -> [XY_Plane088]
  TreeRank = 3058
  sketch-geometry (4):
    g0: LineSegment StartX=-29.912 StartY=-74.2447 StartZ=0 EndX=-5.65235 EndY=-74.2447 EndZ=0
    g1: LineSegment StartX=-5.65235 StartY=-74.2447 StartZ=0 EndX=-5.65235 EndY=-96.8671 EndZ=0
    g2: LineSegment StartX=-5.65235 StartY=-96.8671 StartZ=0 EndX=-29.912 EndY=-96.8671 EndZ=0
    g3: LineSegment StartX=-29.912 StartY=-96.8671 StartZ=0 EndX=-29.912 EndY=-74.2447 EndZ=0
  constraints (10):
    c: Coincident(g0,g1)
    c: Coincident(g1,g2)
    c: Coincident(g2,g3)
    c: Coincident(g3,g0)
    c: Horizontal(g0)
    c: Horizontal(g2)
    c: Vertical(g1)
    c: Vertical(g3)
    c: Coincident(g0,g-3)
    c: Coincident(g1,g-4)
FEATURE [PartDesign::ShapeBinder] ShapeBinder041
  Placement = pos=(-34,0,0) rot=(0.57735,-0.57735,-0.57735;2.0944rad)
  Support = -> [Sketch104]
  TraceSupport = false
  TreeRank = 3060
FEATURE [Sketcher::SketchObject] Sketch189
  ArcFitTolerance = 1e-06
  AttachmentSupport = -> [YZ_Plane088]
  ExternalGeometry = -> [ShapeBinder035]
  FullyConstrained = true
  MapMode = 5
  Placement = pos=(0,0,0) rot=(0.57735,0.57735,0.57735;2.0944rad)
  Support = -> [YZ_Plane088]
  TreeRank = 3061
  expr: Constraints[2] = Spreadsheet.side_bar_len
  sketch-geometry (2):
    g0: Circle CenterX=8 CenterY=-2.1 CenterZ=0 NormalX=0 NormalY=0 NormalZ=1 AngleXU=0 Radius=2
    g1: Circle CenterX=-50 CenterY=-2.1 CenterZ=0 NormalX=0 NormalY=0 NormalZ=1 AngleXU=0 Radius=2
  constraints (5):
    c: Coincident(g0,g-3)
    c: Horizontal(g0,g1)
    c: DistanceX(g1,g0) = 58
    c: Radius(g0) = 2
    c: Equal(g1,g0)
FEATURE [PartDesign::Pad] Pad049
  AddSubType = 0
  AlongSketchNormal = false
  CheckUpToFaceLimits = true
  ClaimChildren = false
  Direction = (0,0,1)
  Fit = 0
  FitJoin = 0
  InnerFit = 0
  InnerFitJoin = 0
  InnerTaperAngle = 0
  InnerTaperAngleRev = 0
  Length = 11.5
  Length2 = 100
  Linearize = true
  NewSolid = false
  Placement = pos=(5.1e-15,-5.1e-15,-23) rot=(0,0,1;0rad)
  Profile = -> Sketch182
  Suppress = false
  TreeRank = 3063
  Type = 0
  _ProfileBasedVersion = 1
FEATURE [Part::SubShapeBinder] Import055  label="Import055(Sketch182)"
  BindCopyOnChange = 0
  BindMode = 0
  ClaimChildren = false
  Context = -> Part008 [Body101.Import055.]
  FillStyle = 0
  Fuse = false
  MakeFace = false
  OffsetFill = false
  OffsetIntersection = false
  OffsetJoinType = 0
  OffsetOpenResult = false
  PartialLoad = false
  Relative = true
  Support = -> [Body102[Sketch182.]]
  TreeRank = 3068
  _Version = 8
FEATURE [Sketcher::SketchObject] Sketch187
  ArcFitTolerance = 1e-06
  AttachmentSupport = -> [Pad047]
  ExternalGeometry = -> [Pad047,Import055]
  FullyConstrained = true
  MapMode = 5
  Placement = pos=(10,-13.5,-28) rot=(0.707107,0.707107,0;3.14159rad)
  Support = -> [Pad047]
  TreeRank = 3054
  sketch-geometry (4):
    g0: LineSegment StartX=-6.5 StartY=-3.5 StartZ=0 EndX=-6.5 EndY=3.5 EndZ=0
    g1: LineSegment StartX=-6.5 StartY=3.5 StartZ=0 EndX=5.3e-15 EndY=3.5 EndZ=0
    g2: LineSegment StartX=5.8e-15 StartY=-3.5 StartZ=0 EndX=5.8e-15 EndY=3.5 EndZ=0
    g3: LineSegment StartX=-6.5 StartY=-3.5 StartZ=0 EndX=5.3e-15 EndY=-3.5 EndZ=0
  constraints (11):
    c: PointOnObject(g2,g-3)
    c: Vertical(g0)
    c: Coincident(g1,g0)
    c: Horizontal(g1)
    c: Tangent(g1,g-3) = 1.5708
    c: Coincident(g2,g1)
    c: Coincident(g3,g0)
    c: Coincident(g3,g2)
    c: Vertical(g2)
    c: Vertical(g0,g-4)
    c: Horizontal(g3)
FEATURE [PartDesign::Pad] Pad048
  AddSubType = 0
  AlongSketchNormal = false
  BaseFeature = -> Pad047
  CheckUpToFaceLimits = true
  ClaimChildren = false
  Direction = (2e-16,-3e-16,-1)
  Fit = 0
  FitJoin = 0
  InnerFit = 0
  InnerFitJoin = 0
  InnerTaperAngle = 0
  InnerTaperAngleRev = 0
  Length = 16.5
  Length2 = 100
  Linearize = true
  NewSolid = false
  Placement = pos=(10,-13.5,-5) rot=(0,0,1;1.5708rad)
  Profile = -> Sketch187
  Reversed = true
  Suppress = false
  TreeRank = 3055
  Type = 0
  _ProfileBasedVersion = 1
FEATURE [PartDesign::Pocket] Pocket030
  AddSubType = 1
  BaseFeature = -> Pad048
  CheckUpToFaceLimits = true
  ClaimChildren = false
  Fit = 0
  FitJoin = 0
  InnerFit = 0
  InnerFitJoin = 0
  InnerTaperAngle = 0
  InnerTaperAngleRev = 0
  Length = 4
  Length2 = 100
  Linearize = true
  NewSolid = false
  Placement = pos=(10,-13.5,-5) rot=(0,0,1;1.5708rad)
  Profile = -> Sketch186
  Suppress = false
  TreeRank = 3056
  Type = 0
  _ProfileBasedVersion = 1
  _Version = 1
FEATURE [PartDesign::Mirrored] Mirrored008
  AddSubType = 0
  CopyShape = false
  MirrorPlane = -> YZ_Plane088
  NewSolid = false
  ParallelTransform = true
  Placement = pos=(0,17,0) rot=(1,0,0;1.5708rad)
  SubTransform = true
  Suppress = false
  TreeRank = 3072
  _Version = 3
FEATURE [PartDesign::LinearPattern] LinearPattern013
  AddSubType = 0
  CopyShape = false
  Direction = -> Sketch153 [H_Axis]
  Length = 58
  NewSolid = false
  Occurrences = 2
  ParallelTransform = true
  Placement = pos=(0,17,0) rot=(1,0,0;1.5708rad)
  SubTransform = true
  Suppress = false
  TreeRank = 3073
  _Version = 3
  expr: Length = Spreadsheet.side_bar_len
FEATURE [PartDesign::MultiTransform] MultiTransform009
  AddSubType = 0
  BaseFeature = -> Pocket022
  CopyShape = false
  NewSolid = false
  OriginalSubs = -> [Pocket022]
  Originals = -> [Pocket022]
  ParallelTransform = true
  Placement = pos=(0,17,0) rot=(1,0,0;1.5708rad)
  SubTransform = true
  Suppress = false
  Transformations = -> [Mirrored008,LinearPattern013]
  TreeRank = 3074
  _Version = 3
FEATURE [PartDesign::Fillet] Fillet024
  AddSubType = 0
  Base = -> Clone032 [Edge3]
  BaseFeature = -> Clone032
  NewSolid = false
  Placement = pos=(0,17,0) rot=(1,0,0;1.5708rad)
  Radius = 16
  SupportTransform = false
  Suppress = false
  TreeRank = 3075
FEATURE [PartDesign::Body] Body003  label="body master"
  AutoGroupSolids = false
  BaseFeature = -> Revolution007
  ClaimAllChildren = false
  ExportMode = 0
  Group = -> [Clone032,Fillet024]
  Origin = -> Origin004
  Placement = pos=(0,0,0.1) rot=(0,0,1;0rad)
  Tip = -> Fillet024
  TreeRank = 2070
  _ExportChildren = -> [Clone032,Fillet024]
  _GroupVersion = 1
FEATURE [PartDesign::SubShapeBinder] Reference  label="Reference(body master)"
  BindCopyOnChange = 0
  BindMode = 0
  ClaimChildren = false
  FillStyle = 0
  Fuse = true
  MakeFace = true
  OffsetFill = false
  OffsetIntersection = false
  OffsetJoinType = 0
  OffsetOpenResult = false
  PartialLoad = false
  Relative = true
  Support = -> [Body003]
  TreeRank = 3077
  _Version = 8
FEATURE [PartDesign::Boolean] Boolean
  BaseFeature = -> MultiTransform004
  ClaimAllChildren = false
  ExportMode = 0
  Group = -> [Reference]
  NewSolid = false
  Suppress = false
  TreeRank = 3076
  Type = 2
  _ExportChildren = -> [Reference]
  _GroupVersion = 1
FEATURE [PartDesign::Body] Body092  label="bottom screw support"
  AutoGroupSolids = false
  ClaimAllChildren = false
  ExportMode = 0
  Group = -> [ShapeBinder032,Sketch138,Pad040,Sketch140,Pocket018,Pocket026,Chamfer006,Sketch141,Pocket019,Sketch142,Pocket020,Sketch175,Pocket024,Fillet023,MultiTransform004,Mirrored006,LinearPattern005,Sketch177,Boolean]
  Origin = -> Origin111
  Tip = -> Boolean
  TreeRank = 2486
  _ExportChildren = -> [ShapeBinder032,Pad040,Pocket018,Pocket026,Chamfer006,Pocket019,Pocket020,Pocket024,Fillet023,MultiTransform004,Boolean]
  _GroupVersion = 1
FEATURE [PartDesign::SubShapeBinder] Reference001  label="Reference001(body master)"
  BindCopyOnChange = 0
  BindMode = 0
  ClaimChildren = false
  FillStyle = 0
  Fuse = true
  MakeFace = true
  OffsetFill = false
  OffsetIntersection = false
  OffsetJoinType = 0
  OffsetOpenResult = false
  PartialLoad = false
  Relative = true
  Support = -> [Body003]
  TreeRank = 3079
  _Version = 8
FEATURE [PartDesign::Boolean] Boolean001
  BaseFeature = -> Mirrored007
  ClaimAllChildren = false
  ExportMode = 0
  Group = -> [Reference001]
  NewSolid = false
  Suppress = false
  TreeRank = 3078
  Type = 2
  _ExportChildren = -> [Reference001]
  _GroupVersion = 1
FEATURE [PartDesign::Pad] Pad050
  AddSubType = 0
  AlongSketchNormal = false
  BaseFeature = -> Boolean001
  CheckUpToFaceLimits = true
  ClaimChildren = false
  Direction = (0,1e-16,1)
  Fit = 0
  FitJoin = 0
  InnerFit = 0
  InnerFitJoin = 0
  InnerTaperAngle = 0
  InnerTaperAngleRev = 0
  Length = 1
  Length2 = 100
  Linearize = true
  NewSolid = false
  Profile = -> Boolean001 [Face26,Face21,Face34,Face40,Face10,Face15,Face4,Face46,Face52,Face57,Face82,Face76,Face63,Face68]
  Suppress = false
  TreeRank = 3080
  Type = 0
  _ProfileBasedVersion = 1
FEATURE [PartDesign::Body] Body093  label="bottom alignment"
  AutoGroupSolids = false
  ClaimAllChildren = false
  ExportMode = 0
  Group = -> [Sketch151,Import047,Pad041,Mirrored007,Boolean001,Pad050]
  Origin = -> Origin112
  Tip = -> Pad050
  TreeRank = 3066
  _ExportChildren = -> [Sketch151,Pad041,Mirrored007,Boolean001,Pad050]
  _GroupVersion = 1
FEATURE [PartDesign::SubShapeBinder] Reference002  label="Reference002(body master)"
  BindCopyOnChange = 0
  BindMode = 0
  ClaimChildren = false
  FillStyle = 0
  Fuse = true
  MakeFace = true
  OffsetFill = false
  OffsetIntersection = false
  OffsetJoinType = 0
  OffsetOpenResult = false
  PartialLoad = false
  Relative = true
  Support = -> [Body003]
  TreeRank = 3082
  _Version = 8
FEATURE [PartDesign::Boolean] Boolean002
  BaseFeature = -> Pocket027
  ClaimAllChildren = false
  ExportMode = 0
  Group = -> [Reference002]
  NewSolid = false
  Suppress = false
  TreeRank = 3081
  Type = 2
  _ExportChildren = -> [Reference002]
  _GroupVersion = 1
FEATURE [PartDesign::Body] Body100  label="pcb support"
  AutoGroupSolids = false
  ClaimAllChildren = false
  ExportMode = 0
  Group = -> [ShapeBinder038,DatumPlane057,Sketch178,Import054,Pad045,Sketch179,Pocket027,Boolean002]
  Origin = -> Origin119
  Tip = -> Boolean002
  TreeRank = 3006
  _ExportChildren = -> [ShapeBinder038,DatumPlane057,Import054,Pad045,Pocket027,Boolean002]
  _GroupVersion = 1
FEATURE [PartDesign::SubShapeBinder] Reference003  label="Reference003(body master)"
  BindCopyOnChange = 0
  BindMode = 0
  ClaimChildren = false
  FillStyle = 0
  Fuse = true
  MakeFace = true
  OffsetFill = false
  OffsetIntersection = false
  OffsetJoinType = 0
  OffsetOpenResult = false
  PartialLoad = false
  Relative = true
  Support = -> [Body003]
  TreeRank = 3084
  _Version = 8
FEATURE [PartDesign::Boolean] Boolean003
  BaseFeature = -> Pocket030
  ClaimAllChildren = false
  ExportMode = 0
  Group = -> [Reference003]
  NewSolid = false
  Suppress = false
  TreeRank = 3083
  Type = 2
  _ExportChildren = -> [Reference003]
  _GroupVersion = 1
FEATURE [PartDesign::Body] Body101  label="pcb support2"
  AutoGroupSolids = false
  ClaimAllChildren = false
  ExportMode = 0
  Group = -> [ShapeBinder039,DatumPlane059,Sketch185,Sketch186,Pad047,Sketch187,Pad048,Pocket030,Import055,Boolean003]
  Origin = -> Origin120
  Tip = -> Boolean003
  TreeRank = 3026
  _ExportChildren = -> [ShapeBinder039,DatumPlane059,Pad047,Pad048,Pocket030,Import055,Boolean003]
  _GroupVersion = 1
FEATURE [PartDesign::SubShapeBinder] Reference004  label="Reference004(body master)"
  BindCopyOnChange = 0
  BindMode = 0
  ClaimChildren = false
  FillStyle = 0
  Fuse = true
  MakeFace = true
  OffsetFill = false
  OffsetIntersection = false
  OffsetJoinType = 0
  OffsetOpenResult = false
  PartialLoad = false
  Relative = true
  Support = -> [Body003]
  TreeRank = 3086
  _Version = 8
FEATURE [PartDesign::SubShapeBinder] Reference005  label="Reference005(bottom screw support)"
  BindCopyOnChange = 0
  BindMode = 0
  ClaimChildren = false
  FillStyle = 0
  Fuse = true
  MakeFace = true
  OffsetFill = false
  OffsetIntersection = false
  OffsetJoinType = 0
  OffsetOpenResult = false
  PartialLoad = false
  Relative = true
  Support = -> [Body092]
  TreeRank = 3088
  _Version = 8
FEATURE [PartDesign::SubShapeBinder] Reference006  label="Reference006(bottom alignment)"
  BindCopyOnChange = 0
  BindMode = 0
  ClaimChildren = false
  FillStyle = 0
  Fuse = true
  MakeFace = true
  OffsetFill = false
  OffsetIntersection = false
  OffsetJoinType = 0
  OffsetOpenResult = false
  PartialLoad = false
  Relative = true
  Support = -> [Body093]
  TreeRank = 3089
  _Version = 8
FEATURE [PartDesign::SubShapeBinder] Reference007  label="Reference007(pcb support)"
  BindCopyOnChange = 0
  BindMode = 0
  ClaimChildren = false
  FillStyle = 0
  Fuse = true
  MakeFace = true
  OffsetFill = false
  OffsetIntersection = false
  OffsetJoinType = 0
  OffsetOpenResult = false
  PartialLoad = false
  Relative = true
  Support = -> [Body100]
  TreeRank = 3090
  _Version = 8
FEATURE [PartDesign::SubShapeBinder] Reference008  label="Reference008(pcb support2)"
  BindCopyOnChange = 0
  BindMode = 0
  ClaimChildren = false
  FillStyle = 0
  Fuse = true
  MakeFace = true
  OffsetFill = false
  OffsetIntersection = false
  OffsetJoinType = 0
  OffsetOpenResult = false
  PartialLoad = false
  Relative = true
  Support = -> [Body101]
  TreeRank = 3091
  _Version = 8
FEATURE [PartDesign::SubShapeBinder] Reference009  label="Reference009(usb port)"
  BindCopyOnChange = 0
  BindMode = 0
  ClaimChildren = false
  FillStyle = 0
  Fuse = true
  MakeFace = true
  OffsetFill = false
  OffsetIntersection = false
  OffsetJoinType = 0
  OffsetOpenResult = false
  PartialLoad = false
  Relative = true
  Support = -> [Body102]
  TreeRank = 3092
  _Version = 8
FEATURE [PartDesign::Boolean] Boolean005
  BaseFeature = -> MultiTransform009
  ClaimAllChildren = false
  ExportMode = 0
  Group = -> [Reference005,Reference006,Reference007,Reference008,Reference009]
  NewSolid = false
  Suppress = false
  TreeRank = 3087
  Type = 0
  _ExportChildren = -> [Reference005,Reference006,Reference007,Reference008,Reference009]
  _GroupVersion = 1
FEATURE [PartDesign::Pocket] Pocket031
  AddSubType = 1
  BaseFeature = -> Boolean005
  CheckUpToFaceLimits = true
  ClaimChildren = false
  Fit = 0
  FitJoin = 0
  InnerFit = 0
  InnerFitJoin = 0
  InnerTaperAngle = 0
  InnerTaperAngleRev = 0
  Length = 13
  Length2 = 100
  Linearize = true
  NewSolid = false
  Profile = -> Sketch153
  Suppress = false
  TreeRank = 3093
  Type = 0
  _ProfileBasedVersion = 1
  _Version = 1
FEATURE [PartDesign::Mirrored] Mirrored011
  AddSubType = 0
  CopyShape = false
  MirrorPlane = -> YZ_Plane088
  NewSolid = false
  ParallelTransform = true
  SubTransform = true
  Suppress = false
  TreeRank = 3095
  _Version = 3
FEATURE [PartDesign::LinearPattern] LinearPattern014
  AddSubType = 0
  CopyShape = false
  Direction = -> Y_Axis088
  Length = 58
  NewSolid = false
  Occurrences = 2
  ParallelTransform = true
  Reversed = true
  SubTransform = true
  Suppress = false
  TreeRank = 3096
  _Version = 3
  expr: Length = Spreadsheet.side_bar_len
FEATURE [PartDesign::MultiTransform] MultiTransform010
  AddSubType = 0
  BaseFeature = -> Pocket031
  CopyShape = false
  NewSolid = false
  OriginalSubs = -> [Pocket031]
  Originals = -> [Pocket031]
  ParallelTransform = true
  SubTransform = true
  Suppress = false
  Transformations = -> [Mirrored011,LinearPattern014]
  TreeRank = 3094
  _Version = 3
FEATURE [PartDesign::LinearPattern] LinearPattern015
  AddSubType = 0
  BaseFeature = -> MultiTransform010
  CopyShape = false
  Direction = -> Sketch145 [H_Axis]
  Length = 64
  NewSolid = false
  Occurrences = 3
  OriginalSubs = -> [Groove001]
  Originals = -> [Groove001]
  ParallelTransform = true
  Reversed = true
  SubTransform = true
  Suppress = false
  TreeRank = 3097
  _Version = 3
  expr: Length = Spreadsheet.bottom_groove_len
FEATURE [Part::SubShapeBinder] Import056  label="Import056(Sketch182)"
  BindCopyOnChange = 0
  BindMode = 0
  ClaimChildren = false
  Context = -> Part008 [Body080.Import056.]
  FillStyle = 0
  Fuse = false
  MakeFace = false
  OffsetFill = false
  OffsetIntersection = false
  OffsetJoinType = 0
  OffsetOpenResult = false
  PartialLoad = false
  Relative = true
  Support = -> [Body102[Sketch182.]]
  TreeRank = 3102
  _Version = 8
FEATURE [Sketcher::SketchObject] Sketch190
  ArcFitTolerance = 1e-06
  AttachmentSupport = -> [XY_Plane088]
  ExternalGeometry = -> [Import056]
  FullyConstrained = true
  MapMode = 5
  Support = -> [XY_Plane088]
  TreeRank = 3098
  sketch-geometry (8):
    g0: LineSegment StartX=-6.5 StartY=-20.815 StartZ=0 EndX=0 EndY=-20.815 EndZ=0
    g1: LineSegment StartX=0 StartY=-20.815 StartZ=0 EndX=6.5 EndY=-20.815 EndZ=0
    g2: LineSegment StartX=6.5 StartY=-26.435 StartZ=0 EndX=-6.5 EndY=-26.435 EndZ=0
    g3: LineSegment StartX=-6.5 StartY=-26.435 StartZ=0 EndX=-6.5 EndY=-20.815 EndZ=0
    g4: LineSegment [constr] StartX=7.25 StartY=-20 StartZ=0 EndX=7.25 EndY=-23.625 EndZ=0
    g5: LineSegment [constr] StartX=7.25 StartY=-23.625 StartZ=0 EndX=7.25 EndY=-27.25 EndZ=0
    g6: LineSegment StartX=6.5 StartY=-20.815 StartZ=0 EndX=6.5 EndY=-23.625 EndZ=0
    g7: LineSegment StartX=6.5 StartY=-23.625 StartZ=0 EndX=6.5 EndY=-26.435 EndZ=0
  constraints (23):
    c: PointOnObject(g0,g-2)
    c: Horizontal(g0)
    c: Coincident(g0,g1)
    c: Horizontal(g1)
    c: Horizontal(g2)
    c: Coincident(g2,g3)
    c: Coincident(g3,g0)
    c: Vertical(g3)
    c: Equal(g1,g0)
    c: Coincident(g5,g4)
    c: Vertical(g4)
    c: Equal(g4,g5)
    c: Coincident(g6,g1)
    c: Vertical(g6)
    c: Coincident(g7,g6)
    c: Coincident(g7,g2)
    c: Vertical(g7)
    c: Equal(g6,g7)
    c: Horizontal(g4,g6)
    c: DistanceX(g2,g2) = 13
    c: DistanceY(g3,g3) = 5.62
    c: Coincident(g-4,g4)
    c: Coincident(g-4,g5)
FEATURE [PartDesign::Pocket] Pocket032
  AddSubType = 1
  BaseFeature = -> LinearPattern015
  CheckUpToFaceLimits = true
  ClaimChildren = false
  Fit = 0
  FitJoin = 0
  InnerFit = 0
  InnerFitJoin = 0
  InnerTaperAngle = 0
  InnerTaperAngleRev = 0
  Length = 24
  Length2 = 100
  Linearize = true
  NewSolid = false
  Profile = -> Sketch190
  Suppress = false
  TreeRank = 3099
  Type = 0
  _ProfileBasedVersion = 1
  _Version = 1
FEATURE [Sketcher::SketchObject] Sketch191
  ArcFitTolerance = 1e-06
  AttachmentSupport = -> [XY_Plane088]
  ExternalGeometry = -> [Import056]
  FullyConstrained = true
  MapMode = 5
  Support = -> [XY_Plane088]
  TreeRank = 3100
  sketch-geometry (4):
    g0: LineSegment StartX=7.25 StartY=-20 StartZ=0 EndX=-7.25 EndY=-20 EndZ=0
    g1: LineSegment StartX=-7.25 StartY=-20 StartZ=0 EndX=-7.25 EndY=-27.25 EndZ=0
    g2: LineSegment StartX=-7.25 StartY=-27.25 StartZ=0 EndX=7.25 EndY=-27.25 EndZ=0
    g3: LineSegment StartX=7.25 StartY=-27.25 StartZ=0 EndX=7.25 EndY=-20 EndZ=0
  constraints (10):
    c: Coincident(g0,g1)
    c: Coincident(g1,g2)
    c: Coincident(g2,g3)
    c: Coincident(g3,g0)
    c: Horizontal(g0)
    c: Horizontal(g2)
    c: Vertical(g1)
    c: Vertical(g3)
    c: Coincident(g0,g-3)
    c: Coincident(g2,g-4)
FEATURE [PartDesign::Pocket] Pocket033
  AddSubType = 1
  BaseFeature = -> Pocket032
  CheckUpToFaceLimits = true
  ClaimChildren = false
  Fit = 0
  FitJoin = 0
  InnerFit = 0
  InnerFitJoin = 0
  InnerTaperAngle = 0
  InnerTaperAngleRev = 0
  Length = 22
  Length2 = 100
  Linearize = true
  NewSolid = false
  Profile = -> Sketch191
  Suppress = false
  TreeRank = 3101
  Type = 0
  _ProfileBasedVersion = 1
  _Version = 1
FEATURE [PartDesign::SubShapeBinder] Reference010  label="Reference010(tail fin cutout)"
  BindCopyOnChange = 0
  BindMode = 0
  ClaimChildren = false
  FillStyle = 0
  Fuse = true
  MakeFace = true
  OffsetFill = false
  OffsetIntersection = false
  OffsetJoinType = 0
  OffsetOpenResult = false
  PartialLoad = false
  Relative = true
  Support = -> [Body096]
  TreeRank = 3104
  _Version = 8
FEATURE [PartDesign::Boolean] Boolean006
  BaseFeature = -> Pocket033
  ClaimAllChildren = false
  ExportMode = 0
  Group = -> [Reference010]
  NewSolid = false
  Suppress = false
  TreeRank = 3103
  Type = 1
  _ExportChildren = -> [Reference010]
  _GroupVersion = 1
FEATURE [PartDesign::Body] Body080  label="main bottom body"
  AutoGroupSolids = false
  ClaimAllChildren = false
  ExportMode = 0
  Group = -> [Sketch111,Sketch001,DatumPlane029,Sketch002,DatumPlane030,Sketch003,DatumPlane031,Sketch004,Loft,Loft001,DatumPlane032,Sketch005,DatumPlane033,Sketch006,DatumLine008,Loft002,Revolution007,Sketch114,Groove,Sketch115,Sketch116,Loft003,Sketch117,Loft004,Sketch118,Sketch119,DatumPlane034,Loft005,Fillet014,Fillet015,Chamfer003,Sketch120,Sketch130,DatumPlane035,DatumPlane036,DatumPlane037,DatumPlane039,+73 more]
  Origin = -> Origin001
  Tip = -> Boolean006
  TreeRank = 2067
  _ExportChildren = -> [Sketch111,Sketch001,DatumPlane029,DatumPlane030,DatumPlane031,Loft,Loft001,DatumPlane032,DatumPlane033,DatumLine008,Loft002,Revolution007,Groove,Loft003,Loft004,Sketch119,DatumPlane034,Loft005,Fillet014,Fillet015,Chamfer003,Sketch120,Sketch130,DatumPlane035,DatumPlane036,DatumPlane037,DatumPlane039,Sketch131,Pad037,Sketch132,DatumPlane040,Sketch133,Pocket017,Pad039,Pocket016,DatumLine009,+41 more]
  _GroupVersion = 1
FEATURE [App::Part] Part012  label="groove cutout"
  ClaimAllChildren = false
  ExportMode = 1
  Group = -> [Body056,Body013,Body007,Body008,Body012,Body009,Body006,Body005]
  Origin = -> Origin125
  TreeRank = 3348
  _ExportChildren = -> [Body056,Body013,Body007,Body008,Body012,Body009,Body006,Body005]
  _GroupVersion = 1
FEATURE [PartDesign::FeatureBase] Clone043
  BaseFeature = -> Body
  NewSolid = false
  Suppress = false
  TreeRank = 3381
FEATURE [PartDesign::Body] Body104  label="top master cutout"
  AutoGroupSolids = false
  BaseFeature = -> Body
  ClaimAllChildren = false
  ExportMode = 0
  Group = -> [Clone043]
  Origin = -> Origin126
  Placement = pos=(0,0,-0.1) rot=(0,0,1;0rad)
  Tip = -> Clone043
  TreeRank = 3383
  _ExportChildren = -> [Clone043]
  _GroupVersion = 1
FEATURE [PartDesign::LinearPattern] LinearPattern016
  AddSubType = 0
  CopyShape = false
  Direction = -> Y_Axis033
  Length = 18
  NewSolid = false
  Occurrences = 2
  ParallelTransform = true
  Placement = pos=(0,0,0) rot=(1,0,0;1.5708rad)
  Reversed = true
  SubTransform = true
  Suppress = false
  TreeRank = 3395
  _Version = 3
FEATURE [PartDesign::LinearPattern] LinearPattern017
  AddSubType = 0
  CopyShape = false
  Direction = -> X_Axis033
  Length = 66
  NewSolid = false
  Occurrences = 2
  ParallelTransform = true
  Placement = pos=(0,0,0) rot=(1,0,0;1.5708rad)
  SubTransform = true
  Suppress = false
  TreeRank = 3397
  _Version = 3
FEATURE [PartDesign::MultiTransform] MultiTransform011
  AddSubType = 0
  BaseFeature = -> Pad009
  CopyShape = false
  NewSolid = false
  ParallelTransform = true
  Placement = pos=(0,0,0) rot=(1,0,0;1.5708rad)
  SubTransform = true
  Suppress = false
  Transformations = -> [LinearPattern016,LinearPattern017]
  TreeRank = 3396
  _Version = 3
FEATURE [PartDesign::Body] Body031  label="cylinder"
  AutoGroupSolids = false
  ClaimAllChildren = false
  ExportMode = 0
  Group = -> [Sketch041,Pad009,MultiTransform011,LinearPattern016,LinearPattern017]
  Origin = -> Origin033
  Placement = pos=(-33,25,12) rot=(0,0,1;0rad)
  Tip = -> MultiTransform011
  TreeRank = 3389
  _ExportChildren = -> [Pad009,MultiTransform011]
  _GroupVersion = 1
FEATURE [PartDesign::PolarPattern] PolarPattern007
  AddSubType = 0
  Angle = 180
  Axis = -> Z_Axis054
  BaseFeature = -> Pad018
  CopyShape = false
  NewSolid = false
  Occurrences = 2
  OriginalSubs = -> [Pad018,Pad017]
  Originals = -> [Pad018,Pad017]
  ParallelTransform = true
  SubTransform = true
  Suppress = false
  TreeRank = 3400
  _Version = 3
FEATURE [PartDesign::Body] Body051  label="emboss cutout"
  AutoGroupSolids = false
  ClaimAllChildren = false
  ExportMode = 0
  Group = -> [Import020,Sketch074,Sketch075,Sketch076,Pad017,Pad018,PolarPattern007]
  Origin = -> Origin054
  Placement = pos=(0,13,8) rot=(0,0,1;0rad)
  Tip = -> PolarPattern007
  TreeRank = 3311
  _ExportChildren = -> [Import020,Sketch076,Pad017,Pad018,PolarPattern007]
  _GroupVersion = 1
FEATURE [Part::Cut] Cut004
  Base = -> Cut003
  Tool = -> Body044
  TreeRank = 980
FEATURE [Sketcher::SketchObject] Sketch064
  ArcFitTolerance = 1e-06
  AttachmentSupport = -> [Cut004]
  ExternalGeometry = -> [Import012]
  FullyConstrained = true
  MapMode = 5
  Placement = pos=(0,0,14) rot=(0,0,1;0rad)
  Support = -> [Cut004]
  TreeRank = 1014
  expr: Constraints[1] = 9 + 2
  sketch-geometry (1):
    g0: Circle CenterX=0 CenterY=19.5 CenterZ=0 NormalX=0 NormalY=0 NormalZ=1 AngleXU=0 Radius=11
  constraints (3):
    c: PointOnObject(g0,g-2)
    c: Radius(g0) = 11
    c: DistanceY(g0,g-3) = 34
FEATURE [PartDesign::ShapeBinder] ShapeBinder020
  Support = -> [Cut004]
  TraceSupport = false
  TreeRank = 1033
FEATURE [PartDesign::Body] Body047  label="card cutout"
  AutoGroupSolids = false
  ClaimAllChildren = false
  ExportMode = 0
  Group = -> [Import013,Sketch065,ShapeBinder020,Pad013]
  Origin = -> Origin050
  Tip = -> Pad013
  TreeRank = 1028
  _ExportChildren = -> [Import013,ShapeBinder020,Pad013]
  _GroupVersion = 1
FEATURE [PartDesign::Pad] Pad016
  AddSubType = 0
  AlongSketchNormal = false
  CheckUpToFaceLimits = true
  ClaimChildren = false
  Direction = (0,0,1)
  Fit = 0
  FitJoin = 0
  InnerFit = 0
  InnerFitJoin = 0
  InnerTaperAngle = 0
  InnerTaperAngleRev = 0
  Length = 5
  Length2 = 100
  Linearize = true
  NewSolid = false
  Profile = -> Sketch064
  Reversed = true
  Suppress = false
  TreeRank = 1122
  Type = 0
  _ProfileBasedVersion = 1
FEATURE [PartDesign::Body] Body046  label="joystick hole"
  AutoGroupSolids = false
  ClaimAllChildren = false
  ExportMode = 0
  Group = -> [Sketch064,Import012,Pad016]
  Origin = -> Origin049
  Tip = -> Pad016
  TreeRank = 3262
  _ExportChildren = -> [Import012,Pad016]
  _GroupVersion = 1
FEATURE [PartDesign::FeatureBase] Clone024
  BaseFeature = -> Cut004
  NewSolid = false
  Suppress = false
  TreeRank = 1550
FEATURE [PartDesign::Body] Body067  label="top shell w/0 card slot"
  AutoGroupSolids = false
  BaseFeature = -> Cut004
  ClaimAllChildren = false
  ExportMode = 0
  Group = -> [Clone024]
  Origin = -> Origin073
  Tip = -> Clone024
  TreeRank = 1552
  _ExportChildren = -> [Clone024]
  _GroupVersion = 1
FEATURE [Part::Cut] Cut024  label="bottom groove support"
  Base = -> Body065
  Tool = -> Body067
  TreeRank = 3176
FEATURE [PartDesign::FeatureBase] Clone025
  BaseFeature = -> Cut024
  NewSolid = false
  Suppress = false
  TreeRank = 1563
FEATURE [PartDesign::Body] Body068  label="middle groove support"
  AutoGroupSolids = false
  BaseFeature = -> Cut024
  ClaimAllChildren = false
  ExportMode = 0
  Group = -> [Clone025]
  Origin = -> Origin074
  Placement = pos=(0,37,0) rot=(0,0,1;0rad)
  Tip = -> Clone025
  TreeRank = 3184
  _ExportChildren = -> [Clone025]
  _GroupVersion = 1
FEATURE [Part::Cut] Cut005  label="basic top shell"
  Base = -> Cut004
  Tool = -> Body047
  TreeRank = 3416
FEATURE [Sketcher::SketchObject] Sketch070
  ArcFitTolerance = 1e-06
  AttachmentSupport = -> [Cut005]
  ExternalGeometry = -> [Import017]
  FullyConstrained = true
  MapMode = 5
  Placement = pos=(0,0,14) rot=(0,0,1;0rad)
  Support = -> [Cut005]
  TreeRank = 1093
  expr: Constraints[1] = 9 + 2
  sketch-geometry (1):
    g0: Circle CenterX=0 CenterY=19.5 CenterZ=0 NormalX=0 NormalY=0 NormalZ=1 AngleXU=0 Radius=11
  constraints (2):
    c: Coincident(g0,g-3)
    c: Radius(g0) = 11
FEATURE [PartDesign::Pad] Pad014
  AddSubType = 0
  AlongSketchNormal = false
  CheckUpToFaceLimits = true
  ClaimChildren = false
  Direction = (0,0,1)
  Fit = 0
  FitJoin = 0
  InnerFit = 0
  InnerFitJoin = 0
  InnerTaperAngle = 0
  InnerTaperAngleRev = 0
  Length = 1
  Length2 = 100
  Linearize = true
  NewSolid = false
  Profile = -> Sketch070
  Reversed = true
  Suppress = false
  TreeRank = 1095
  Type = 0
  _ProfileBasedVersion = 1
FEATURE [Sketcher::SketchObject] Sketch071
  ArcFitTolerance = 1e-06
  AttachmentSupport = -> [Pad014]
  ExternalGeometry = -> [Import017]
  FullyConstrained = true
  MapMode = 5
  Placement = pos=(0,0,14) rot=(0,0,1;0rad)
  Support = -> [Pad014]
  TreeRank = 1096
  sketch-geometry (1):
    g0: Circle CenterX=0 CenterY=19.5 CenterZ=0 NormalX=0 NormalY=0 NormalZ=1 AngleXU=0 Radius=13
  constraints (2):
    c: Coincident(g0,g-3)
    c: Radius(g0) = 13
FEATURE [PartDesign::Pad] Pad015
  AddSubType = 0
  AlongSketchNormal = false
  BaseFeature = -> Pad014
  CheckUpToFaceLimits = true
  ClaimChildren = false
  Direction = (0,0,1)
  Fit = 0
  FitJoin = 0
  InnerFit = 0
  InnerFitJoin = 0
  InnerTaperAngle = 0
  InnerTaperAngleRev = 0
  Length = 3
  Length2 = 100
  Linearize = true
  NewSolid = false
  Profile = -> Sketch071
  Suppress = false
  TreeRank = 1097
  Type = 0
  _ProfileBasedVersion = 1
FEATURE [PartDesign::Chamfer] Chamfer
  AddSubType = 0
  Angle = 56
  Base = -> Pad015 [Edge3]
  BaseFeature = -> Pad015
  ChamferType = 2
  FlipDirection = false
  NewSolid = false
  Size = 2.99
  Size2 = 1
  SupportTransform = false
  Suppress = false
  TreeRank = 1098
FEATURE [Sketcher::SketchObject] Sketch072
  ArcFitTolerance = 1e-06
  AttachmentSupport = -> [Chamfer]
  ExternalGeometry = -> [Chamfer]
  FullyConstrained = true
  MapMode = 5
  Placement = pos=(0,0,17) rot=(0,0,1;0rad)
  Support = -> [Chamfer]
  TreeRank = 1099
  sketch-geometry (1):
    g0: Circle CenterX=0 CenterY=19.5 CenterZ=0 NormalX=0 NormalY=0 NormalZ=1 AngleXU=0 Radius=9
  constraints (2):
    c: Coincident(g0,g-3)
    c: Radius(g0) = 9
FEATURE [PartDesign::Pocket] Pocket004
  AddSubType = 1
  BaseFeature = -> Chamfer
  CheckUpToFaceLimits = true
  ClaimChildren = false
  Fit = 0
  FitJoin = 0
  InnerFit = 0
  InnerFitJoin = 0
  InnerTaperAngle = 0
  InnerTaperAngleRev = 0
  Length = 5
  Length2 = 100
  Linearize = true
  NewSolid = false
  Profile = -> Sketch072
  Suppress = false
  TreeRank = 1100
  Type = 0
  _ProfileBasedVersion = 1
  _Version = 1
FEATURE [PartDesign::Plane] DatumPlane024
  AttachmentSupport = -> [Pocket004]
  Length = 25.9112
  MapMode = 11
  MinimumLength = 10
  MinimumWidth = 10
  Placement = pos=(0,19.5,13) rot=(0,0,1;1.5708rad)
  ResizeMode = 0
  Support = -> [Pocket004]
  TreeRank = 1101
  Width = 26
FEATURE [PartDesign::Draft] Draft001
  AddSubType = 0
  Angle = 23
  Base = -> Pocket004 [Face4]
  BaseFeature = -> Pocket004
  NeutralPlane = -> DatumPlane024
  NewSolid = false
  SupportTransform = false
  Suppress = false
  TreeRank = 1102
FEATURE [PartDesign::Body] Body048  label="joystick guard"
  AutoGroupSolids = false
  ClaimAllChildren = false
  ExportMode = 0
  Group = -> [Sketch070,Import017,Pad014,Sketch071,Pad015,Chamfer,Sketch072,Pocket004,Draft001,DatumPlane024,Import019,Sketch073]
  Origin = -> Origin051
  Tip = -> Draft001
  TreeRank = 1047
  _ExportChildren = -> [Import017,Pad014,Pad015,Chamfer,Pocket004,Draft001,DatumPlane024,Import019,Sketch073]
  _GroupVersion = 1
FEATURE [Sketcher::SketchObject] Sketch084
  ArcFitTolerance = 1e-06
  AttachmentSupport = -> [Cut005]
  ExternalGeometry = -> [Import026]
  FullyConstrained = true
  MapMode = 5
  Placement = pos=(-34,0,0) rot=(0.57735,0.57735,0.57735;2.0944rad)
  Support = -> [Cut005]
  TreeRank = 1298
  sketch-geometry (4):
    g0: LineSegment StartX=-7.25 StartY=13.4 StartZ=0 EndX=33.25 EndY=13.4 EndZ=0
    g1: LineSegment StartX=33.25 StartY=13.4 StartZ=0 EndX=33.25 EndY=2.6 EndZ=0
    g2: LineSegment StartX=33.25 StartY=2.6 StartZ=0 EndX=-7.25 EndY=2.6 EndZ=0
    g3: LineSegment StartX=-7.25 StartY=2.6 StartZ=0 EndX=-7.25 EndY=13.4 EndZ=0
  constraints (12):
    c: Coincident(g0,g1)
    c: Coincident(g1,g2)
    c: Coincident(g2,g3)
    c: Coincident(g3,g0)
    c: Horizontal(g0)
    c: Horizontal(g2)
    c: Vertical(g1)
    c: Vertical(g3)
    c: DistanceX(g0,g-3) = 2
    c: DistanceX(g-4,g1) = 2
    c: DistanceY(g-5,g0) = 2
    c: DistanceY(g1,g-5) = 2
FEATURE [PartDesign::Pad] Pad022
  AddSubType = 0
  AlongSketchNormal = false
  CheckUpToFaceLimits = true
  ClaimChildren = false
  Direction = (1,0,0)
  Fit = 0
  FitJoin = 0
  InnerFit = 0
  InnerFitJoin = 0
  InnerTaperAngle = 0
  InnerTaperAngleRev = 0
  Length = 2
  Length2 = 100
  Linearize = true
  NewSolid = false
  Profile = -> Sketch084
  Suppress = false
  TreeRank = 1300
  Type = 0
  _ProfileBasedVersion = 1
FEATURE [PartDesign::Fillet] Fillet008
  AddSubType = 0
  Base = -> Pad022 [Face6]
  BaseFeature = -> Pad022
  NewSolid = false
  Radius = 1.99
  SupportTransform = false
  Suppress = false
  TreeRank = 1301
FEATURE [PartDesign::Mirrored] Mirrored012
  AddSubType = 0
  BaseFeature = -> Fillet008
  CopyShape = false
  MirrorPlane = -> YZ_Plane061
  NewSolid = false
  OriginalSubs = -> [Fillet008,Pad022]
  Originals = -> [Fillet008,Pad022]
  ParallelTransform = true
  SubTransform = true
  Suppress = false
  TreeRank = 3384
  _Version = 3
FEATURE [PartDesign::FeatureBase] Clone023
  BaseFeature = -> Cut005
  NewSolid = false
  Suppress = false
  TreeRank = 3410
FEATURE [PartDesign::Body] Body066  label="top shell w card slot"
  AutoGroupSolids = false
  BaseFeature = -> Cut005
  ClaimAllChildren = false
  ExportMode = 0
  Group = -> [Clone023]
  Origin = -> Origin072
  Tip = -> Clone023
  TreeRank = 3411
  _ExportChildren = -> [Clone023]
  _GroupVersion = 1
FEATURE [App::Part] Part006  label="masters"
  ClaimAllChildren = false
  ExportMode = 1
  Group = -> [Body,Body010,Body053,Body066,Body045,Body088,Body089,Cut005,Cut004,Cut003,Body042,Body043,Body044,Body047]
  Origin = -> Origin087
  TreeRank = 1838
  _ExportChildren = -> [Body,Body010,Body053,Body066,Body045,Body088,Body089,Cut005]
  _GroupVersion = 1
FEATURE [PartDesign::FeatureBase] Clone042
  BaseFeature = -> Cut005
  NewSolid = false
  Suppress = false
  TreeRank = 3414
FEATURE [Part::SubShapeBinder] Import045  label="Import045(Pad034)"
  BindCopyOnChange = 0
  BindMode = 0
  ClaimChildren = false
  Context = -> Part [Part009.Body086.Import045.]
  FillStyle = 0
  Fuse = false
  MakeFace = false
  OffsetFill = false
  OffsetIntersection = false
  OffsetJoinType = 0
  OffsetOpenResult = false
  PartialLoad = false
  Relative = true
  Support = -> [Body084[Pad034.]]
  TreeRank = 3435
  _Version = 8
FEATURE [PartDesign::Body] Body086  label="hanger"
  AutoGroupSolids = false
  ClaimAllChildren = false
  ExportMode = 0
  Group = -> [Sketch127,Pad035,Import045]
  Origin = -> Origin102
  Tip = -> Pad035
  TreeRank = 2192
  _ExportChildren = -> [Pad035,Import045]
  _GroupVersion = 1
FEATURE [PartDesign::SubShapeBinder] Reference016  label="Reference016(emboss support)"
  BindCopyOnChange = 0
  BindMode = 0
  ClaimChildren = false
  FillStyle = 0
  Fuse = true
  MakeFace = true
  OffsetFill = false
  OffsetIntersection = false
  OffsetJoinType = 0
  OffsetOpenResult = false
  PartialLoad = false
  Relative = true
  Support = -> [Part011[Body058.]]
  TreeRank = 3454
  _Version = 8
FEATURE [PartDesign::SubShapeBinder] Reference015  label="Reference015(top master cutout)"
  BindCopyOnChange = 0
  BindMode = 0
  ClaimChildren = false
  FillStyle = 0
  Fuse = true
  MakeFace = true
  OffsetFill = false
  OffsetIntersection = false
  OffsetJoinType = 0
  OffsetOpenResult = false
  PartialLoad = false
  Relative = true
  Support = -> [Body104]
  TreeRank = 3455
  _Version = 8
FEATURE [PartDesign::Boolean] Boolean011
  BaseFeature = -> Pad034
  ClaimAllChildren = false
  ExportMode = 0
  Group = -> [Reference015]
  NewSolid = false
  Suppress = false
  TreeRank = 3433
  Type = 2
  _ExportChildren = -> [Reference015]
  _GroupVersion = 1
FEATURE [Sketcher::SketchObject] Sketch192
  ArcFitTolerance = 1e-06
  AttachmentSupport = -> [Boolean011]
  ExternalGeometry = -> [Sketch126]
  FullyConstrained = true
  MapMode = 5
  Placement = pos=(0,0,13.9) rot=(0,0,1;0rad)
  Support = -> [Boolean011]
  TreeRank = 3456
  sketch-geometry (4):
    g0: LineSegment StartX=10.9282 StartY=-99 StartZ=0 EndX=-10.9282 EndY=-99 EndZ=0
    g1: LineSegment StartX=-10.9282 StartY=-99 StartZ=0 EndX=-10.9282 EndY=-79 EndZ=0
    g2: LineSegment StartX=-10.9282 StartY=-79 StartZ=0 EndX=10.9282 EndY=-79 EndZ=0
    g3: LineSegment StartX=10.9282 StartY=-79 StartZ=0 EndX=10.9282 EndY=-99 EndZ=0
  constraints (11):
    c: Coincident(g0,g1)
    c: Coincident(g1,g2)
    c: Coincident(g2,g3)
    c: Coincident(g3,g0)
    c: Horizontal(g0)
    c: Horizontal(g2)
    c: Vertical(g1)
    c: Vertical(g3)
    c: Coincident(g0,g-3)
    c: Vertical(g1,g-3)
    c: DistanceY(g3,g3) = 20
FEATURE [PartDesign::Pocket] Pocket034
  AddSubType = 1
  BaseFeature = -> Boolean011
  CheckUpToFaceLimits = true
  ClaimChildren = false
  Fit = 0
  FitJoin = 0
  InnerFit = 0
  InnerFitJoin = 0
  InnerTaperAngle = 0
  InnerTaperAngleRev = 0
  Length = 3.1
  Length2 = 100
  Linearize = true
  NewSolid = false
  Profile = -> Sketch192
  Suppress = false
  TreeRank = 3457
  Type = 0
  _ProfileBasedVersion = 1
  _Version = 1
FEATURE [PartDesign::Body] Body084  label="tail support"
  AutoGroupSolids = false
  ClaimAllChildren = false
  ExportMode = 0
  Group = -> [Sketch126,Pad034,Boolean011,Sketch192,Pocket034]
  Origin = -> Origin100
  Tip = -> Pocket034
  TreeRank = 3423
  _ExportChildren = -> [Pad034,Boolean011,Pocket034]
  _GroupVersion = 1
FEATURE [PartDesign::SubShapeBinder] Reference017  label="Reference017(tail support)"
  BindCopyOnChange = 0
  BindMode = 0
  ClaimChildren = false
  FillStyle = 0
  Fuse = true
  MakeFace = true
  OffsetFill = false
  OffsetIntersection = false
  OffsetJoinType = 0
  OffsetOpenResult = false
  PartialLoad = false
  Relative = true
  Support = -> [Part009[Body084.]]
  TreeRank = 3459
  _Version = 8
FEATURE [PartDesign::SubShapeBinder] Reference018  label="Reference018(fin)"
  BindCopyOnChange = 0
  BindMode = 0
  ClaimChildren = false
  FillStyle = 0
  Fuse = true
  MakeFace = true
  OffsetFill = false
  OffsetIntersection = false
  OffsetJoinType = 0
  OffsetOpenResult = false
  PartialLoad = false
  Relative = true
  Support = -> [Part009[Body081.]]
  TreeRank = 3460
  _Version = 8
FEATURE [PartDesign::SubShapeBinder] Reference020  label="Reference020(trademark support)"
  BindCopyOnChange = 0
  BindMode = 0
  ClaimChildren = false
  FillStyle = 0
  Fuse = true
  MakeFace = true
  OffsetFill = false
  OffsetIntersection = false
  OffsetJoinType = 0
  OffsetOpenResult = false
  PartialLoad = false
  Relative = true
  Support = -> [Part011[Body055.]]
  TreeRank = 3462
  _Version = 8
FEATURE [PartDesign::Mirrored] Mirrored013
  AddSubType = 0
  BaseFeature = -> Fillet013
  CopyShape = false
  MirrorPlane = -> YZ_Plane077
  NewSolid = false
  OriginalSubs = -> [Pad026,Fillet013]
  Originals = -> [Pad026,Fillet013]
  ParallelTransform = true
  SubTransform = true
  Suppress = false
  TreeRank = 3470
  _Version = 3
FEATURE [PartDesign::Body] Body071  label="left groove support"
  AutoGroupSolids = false
  ClaimAllChildren = false
  ExportMode = 0
  Group = -> [Import031,Sketch096,Import032,Import033,Pad026,Fillet013,Mirrored013]
  Origin = -> Origin077
  Tip = -> Mirrored013
  TreeRank = 3469
  _ExportChildren = -> [Import031,Import032,Import033,Pad026,Fillet013,Mirrored013]
  _GroupVersion = 1
FEATURE [Part::MultiFuse] Fusion003
  Shapes = -> [Body016,Body017]
  TreeRank = 397
FEATURE [PartDesign::FeatureBase] Clone007
  BaseFeature = -> Fusion003
  NewSolid = false
  Suppress = false
  TreeRank = 407
FEATURE [PartDesign::Body] Body023
  AutoGroupSolids = false
  BaseFeature = -> Fusion003
  ClaimAllChildren = false
  ExportMode = 0
  Group = -> [Clone007]
  Origin = -> Origin024
  Placement = pos=(-20.95,0,28.8) rot=(0,1,0;4.71239rad)
  Tip = -> Clone007
  TreeRank = 410
  _ExportChildren = -> [Clone007]
  _GroupVersion = 1
FEATURE [PartDesign::FeatureBase] Clone008
  BaseFeature = -> Fusion003
  NewSolid = false
  Suppress = false
  TreeRank = 440
FEATURE [PartDesign::Body] Body024
  AutoGroupSolids = false
  BaseFeature = -> Fusion003
  ClaimAllChildren = false
  ExportMode = 0
  Group = -> [Clone008]
  Origin = -> Origin025
  Placement = pos=(-3.18,0,15.72) rot=(0,-1,0;0.610865rad)
  Tip = -> Clone008
  TreeRank = 443
  _ExportChildren = -> [Clone008]
  _GroupVersion = 1
FEATURE [PartDesign::FeatureBase] Clone009
  BaseFeature = -> Fusion003
  NewSolid = false
  Suppress = false
  TreeRank = 453
FEATURE [PartDesign::Body] Body025
  AutoGroupSolids = false
  BaseFeature = -> Fusion003
  ClaimAllChildren = false
  ExportMode = 0
  Group = -> [Clone009]
  Origin = -> Origin026
  Placement = pos=(-14.58,0,29.79) rot=(0,-1,0;1.309rad)
  Tip = -> Clone009
  TreeRank = 456
  _ExportChildren = -> [Clone009]
  _GroupVersion = 1
FEATURE [Part::MultiFuse] Fusion
  Shapes = -> [Fusion003,Body023]
  TreeRank = 457
FEATURE [Part::MultiFuse] Fusion004
  Shapes = -> [Fusion,Body024]
  TreeRank = 458
FEATURE [Part::MultiFuse] Fusion005
  Shapes = -> [Fusion004,Body025]
  TreeRank = 3485
FEATURE [Part::Cut] Cut  label="top bump fin"
  Base = -> Body015
  Tool = -> Body014
  TreeRank = 3487
FEATURE [Part::Cut] Cut026  label="bump side 1"
  Base = -> Fusion005
  Tool = -> Body022
  TreeRank = 3488
FEATURE [Part::MultiFuse] Fusion024  label="bump side master"
  Shapes = -> [Cut026,Cut002]
  TreeRank = 3489
FEATURE [PartDesign::FeatureBase] Clone045
  BaseFeature = -> Fusion024
  NewSolid = false
  Suppress = false
  TreeRank = 3499
FEATURE [PartDesign::Mirrored] Mirrored014
  AddSubType = 0
  BaseFeature = -> Clone045
  CopyShape = false
  MirrorPlane = -> YZ_Plane117
  NewSolid = false
  ParallelTransform = true
  SubTransform = true
  Suppress = false
  TreeRank = 3502
  _Version = 3
FEATURE [PartDesign::Body] Body106  label="bump side"
  AutoGroupSolids = false
  BaseFeature = -> Fusion024
  ClaimAllChildren = false
  ExportMode = 0
  Group = -> [Clone045,Mirrored014]
  Origin = -> Origin128
  Tip = -> Mirrored014
  TreeRank = 3501
  _ExportChildren = -> [Clone045,Mirrored014]
  _GroupVersion = 1
FEATURE [PartDesign::SubShapeBinder] Reference023  label="Reference023(middle groove support)"
  BindCopyOnChange = 0
  BindMode = 0
  ClaimChildren = false
  FillStyle = 0
  Fuse = true
  MakeFace = true
  OffsetFill = false
  OffsetIntersection = false
  OffsetJoinType = 0
  OffsetOpenResult = false
  PartialLoad = false
  Relative = true
  Support = -> [Part005[Body068.]]
  TreeRank = 3503
  _Version = 8
FEATURE [PartDesign::SubShapeBinder] Reference024  label="Reference024(top groove support)"
  BindCopyOnChange = 0
  BindMode = 0
  ClaimChildren = false
  FillStyle = 0
  Fuse = true
  MakeFace = true
  OffsetFill = false
  OffsetIntersection = false
  OffsetJoinType = 0
  OffsetOpenResult = false
  PartialLoad = false
  Relative = true
  Support = -> [Part005[Common002.]]
  TreeRank = 3504
  _Version = 8
FEATURE [PartDesign::SubShapeBinder] Reference025  label="Reference025(bottom groove support)"
  BindCopyOnChange = 0
  BindMode = 0
  ClaimChildren = false
  FillStyle = 0
  Fuse = true
  MakeFace = true
  OffsetFill = false
  OffsetIntersection = false
  OffsetJoinType = 0
  OffsetOpenResult = false
  PartialLoad = false
  Relative = true
  Support = -> [Part005[Cut024.]]
  TreeRank = 3505
  _Version = 8
FEATURE [PartDesign::SubShapeBinder] Reference026  label="Reference026(left groove support)"
  BindCopyOnChange = 0
  BindMode = 0
  ClaimChildren = false
  FillStyle = 0
  Fuse = true
  MakeFace = true
  OffsetFill = false
  OffsetIntersection = false
  OffsetJoinType = 0
  OffsetOpenResult = false
  PartialLoad = false
  Relative = true
  Support = -> [Part005[Body071.]]
  TreeRank = 3506
  _Version = 8
FEATURE [PartDesign::SubShapeBinder] Reference027  label="Reference027(middle groove support 2)"
  BindCopyOnChange = 0
  BindMode = 0
  ClaimChildren = false
  FillStyle = 0
  Fuse = true
  MakeFace = true
  OffsetFill = false
  OffsetIntersection = false
  OffsetJoinType = 0
  OffsetOpenResult = false
  PartialLoad = false
  Relative = true
  Support = -> [Part005[Common003.]]
  TreeRank = 3507
  _Version = 8
FEATURE [PartDesign::SubShapeBinder] Reference028  label="Reference028(bump side)"
  BindCopyOnChange = 0
  BindMode = 0
  ClaimChildren = false
  FillStyle = 0
  Fuse = true
  MakeFace = true
  OffsetFill = false
  OffsetIntersection = false
  OffsetJoinType = 0
  OffsetOpenResult = false
  PartialLoad = false
  Relative = true
  Support = -> [Part004[Body106.]]
  TreeRank = 3508
  _Version = 8
FEATURE [PartDesign::SubShapeBinder] Reference029  label="Reference029(top bump fin)"
  BindCopyOnChange = 0
  BindMode = 0
  ClaimChildren = false
  FillStyle = 0
  Fuse = true
  MakeFace = true
  OffsetFill = false
  OffsetIntersection = false
  OffsetJoinType = 0
  OffsetOpenResult = false
  PartialLoad = false
  Relative = true
  Support = -> [Part004[Cut.]]
  TreeRank = 3509
  _Version = 8
FEATURE [PartDesign::SubShapeBinder] Reference030  label="Reference030(arrows)"
  BindCopyOnChange = 0
  BindMode = 0
  ClaimChildren = false
  FillStyle = 0
  Fuse = true
  MakeFace = true
  OffsetFill = false
  OffsetIntersection = false
  OffsetJoinType = 0
  OffsetOpenResult = false
  PartialLoad = false
  Relative = true
  Support = -> [Part004[Body057.]]
  TreeRank = 3510
  _Version = 8
FEATURE [PartDesign::SubShapeBinder] Reference031  label="Reference031(square bumps)"
  BindCopyOnChange = 0
  BindMode = 0
  ClaimChildren = false
  FillStyle = 0
  Fuse = true
  MakeFace = true
  OffsetFill = false
  OffsetIntersection = false
  OffsetJoinType = 0
  OffsetOpenResult = false
  PartialLoad = false
  Relative = true
  Support = -> [Part004[Body011.]]
  TreeRank = 3511
  _Version = 8
FEATURE [PartDesign::SubShapeBinder] Reference032  label="Reference032(top groove)"
  BindCopyOnChange = 0
  BindMode = 0
  ClaimChildren = false
  FillStyle = 0
  Fuse = true
  MakeFace = true
  OffsetFill = false
  OffsetIntersection = false
  OffsetJoinType = 0
  OffsetOpenResult = false
  PartialLoad = false
  Relative = true
  Support = -> [Part012[Body005.]]
  TreeRank = 3513
  _Version = 8
FEATURE [PartDesign::SubShapeBinder] Reference033  label="Reference033(bottom groove)"
  BindCopyOnChange = 0
  BindMode = 0
  ClaimChildren = false
  FillStyle = 0
  Fuse = true
  MakeFace = true
  OffsetFill = false
  OffsetIntersection = false
  OffsetJoinType = 0
  OffsetOpenResult = false
  PartialLoad = false
  Relative = true
  Support = -> [Part012[Body006.]]
  TreeRank = 3514
  _Version = 8
FEATURE [PartDesign::SubShapeBinder] Reference034  label="Reference034(left groove)"
  BindCopyOnChange = 0
  BindMode = 0
  ClaimChildren = false
  FillStyle = 0
  Fuse = true
  MakeFace = true
  OffsetFill = false
  OffsetIntersection = false
  OffsetJoinType = 0
  OffsetOpenResult = false
  PartialLoad = false
  Relative = true
  Support = -> [Part012[Body009.]]
  TreeRank = 3515
  _Version = 8
FEATURE [PartDesign::SubShapeBinder] Reference035  label="Reference035(right groove)"
  BindCopyOnChange = 0
  BindMode = 0
  ClaimChildren = false
  FillStyle = 0
  Fuse = true
  MakeFace = true
  OffsetFill = false
  OffsetIntersection = false
  OffsetJoinType = 0
  OffsetOpenResult = false
  PartialLoad = false
  Relative = true
  Support = -> [Part012[Body012.]]
  TreeRank = 3516
  _Version = 8
FEATURE [PartDesign::SubShapeBinder] Reference036  label="Reference036(middle groove)"
  BindCopyOnChange = 0
  BindMode = 0
  ClaimChildren = false
  FillStyle = 0
  Fuse = true
  MakeFace = true
  OffsetFill = false
  OffsetIntersection = false
  OffsetJoinType = 0
  OffsetOpenResult = false
  PartialLoad = false
  Relative = true
  Support = -> [Part012[Body008.]]
  TreeRank = 3517
  _Version = 8
FEATURE [PartDesign::SubShapeBinder] Reference037  label="Reference037(middle side groove)"
  BindCopyOnChange = 0
  BindMode = 0
  ClaimChildren = false
  FillStyle = 0
  Fuse = true
  MakeFace = true
  OffsetFill = false
  OffsetIntersection = false
  OffsetJoinType = 0
  OffsetOpenResult = false
  PartialLoad = false
  Relative = true
  Support = -> [Part012[Body007.]]
  TreeRank = 3518
  _Version = 8
FEATURE [PartDesign::SubShapeBinder] Reference038  label="Reference038(belly button)"
  BindCopyOnChange = 0
  BindMode = 0
  ClaimChildren = false
  FillStyle = 0
  Fuse = true
  MakeFace = true
  OffsetFill = false
  OffsetIntersection = false
  OffsetJoinType = 0
  OffsetOpenResult = false
  PartialLoad = false
  Relative = true
  Support = -> [Part012[Body013.]]
  TreeRank = 3519
  _Version = 8
FEATURE [PartDesign::SubShapeBinder] Reference040  label="Reference040(cylinder)"
  BindCopyOnChange = 0
  BindMode = 0
  ClaimChildren = false
  FillStyle = 0
  Fuse = true
  MakeFace = true
  OffsetFill = false
  OffsetIntersection = false
  OffsetJoinType = 0
  OffsetOpenResult = false
  PartialLoad = false
  Relative = true
  Support = -> [Part011[Body031.]]
  TreeRank = 3521
  _Version = 8
FEATURE [PartDesign::SubShapeBinder] Reference041  label="Reference041(trademark cutout)"
  BindCopyOnChange = 0
  BindMode = 0
  ClaimChildren = false
  FillStyle = 0
  Fuse = true
  MakeFace = true
  OffsetFill = false
  OffsetIntersection = false
  OffsetJoinType = 0
  OffsetOpenResult = false
  PartialLoad = false
  Relative = true
  Support = -> [Part011[Body054.]]
  TreeRank = 3522
  _Version = 8
FEATURE [PartDesign::SubShapeBinder] Reference042  label="Reference042(emboss cutout)"
  BindCopyOnChange = 0
  BindMode = 0
  ClaimChildren = false
  FillStyle = 0
  Fuse = true
  MakeFace = true
  OffsetFill = false
  OffsetIntersection = false
  OffsetJoinType = 0
  OffsetOpenResult = false
  PartialLoad = false
  Relative = true
  Support = -> [Part011[Body051.]]
  TreeRank = 3523
  _Version = 8
FEATURE [PartDesign::SubShapeBinder] Reference043  label="Reference043(top light cutout)"
  BindCopyOnChange = 0
  BindMode = 0
  ClaimChildren = false
  FillStyle = 0
  Fuse = true
  MakeFace = true
  OffsetFill = false
  OffsetIntersection = false
  OffsetJoinType = 0
  OffsetOpenResult = false
  PartialLoad = false
  Relative = true
  Support = -> [Part010[Body041.]]
  TreeRank = 3524
  _Version = 8
FEATURE [PartDesign::SubShapeBinder] Reference044  label="Reference044(front light top cutout)"
  BindCopyOnChange = 0
  BindMode = 0
  ClaimChildren = false
  FillStyle = 0
  Fuse = true
  MakeFace = true
  OffsetFill = false
  OffsetIntersection = false
  OffsetJoinType = 0
  OffsetOpenResult = false
  PartialLoad = false
  Relative = true
  Support = -> [Part010[Body034.]]
  TreeRank = 3525
  _Version = 8
FEATURE [PartDesign::SubShapeBinder] Reference045  label="Reference045(front light hole)"
  BindCopyOnChange = 0
  BindMode = 0
  ClaimChildren = false
  FillStyle = 0
  Fuse = true
  MakeFace = true
  OffsetFill = false
  OffsetIntersection = false
  OffsetJoinType = 0
  OffsetOpenResult = false
  PartialLoad = false
  Relative = true
  Support = -> [Part010[Body035.]]
  TreeRank = 3526
  _Version = 8
FEATURE [PartDesign::SubShapeBinder] Reference046  label="Reference046(hanger)"
  BindCopyOnChange = 0
  BindMode = 0
  ClaimChildren = false
  FillStyle = 0
  Fuse = true
  MakeFace = true
  OffsetFill = false
  OffsetIntersection = false
  OffsetJoinType = 0
  OffsetOpenResult = false
  PartialLoad = false
  Relative = true
  Support = -> [Part013[Body086.]]
  TreeRank = 3527
  _Version = 8
FEATURE [PartDesign::SubShapeBinder] Reference047  label="Reference047(joystick hole)"
  BindCopyOnChange = 0
  BindMode = 0
  ClaimChildren = false
  FillStyle = 0
  Fuse = true
  MakeFace = true
  OffsetFill = false
  OffsetIntersection = false
  OffsetJoinType = 0
  OffsetOpenResult = false
  PartialLoad = false
  Relative = true
  Support = -> [Body046]
  TreeRank = 3528
  _Version = 8
FEATURE [PartDesign::SubShapeBinder] Reference048  label="Reference048(front light support)"
  BindCopyOnChange = 0
  BindMode = 0
  ClaimChildren = false
  FillStyle = 0
  Fuse = true
  MakeFace = true
  OffsetFill = false
  OffsetIntersection = false
  OffsetJoinType = 0
  OffsetOpenResult = false
  PartialLoad = false
  Relative = true
  Support = -> [Part010[Body060.]]
  TreeRank = 3529
  _Version = 8
FEATURE [PartDesign::SubShapeBinder] Reference049  label="Reference049(front light shell)"
  BindCopyOnChange = 0
  BindMode = 0
  ClaimChildren = false
  FillStyle = 0
  Fuse = true
  MakeFace = true
  OffsetFill = false
  OffsetIntersection = false
  OffsetJoinType = 0
  OffsetOpenResult = false
  PartialLoad = false
  Relative = true
  Support = -> [Part010[Body039.]]
  TreeRank = 3530
  _Version = 8
FEATURE [PartDesign::SubShapeBinder] Reference050  label="Reference050(front light bottom)"
  BindCopyOnChange = 0
  BindMode = 0
  ClaimChildren = false
  FillStyle = 0
  Fuse = true
  MakeFace = true
  OffsetFill = false
  OffsetIntersection = false
  OffsetJoinType = 0
  OffsetOpenResult = false
  PartialLoad = false
  Relative = true
  Support = -> [Part010[Body033.]]
  TreeRank = 3531
  _Version = 8
FEATURE [PartDesign::SubShapeBinder] Reference051  label="Reference051(top light shell)"
  BindCopyOnChange = 0
  BindMode = 0
  ClaimChildren = false
  FillStyle = 0
  Fuse = true
  MakeFace = true
  OffsetFill = false
  OffsetIntersection = false
  OffsetJoinType = 0
  OffsetOpenResult = false
  PartialLoad = false
  Relative = true
  Support = -> [Part010[Body040.]]
  TreeRank = 3532
  _Version = 8
FEATURE [Part::SubShapeBinder] Import057  label="Import057(Sketch077)"
  BindCopyOnChange = 0
  BindMode = 0
  ClaimChildren = false
  Context = -> Part001 [Body061.Import057.]
  FillStyle = 0
  Fuse = false
  MakeFace = false
  OffsetFill = false
  OffsetIntersection = false
  OffsetJoinType = 0
  OffsetOpenResult = false
  PartialLoad = false
  Relative = true
  Support = -> [Part[Part011.Body054.Sketch077.]]
  TreeRank = 3537
  _Version = 8
FEATURE [Sketcher::SketchObject] Sketch088
  ArcFitTolerance = 1e-06
  AttachmentSupport = -> [ShapeBinder024]
  ExternalGeometry = -> [Import057]
  FullyConstrained = true
  MapMode = 5
  Placement = pos=(0,0,13) rot=(0,0,1;0rad)
  Support = -> [ShapeBinder024]
  TreeRank = 1424
  sketch-geometry (4):
    g0: ArcOfCircle CenterX=-19 CenterY=42.2 CenterZ=0 NormalX=0 NormalY=0 NormalZ=1 AngleXU=0 Radius=2.3 StartAngle=1.5708 EndAngle=4.71239
    g1: ArcOfCircle CenterX=-4 CenterY=42.2 CenterZ=0 NormalX=0 NormalY=0 NormalZ=1 AngleXU=0 Radius=2.3 StartAngle=4.71239 EndAngle=7.85398
    g2: LineSegment StartX=-19 StartY=39.9 StartZ=0 EndX=-4 EndY=39.9 EndZ=0
    g3: LineSegment StartX=-4 StartY=44.5 StartZ=0 EndX=-19 EndY=44.5 EndZ=0
  constraints (7):
    c: Tangent(g0,g2) = -1.5708
    c: Tangent(g2,g1) = -1.5708
    c: Tangent(g1,g3) = -1.5708
    c: Tangent(g3,g0) = -1.5708
    c: Coincident(g0,g-3)
    c: Coincident(g1,g-4)
    c: Coincident(g1,g-4)
FEATURE [PartDesign::Pad] Pad024
  AddSubType = 0
  AlongSketchNormal = false
  CheckUpToFaceLimits = true
  ClaimChildren = false
  Direction = (0,0,1)
  Fit = 0
  FitJoin = 0
  InnerFit = 0
  InnerFitJoin = 0
  InnerTaperAngle = 0
  InnerTaperAngleRev = 0
  Length = 1
  Length2 = 100
  Linearize = true
  NewSolid = false
  Profile = -> Sketch088
  Reversed = true
  Suppress = false
  TreeRank = 1808
  Type = 0
  _ProfileBasedVersion = 1
FEATURE [PartDesign::SubShapeBinder] Reference052  label="Reference052(trademark groove)"
  BindCopyOnChange = 0
  BindMode = 0
  ClaimChildren = false
  FillStyle = 0
  Fuse = true
  MakeFace = true
  OffsetFill = false
  OffsetIntersection = false
  OffsetJoinType = 0
  OffsetOpenResult = false
  PartialLoad = false
  Relative = true
  Support = -> [Part012[Body056.]]
  TreeRank = 3538
  _Version = 8
FEATURE [App::Part] Part013  label="hanger001"
  ClaimAllChildren = false
  ExportMode = 1
  Group = -> [Body086]
  Origin = -> Origin129
  TreeRank = 3543
  _ExportChildren = -> [Body086]
  _GroupVersion = 1
FEATURE [PartDesign::SubShapeBinder] Reference053  label="Reference053(front bars)"
  BindCopyOnChange = 0
  BindMode = 0
  ClaimChildren = false
  FillStyle = 0
  Fuse = true
  MakeFace = true
  OffsetFill = false
  OffsetIntersection = false
  OffsetJoinType = 0
  OffsetOpenResult = false
  PartialLoad = false
  Relative = true
  Support = -> [Body098]
  TreeRank = 3549
  _Version = 8
FEATURE [PartDesign::SubShapeBinder] Reference054  label="Reference054(chin plate)"
  BindCopyOnChange = 0
  BindMode = 0
  ClaimChildren = false
  FillStyle = 0
  Fuse = true
  MakeFace = true
  OffsetFill = false
  OffsetIntersection = false
  OffsetJoinType = 0
  OffsetOpenResult = false
  PartialLoad = false
  Relative = true
  Support = -> [Body095]
  TreeRank = 3550
  _Version = 8
FEATURE [PartDesign::SubShapeBinder] Reference055  label="Reference055(trademark text)"
  BindCopyOnChange = 0
  BindMode = 0
  ClaimChildren = false
  FillStyle = 0
  Fuse = true
  MakeFace = true
  OffsetFill = false
  OffsetIntersection = false
  OffsetJoinType = 0
  OffsetOpenResult = false
  PartialLoad = false
  Relative = true
  Support = -> [Extrude]
  TreeRank = 3552
  _Version = 8
FEATURE [PartDesign::Boolean] Boolean015
  BaseFeature = -> Pad024
  ClaimAllChildren = false
  ExportMode = 0
  Group = -> [Reference055]
  NewSolid = false
  Suppress = false
  TreeRank = 3551
  Type = 0
  _ExportChildren = -> [Reference055]
  _GroupVersion = 1
FEATURE [PartDesign::Body] Body061  label="trademark"
  AutoGroupSolids = false
  ClaimAllChildren = false
  ExportMode = 0
  Group = -> [ShapeBinder024,Sketch088,Pad024,Import057,Boolean015]
  Origin = -> Origin065
  Tip = -> Boolean015
  TreeRank = 3535
  _ExportChildren = -> [ShapeBinder024,Pad024,Import057,Boolean015]
  _GroupVersion = 1
FEATURE [App::Part] Part001  label="trademark insert001"
  ClaimAllChildren = false
  ExportMode = 1
  Group = -> [Extrude,ShapeString,Body061]
  Origin = -> Origin079
  TreeRank = 1663
  _ExportChildren = -> [Extrude,Body061]
  _GroupVersion = 1
FEATURE [PartDesign::SubShapeBinder] Reference056  label="Reference056(emboss support)"
  BindCopyOnChange = 0
  BindMode = 0
  ClaimChildren = false
  FillStyle = 0
  Fuse = true
  MakeFace = true
  OffsetFill = false
  OffsetIntersection = false
  OffsetJoinType = 0
  OffsetOpenResult = false
  PartialLoad = false
  Relative = true
  Support = -> [Part011[Body058.]]
  TreeRank = 3576
  _Version = 8
FEATURE [PartDesign::SubShapeBinder] Reference057  label="Reference057(top inside master)"
  BindCopyOnChange = 0
  BindMode = 0
  ClaimChildren = false
  FillStyle = 0
  Fuse = true
  MakeFace = true
  OffsetFill = false
  OffsetIntersection = false
  OffsetJoinType = 0
  OffsetOpenResult = false
  PartialLoad = false
  Relative = true
  Support = -> [Part006[Body053.]]
  TreeRank = 3577
  _Version = 8
FEATURE [PartDesign::Boolean] Boolean009
  BaseFeature = -> Mirrored012
  ClaimAllChildren = false
  ExportMode = 0
  Group = -> [Reference057]
  NewSolid = false
  Suppress = false
  TreeRank = 3385
  Type = 2
  _ExportChildren = -> [Reference057]
  _GroupVersion = 1
FEATURE [PartDesign::Body] Body058  label="emboss support"
  AutoGroupSolids = false
  ClaimAllChildren = false
  ExportMode = 0
  Group = -> [ShapeBinder023,Sketch084,Import026,Pad022,Fillet008,Mirrored012,Boolean009]
  Origin = -> Origin061
  Tip = -> Boolean009
  TreeRank = 3370
  _ExportChildren = -> [ShapeBinder023,Import026,Pad022,Fillet008,Mirrored012,Boolean009]
  _GroupVersion = 1
FEATURE [PartDesign::FeatureBase] Clone046
  BaseFeature = -> Body010
  NewSolid = false
  Suppress = false
  TreeRank = 3587
FEATURE [PartDesign::Body] Body107  label="tail b 1"
  AutoGroupSolids = false
  BaseFeature = -> Body010
  ClaimAllChildren = false
  ExportMode = 0
  Group = -> [Clone046]
  Origin = -> Origin133
  Placement = pos=(-20.95,-54,22.85) rot=(0,-1,0;1.5708rad)
  Tip = -> Clone046
  TreeRank = 3590
  _ExportChildren = -> [Clone046]
  _GroupVersion = 1
FEATURE [PartDesign::FeatureBase] Clone047
  BaseFeature = -> Body010
  NewSolid = false
  Suppress = false
  TreeRank = 3600
FEATURE [PartDesign::Body] Body108  label="tail b 2"
  AutoGroupSolids = false
  BaseFeature = -> Body010
  ClaimAllChildren = false
  ExportMode = 0
  Group = -> [Clone047]
  Origin = -> Origin134
  Placement = pos=(-20.95,-66,22.85) rot=(0,-1,0;1.5708rad)
  Tip = -> Clone047
  TreeRank = 3603
  _ExportChildren = -> [Clone047]
  _GroupVersion = 1
FEATURE [PartDesign::FeatureBase] Clone048
  BaseFeature = -> Body010
  NewSolid = false
  Suppress = false
  TreeRank = 3613
FEATURE [PartDesign::Body] Body109  label="tail b 3"
  AutoGroupSolids = false
  BaseFeature = -> Body010
  ClaimAllChildren = false
  ExportMode = 0
  Group = -> [Clone048]
  Origin = -> Origin135
  Placement = pos=(-18.6544,-66.5173,22.85) rot=(0.280624,-0.917878,0.280624;1.65638rad)
  Tip = -> Clone048
  TreeRank = 3616
  _ExportChildren = -> [Clone048]
  _GroupVersion = 1
FEATURE [PartDesign::FeatureBase] Clone049
  BaseFeature = -> Body010
  NewSolid = false
  Suppress = false
  TreeRank = 3626
FEATURE [PartDesign::Body] Body110  label="tail b 4"
  AutoGroupSolids = false
  BaseFeature = -> Body010
  ClaimAllChildren = false
  ExportMode = 0
  Group = -> [Clone049]
  Origin = -> Origin136
  Placement = pos=(-12.5584,-71.3611,22.85) rot=(0.363936,-0.85738,0.363936;1.72407rad)
  Tip = -> Clone049
  TreeRank = 3629
  _ExportChildren = -> [Clone049]
  _GroupVersion = 1
FEATURE [Part::MultiFuse] Fusion025
  Shapes = -> [Body107,Body108]
  TreeRank = 3630
FEATURE [Part::MultiFuse] Fusion026
  Shapes = -> [Fusion025,Body109]
  TreeRank = 3631
FEATURE [Part::MultiFuse] Fusion027  label="tail bump master"
  Shapes = -> [Fusion026,Body110]
  TreeRank = 3632
FEATURE [PartDesign::FeatureBase] Clone050
  BaseFeature = -> Fusion027
  NewSolid = false
  Suppress = false
  TreeRank = 3642
FEATURE [PartDesign::Mirrored] Mirrored015
  AddSubType = 0
  BaseFeature = -> Clone050
  CopyShape = false
  MirrorPlane = -> YZ_Plane124
  NewSolid = false
  OriginalSubs = -> [Clone050]
  Originals = -> [Clone050]
  ParallelTransform = true
  SubTransform = true
  Suppress = false
  TreeRank = 3646
  _Version = 3
FEATURE [PartDesign::Body] Body111  label="tail bump"
  AutoGroupSolids = false
  BaseFeature = -> Fusion027
  ClaimAllChildren = false
  ExportMode = 0
  Group = -> [Clone050,Mirrored015]
  Origin = -> Origin137
  Tip = -> Mirrored015
  TreeRank = 3645
  _ExportChildren = -> [Clone050,Mirrored015]
  _GroupVersion = 1
FEATURE [App::Part] Part004  label="bumps"
  ClaimAllChildren = false
  ExportMode = 1
  Group = -> [Body014,Body015,Body022,Fusion005,Body025,Fusion004,Body024,Fusion,Fusion003,Body016,Body017,Body023,Cut002,Fusion008,Body029,Fusion007,Body028,Fusion006,Body026,Body027,Body030,Body011,Body057,Cut,Cut026,Fusion024,Body106,Body107,Body108,Body109,Body110,Fusion027,Fusion026,Fusion025,Body111]
  Origin = -> Origin085
  TreeRank = 1826
  _ExportChildren = -> [Body011,Body057,Cut,Fusion024,Body106,Fusion027,Body111]
  _GroupVersion = 1
FEATURE [PartDesign::SubShapeBinder] Reference058  label="Reference058(tail bump)"
  BindCopyOnChange = 0
  BindMode = 0
  ClaimChildren = false
  FillStyle = 0
  Fuse = true
  MakeFace = true
  OffsetFill = false
  OffsetIntersection = false
  OffsetJoinType = 0
  OffsetOpenResult = false
  PartialLoad = false
  Relative = true
  Support = -> [Part004[Body111.]]
  TreeRank = 3647
  _Version = 8
FEATURE [Sketcher::SketchObject] Sketch193
  ArcFitTolerance = 1e-06
  AttachmentSupport = -> [Sketch077]
  ExternalGeometry = -> [Sketch077]
  FullyConstrained = true
  MapMode = 5
  Placement = pos=(0,0,14) rot=(0,0,1;0rad)
  Support = -> [Sketch077]
  TreeRank = 3648
  sketch-geometry (5):
    g0: Circle CenterX=-14 CenterY=42.2 CenterZ=0 NormalX=0 NormalY=0 NormalZ=1 AngleXU=0 Radius=1
    g1: Circle CenterX=-9 CenterY=42.2 CenterZ=0 NormalX=0 NormalY=0 NormalZ=1 AngleXU=0 Radius=1
    g2: LineSegment [constr] StartX=-19 StartY=42.2 StartZ=0 EndX=-14 EndY=42.2 EndZ=0
    g3: LineSegment [constr] StartX=-14 StartY=42.2 StartZ=0 EndX=-9 EndY=42.2 EndZ=0
    g4: LineSegment [constr] StartX=-9 StartY=42.2 StartZ=0 EndX=-4 EndY=42.2 EndZ=0
  constraints (12):
    c: Diameter(g0) = 2
    c: Diameter(g1) = 2
    c: Coincident(g2,g-3)
    c: Coincident(g2,g0)
    c: Coincident(g3,g0)
    c: Coincident(g3,g1)
    c: Horizontal(g3)
    c: Coincident(g4,g1)
    c: Coincident(g4,g-4)
    c: Equal(g2,g3)
    c: Equal(g3,g4)
    c: Horizontal(g2)
FEATURE [PartDesign::Pad] Pad051
  AddSubType = 0
  AlongSketchNormal = false
  BaseFeature = -> Pad019
  CheckUpToFaceLimits = true
  ClaimChildren = false
  Direction = (0,0,1)
  Fit = 0
  FitJoin = 0
  InnerFit = 0
  InnerFitJoin = 0
  InnerTaperAngle = 0
  InnerTaperAngleRev = 0
  Length = 10
  Length2 = 100
  Linearize = true
  NewSolid = false
  Profile = -> Sketch193
  Reversed = true
  Suppress = false
  TreeRank = 3649
  Type = 0
  _ProfileBasedVersion = 1
FEATURE [PartDesign::Body] Body054  label="trademark cutout"
  AutoGroupSolids = false
  ClaimAllChildren = false
  ExportMode = 0
  Group = -> [Import021,Sketch077,Pad019,Sketch193,Pad051]
  Origin = -> Origin057
  Tip = -> Pad051
  TreeRank = 3258
  _ExportChildren = -> [Import021,Pad019,Pad051]
  _GroupVersion = 1
FEATURE [App::Part] Part011  label="emboss"
  ClaimAllChildren = false
  ExportMode = 1
  Group = -> [Body051,Body058,Body054,Body031,Body055]
  Origin = -> Origin124
  TreeRank = 3343
  _ExportChildren = -> [Body051,Body058,Body054,Body031,Body055]
  _GroupVersion = 1
FEATURE [PartDesign::SubShapeBinder] Reference059  label="Reference059(top inside master)"
  BindCopyOnChange = 0
  BindMode = 0
  ClaimChildren = false
  FillStyle = 0
  Fuse = true
  MakeFace = true
  OffsetFill = false
  OffsetIntersection = false
  OffsetJoinType = 0
  OffsetOpenResult = false
  PartialLoad = false
  Relative = true
  Support = -> [Part006[Body053.]]
  TreeRank = 3651
  _Version = 8
FEATURE [PartDesign::Boolean] Boolean017
  BaseFeature = -> Revolution004
  ClaimAllChildren = false
  ExportMode = 0
  Group = -> [Reference059]
  NewSolid = false
  Suppress = false
  TreeRank = 3650
  Type = 2
  _ExportChildren = -> [Reference059]
  _GroupVersion = 1
FEATURE [PartDesign::Body] Body039  label="front light shell"
  AutoGroupSolids = false
  ClaimAllChildren = false
  ExportMode = 0
  Group = -> [ShapeBinder014,Import007,Sketch047,DatumLine005,Revolution004,Boolean017]
  Origin = -> Origin041
  Tip = -> Boolean017
  TreeRank = 3327
  _ExportChildren = -> [ShapeBinder014,Import007,DatumLine005,Revolution004,Boolean017]
  _GroupVersion = 1
FEATURE [App::Part] Part010  label="lights"
  ClaimAllChildren = false
  ExportMode = 1
  Group = -> [Body035,Body034,Body033,Body040,Body039,Body060,Body041]
  Origin = -> Origin123
  TreeRank = 3338
  _ExportChildren = -> [Body035,Body034,Body033,Body040,Body039,Body060,Body041]
  _GroupVersion = 1
FEATURE [PartDesign::ShapeBinder] ShapeBinder042
  Placement = pos=(0,0,14) rot=(0,0,1;0rad)
  Support = -> [Sketch070]
  TraceSupport = false
  TreeRank = 3664
FEATURE [PartDesign::ShapeBinder] ShapeBinder043
  Support = -> [Draft001]
  TraceSupport = false
  TreeRank = 3666
FEATURE [Sketcher::SketchObject] Sketch194
  ArcFitTolerance = 1e-06
  AttachmentSupport = -> [YZ_Plane125]
  ExternalGeometry = -> [ShapeBinder042,ShapeBinder043]
  FullyConstrained = true
  MapMode = 5
  Placement = pos=(0,0,0) rot=(0.57735,0.57735,0.57735;2.0944rad)
  Support = -> [YZ_Plane125]
  TreeRank = 3665
  sketch-geometry (19):
    g0: LineSegment [constr] StartX=19.5 StartY=14 StartZ=0 EndX=19.5 EndY=0 EndZ=0
    g1: Circle [constr] CenterX=19.5 CenterY=0 CenterZ=0 NormalX=0 NormalY=0 NormalZ=1 AngleXU=0 Radius=15.8114
    g2: ArcOfCircle CenterX=19.5 CenterY=0 CenterZ=0 NormalX=0 NormalY=0 NormalZ=1 AngleXU=0 Radius=15.6 StartAngle=0.63288 EndAngle=1.25466
    g3: ArcOfCircle CenterX=19.5 CenterY=0 CenterZ=0 NormalX=0 NormalY=0 NormalZ=1 AngleXU=0 Radius=14.5 StartAngle=0.689743 EndAngle=1.3199
    g4: LineSegment StartX=23.1 StartY=14.046 StartZ=0 EndX=23.1 EndY=10.046 EndZ=0
    g5: LineSegment StartX=23.1 StartY=10.046 StartZ=0 EndX=19.5 EndY=10.046 EndZ=0
    g6: LineSegment StartX=24.35 StartY=14.8269 StartZ=0 EndX=24.35 EndY=18.8269 EndZ=0
    g7: LineSegment [constr] StartX=32.0787 StartY=9.22692 StartZ=0 EndX=19.5 EndY=0 EndZ=0
    g8: LineSegment StartX=24.35 StartY=18.8269 StartZ=0 EndX=28.5 EndY=20.2269 EndZ=0
    g9: LineSegment StartX=28.5 StartY=20.2269 StartZ=0 EndX=28.5 EndY=21.6269 EndZ=0
    g10: ArcOfCircle [constr] CenterX=19.5 CenterY=5.95192 CenterZ=0 NormalX=0 NormalY=0 NormalZ=1 AngleXU=0 Radius=18.075 StartAngle=1.04959 EndAngle=1.5708
    g11: LineSegment StartX=32.0787 StartY=9.22692 StartZ=0 EndX=30.6854 EndY=9.22692 EndZ=0
    g12: ArcOfCircle CenterX=19.5 CenterY=24.6092 CenterZ=0 NormalX=0 NormalY=0 NormalZ=1 AngleXU=0 Radius=1 StartAngle=4.71239 EndAngle=5.63968
    g13: ArcOfCircle CenterX=26.5501 CenterY=22.3823 CenterZ=0 NormalX=0 NormalY=0 NormalZ=1 AngleXU=0 Radius=0.5 StartAngle=6.26776 EndAngle=8.62955
    g14: ArcOfCircle CenterX=23.1102 CenterY=23.4555 CenterZ=0 NormalX=0 NormalY=0 NormalZ=1 AngleXU=0 Radius=0.5 StartAngle=0.202001 EndAngle=2.53279
    g15: ArcOfCircle CenterX=19.5 CenterY=5.95192 CenterZ=0 NormalX=0 NormalY=0 NormalZ=1 AngleXU=0 Radius=18.075 StartAngle=1.39282 EndAngle=1.52652
    g16: ArcOfCircle CenterX=19.5 CenterY=5.95192 CenterZ=0 NormalX=0 NormalY=0 NormalZ=1 AngleXU=0 Radius=18.075 StartAngle=1.19106 EndAngle=1.34197
    g17: ArcOfCircle CenterX=19.5 CenterY=5.95192 CenterZ=0 NormalX=0 NormalY=0 NormalZ=1 AngleXU=0 Radius=18.075 StartAngle=1.04959 EndAngle=1.13988
    g18: LineSegment StartX=19.5 StartY=23.6092 StartZ=0 EndX=19.5 EndY=10.046 EndZ=0
  constraints (59):
    c: Coincident(g0,g-4)
    c: PointOnObject(g0,g-1)
    c: Vertical(g0)
    c: Coincident(g1,g0)
    c: PointOnObject(g-5,g1)
    c: Coincident(g2,g0)
    c: Radius(g2) = 15.6
    c: Coincident(g3,g2)
    c: Coincident(g4,g3)
    c: Vertical(g4)
    c: Coincident(g5,g4)
    c: PointOnObject(g5,g0)
    c: Horizontal(g5)
    c: Coincident(g6,g2)
    c: Radius(g3) = 14.5
    c: Coincident(g7,g2)
    c: Coincident(g7,g2)
    c: Coincident(g8,g6)
    c: Coincident(g9,g8)
    c: PointOnObject(g10,g0)
    c: Coincident(g10,g9)
    c: Vertical(g10,g5)
    c: DistanceY(g9,g10) = 2.4
    c: DistanceY(g9,g9) = 1.4
    c: DistanceX(g10,g8) = 9
    c: Vertical(g9)
    c: DistanceY(g6,g8) = 1.4
    c: Vertical(g6)
    c: DistanceX(g10,g6) = 4.85
    c: DistanceY(g6,g6) = 4
    c: Coincident(g11,g2)
    c: Coincident(g11,g3)
    c: Horizontal(g11)
    c: DistanceY(g2,g2) = 5.6
    c: DistanceX(g5,g5) = 3.6
    c: DistanceY(g4,g4) = 4
    c: PointOnObject(g12,g10)
    c: Radius(g12) = 1
    c: PointOnObject(g13,g10)
    c: Radius(g14) = 0.5
    c: Radius(g13) = 0.5
    c: Coincident(g15,g10)
    c: Coincident(g15,g12)
    c: Coincident(g15,g14)
    c: Coincident(g16,g15)
    c: Coincident(g16,g14)
    c: Coincident(g16,g13)
    c: Coincident(g17,g15)
    c: Coincident(g17,g13)
    c: Coincident(g17,g9)
    c: Vertical(g12,g10)
    c: Vertical(g12,g10)
    c: DistanceX(g12,g12) = 0.8
    c: DistanceX(g14,g14) = 0.9
    c: DistanceX(g13,g13) = 0.85
    c: DistanceX(g12,g14) = 2.4
    c: DistanceX(g14,g13) = 2.6
    c: Coincident(g18,g12)
    c: Coincident(g18,g5)
FEATURE [PartDesign::Line] DatumLine012
  AttacherType = Attacher::AttachEngineLine
  AttachmentSupport = -> [Sketch194]
  Length = 24.0092
  MapMode = 29
  MinimumLength = 10
  Placement = pos=(4.3e-15,19.5,0) rot=(0,1,0;3.14159rad)
  ResizeMode = 0
  Support = -> [Sketch194]
  TreeRank = 3667
FEATURE [PartDesign::Revolution] Revolution010
  AddSubType = 0
  Angle = 360
  Axis = (2e-16,0,-1)
  Base = (4.3e-15,19.5,0)
  ClaimChildren = false
  Fit = 0
  FitJoin = 0
  InnerFit = 0
  InnerFitJoin = 0
  Linearize = true
  NewSolid = false
  Placement = pos=(0,0,0) rot=(0.57735,0.57735,0.57735;2.0944rad)
  Profile = -> Sketch194
  ReferenceAxis = -> DatumLine012
  Reversed = true
  Suppress = false
  TreeRank = 3668
  _ProfileBasedVersion = 1
FEATURE [Sketcher::SketchObject] Sketch195
  ArcFitTolerance = 1e-06
  AttachmentSupport = -> [Revolution010]
  ExternalGeometry = -> [Revolution010]
  FullyConstrained = true
  MapMode = 5
  Placement = pos=(-5.6e-15,1.1e-15,10.046) rot=(0.707107,0.707107,0;3.14159rad)
  Support = -> [Revolution010]
  TreeRank = 3669
  sketch-geometry (5):
    g0: Circle [constr] CenterX=19.5 CenterY=0 CenterZ=0 NormalX=0 NormalY=0 NormalZ=1 AngleXU=0 Radius=1.95
    g1: LineSegment StartX=18.254 StartY=1.5 StartZ=0 EndX=20.746 EndY=1.5 EndZ=0
    g2: LineSegment StartX=18.254 StartY=-1.5 StartZ=0 EndX=20.746 EndY=-1.5 EndZ=0
    g3: ArcOfCircle CenterX=19.5 CenterY=-1.1e-15 CenterZ=0 NormalX=0 NormalY=0 NormalZ=1 AngleXU=0 Radius=1.95 StartAngle=2.26396 EndAngle=4.01923
    g4: ArcOfCircle CenterX=19.5 CenterY=-4e-16 CenterZ=0 NormalX=0 NormalY=0 NormalZ=1 AngleXU=0 Radius=1.95 StartAngle=5.40555 EndAngle=7.16082
  constraints (16):
    c: Coincident(g0,g-3)
    c: Diameter(g0) = 3.9
    c: PointOnObject(g1,g0)
    c: PointOnObject(g1,g0)
    c: PointOnObject(g2,g0)
    c: PointOnObject(g2,g0)
    c: Horizontal(g2)
    c: Equal(g1,g2)
    c: Horizontal(g1)
    c: Coincident(g3,g1)
    c: Coincident(g3,g2)
    c: Vertical(g3,g-3)
    c: Coincident(g4,g1)
    c: Coincident(g4,g2)
    c: Vertical(g4,g3)
    c: DistanceY(g2,g1) = 3
FEATURE [PartDesign::Pocket] Pocket035
  AddSubType = 1
  BaseFeature = -> Revolution010
  CheckUpToFaceLimits = true
  ClaimChildren = false
  Fit = 0
  FitJoin = 0
  InnerFit = 0
  InnerFitJoin = 0
  InnerTaperAngle = 0
  InnerTaperAngleRev = 0
  Length = 5
  Length2 = 100
  Linearize = true
  NewSolid = false
  Placement = pos=(0,0,0) rot=(0.57735,0.57735,0.57735;2.0944rad)
  Profile = -> Sketch195
  Suppress = false
  TreeRank = 3670
  Type = 0
  _ProfileBasedVersion = 1
  _Version = 1
FEATURE [PartDesign::Body] Body112  label="thumbstick"
  AutoGroupSolids = false
  ClaimAllChildren = false
  ExportMode = 0
  Group = -> [ShapeBinder042,Sketch194,ShapeBinder043,DatumLine012,Revolution010,Sketch195,Pocket035]
  Origin = -> Origin138
  Tip = -> Pocket035
  TreeRank = 3663
  _ExportChildren = -> [ShapeBinder042,ShapeBinder043,DatumLine012,Revolution010,Pocket035]
  _GroupVersion = 1
FEATURE [App::Part] Part002  label="joystick guard001"
  ClaimAllChildren = false
  ExportMode = 1
  Group = -> [Body048,Body049,Body112]
  Origin = -> Origin080
  TreeRank = 1668
  _ExportChildren = -> [Body048,Body049,Body112]
  _GroupVersion = 1
FEATURE [PartDesign::Pocket] Pocket013
  AddSubType = 1
  BaseFeature = -> Pocket012
  CheckUpToFaceLimits = true
  ClaimChildren = false
  Fit = 0
  FitJoin = 0
  InnerFit = 0
  InnerFitJoin = 0
  InnerTaperAngle = 0
  InnerTaperAngleRev = 0
  Length = 20
  Length2 = 100
  Linearize = true
  NewSolid = false
  Profile = -> Sketch109
  Suppress = false
  TreeRank = 3692
  Type = 0
  _ProfileBasedVersion = 1
  _Version = 1
FEATURE [Sketcher::SketchObject] Sketch176
  ArcFitTolerance = 1e-06
  AttachmentSupport = -> [Pocket013]
  ExternalGeometry = -> [Pocket013]
  FullyConstrained = true
  MapMode = 5
  Placement = pos=(0,3,0) rot=(1,0,0;1.5708rad)
  Support = -> [Pocket013]
  TreeRank = 2987
  sketch-geometry (1):
    g0: Circle CenterX=-30 CenterY=17 CenterZ=0 NormalX=0 NormalY=0 NormalZ=1 AngleXU=0 Radius=13.5
  constraints (3):
    c: DistanceX(g0,g-3) = 16
    c: Radius(g0) = 13.5
    c: DistanceY(g-3,g0) = 3
FEATURE [PartDesign::Pocket] Pocket025
  AddSubType = 1
  BaseFeature = -> Pocket013
  CheckUpToFaceLimits = true
  ClaimChildren = false
  Fit = 0
  FitJoin = 0
  InnerFit = 0
  InnerFitJoin = 0
  InnerTaperAngle = 0
  InnerTaperAngleRev = 0
  Length = 10
  Length2 = 100
  Linearize = true
  NewSolid = false
  Profile = -> Sketch176
  Suppress = false
  TreeRank = 3694
  Type = 0
  _ProfileBasedVersion = 1
  _Version = 1
FEATURE [PartDesign::Chamfer] Chamfer005
  AddSubType = 0
  Angle = 45
  Base = -> Pocket025 [Edge26]
  BaseFeature = -> Pocket025
  ChamferType = 0
  FlipDirection = false
  NewSolid = false
  Size = 2
  Size2 = 1
  SupportTransform = false
  Suppress = false
  TreeRank = 3693
FEATURE [Sketcher::SketchObject] Sketch196
  ArcFitTolerance = 1e-06
  AttachmentSupport = -> [YZ_Plane127]
  FullyConstrained = true
  MapMode = 5
  Placement = pos=(0,0,0) rot=(0.57735,0.57735,0.57735;2.0944rad)
  Support = -> [YZ_Plane127]
  TreeRank = 3707
  sketch-geometry (1):
    g0: LineSegment StartX=0 StartY=0 StartZ=0 EndX=0 EndY=12 EndZ=0
  constraints (3):
    c: Coincident(g0,g-1)
    c: PointOnObject(g0,g-2)
    c: DistanceY(g0,g0) = 12
FEATURE [PartDesign::Plane] DatumPlane060
  AttachmentSupport = -> [Sketch196]
  Length = 53.98
  MapMode = 7
  MinimumLength = 10
  MinimumWidth = 10
  Placement = pos=(-2.7e-15,2.7e-15,12) rot=(0,1,0;3.14159rad)
  ResizeMode = 0
  Support = -> [Sketch196]
  TreeRank = 3708
  Width = 10
FEATURE [Sketcher::SketchObject] Sketch197
  ArcFitTolerance = 1e-06
  AttachmentSupport = -> [DatumPlane060]
  FullyConstrained = true
  MapMode = 5
  Placement = pos=(-2.7e-15,2.7e-15,12) rot=(0,1,0;3.14159rad)
  Support = -> [DatumPlane060]
  TreeRank = 3709
  expr: Constraints[12] = Spreadsheet.card_len
  sketch-geometry (5):
    g0: LineSegment StartX=-26.99 StartY=7 StartZ=0 EndX=0 EndY=7 EndZ=0
    g1: LineSegment StartX=0 StartY=7 StartZ=0 EndX=26.99 EndY=7 EndZ=0
    g2: LineSegment StartX=26.99 StartY=7 StartZ=0 EndX=26.99 EndY=-3 EndZ=0
    g3: LineSegment StartX=26.99 StartY=-3 StartZ=0 EndX=-26.99 EndY=-3 EndZ=0
    g4: LineSegment StartX=-26.99 StartY=-3 StartZ=0 EndX=-26.99 EndY=7 EndZ=0
  constraints (15):
    c: PointOnObject(g0,g-2)
    c: Horizontal(g0)
    c: Coincident(g1,g0)
    c: Horizontal(g1)
    c: Coincident(g2,g1)
    c: Coincident(g3,g2)
    c: Horizontal(g3)
    c: Coincident(g4,g3)
    c: Coincident(g4,g0)
    c: Vertical(g4)
    c: Equal(g0,g1)
    c: Vertical(g2)
    c: DistanceX(g3,g3) = 53.98
    c: DistanceY(g-1,g0) = 7
    c: DistanceY(g2,g2) = 10
FEATURE [PartDesign::Pad] Pad052
  AddSubType = 0
  AlongSketchNormal = false
  CheckUpToFaceLimits = true
  ClaimChildren = false
  Direction = (2e-16,-2e-16,-1)
  Fit = 0
  FitJoin = 0
  InnerFit = 0
  InnerFitJoin = 0
  InnerTaperAngle = 0
  InnerTaperAngleRev = 0
  Length = 1.2
  Length2 = 100
  Linearize = true
  NewSolid = false
  Placement = pos=(-2.7e-15,2.7e-15,12) rot=(0,1,0;3.14159rad)
  Profile = -> Sketch197
  Suppress = false
  TreeRank = 3710
  Type = 0
  _ProfileBasedVersion = 1
FEATURE [PartDesign::Body] Body113  label="card cutout 2"
  AutoGroupSolids = false
  ClaimAllChildren = false
  ExportMode = 0
  Group = -> [Sketch196,DatumPlane060,Sketch197,Pad052]
  Origin = -> Origin140
  Tip = -> Pad052
  TreeRank = 3716
  _ExportChildren = -> [Sketch196,DatumPlane060,Pad052]
  _GroupVersion = 1
FEATURE [PartDesign::SubShapeBinder] Reference019  label="Reference019(screw support w card slot)"
  BindCopyOnChange = 0
  BindMode = 0
  ClaimChildren = false
  FillStyle = 0
  Fuse = true
  MakeFace = true
  OffsetFill = false
  OffsetIntersection = false
  OffsetJoinType = 0
  OffsetOpenResult = false
  PartialLoad = false
  Relative = true
  Support = -> [Part007[Body105.]]
  TreeRank = 3712
  _Version = 8
FEATURE [PartDesign::Boolean] Boolean013
  BaseFeature = -> Clone042
  ClaimAllChildren = false
  ExportMode = 0
  Group = -> [Reference017,Reference018,Reference019,Reference020,Reference023,Reference024,Reference025,Reference026,Reference027,Reference028,Reference029,Reference030,Reference031,Reference048,Reference049,Reference050,Reference051,Reference053,Reference054,Reference058]
  NewSolid = false
  Suppress = false
  TreeRank = 3458
  Type = 0
  _ExportChildren = -> [Reference017,Reference018,Reference019,Reference020,Reference023,Reference024,Reference025,Reference026,Reference027,Reference028,Reference029,Reference030,Reference031,Reference048,Reference049,Reference050,Reference051,Reference053,Reference054,Reference058]
  _GroupVersion = 1
FEATURE [PartDesign::Boolean] Boolean014
  BaseFeature = -> Boolean013
  ClaimAllChildren = false
  ExportMode = 0
  Group = -> [Reference032,Reference033,Reference034,Reference035,Reference036,Reference037,Reference038,Reference040,Reference041,Reference042,Reference043,Reference044,Reference045,Reference046,Reference047,Reference052]
  NewSolid = false
  Suppress = false
  TreeRank = 3512
  Type = 1
  _ExportChildren = -> [Reference032,Reference033,Reference034,Reference035,Reference036,Reference037,Reference038,Reference040,Reference041,Reference042,Reference043,Reference044,Reference045,Reference046,Reference047,Reference052]
  _GroupVersion = 1
FEATURE [PartDesign::Boolean] Boolean016
  BaseFeature = -> Boolean014
  ClaimAllChildren = false
  ExportMode = 0
  Group = -> [Reference056]
  NewSolid = false
  Suppress = false
  TreeRank = 3575
  Type = 0
  _ExportChildren = -> [Reference056]
  _GroupVersion = 1
FEATURE [PartDesign::Fillet] Fillet025
  AddSubType = 0
  Base = -> Chamfer005 [Edge38,Edge41,Edge24]
  BaseFeature = -> Chamfer005
  NewSolid = false
  Radius = 1
  SupportTransform = false
  Suppress = false
  TreeRank = 3719
FEATURE [PartDesign::MultiTransform] MultiTransform003
  AddSubType = 0
  BaseFeature = -> Fillet025
  CopyShape = false
  NewSolid = false
  OriginalSubs = -> [Pad029,Pad030,Pocket025,Chamfer005,Fillet025,Pocket011,Chamfer007,Pocket012,Pocket013]
  Originals = -> [Pad029,Pad030,Pocket025,Chamfer005,Fillet025,Pocket011,Chamfer007,Pocket012,Pocket013]
  ParallelTransform = true
  SubTransform = true
  Suppress = false
  Transformations = -> [Mirrored005,LinearPattern004]
  TreeRank = 2396
  _Version = 3
FEATURE [PartDesign::Body] Body073  label="screw support001"
  AutoGroupSolids = false
  ClaimAllChildren = false
  ExportMode = 0
  Group = -> [Sketch103,Pad029,Pad030,Sketch129,Sketch104,Sketch107,Sketch108,Sketch109,Pocket011,Chamfer007,Pocket012,Pocket013,Sketch176,Pocket025,Chamfer005,Fillet025,MultiTransform003,Mirrored005,LinearPattern004]
  Origin = -> Origin083
  Tip = -> MultiTransform003
  TreeRank = 3363
  _ExportChildren = -> [Pad029,Pad030,Sketch104,Sketch107,Pocket011,Chamfer007,Pocket012,Pocket013,Pocket025,Chamfer005,Fillet025,MultiTransform003]
  _GroupVersion = 1
FEATURE [Part::Cut] Cut025
  Base = -> Body073
  Tool = -> Body079
  TreeRank = 3438
FEATURE [Part::MultiCommon] Common  label="screw support body"
  Shapes = -> [Cut025,Body078]
  TreeRank = 3715
FEATURE [PartDesign::FeatureBase] Clone044
  BaseFeature = -> Common
  NewSolid = false
  Suppress = false
  TreeRank = 3450
FEATURE [PartDesign::Boolean] Boolean012
  BaseFeature = -> Clone044
  ClaimAllChildren = false
  ExportMode = 0
  Group = -> [Reference016]
  NewSolid = false
  Suppress = false
  TreeRank = 3453
  Type = 1
  _ExportChildren = -> [Reference016]
  _GroupVersion = 1
FEATURE [PartDesign::Body] Body105  label="screw support w card slot"
  AutoGroupSolids = false
  BaseFeature = -> Common
  ClaimAllChildren = false
  ExportMode = 0
  Group = -> [Clone044,Boolean012]
  Origin = -> Origin127
  Tip = -> Boolean012
  TreeRank = 3452
  _ExportChildren = -> [Clone044,Boolean012]
  _GroupVersion = 1
FEATURE [App::Part] Part007  label="screw support"
  ClaimAllChildren = false
  ExportMode = 1
  Group = -> [Body078,Body079,Body073,Cut025,Common,Body105,Body113]
  Origin = -> Origin094
  TreeRank = 2036
  _ExportChildren = -> [Common,Body105,Body113]
  _GroupVersion = 1
FEATURE [PartDesign::FeatureBase] Clone051
  BaseFeature = -> Pipe017
  NewSolid = false
  Placement = pos=(-25,-51,0) rot=(0.57735,-0.57735,-0.57735;2.0944rad)
  Suppress = false
  TreeRank = 3729
FEATURE [PartDesign::Body] Body114  label="sidebar for print"
  AutoGroupSolids = false
  BaseFeature = -> Pipe017
  ClaimAllChildren = false
  ExportMode = 0
  Group = -> [Clone051]
  Origin = -> Origin141
  Tip = -> Clone051
  TreeRank = 3732
  _ExportChildren = -> [Clone051]
  _GroupVersion = 1
FEATURE [App::Part] Part014  label="side bars001"
  ClaimAllChildren = false
  ExportMode = 1
  Group = -> [Body097,Body114]
  Origin = -> Origin130
  TreeRank = 3548
  _ExportChildren = -> [Body097,Body114]
  _GroupVersion = 1
FEATURE [Sketcher::SketchObject] Sketch198
  ArcFitTolerance = 1e-06
  AttachmentSupport = -> [XY_Plane114]
  FullyConstrained = true
  MapMode = 5
  Support = -> [XY_Plane114]
  TreeRank = 3733
  sketch-geometry (1):
    g0: Circle CenterX=0 CenterY=-28 CenterZ=0 NormalX=0 NormalY=0 NormalZ=1 AngleXU=0 Radius=17.5
  constraints (3):
    c: PointOnObject(g0,g-2)
    c: DistanceY(g0,g-1) = 28
    c: Diameter(g0) = 35
FEATURE [PartDesign::Pocket] Pocket036
  AddSubType = 1
  BaseFeature = -> Boolean016
  CheckUpToFaceLimits = true
  ClaimChildren = false
  Fit = 0
  FitJoin = 0
  InnerFit = 0
  InnerFitJoin = 0
  InnerTaperAngle = 0
  InnerTaperAngleRev = 0
  Length = 12
  Length2 = 100
  Linearize = true
  NewSolid = false
  Profile = -> Sketch198
  Reversed = true
  Suppress = false
  TreeRank = 3734
  Type = 0
  _ProfileBasedVersion = 1
  _Version = 1
FEATURE [PartDesign::Body] Body103  label="top shell working"
  AutoGroupSolids = false
  BaseFeature = -> Cut005
  ClaimAllChildren = false
  ExportMode = 0
  Group = -> [Clone042,Boolean013,Boolean014,Boolean016,Sketch198,Pocket036]
  Origin = -> Origin122
  Tip = -> Pocket036
  TreeRank = 3415
  _ExportChildren = -> [Clone042,Boolean013,Boolean014,Boolean016,Pocket036]
  _GroupVersion = 1
FEATURE [PartDesign::FeatureBase] Clone052
  BaseFeature = -> Body053
  NewSolid = false
  Suppress = false
  TreeRank = 3762
FEATURE [PartDesign::Pad] Pad053
  AddSubType = 0
  AlongSketchNormal = false
  BaseFeature = -> Clone052
  CheckUpToFaceLimits = true
  ClaimChildren = false
  Direction = (0,0,-1)
  Fit = 0
  FitJoin = 0
  InnerFit = 0
  InnerFitJoin = 0
  InnerTaperAngle = 0
  InnerTaperAngleRev = 0
  Length = 10
  Length2 = 100
  Linearize = true
  NewSolid = false
  Profile = -> Clone052 [Face4]
  Suppress = false
  TreeRank = 3765
  Type = 0
  _ProfileBasedVersion = 1
FEATURE [PartDesign::Body] Body115  label="tail fin cutout001"
  AutoGroupSolids = false
  BaseFeature = -> Body053
  ClaimAllChildren = false
  ExportMode = 0
  Group = -> [Clone052,Pad053]
  Origin = -> Origin143
  Tip = -> Pad053
  TreeRank = 3764
  _ExportChildren = -> [Clone052,Pad053]
  _GroupVersion = 1
FEATURE [PartDesign::SubShapeBinder] Reference060  label="Reference060(tail fin cutout001)"
  BindCopyOnChange = 0
  BindMode = 0
  ClaimChildren = false
  FillStyle = 0
  Fuse = true
  MakeFace = true
  OffsetFill = false
  OffsetIntersection = false
  OffsetJoinType = 0
  OffsetOpenResult = false
  PartialLoad = false
  Relative = true
  Support = -> [Body115]
  TreeRank = 3766
  _Version = 8
FEATURE [PartDesign::Boolean] Boolean010
  BaseFeature = -> Fillet016
  ClaimAllChildren = false
  ExportMode = 0
  Group = -> [Reference060]
  NewSolid = false
  Suppress = false
  TreeRank = 3430
  Type = 1
  _ExportChildren = -> [Reference060]
  _GroupVersion = 1
FEATURE [PartDesign::Body] Body081  label="fin"
  AutoGroupSolids = false
  ClaimAllChildren = false
  ExportMode = 0
  Group = -> [Sketch121,Sketch122,Sketch123,DatumPlane038,Sketch124,Loft006,Sketch125,Mirrored,Pocket010,Mirrored004,Fillet016,Boolean010]
  Origin = -> Origin097
  Tip = -> Boolean010
  TreeRank = 2093
  _ExportChildren = -> [Sketch122,Sketch123,DatumPlane038,Loft006,Mirrored,Pocket010,Mirrored004,Fillet016,Boolean010]
  _GroupVersion = 1
FEATURE [App::Part] Part009  label="tail"
  ClaimAllChildren = false
  ExportMode = 1
  Group = -> [Body084,Body081,Body115]
  Origin = -> Origin096
  TreeRank = 2081
  _ExportChildren = -> [Body084,Body081,Body115]
  _GroupVersion = 1
FEATURE [PartDesign::FeatureBase] Clone041
  BaseFeature = -> Body081
  NewSolid = false
  Suppress = false
  TreeRank = 2783
FEATURE [PartDesign::Body] Body096  label="tail fin cutout"
  AutoGroupSolids = false
  BaseFeature = -> Body081
  ClaimAllChildren = false
  ExportMode = 0
  Group = -> [Clone041]
  Origin = -> Origin115
  Tip = -> Clone041
  TreeRank = 2785
  _ExportChildren = -> [Clone041]
  _GroupVersion = 1
FEATURE [Sketcher::SketchObject] Sketch199
  ArcFitTolerance = 1e-06
  AttachmentSupport = -> [Pad049]
  ExternalGeometry = -> [Sketch182]
  FullyConstrained = true
  MapMode = 5
  Placement = pos=(5.1e-15,-5.1e-15,-11.5) rot=(0,0,1;0rad)
  Support = -> [Pad049]
  TreeRank = 3767
  sketch-geometry (2):
    g0: Circle CenterX=-11.5 CenterY=-27.5 CenterZ=0 NormalX=0 NormalY=0 NormalZ=1 AngleXU=0 Radius=1.7
    g1: Circle CenterX=11.5 CenterY=-27.5 CenterZ=0 NormalX=0 NormalY=0 NormalZ=1 AngleXU=0 Radius=1.7
  constraints (4):
    c: Coincident(g0,g-3)
    c: Coincident(g1,g-4)
    c: Diameter(g0) = 3.4
    c: Diameter(g1) = 3.4
FEATURE [PartDesign::Pocket] Pocket037
  AddSubType = 1
  BaseFeature = -> Pad049
  CheckUpToFaceLimits = true
  ClaimChildren = false
  Fit = 0
  FitJoin = 0
  InnerFit = 0
  InnerFitJoin = 0
  InnerTaperAngle = 0
  InnerTaperAngleRev = 0
  Length = 4
  Length2 = 100
  Linearize = true
  NewSolid = false
  Placement = pos=(5.1e-15,-5.1e-15,-23) rot=(0,0,1;0rad)
  Profile = -> Sketch199
  Suppress = false
  TreeRank = 3768
  Type = 0
  _ProfileBasedVersion = 1
  _Version = 1
FEATURE [PartDesign::Boolean] Boolean004
  BaseFeature = -> Pocket037
  ClaimAllChildren = false
  ExportMode = 0
  Group = -> [Reference004]
  NewSolid = false
  Suppress = false
  TreeRank = 3085
  Type = 2
  _ExportChildren = -> [Reference004]
  _GroupVersion = 1
FEATURE [PartDesign::Body] Body102  label="usb port"
  AutoGroupSolids = false
  ClaimAllChildren = false
  ExportMode = 0
  Group = -> [Sketch181,DatumPlane058,Sketch182,Sketch183,Pad049,Sketch199,Pocket037,Boolean004]
  Origin = -> Origin121
  Tip = -> Boolean004
  TreeRank = 3038
  _ExportChildren = -> [Sketch181,DatumPlane058,Sketch183,Pad049,Pocket037,Boolean004]
  _GroupVersion = 1
FEATURE [App::Part] Part008  label="bottom"
  ClaimAllChildren = false
  ExportMode = 1
  Group = -> [Body080,Body001,Body003,Body092,Body093,Body096,Body100,Body101,Body102,Body099]
  Origin = -> Origin095
  TreeRank = 2061
  _ExportChildren = -> [Body080,Body001,Body003,Body092,Body093,Body096,Body100,Body101,Body102,Body099]
  _GroupVersion = 1
FEATURE [PartDesign::Body] Body069
  AutoGroupSolids = false
  ClaimAllChildren = false
  ExportMode = 0
  Group = -> [Sketch093,Import030,ShapeBinder026,Sketch094,Pipe013,Fillet012,Split,Split_i0]
  Origin = -> Origin075
  Tip = -> Split
  TreeRank = 1606
  _ExportChildren = -> [Import030,ShapeBinder026,Pipe013,Fillet012,Split]
  _GroupVersion = 1
FEATURE [PartDesign::Split] Split
  BaseFeature = -> Fillet012
  Fragment = false
  Mode = 0
  NewSolid = false
  Solids = -> [Split_i0]
  Suppress = false
  Tolerance = 0
  TreeRank = 1600
  _Version = 1
FEATURE [PartDesign::Solid] Split_i0
  Active = true
  Parent = -> Split
  TreeRank = 1601
FEATURE [Part::MultiCommon] Common003  label="middle groove support 2"
  Shapes = -> [Body069,Body070]
  TreeRank = 3152
FEATURE [App::Part] Part  label="top shell"
  ClaimAllChildren = false
  ExportMode = 1
  Group = -> [Body046,Part004,Part005,Part006,Part007,Part009,Body095,Part010,Part011,Part012,Body103,Body104,Body098]
  Origin = -> Origin078
  TreeRank = 1657
  _ExportChildren = -> [Body046,Part004,Part005,Part006,Part007,Part009,Body095,Part010,Part011,Part012,Body103,Body104,Body098]
  _GroupVersion = 1
FEATURE [App::Part] Part005  label="groove support"
  ClaimAllChildren = false
  ExportMode = 1
  Group = -> [Common003,Body069,Body070,Body071,Cut024,Body065,Body067,Common002,Body063,Body064,Body068]
  Origin = -> Origin086
  TreeRank = 1831
  _ExportChildren = -> [Common003,Body071,Cut024,Common002,Body068]
  _GroupVersion = 1
